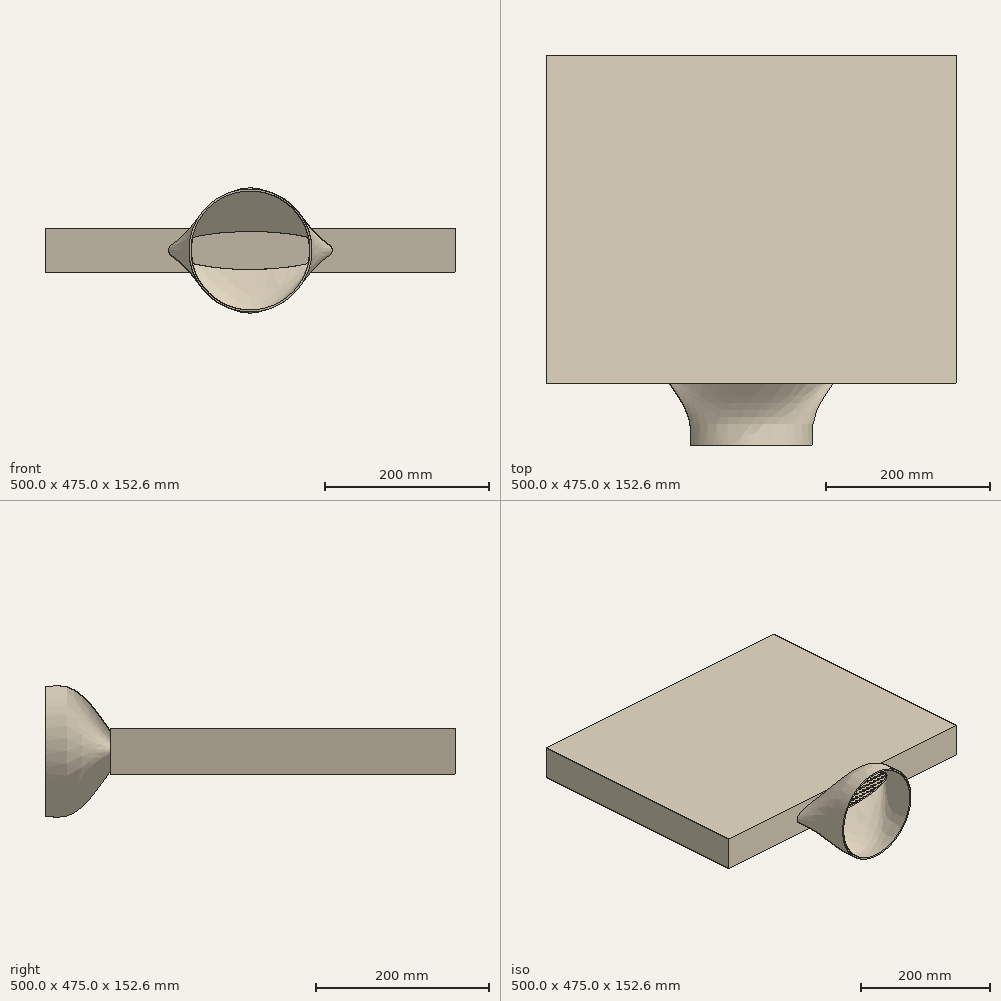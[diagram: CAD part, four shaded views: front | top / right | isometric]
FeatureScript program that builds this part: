
annotation { "Feature Type Name" : "Feature", "Feature Type Description" : "" }
export const myFeature = defineFeature(function(context is Context, id is Id, definition is map)
    precondition{}
    {
        {
            var Q0;
            Q0=qCreatedBy(makeId("Top.planeOp"),FACE);
            var sketch = newSketch(context, id + "F0", { "sketchPlane" : qUnion([Q0])});
            skLineSegment(sketch, "E0.bottom", {"start": v(-250, -200) * mm, "end": v(250, -200) * mm});
            skLineSegment(sketch, "E0.top", {"start": v(-250, 200) * mm, "end": v(250, 200) * mm});
            skLineSegment(sketch, "E0.left", {"start": v(-250, -200) * mm, "end": v(-250, 200) * mm});
            skLineSegment(sketch, "E0.right", {"start": v(250, -200) * mm, "end": v(250, 200) * mm});
            skPoint(sketch, "E0.middle", {"position": v(0, 0) * mm});
            skCircle(sketch, "E1", {"center": v(-243.5, 197) * mm, "radius": 2.5 * mm});
            skCircle(sketch, "E2.0.1.0", {"center": v(-243.5, 189) * mm, "radius": 2.5 * mm});
            skCircle(sketch, "E2.0.2.0", {"center": v(-243.5, 181) * mm, "radius": 2.5 * mm});
            skCircle(sketch, "E2.0.3.0", {"center": v(-243.5, 173) * mm, "radius": 2.5 * mm});
            skCircle(sketch, "E2.0.4.0", {"center": v(-243.5, 165) * mm, "radius": 2.5 * mm});
            skCircle(sketch, "E2.0.5.0", {"center": v(-243.5, 157) * mm, "radius": 2.5 * mm});
            skCircle(sketch, "E2.0.6.0", {"center": v(-243.5, 149) * mm, "radius": 2.5 * mm});
            skCircle(sketch, "E2.0.7.0", {"center": v(-243.5, 141) * mm, "radius": 2.5 * mm});
            skCircle(sketch, "E2.0.8.0", {"center": v(-243.5, 133) * mm, "radius": 2.5 * mm});
            skCircle(sketch, "E2.0.9.0", {"center": v(-243.5, 125) * mm, "radius": 2.5 * mm});
            skCircle(sketch, "E2.0.10.0", {"center": v(-243.5, 117) * mm, "radius": 2.5 * mm});
            skCircle(sketch, "E2.0.11.0", {"center": v(-243.5, 109) * mm, "radius": 2.5 * mm});
            skCircle(sketch, "E2.0.12.0", {"center": v(-243.5, 101) * mm, "radius": 2.5 * mm});
            skCircle(sketch, "E2.0.13.0", {"center": v(-243.5, 93) * mm, "radius": 2.5 * mm});
            skCircle(sketch, "E2.0.14.0", {"center": v(-243.5, 85) * mm, "radius": 2.5 * mm});
            skCircle(sketch, "E2.0.15.0", {"center": v(-243.5, 77) * mm, "radius": 2.5 * mm});
            skCircle(sketch, "E2.0.16.0", {"center": v(-243.5, 69) * mm, "radius": 2.5 * mm});
            skCircle(sketch, "E2.0.17.0", {"center": v(-243.5, 61) * mm, "radius": 2.5 * mm});
            skCircle(sketch, "E2.0.18.0", {"center": v(-243.5, 53) * mm, "radius": 2.5 * mm});
            skCircle(sketch, "E2.0.19.0", {"center": v(-243.5, 45) * mm, "radius": 2.5 * mm});
            skCircle(sketch, "E2.0.20.0", {"center": v(-243.5, 37) * mm, "radius": 2.5 * mm});
            skCircle(sketch, "E2.0.21.0", {"center": v(-243.5, 29) * mm, "radius": 2.5 * mm});
            skCircle(sketch, "E2.0.22.0", {"center": v(-243.5, 21) * mm, "radius": 2.5 * mm});
            skCircle(sketch, "E2.0.23.0", {"center": v(-243.5, 13) * mm, "radius": 2.5 * mm});
            skCircle(sketch, "E2.0.24.0", {"center": v(-243.5, 5) * mm, "radius": 2.5 * mm});
            skCircle(sketch, "E2.0.25.0", {"center": v(-243.5, -3) * mm, "radius": 2.5 * mm});
            skCircle(sketch, "E2.0.26.0", {"center": v(-243.5, -11) * mm, "radius": 2.5 * mm});
            skCircle(sketch, "E2.0.27.0", {"center": v(-243.5, -19) * mm, "radius": 2.5 * mm});
            skCircle(sketch, "E2.0.28.0", {"center": v(-243.5, -27) * mm, "radius": 2.5 * mm});
            skCircle(sketch, "E2.0.29.0", {"center": v(-243.5, -35) * mm, "radius": 2.5 * mm});
            skCircle(sketch, "E2.0.30.0", {"center": v(-243.5, -43) * mm, "radius": 2.5 * mm});
            skCircle(sketch, "E2.0.31.0", {"center": v(-243.5, -51) * mm, "radius": 2.5 * mm});
            skCircle(sketch, "E2.0.32.0", {"center": v(-243.5, -59) * mm, "radius": 2.5 * mm});
            skCircle(sketch, "E2.0.33.0", {"center": v(-243.5, -67) * mm, "radius": 2.5 * mm});
            skCircle(sketch, "E2.0.34.0", {"center": v(-243.5, -75) * mm, "radius": 2.5 * mm});
            skCircle(sketch, "E2.0.35.0", {"center": v(-243.5, -83) * mm, "radius": 2.5 * mm});
            skCircle(sketch, "E2.0.36.0", {"center": v(-243.5, -91) * mm, "radius": 2.5 * mm});
            skCircle(sketch, "E2.0.37.0", {"center": v(-243.5, -99) * mm, "radius": 2.5 * mm});
            skCircle(sketch, "E2.0.38.0", {"center": v(-243.5, -107) * mm, "radius": 2.5 * mm});
            skCircle(sketch, "E2.0.39.0", {"center": v(-243.5, -115) * mm, "radius": 2.5 * mm});
            skCircle(sketch, "E2.0.40.0", {"center": v(-243.5, -123) * mm, "radius": 2.5 * mm});
            skCircle(sketch, "E2.0.41.0", {"center": v(-243.5, -131) * mm, "radius": 2.5 * mm});
            skCircle(sketch, "E2.0.42.0", {"center": v(-243.5, -139) * mm, "radius": 2.5 * mm});
            skCircle(sketch, "E2.0.43.0", {"center": v(-243.5, -147) * mm, "radius": 2.5 * mm});
            skCircle(sketch, "E2.0.44.0", {"center": v(-243.5, -155) * mm, "radius": 2.5 * mm});
            skCircle(sketch, "E2.0.45.0", {"center": v(-243.5, -163) * mm, "radius": 2.5 * mm});
            skCircle(sketch, "E2.0.46.0", {"center": v(-243.5, -171) * mm, "radius": 2.5 * mm});
            skCircle(sketch, "E2.0.47.0", {"center": v(-243.5, -179) * mm, "radius": 2.5 * mm});
            skCircle(sketch, "E2.0.48.0", {"center": v(-243.5, -187) * mm, "radius": 2.5 * mm});
            skCircle(sketch, "E2.0.49.0", {"center": v(-243.5, -195) * mm, "radius": 2.5 * mm});
            skCircle(sketch, "E2.1.0.0", {"center": v(-235.5, 197) * mm, "radius": 2.5 * mm});
            skCircle(sketch, "E2.1.1.0", {"center": v(-235.5, 189) * mm, "radius": 2.5 * mm});
            skCircle(sketch, "E2.1.2.0", {"center": v(-235.5, 181) * mm, "radius": 2.5 * mm});
            skCircle(sketch, "E2.1.3.0", {"center": v(-235.5, 173) * mm, "radius": 2.5 * mm});
            skCircle(sketch, "E2.1.4.0", {"center": v(-235.5, 165) * mm, "radius": 2.5 * mm});
            skCircle(sketch, "E2.1.5.0", {"center": v(-235.5, 157) * mm, "radius": 2.5 * mm});
            skCircle(sketch, "E2.1.6.0", {"center": v(-235.5, 149) * mm, "radius": 2.5 * mm});
            skCircle(sketch, "E2.1.7.0", {"center": v(-235.5, 141) * mm, "radius": 2.5 * mm});
            skCircle(sketch, "E2.1.8.0", {"center": v(-235.5, 133) * mm, "radius": 2.5 * mm});
            skCircle(sketch, "E2.1.9.0", {"center": v(-235.5, 125) * mm, "radius": 2.5 * mm});
            skCircle(sketch, "E2.1.10.0", {"center": v(-235.5, 117) * mm, "radius": 2.5 * mm});
            skCircle(sketch, "E2.1.11.0", {"center": v(-235.5, 109) * mm, "radius": 2.5 * mm});
            skCircle(sketch, "E2.1.12.0", {"center": v(-235.5, 101) * mm, "radius": 2.5 * mm});
            skCircle(sketch, "E2.1.13.0", {"center": v(-235.5, 93) * mm, "radius": 2.5 * mm});
            skCircle(sketch, "E2.1.14.0", {"center": v(-235.5, 85) * mm, "radius": 2.5 * mm});
            skCircle(sketch, "E2.1.15.0", {"center": v(-235.5, 77) * mm, "radius": 2.5 * mm});
            skCircle(sketch, "E2.1.16.0", {"center": v(-235.5, 69) * mm, "radius": 2.5 * mm});
            skCircle(sketch, "E2.1.17.0", {"center": v(-235.5, 61) * mm, "radius": 2.5 * mm});
            skCircle(sketch, "E2.1.18.0", {"center": v(-235.5, 53) * mm, "radius": 2.5 * mm});
            skCircle(sketch, "E2.1.19.0", {"center": v(-235.5, 45) * mm, "radius": 2.5 * mm});
            skCircle(sketch, "E2.1.20.0", {"center": v(-235.5, 37) * mm, "radius": 2.5 * mm});
            skCircle(sketch, "E2.1.21.0", {"center": v(-235.5, 29) * mm, "radius": 2.5 * mm});
            skCircle(sketch, "E2.1.22.0", {"center": v(-235.5, 21) * mm, "radius": 2.5 * mm});
            skCircle(sketch, "E2.1.23.0", {"center": v(-235.5, 13) * mm, "radius": 2.5 * mm});
            skCircle(sketch, "E2.1.24.0", {"center": v(-235.5, 5) * mm, "radius": 2.5 * mm});
            skCircle(sketch, "E2.1.25.0", {"center": v(-235.5, -3) * mm, "radius": 2.5 * mm});
            skCircle(sketch, "E2.1.26.0", {"center": v(-235.5, -11) * mm, "radius": 2.5 * mm});
            skCircle(sketch, "E2.1.27.0", {"center": v(-235.5, -19) * mm, "radius": 2.5 * mm});
            skCircle(sketch, "E2.1.28.0", {"center": v(-235.5, -27) * mm, "radius": 2.5 * mm});
            skCircle(sketch, "E2.1.29.0", {"center": v(-235.5, -35) * mm, "radius": 2.5 * mm});
            skCircle(sketch, "E2.1.30.0", {"center": v(-235.5, -43) * mm, "radius": 2.5 * mm});
            skCircle(sketch, "E2.1.31.0", {"center": v(-235.5, -51) * mm, "radius": 2.5 * mm});
            skCircle(sketch, "E2.1.32.0", {"center": v(-235.5, -59) * mm, "radius": 2.5 * mm});
            skCircle(sketch, "E2.1.33.0", {"center": v(-235.5, -67) * mm, "radius": 2.5 * mm});
            skCircle(sketch, "E2.1.34.0", {"center": v(-235.5, -75) * mm, "radius": 2.5 * mm});
            skCircle(sketch, "E2.1.35.0", {"center": v(-235.5, -83) * mm, "radius": 2.5 * mm});
            skCircle(sketch, "E2.1.36.0", {"center": v(-235.5, -91) * mm, "radius": 2.5 * mm});
            skCircle(sketch, "E2.1.37.0", {"center": v(-235.5, -99) * mm, "radius": 2.5 * mm});
            skCircle(sketch, "E2.1.38.0", {"center": v(-235.5, -107) * mm, "radius": 2.5 * mm});
            skCircle(sketch, "E2.1.39.0", {"center": v(-235.5, -115) * mm, "radius": 2.5 * mm});
            skCircle(sketch, "E2.1.40.0", {"center": v(-235.5, -123) * mm, "radius": 2.5 * mm});
            skCircle(sketch, "E2.1.41.0", {"center": v(-235.5, -131) * mm, "radius": 2.5 * mm});
            skCircle(sketch, "E2.1.42.0", {"center": v(-235.5, -139) * mm, "radius": 2.5 * mm});
            skCircle(sketch, "E2.1.43.0", {"center": v(-235.5, -147) * mm, "radius": 2.5 * mm});
            skCircle(sketch, "E2.1.44.0", {"center": v(-235.5, -155) * mm, "radius": 2.5 * mm});
            skCircle(sketch, "E2.1.45.0", {"center": v(-235.5, -163) * mm, "radius": 2.5 * mm});
            skCircle(sketch, "E2.1.46.0", {"center": v(-235.5, -171) * mm, "radius": 2.5 * mm});
            skCircle(sketch, "E2.1.47.0", {"center": v(-235.5, -179) * mm, "radius": 2.5 * mm});
            skCircle(sketch, "E2.1.48.0", {"center": v(-235.5, -187) * mm, "radius": 2.5 * mm});
            skCircle(sketch, "E2.1.49.0", {"center": v(-235.5, -195) * mm, "radius": 2.5 * mm});
            skCircle(sketch, "E2.2.0.0", {"center": v(-227.5, 197) * mm, "radius": 2.5 * mm});
            skCircle(sketch, "E2.2.1.0", {"center": v(-227.5, 189) * mm, "radius": 2.5 * mm});
            skCircle(sketch, "E2.2.2.0", {"center": v(-227.5, 181) * mm, "radius": 2.5 * mm});
            skCircle(sketch, "E2.2.3.0", {"center": v(-227.5, 173) * mm, "radius": 2.5 * mm});
            skCircle(sketch, "E2.2.4.0", {"center": v(-227.5, 165) * mm, "radius": 2.5 * mm});
            skCircle(sketch, "E2.2.5.0", {"center": v(-227.5, 157) * mm, "radius": 2.5 * mm});
            skCircle(sketch, "E2.2.6.0", {"center": v(-227.5, 149) * mm, "radius": 2.5 * mm});
            skCircle(sketch, "E2.2.7.0", {"center": v(-227.5, 141) * mm, "radius": 2.5 * mm});
            skCircle(sketch, "E2.2.8.0", {"center": v(-227.5, 133) * mm, "radius": 2.5 * mm});
            skCircle(sketch, "E2.2.9.0", {"center": v(-227.5, 125) * mm, "radius": 2.5 * mm});
            skCircle(sketch, "E2.2.10.0", {"center": v(-227.5, 117) * mm, "radius": 2.5 * mm});
            skCircle(sketch, "E2.2.11.0", {"center": v(-227.5, 109) * mm, "radius": 2.5 * mm});
            skCircle(sketch, "E2.2.12.0", {"center": v(-227.5, 101) * mm, "radius": 2.5 * mm});
            skCircle(sketch, "E2.2.13.0", {"center": v(-227.5, 93) * mm, "radius": 2.5 * mm});
            skCircle(sketch, "E2.2.14.0", {"center": v(-227.5, 85) * mm, "radius": 2.5 * mm});
            skCircle(sketch, "E2.2.15.0", {"center": v(-227.5, 77) * mm, "radius": 2.5 * mm});
            skCircle(sketch, "E2.2.16.0", {"center": v(-227.5, 69) * mm, "radius": 2.5 * mm});
            skCircle(sketch, "E2.2.17.0", {"center": v(-227.5, 61) * mm, "radius": 2.5 * mm});
            skCircle(sketch, "E2.2.18.0", {"center": v(-227.5, 53) * mm, "radius": 2.5 * mm});
            skCircle(sketch, "E2.2.19.0", {"center": v(-227.5, 45) * mm, "radius": 2.5 * mm});
            skCircle(sketch, "E2.2.20.0", {"center": v(-227.5, 37) * mm, "radius": 2.5 * mm});
            skCircle(sketch, "E2.2.21.0", {"center": v(-227.5, 29) * mm, "radius": 2.5 * mm});
            skCircle(sketch, "E2.2.22.0", {"center": v(-227.5, 21) * mm, "radius": 2.5 * mm});
            skCircle(sketch, "E2.2.23.0", {"center": v(-227.5, 13) * mm, "radius": 2.5 * mm});
            skCircle(sketch, "E2.2.24.0", {"center": v(-227.5, 5) * mm, "radius": 2.5 * mm});
            skCircle(sketch, "E2.2.25.0", {"center": v(-227.5, -3) * mm, "radius": 2.5 * mm});
            skCircle(sketch, "E2.2.26.0", {"center": v(-227.5, -11) * mm, "radius": 2.5 * mm});
            skCircle(sketch, "E2.2.27.0", {"center": v(-227.5, -19) * mm, "radius": 2.5 * mm});
            skCircle(sketch, "E2.2.28.0", {"center": v(-227.5, -27) * mm, "radius": 2.5 * mm});
            skCircle(sketch, "E2.2.29.0", {"center": v(-227.5, -35) * mm, "radius": 2.5 * mm});
            skCircle(sketch, "E2.2.30.0", {"center": v(-227.5, -43) * mm, "radius": 2.5 * mm});
            skCircle(sketch, "E2.2.31.0", {"center": v(-227.5, -51) * mm, "radius": 2.5 * mm});
            skCircle(sketch, "E2.2.32.0", {"center": v(-227.5, -59) * mm, "radius": 2.5 * mm});
            skCircle(sketch, "E2.2.33.0", {"center": v(-227.5, -67) * mm, "radius": 2.5 * mm});
            skCircle(sketch, "E2.2.34.0", {"center": v(-227.5, -75) * mm, "radius": 2.5 * mm});
            skCircle(sketch, "E2.2.35.0", {"center": v(-227.5, -83) * mm, "radius": 2.5 * mm});
            skCircle(sketch, "E2.2.36.0", {"center": v(-227.5, -91) * mm, "radius": 2.5 * mm});
            skCircle(sketch, "E2.2.37.0", {"center": v(-227.5, -99) * mm, "radius": 2.5 * mm});
            skCircle(sketch, "E2.2.38.0", {"center": v(-227.5, -107) * mm, "radius": 2.5 * mm});
            skCircle(sketch, "E2.2.39.0", {"center": v(-227.5, -115) * mm, "radius": 2.5 * mm});
            skCircle(sketch, "E2.2.40.0", {"center": v(-227.5, -123) * mm, "radius": 2.5 * mm});
            skCircle(sketch, "E2.2.41.0", {"center": v(-227.5, -131) * mm, "radius": 2.5 * mm});
            skCircle(sketch, "E2.2.42.0", {"center": v(-227.5, -139) * mm, "radius": 2.5 * mm});
            skCircle(sketch, "E2.2.43.0", {"center": v(-227.5, -147) * mm, "radius": 2.5 * mm});
            skCircle(sketch, "E2.2.44.0", {"center": v(-227.5, -155) * mm, "radius": 2.5 * mm});
            skCircle(sketch, "E2.2.45.0", {"center": v(-227.5, -163) * mm, "radius": 2.5 * mm});
            skCircle(sketch, "E2.2.46.0", {"center": v(-227.5, -171) * mm, "radius": 2.5 * mm});
            skCircle(sketch, "E2.2.47.0", {"center": v(-227.5, -179) * mm, "radius": 2.5 * mm});
            skCircle(sketch, "E2.2.48.0", {"center": v(-227.5, -187) * mm, "radius": 2.5 * mm});
            skCircle(sketch, "E2.2.49.0", {"center": v(-227.5, -195) * mm, "radius": 2.5 * mm});
            skCircle(sketch, "E2.3.0.0", {"center": v(-219.5, 197) * mm, "radius": 2.5 * mm});
            skCircle(sketch, "E2.3.1.0", {"center": v(-219.5, 189) * mm, "radius": 2.5 * mm});
            skCircle(sketch, "E2.3.2.0", {"center": v(-219.5, 181) * mm, "radius": 2.5 * mm});
            skCircle(sketch, "E2.3.3.0", {"center": v(-219.5, 173) * mm, "radius": 2.5 * mm});
            skCircle(sketch, "E2.3.4.0", {"center": v(-219.5, 165) * mm, "radius": 2.5 * mm});
            skCircle(sketch, "E2.3.5.0", {"center": v(-219.5, 157) * mm, "radius": 2.5 * mm});
            skCircle(sketch, "E2.3.6.0", {"center": v(-219.5, 149) * mm, "radius": 2.5 * mm});
            skCircle(sketch, "E2.3.7.0", {"center": v(-219.5, 141) * mm, "radius": 2.5 * mm});
            skCircle(sketch, "E2.3.8.0", {"center": v(-219.5, 133) * mm, "radius": 2.5 * mm});
            skCircle(sketch, "E2.3.9.0", {"center": v(-219.5, 125) * mm, "radius": 2.5 * mm});
            skCircle(sketch, "E2.3.10.0", {"center": v(-219.5, 117) * mm, "radius": 2.5 * mm});
            skCircle(sketch, "E2.3.11.0", {"center": v(-219.5, 109) * mm, "radius": 2.5 * mm});
            skCircle(sketch, "E2.3.12.0", {"center": v(-219.5, 101) * mm, "radius": 2.5 * mm});
            skCircle(sketch, "E2.3.13.0", {"center": v(-219.5, 93) * mm, "radius": 2.5 * mm});
            skCircle(sketch, "E2.3.14.0", {"center": v(-219.5, 85) * mm, "radius": 2.5 * mm});
            skCircle(sketch, "E2.3.15.0", {"center": v(-219.5, 77) * mm, "radius": 2.5 * mm});
            skCircle(sketch, "E2.3.16.0", {"center": v(-219.5, 69) * mm, "radius": 2.5 * mm});
            skCircle(sketch, "E2.3.17.0", {"center": v(-219.5, 61) * mm, "radius": 2.5 * mm});
            skCircle(sketch, "E2.3.18.0", {"center": v(-219.5, 53) * mm, "radius": 2.5 * mm});
            skCircle(sketch, "E2.3.19.0", {"center": v(-219.5, 45) * mm, "radius": 2.5 * mm});
            skCircle(sketch, "E2.3.20.0", {"center": v(-219.5, 37) * mm, "radius": 2.5 * mm});
            skCircle(sketch, "E2.3.21.0", {"center": v(-219.5, 29) * mm, "radius": 2.5 * mm});
            skCircle(sketch, "E2.3.22.0", {"center": v(-219.5, 21) * mm, "radius": 2.5 * mm});
            skCircle(sketch, "E2.3.23.0", {"center": v(-219.5, 13) * mm, "radius": 2.5 * mm});
            skCircle(sketch, "E2.3.24.0", {"center": v(-219.5, 5) * mm, "radius": 2.5 * mm});
            skCircle(sketch, "E2.3.25.0", {"center": v(-219.5, -3) * mm, "radius": 2.5 * mm});
            skCircle(sketch, "E2.3.26.0", {"center": v(-219.5, -11) * mm, "radius": 2.5 * mm});
            skCircle(sketch, "E2.3.27.0", {"center": v(-219.5, -19) * mm, "radius": 2.5 * mm});
            skCircle(sketch, "E2.3.28.0", {"center": v(-219.5, -27) * mm, "radius": 2.5 * mm});
            skCircle(sketch, "E2.3.29.0", {"center": v(-219.5, -35) * mm, "radius": 2.5 * mm});
            skCircle(sketch, "E2.3.30.0", {"center": v(-219.5, -43) * mm, "radius": 2.5 * mm});
            skCircle(sketch, "E2.3.31.0", {"center": v(-219.5, -51) * mm, "radius": 2.5 * mm});
            skCircle(sketch, "E2.3.32.0", {"center": v(-219.5, -59) * mm, "radius": 2.5 * mm});
            skCircle(sketch, "E2.3.33.0", {"center": v(-219.5, -67) * mm, "radius": 2.5 * mm});
            skCircle(sketch, "E2.3.34.0", {"center": v(-219.5, -75) * mm, "radius": 2.5 * mm});
            skCircle(sketch, "E2.3.35.0", {"center": v(-219.5, -83) * mm, "radius": 2.5 * mm});
            skCircle(sketch, "E2.3.36.0", {"center": v(-219.5, -91) * mm, "radius": 2.5 * mm});
            skCircle(sketch, "E2.3.37.0", {"center": v(-219.5, -99) * mm, "radius": 2.5 * mm});
            skCircle(sketch, "E2.3.38.0", {"center": v(-219.5, -107) * mm, "radius": 2.5 * mm});
            skCircle(sketch, "E2.3.39.0", {"center": v(-219.5, -115) * mm, "radius": 2.5 * mm});
            skCircle(sketch, "E2.3.40.0", {"center": v(-219.5, -123) * mm, "radius": 2.5 * mm});
            skCircle(sketch, "E2.3.41.0", {"center": v(-219.5, -131) * mm, "radius": 2.5 * mm});
            skCircle(sketch, "E2.3.42.0", {"center": v(-219.5, -139) * mm, "radius": 2.5 * mm});
            skCircle(sketch, "E2.3.43.0", {"center": v(-219.5, -147) * mm, "radius": 2.5 * mm});
            skCircle(sketch, "E2.3.44.0", {"center": v(-219.5, -155) * mm, "radius": 2.5 * mm});
            skCircle(sketch, "E2.3.45.0", {"center": v(-219.5, -163) * mm, "radius": 2.5 * mm});
            skCircle(sketch, "E2.3.46.0", {"center": v(-219.5, -171) * mm, "radius": 2.5 * mm});
            skCircle(sketch, "E2.3.47.0", {"center": v(-219.5, -179) * mm, "radius": 2.5 * mm});
            skCircle(sketch, "E2.3.48.0", {"center": v(-219.5, -187) * mm, "radius": 2.5 * mm});
            skCircle(sketch, "E2.3.49.0", {"center": v(-219.5, -195) * mm, "radius": 2.5 * mm});
            skCircle(sketch, "E2.4.0.0", {"center": v(-211.5, 197) * mm, "radius": 2.5 * mm});
            skCircle(sketch, "E2.4.1.0", {"center": v(-211.5, 189) * mm, "radius": 2.5 * mm});
            skCircle(sketch, "E2.4.2.0", {"center": v(-211.5, 181) * mm, "radius": 2.5 * mm});
            skCircle(sketch, "E2.4.3.0", {"center": v(-211.5, 173) * mm, "radius": 2.5 * mm});
            skCircle(sketch, "E2.4.4.0", {"center": v(-211.5, 165) * mm, "radius": 2.5 * mm});
            skCircle(sketch, "E2.4.5.0", {"center": v(-211.5, 157) * mm, "radius": 2.5 * mm});
            skCircle(sketch, "E2.4.6.0", {"center": v(-211.5, 149) * mm, "radius": 2.5 * mm});
            skCircle(sketch, "E2.4.7.0", {"center": v(-211.5, 141) * mm, "radius": 2.5 * mm});
            skCircle(sketch, "E2.4.8.0", {"center": v(-211.5, 133) * mm, "radius": 2.5 * mm});
            skCircle(sketch, "E2.4.9.0", {"center": v(-211.5, 125) * mm, "radius": 2.5 * mm});
            skCircle(sketch, "E2.4.10.0", {"center": v(-211.5, 117) * mm, "radius": 2.5 * mm});
            skCircle(sketch, "E2.4.11.0", {"center": v(-211.5, 109) * mm, "radius": 2.5 * mm});
            skCircle(sketch, "E2.4.12.0", {"center": v(-211.5, 101) * mm, "radius": 2.5 * mm});
            skCircle(sketch, "E2.4.13.0", {"center": v(-211.5, 93) * mm, "radius": 2.5 * mm});
            skCircle(sketch, "E2.4.14.0", {"center": v(-211.5, 85) * mm, "radius": 2.5 * mm});
            skCircle(sketch, "E2.4.15.0", {"center": v(-211.5, 77) * mm, "radius": 2.5 * mm});
            skCircle(sketch, "E2.4.16.0", {"center": v(-211.5, 69) * mm, "radius": 2.5 * mm});
            skCircle(sketch, "E2.4.17.0", {"center": v(-211.5, 61) * mm, "radius": 2.5 * mm});
            skCircle(sketch, "E2.4.18.0", {"center": v(-211.5, 53) * mm, "radius": 2.5 * mm});
            skCircle(sketch, "E2.4.19.0", {"center": v(-211.5, 45) * mm, "radius": 2.5 * mm});
            skCircle(sketch, "E2.4.20.0", {"center": v(-211.5, 37) * mm, "radius": 2.5 * mm});
            skCircle(sketch, "E2.4.21.0", {"center": v(-211.5, 29) * mm, "radius": 2.5 * mm});
            skCircle(sketch, "E2.4.22.0", {"center": v(-211.5, 21) * mm, "radius": 2.5 * mm});
            skCircle(sketch, "E2.4.23.0", {"center": v(-211.5, 13) * mm, "radius": 2.5 * mm});
            skCircle(sketch, "E2.4.24.0", {"center": v(-211.5, 5) * mm, "radius": 2.5 * mm});
            skCircle(sketch, "E2.4.25.0", {"center": v(-211.5, -3) * mm, "radius": 2.5 * mm});
            skCircle(sketch, "E2.4.26.0", {"center": v(-211.5, -11) * mm, "radius": 2.5 * mm});
            skCircle(sketch, "E2.4.27.0", {"center": v(-211.5, -19) * mm, "radius": 2.5 * mm});
            skCircle(sketch, "E2.4.28.0", {"center": v(-211.5, -27) * mm, "radius": 2.5 * mm});
            skCircle(sketch, "E2.4.29.0", {"center": v(-211.5, -35) * mm, "radius": 2.5 * mm});
            skCircle(sketch, "E2.4.30.0", {"center": v(-211.5, -43) * mm, "radius": 2.5 * mm});
            skCircle(sketch, "E2.4.31.0", {"center": v(-211.5, -51) * mm, "radius": 2.5 * mm});
            skCircle(sketch, "E2.4.32.0", {"center": v(-211.5, -59) * mm, "radius": 2.5 * mm});
            skCircle(sketch, "E2.4.33.0", {"center": v(-211.5, -67) * mm, "radius": 2.5 * mm});
            skCircle(sketch, "E2.4.34.0", {"center": v(-211.5, -75) * mm, "radius": 2.5 * mm});
            skCircle(sketch, "E2.4.35.0", {"center": v(-211.5, -83) * mm, "radius": 2.5 * mm});
            skCircle(sketch, "E2.4.36.0", {"center": v(-211.5, -91) * mm, "radius": 2.5 * mm});
            skCircle(sketch, "E2.4.37.0", {"center": v(-211.5, -99) * mm, "radius": 2.5 * mm});
            skCircle(sketch, "E2.4.38.0", {"center": v(-211.5, -107) * mm, "radius": 2.5 * mm});
            skCircle(sketch, "E2.4.39.0", {"center": v(-211.5, -115) * mm, "radius": 2.5 * mm});
            skCircle(sketch, "E2.4.40.0", {"center": v(-211.5, -123) * mm, "radius": 2.5 * mm});
            skCircle(sketch, "E2.4.41.0", {"center": v(-211.5, -131) * mm, "radius": 2.5 * mm});
            skCircle(sketch, "E2.4.42.0", {"center": v(-211.5, -139) * mm, "radius": 2.5 * mm});
            skCircle(sketch, "E2.4.43.0", {"center": v(-211.5, -147) * mm, "radius": 2.5 * mm});
            skCircle(sketch, "E2.4.44.0", {"center": v(-211.5, -155) * mm, "radius": 2.5 * mm});
            skCircle(sketch, "E2.4.45.0", {"center": v(-211.5, -163) * mm, "radius": 2.5 * mm});
            skCircle(sketch, "E2.4.46.0", {"center": v(-211.5, -171) * mm, "radius": 2.5 * mm});
            skCircle(sketch, "E2.4.47.0", {"center": v(-211.5, -179) * mm, "radius": 2.5 * mm});
            skCircle(sketch, "E2.4.48.0", {"center": v(-211.5, -187) * mm, "radius": 2.5 * mm});
            skCircle(sketch, "E2.4.49.0", {"center": v(-211.5, -195) * mm, "radius": 2.5 * mm});
            skCircle(sketch, "E2.5.0.0", {"center": v(-203.5, 197) * mm, "radius": 2.5 * mm});
            skCircle(sketch, "E2.5.1.0", {"center": v(-203.5, 189) * mm, "radius": 2.5 * mm});
            skCircle(sketch, "E2.5.2.0", {"center": v(-203.5, 181) * mm, "radius": 2.5 * mm});
            skCircle(sketch, "E2.5.3.0", {"center": v(-203.5, 173) * mm, "radius": 2.5 * mm});
            skCircle(sketch, "E2.5.4.0", {"center": v(-203.5, 165) * mm, "radius": 2.5 * mm});
            skCircle(sketch, "E2.5.5.0", {"center": v(-203.5, 157) * mm, "radius": 2.5 * mm});
            skCircle(sketch, "E2.5.6.0", {"center": v(-203.5, 149) * mm, "radius": 2.5 * mm});
            skCircle(sketch, "E2.5.7.0", {"center": v(-203.5, 141) * mm, "radius": 2.5 * mm});
            skCircle(sketch, "E2.5.8.0", {"center": v(-203.5, 133) * mm, "radius": 2.5 * mm});
            skCircle(sketch, "E2.5.9.0", {"center": v(-203.5, 125) * mm, "radius": 2.5 * mm});
            skCircle(sketch, "E2.5.10.0", {"center": v(-203.5, 117) * mm, "radius": 2.5 * mm});
            skCircle(sketch, "E2.5.11.0", {"center": v(-203.5, 109) * mm, "radius": 2.5 * mm});
            skCircle(sketch, "E2.5.12.0", {"center": v(-203.5, 101) * mm, "radius": 2.5 * mm});
            skCircle(sketch, "E2.5.13.0", {"center": v(-203.5, 93) * mm, "radius": 2.5 * mm});
            skCircle(sketch, "E2.5.14.0", {"center": v(-203.5, 85) * mm, "radius": 2.5 * mm});
            skCircle(sketch, "E2.5.15.0", {"center": v(-203.5, 77) * mm, "radius": 2.5 * mm});
            skCircle(sketch, "E2.5.16.0", {"center": v(-203.5, 69) * mm, "radius": 2.5 * mm});
            skCircle(sketch, "E2.5.17.0", {"center": v(-203.5, 61) * mm, "radius": 2.5 * mm});
            skCircle(sketch, "E2.5.18.0", {"center": v(-203.5, 53) * mm, "radius": 2.5 * mm});
            skCircle(sketch, "E2.5.19.0", {"center": v(-203.5, 45) * mm, "radius": 2.5 * mm});
            skCircle(sketch, "E2.5.20.0", {"center": v(-203.5, 37) * mm, "radius": 2.5 * mm});
            skCircle(sketch, "E2.5.21.0", {"center": v(-203.5, 29) * mm, "radius": 2.5 * mm});
            skCircle(sketch, "E2.5.22.0", {"center": v(-203.5, 21) * mm, "radius": 2.5 * mm});
            skCircle(sketch, "E2.5.23.0", {"center": v(-203.5, 13) * mm, "radius": 2.5 * mm});
            skCircle(sketch, "E2.5.24.0", {"center": v(-203.5, 5) * mm, "radius": 2.5 * mm});
            skCircle(sketch, "E2.5.25.0", {"center": v(-203.5, -3) * mm, "radius": 2.5 * mm});
            skCircle(sketch, "E2.5.26.0", {"center": v(-203.5, -11) * mm, "radius": 2.5 * mm});
            skCircle(sketch, "E2.5.27.0", {"center": v(-203.5, -19) * mm, "radius": 2.5 * mm});
            skCircle(sketch, "E2.5.28.0", {"center": v(-203.5, -27) * mm, "radius": 2.5 * mm});
            skCircle(sketch, "E2.5.29.0", {"center": v(-203.5, -35) * mm, "radius": 2.5 * mm});
            skCircle(sketch, "E2.5.30.0", {"center": v(-203.5, -43) * mm, "radius": 2.5 * mm});
            skCircle(sketch, "E2.5.31.0", {"center": v(-203.5, -51) * mm, "radius": 2.5 * mm});
            skCircle(sketch, "E2.5.32.0", {"center": v(-203.5, -59) * mm, "radius": 2.5 * mm});
            skCircle(sketch, "E2.5.33.0", {"center": v(-203.5, -67) * mm, "radius": 2.5 * mm});
            skCircle(sketch, "E2.5.34.0", {"center": v(-203.5, -75) * mm, "radius": 2.5 * mm});
            skCircle(sketch, "E2.5.35.0", {"center": v(-203.5, -83) * mm, "radius": 2.5 * mm});
            skCircle(sketch, "E2.5.36.0", {"center": v(-203.5, -91) * mm, "radius": 2.5 * mm});
            skCircle(sketch, "E2.5.37.0", {"center": v(-203.5, -99) * mm, "radius": 2.5 * mm});
            skCircle(sketch, "E2.5.38.0", {"center": v(-203.5, -107) * mm, "radius": 2.5 * mm});
            skCircle(sketch, "E2.5.39.0", {"center": v(-203.5, -115) * mm, "radius": 2.5 * mm});
            skCircle(sketch, "E2.5.40.0", {"center": v(-203.5, -123) * mm, "radius": 2.5 * mm});
            skCircle(sketch, "E2.5.41.0", {"center": v(-203.5, -131) * mm, "radius": 2.5 * mm});
            skCircle(sketch, "E2.5.42.0", {"center": v(-203.5, -139) * mm, "radius": 2.5 * mm});
            skCircle(sketch, "E2.5.43.0", {"center": v(-203.5, -147) * mm, "radius": 2.5 * mm});
            skCircle(sketch, "E2.5.44.0", {"center": v(-203.5, -155) * mm, "radius": 2.5 * mm});
            skCircle(sketch, "E2.5.45.0", {"center": v(-203.5, -163) * mm, "radius": 2.5 * mm});
            skCircle(sketch, "E2.5.46.0", {"center": v(-203.5, -171) * mm, "radius": 2.5 * mm});
            skCircle(sketch, "E2.5.47.0", {"center": v(-203.5, -179) * mm, "radius": 2.5 * mm});
            skCircle(sketch, "E2.5.48.0", {"center": v(-203.5, -187) * mm, "radius": 2.5 * mm});
            skCircle(sketch, "E2.5.49.0", {"center": v(-203.5, -195) * mm, "radius": 2.5 * mm});
            skCircle(sketch, "E2.6.0.0", {"center": v(-195.5, 197) * mm, "radius": 2.5 * mm});
            skCircle(sketch, "E2.6.1.0", {"center": v(-195.5, 189) * mm, "radius": 2.5 * mm});
            skCircle(sketch, "E2.6.2.0", {"center": v(-195.5, 181) * mm, "radius": 2.5 * mm});
            skCircle(sketch, "E2.6.3.0", {"center": v(-195.5, 173) * mm, "radius": 2.5 * mm});
            skCircle(sketch, "E2.6.4.0", {"center": v(-195.5, 165) * mm, "radius": 2.5 * mm});
            skCircle(sketch, "E2.6.5.0", {"center": v(-195.5, 157) * mm, "radius": 2.5 * mm});
            skCircle(sketch, "E2.6.6.0", {"center": v(-195.5, 149) * mm, "radius": 2.5 * mm});
            skCircle(sketch, "E2.6.7.0", {"center": v(-195.5, 141) * mm, "radius": 2.5 * mm});
            skCircle(sketch, "E2.6.8.0", {"center": v(-195.5, 133) * mm, "radius": 2.5 * mm});
            skCircle(sketch, "E2.6.9.0", {"center": v(-195.5, 125) * mm, "radius": 2.5 * mm});
            skCircle(sketch, "E2.6.10.0", {"center": v(-195.5, 117) * mm, "radius": 2.5 * mm});
            skCircle(sketch, "E2.6.11.0", {"center": v(-195.5, 109) * mm, "radius": 2.5 * mm});
            skCircle(sketch, "E2.6.12.0", {"center": v(-195.5, 101) * mm, "radius": 2.5 * mm});
            skCircle(sketch, "E2.6.13.0", {"center": v(-195.5, 93) * mm, "radius": 2.5 * mm});
            skCircle(sketch, "E2.6.14.0", {"center": v(-195.5, 85) * mm, "radius": 2.5 * mm});
            skCircle(sketch, "E2.6.15.0", {"center": v(-195.5, 77) * mm, "radius": 2.5 * mm});
            skCircle(sketch, "E2.6.16.0", {"center": v(-195.5, 69) * mm, "radius": 2.5 * mm});
            skCircle(sketch, "E2.6.17.0", {"center": v(-195.5, 61) * mm, "radius": 2.5 * mm});
            skCircle(sketch, "E2.6.18.0", {"center": v(-195.5, 53) * mm, "radius": 2.5 * mm});
            skCircle(sketch, "E2.6.19.0", {"center": v(-195.5, 45) * mm, "radius": 2.5 * mm});
            skCircle(sketch, "E2.6.20.0", {"center": v(-195.5, 37) * mm, "radius": 2.5 * mm});
            skCircle(sketch, "E2.6.21.0", {"center": v(-195.5, 29) * mm, "radius": 2.5 * mm});
            skCircle(sketch, "E2.6.22.0", {"center": v(-195.5, 21) * mm, "radius": 2.5 * mm});
            skCircle(sketch, "E2.6.23.0", {"center": v(-195.5, 13) * mm, "radius": 2.5 * mm});
            skCircle(sketch, "E2.6.24.0", {"center": v(-195.5, 5) * mm, "radius": 2.5 * mm});
            skCircle(sketch, "E2.6.25.0", {"center": v(-195.5, -3) * mm, "radius": 2.5 * mm});
            skCircle(sketch, "E2.6.26.0", {"center": v(-195.5, -11) * mm, "radius": 2.5 * mm});
            skCircle(sketch, "E2.6.27.0", {"center": v(-195.5, -19) * mm, "radius": 2.5 * mm});
            skCircle(sketch, "E2.6.28.0", {"center": v(-195.5, -27) * mm, "radius": 2.5 * mm});
            skCircle(sketch, "E2.6.29.0", {"center": v(-195.5, -35) * mm, "radius": 2.5 * mm});
            skCircle(sketch, "E2.6.30.0", {"center": v(-195.5, -43) * mm, "radius": 2.5 * mm});
            skCircle(sketch, "E2.6.31.0", {"center": v(-195.5, -51) * mm, "radius": 2.5 * mm});
            skCircle(sketch, "E2.6.32.0", {"center": v(-195.5, -59) * mm, "radius": 2.5 * mm});
            skCircle(sketch, "E2.6.33.0", {"center": v(-195.5, -67) * mm, "radius": 2.5 * mm});
            skCircle(sketch, "E2.6.34.0", {"center": v(-195.5, -75) * mm, "radius": 2.5 * mm});
            skCircle(sketch, "E2.6.35.0", {"center": v(-195.5, -83) * mm, "radius": 2.5 * mm});
            skCircle(sketch, "E2.6.36.0", {"center": v(-195.5, -91) * mm, "radius": 2.5 * mm});
            skCircle(sketch, "E2.6.37.0", {"center": v(-195.5, -99) * mm, "radius": 2.5 * mm});
            skCircle(sketch, "E2.6.38.0", {"center": v(-195.5, -107) * mm, "radius": 2.5 * mm});
            skCircle(sketch, "E2.6.39.0", {"center": v(-195.5, -115) * mm, "radius": 2.5 * mm});
            skCircle(sketch, "E2.6.40.0", {"center": v(-195.5, -123) * mm, "radius": 2.5 * mm});
            skCircle(sketch, "E2.6.41.0", {"center": v(-195.5, -131) * mm, "radius": 2.5 * mm});
            skCircle(sketch, "E2.6.42.0", {"center": v(-195.5, -139) * mm, "radius": 2.5 * mm});
            skCircle(sketch, "E2.6.43.0", {"center": v(-195.5, -147) * mm, "radius": 2.5 * mm});
            skCircle(sketch, "E2.6.44.0", {"center": v(-195.5, -155) * mm, "radius": 2.5 * mm});
            skCircle(sketch, "E2.6.45.0", {"center": v(-195.5, -163) * mm, "radius": 2.5 * mm});
            skCircle(sketch, "E2.6.46.0", {"center": v(-195.5, -171) * mm, "radius": 2.5 * mm});
            skCircle(sketch, "E2.6.47.0", {"center": v(-195.5, -179) * mm, "radius": 2.5 * mm});
            skCircle(sketch, "E2.6.48.0", {"center": v(-195.5, -187) * mm, "radius": 2.5 * mm});
            skCircle(sketch, "E2.6.49.0", {"center": v(-195.5, -195) * mm, "radius": 2.5 * mm});
            skCircle(sketch, "E2.7.0.0", {"center": v(-187.5, 197) * mm, "radius": 2.5 * mm});
            skCircle(sketch, "E2.7.1.0", {"center": v(-187.5, 189) * mm, "radius": 2.5 * mm});
            skCircle(sketch, "E2.7.2.0", {"center": v(-187.5, 181) * mm, "radius": 2.5 * mm});
            skCircle(sketch, "E2.7.3.0", {"center": v(-187.5, 173) * mm, "radius": 2.5 * mm});
            skCircle(sketch, "E2.7.4.0", {"center": v(-187.5, 165) * mm, "radius": 2.5 * mm});
            skCircle(sketch, "E2.7.5.0", {"center": v(-187.5, 157) * mm, "radius": 2.5 * mm});
            skCircle(sketch, "E2.7.6.0", {"center": v(-187.5, 149) * mm, "radius": 2.5 * mm});
            skCircle(sketch, "E2.7.7.0", {"center": v(-187.5, 141) * mm, "radius": 2.5 * mm});
            skCircle(sketch, "E2.7.8.0", {"center": v(-187.5, 133) * mm, "radius": 2.5 * mm});
            skCircle(sketch, "E2.7.9.0", {"center": v(-187.5, 125) * mm, "radius": 2.5 * mm});
            skCircle(sketch, "E2.7.10.0", {"center": v(-187.5, 117) * mm, "radius": 2.5 * mm});
            skCircle(sketch, "E2.7.11.0", {"center": v(-187.5, 109) * mm, "radius": 2.5 * mm});
            skCircle(sketch, "E2.7.12.0", {"center": v(-187.5, 101) * mm, "radius": 2.5 * mm});
            skCircle(sketch, "E2.7.13.0", {"center": v(-187.5, 93) * mm, "radius": 2.5 * mm});
            skCircle(sketch, "E2.7.14.0", {"center": v(-187.5, 85) * mm, "radius": 2.5 * mm});
            skCircle(sketch, "E2.7.15.0", {"center": v(-187.5, 77) * mm, "radius": 2.5 * mm});
            skCircle(sketch, "E2.7.16.0", {"center": v(-187.5, 69) * mm, "radius": 2.5 * mm});
            skCircle(sketch, "E2.7.17.0", {"center": v(-187.5, 61) * mm, "radius": 2.5 * mm});
            skCircle(sketch, "E2.7.18.0", {"center": v(-187.5, 53) * mm, "radius": 2.5 * mm});
            skCircle(sketch, "E2.7.19.0", {"center": v(-187.5, 45) * mm, "radius": 2.5 * mm});
            skCircle(sketch, "E2.7.20.0", {"center": v(-187.5, 37) * mm, "radius": 2.5 * mm});
            skCircle(sketch, "E2.7.21.0", {"center": v(-187.5, 29) * mm, "radius": 2.5 * mm});
            skCircle(sketch, "E2.7.22.0", {"center": v(-187.5, 21) * mm, "radius": 2.5 * mm});
            skCircle(sketch, "E2.7.23.0", {"center": v(-187.5, 13) * mm, "radius": 2.5 * mm});
            skCircle(sketch, "E2.7.24.0", {"center": v(-187.5, 5) * mm, "radius": 2.5 * mm});
            skCircle(sketch, "E2.7.25.0", {"center": v(-187.5, -3) * mm, "radius": 2.5 * mm});
            skCircle(sketch, "E2.7.26.0", {"center": v(-187.5, -11) * mm, "radius": 2.5 * mm});
            skCircle(sketch, "E2.7.27.0", {"center": v(-187.5, -19) * mm, "radius": 2.5 * mm});
            skCircle(sketch, "E2.7.28.0", {"center": v(-187.5, -27) * mm, "radius": 2.5 * mm});
            skCircle(sketch, "E2.7.29.0", {"center": v(-187.5, -35) * mm, "radius": 2.5 * mm});
            skCircle(sketch, "E2.7.30.0", {"center": v(-187.5, -43) * mm, "radius": 2.5 * mm});
            skCircle(sketch, "E2.7.31.0", {"center": v(-187.5, -51) * mm, "radius": 2.5 * mm});
            skCircle(sketch, "E2.7.32.0", {"center": v(-187.5, -59) * mm, "radius": 2.5 * mm});
            skCircle(sketch, "E2.7.33.0", {"center": v(-187.5, -67) * mm, "radius": 2.5 * mm});
            skCircle(sketch, "E2.7.34.0", {"center": v(-187.5, -75) * mm, "radius": 2.5 * mm});
            skCircle(sketch, "E2.7.35.0", {"center": v(-187.5, -83) * mm, "radius": 2.5 * mm});
            skCircle(sketch, "E2.7.36.0", {"center": v(-187.5, -91) * mm, "radius": 2.5 * mm});
            skCircle(sketch, "E2.7.37.0", {"center": v(-187.5, -99) * mm, "radius": 2.5 * mm});
            skCircle(sketch, "E2.7.38.0", {"center": v(-187.5, -107) * mm, "radius": 2.5 * mm});
            skCircle(sketch, "E2.7.39.0", {"center": v(-187.5, -115) * mm, "radius": 2.5 * mm});
            skCircle(sketch, "E2.7.40.0", {"center": v(-187.5, -123) * mm, "radius": 2.5 * mm});
            skCircle(sketch, "E2.7.41.0", {"center": v(-187.5, -131) * mm, "radius": 2.5 * mm});
            skCircle(sketch, "E2.7.42.0", {"center": v(-187.5, -139) * mm, "radius": 2.5 * mm});
            skCircle(sketch, "E2.7.43.0", {"center": v(-187.5, -147) * mm, "radius": 2.5 * mm});
            skCircle(sketch, "E2.7.44.0", {"center": v(-187.5, -155) * mm, "radius": 2.5 * mm});
            skCircle(sketch, "E2.7.45.0", {"center": v(-187.5, -163) * mm, "radius": 2.5 * mm});
            skCircle(sketch, "E2.7.46.0", {"center": v(-187.5, -171) * mm, "radius": 2.5 * mm});
            skCircle(sketch, "E2.7.47.0", {"center": v(-187.5, -179) * mm, "radius": 2.5 * mm});
            skCircle(sketch, "E2.7.48.0", {"center": v(-187.5, -187) * mm, "radius": 2.5 * mm});
            skCircle(sketch, "E2.7.49.0", {"center": v(-187.5, -195) * mm, "radius": 2.5 * mm});
            skCircle(sketch, "E2.8.0.0", {"center": v(-179.5, 197) * mm, "radius": 2.5 * mm});
            skCircle(sketch, "E2.8.1.0", {"center": v(-179.5, 189) * mm, "radius": 2.5 * mm});
            skCircle(sketch, "E2.8.2.0", {"center": v(-179.5, 181) * mm, "radius": 2.5 * mm});
            skCircle(sketch, "E2.8.3.0", {"center": v(-179.5, 173) * mm, "radius": 2.5 * mm});
            skCircle(sketch, "E2.8.4.0", {"center": v(-179.5, 165) * mm, "radius": 2.5 * mm});
            skCircle(sketch, "E2.8.5.0", {"center": v(-179.5, 157) * mm, "radius": 2.5 * mm});
            skCircle(sketch, "E2.8.6.0", {"center": v(-179.5, 149) * mm, "radius": 2.5 * mm});
            skCircle(sketch, "E2.8.7.0", {"center": v(-179.5, 141) * mm, "radius": 2.5 * mm});
            skCircle(sketch, "E2.8.8.0", {"center": v(-179.5, 133) * mm, "radius": 2.5 * mm});
            skCircle(sketch, "E2.8.9.0", {"center": v(-179.5, 125) * mm, "radius": 2.5 * mm});
            skCircle(sketch, "E2.8.10.0", {"center": v(-179.5, 117) * mm, "radius": 2.5 * mm});
            skCircle(sketch, "E2.8.11.0", {"center": v(-179.5, 109) * mm, "radius": 2.5 * mm});
            skCircle(sketch, "E2.8.12.0", {"center": v(-179.5, 101) * mm, "radius": 2.5 * mm});
            skCircle(sketch, "E2.8.13.0", {"center": v(-179.5, 93) * mm, "radius": 2.5 * mm});
            skCircle(sketch, "E2.8.14.0", {"center": v(-179.5, 85) * mm, "radius": 2.5 * mm});
            skCircle(sketch, "E2.8.15.0", {"center": v(-179.5, 77) * mm, "radius": 2.5 * mm});
            skCircle(sketch, "E2.8.16.0", {"center": v(-179.5, 69) * mm, "radius": 2.5 * mm});
            skCircle(sketch, "E2.8.17.0", {"center": v(-179.5, 61) * mm, "radius": 2.5 * mm});
            skCircle(sketch, "E2.8.18.0", {"center": v(-179.5, 53) * mm, "radius": 2.5 * mm});
            skCircle(sketch, "E2.8.19.0", {"center": v(-179.5, 45) * mm, "radius": 2.5 * mm});
            skCircle(sketch, "E2.8.20.0", {"center": v(-179.5, 37) * mm, "radius": 2.5 * mm});
            skCircle(sketch, "E2.8.21.0", {"center": v(-179.5, 29) * mm, "radius": 2.5 * mm});
            skCircle(sketch, "E2.8.22.0", {"center": v(-179.5, 21) * mm, "radius": 2.5 * mm});
            skCircle(sketch, "E2.8.23.0", {"center": v(-179.5, 13) * mm, "radius": 2.5 * mm});
            skCircle(sketch, "E2.8.24.0", {"center": v(-179.5, 5) * mm, "radius": 2.5 * mm});
            skCircle(sketch, "E2.8.25.0", {"center": v(-179.5, -3) * mm, "radius": 2.5 * mm});
            skCircle(sketch, "E2.8.26.0", {"center": v(-179.5, -11) * mm, "radius": 2.5 * mm});
            skCircle(sketch, "E2.8.27.0", {"center": v(-179.5, -19) * mm, "radius": 2.5 * mm});
            skCircle(sketch, "E2.8.28.0", {"center": v(-179.5, -27) * mm, "radius": 2.5 * mm});
            skCircle(sketch, "E2.8.29.0", {"center": v(-179.5, -35) * mm, "radius": 2.5 * mm});
            skCircle(sketch, "E2.8.30.0", {"center": v(-179.5, -43) * mm, "radius": 2.5 * mm});
            skCircle(sketch, "E2.8.31.0", {"center": v(-179.5, -51) * mm, "radius": 2.5 * mm});
            skCircle(sketch, "E2.8.32.0", {"center": v(-179.5, -59) * mm, "radius": 2.5 * mm});
            skCircle(sketch, "E2.8.33.0", {"center": v(-179.5, -67) * mm, "radius": 2.5 * mm});
            skCircle(sketch, "E2.8.34.0", {"center": v(-179.5, -75) * mm, "radius": 2.5 * mm});
            skCircle(sketch, "E2.8.35.0", {"center": v(-179.5, -83) * mm, "radius": 2.5 * mm});
            skCircle(sketch, "E2.8.36.0", {"center": v(-179.5, -91) * mm, "radius": 2.5 * mm});
            skCircle(sketch, "E2.8.37.0", {"center": v(-179.5, -99) * mm, "radius": 2.5 * mm});
            skCircle(sketch, "E2.8.38.0", {"center": v(-179.5, -107) * mm, "radius": 2.5 * mm});
            skCircle(sketch, "E2.8.39.0", {"center": v(-179.5, -115) * mm, "radius": 2.5 * mm});
            skCircle(sketch, "E2.8.40.0", {"center": v(-179.5, -123) * mm, "radius": 2.5 * mm});
            skCircle(sketch, "E2.8.41.0", {"center": v(-179.5, -131) * mm, "radius": 2.5 * mm});
            skCircle(sketch, "E2.8.42.0", {"center": v(-179.5, -139) * mm, "radius": 2.5 * mm});
            skCircle(sketch, "E2.8.43.0", {"center": v(-179.5, -147) * mm, "radius": 2.5 * mm});
            skCircle(sketch, "E2.8.44.0", {"center": v(-179.5, -155) * mm, "radius": 2.5 * mm});
            skCircle(sketch, "E2.8.45.0", {"center": v(-179.5, -163) * mm, "radius": 2.5 * mm});
            skCircle(sketch, "E2.8.46.0", {"center": v(-179.5, -171) * mm, "radius": 2.5 * mm});
            skCircle(sketch, "E2.8.47.0", {"center": v(-179.5, -179) * mm, "radius": 2.5 * mm});
            skCircle(sketch, "E2.8.48.0", {"center": v(-179.5, -187) * mm, "radius": 2.5 * mm});
            skCircle(sketch, "E2.8.49.0", {"center": v(-179.5, -195) * mm, "radius": 2.5 * mm});
            skCircle(sketch, "E2.9.0.0", {"center": v(-171.5, 197) * mm, "radius": 2.5 * mm});
            skCircle(sketch, "E2.9.1.0", {"center": v(-171.5, 189) * mm, "radius": 2.5 * mm});
            skCircle(sketch, "E2.9.2.0", {"center": v(-171.5, 181) * mm, "radius": 2.5 * mm});
            skCircle(sketch, "E2.9.3.0", {"center": v(-171.5, 173) * mm, "radius": 2.5 * mm});
            skCircle(sketch, "E2.9.4.0", {"center": v(-171.5, 165) * mm, "radius": 2.5 * mm});
            skCircle(sketch, "E2.9.5.0", {"center": v(-171.5, 157) * mm, "radius": 2.5 * mm});
            skCircle(sketch, "E2.9.6.0", {"center": v(-171.5, 149) * mm, "radius": 2.5 * mm});
            skCircle(sketch, "E2.9.7.0", {"center": v(-171.5, 141) * mm, "radius": 2.5 * mm});
            skCircle(sketch, "E2.9.8.0", {"center": v(-171.5, 133) * mm, "radius": 2.5 * mm});
            skCircle(sketch, "E2.9.9.0", {"center": v(-171.5, 125) * mm, "radius": 2.5 * mm});
            skCircle(sketch, "E2.9.10.0", {"center": v(-171.5, 117) * mm, "radius": 2.5 * mm});
            skCircle(sketch, "E2.9.11.0", {"center": v(-171.5, 109) * mm, "radius": 2.5 * mm});
            skCircle(sketch, "E2.9.12.0", {"center": v(-171.5, 101) * mm, "radius": 2.5 * mm});
            skCircle(sketch, "E2.9.13.0", {"center": v(-171.5, 93) * mm, "radius": 2.5 * mm});
            skCircle(sketch, "E2.9.14.0", {"center": v(-171.5, 85) * mm, "radius": 2.5 * mm});
            skCircle(sketch, "E2.9.15.0", {"center": v(-171.5, 77) * mm, "radius": 2.5 * mm});
            skCircle(sketch, "E2.9.16.0", {"center": v(-171.5, 69) * mm, "radius": 2.5 * mm});
            skCircle(sketch, "E2.9.17.0", {"center": v(-171.5, 61) * mm, "radius": 2.5 * mm});
            skCircle(sketch, "E2.9.18.0", {"center": v(-171.5, 53) * mm, "radius": 2.5 * mm});
            skCircle(sketch, "E2.9.19.0", {"center": v(-171.5, 45) * mm, "radius": 2.5 * mm});
            skCircle(sketch, "E2.9.20.0", {"center": v(-171.5, 37) * mm, "radius": 2.5 * mm});
            skCircle(sketch, "E2.9.21.0", {"center": v(-171.5, 29) * mm, "radius": 2.5 * mm});
            skCircle(sketch, "E2.9.22.0", {"center": v(-171.5, 21) * mm, "radius": 2.5 * mm});
            skCircle(sketch, "E2.9.23.0", {"center": v(-171.5, 13) * mm, "radius": 2.5 * mm});
            skCircle(sketch, "E2.9.24.0", {"center": v(-171.5, 5) * mm, "radius": 2.5 * mm});
            skCircle(sketch, "E2.9.25.0", {"center": v(-171.5, -3) * mm, "radius": 2.5 * mm});
            skCircle(sketch, "E2.9.26.0", {"center": v(-171.5, -11) * mm, "radius": 2.5 * mm});
            skCircle(sketch, "E2.9.27.0", {"center": v(-171.5, -19) * mm, "radius": 2.5 * mm});
            skCircle(sketch, "E2.9.28.0", {"center": v(-171.5, -27) * mm, "radius": 2.5 * mm});
            skCircle(sketch, "E2.9.29.0", {"center": v(-171.5, -35) * mm, "radius": 2.5 * mm});
            skCircle(sketch, "E2.9.30.0", {"center": v(-171.5, -43) * mm, "radius": 2.5 * mm});
            skCircle(sketch, "E2.9.31.0", {"center": v(-171.5, -51) * mm, "radius": 2.5 * mm});
            skCircle(sketch, "E2.9.32.0", {"center": v(-171.5, -59) * mm, "radius": 2.5 * mm});
            skCircle(sketch, "E2.9.33.0", {"center": v(-171.5, -67) * mm, "radius": 2.5 * mm});
            skCircle(sketch, "E2.9.34.0", {"center": v(-171.5, -75) * mm, "radius": 2.5 * mm});
            skCircle(sketch, "E2.9.35.0", {"center": v(-171.5, -83) * mm, "radius": 2.5 * mm});
            skCircle(sketch, "E2.9.36.0", {"center": v(-171.5, -91) * mm, "radius": 2.5 * mm});
            skCircle(sketch, "E2.9.37.0", {"center": v(-171.5, -99) * mm, "radius": 2.5 * mm});
            skCircle(sketch, "E2.9.38.0", {"center": v(-171.5, -107) * mm, "radius": 2.5 * mm});
            skCircle(sketch, "E2.9.39.0", {"center": v(-171.5, -115) * mm, "radius": 2.5 * mm});
            skCircle(sketch, "E2.9.40.0", {"center": v(-171.5, -123) * mm, "radius": 2.5 * mm});
            skCircle(sketch, "E2.9.41.0", {"center": v(-171.5, -131) * mm, "radius": 2.5 * mm});
            skCircle(sketch, "E2.9.42.0", {"center": v(-171.5, -139) * mm, "radius": 2.5 * mm});
            skCircle(sketch, "E2.9.43.0", {"center": v(-171.5, -147) * mm, "radius": 2.5 * mm});
            skCircle(sketch, "E2.9.44.0", {"center": v(-171.5, -155) * mm, "radius": 2.5 * mm});
            skCircle(sketch, "E2.9.45.0", {"center": v(-171.5, -163) * mm, "radius": 2.5 * mm});
            skCircle(sketch, "E2.9.46.0", {"center": v(-171.5, -171) * mm, "radius": 2.5 * mm});
            skCircle(sketch, "E2.9.47.0", {"center": v(-171.5, -179) * mm, "radius": 2.5 * mm});
            skCircle(sketch, "E2.9.48.0", {"center": v(-171.5, -187) * mm, "radius": 2.5 * mm});
            skCircle(sketch, "E2.9.49.0", {"center": v(-171.5, -195) * mm, "radius": 2.5 * mm});
            skCircle(sketch, "E2.10.0.0", {"center": v(-163.5, 197) * mm, "radius": 2.5 * mm});
            skCircle(sketch, "E2.10.1.0", {"center": v(-163.5, 189) * mm, "radius": 2.5 * mm});
            skCircle(sketch, "E2.10.2.0", {"center": v(-163.5, 181) * mm, "radius": 2.5 * mm});
            skCircle(sketch, "E2.10.3.0", {"center": v(-163.5, 173) * mm, "radius": 2.5 * mm});
            skCircle(sketch, "E2.10.4.0", {"center": v(-163.5, 165) * mm, "radius": 2.5 * mm});
            skCircle(sketch, "E2.10.5.0", {"center": v(-163.5, 157) * mm, "radius": 2.5 * mm});
            skCircle(sketch, "E2.10.6.0", {"center": v(-163.5, 149) * mm, "radius": 2.5 * mm});
            skCircle(sketch, "E2.10.7.0", {"center": v(-163.5, 141) * mm, "radius": 2.5 * mm});
            skCircle(sketch, "E2.10.8.0", {"center": v(-163.5, 133) * mm, "radius": 2.5 * mm});
            skCircle(sketch, "E2.10.9.0", {"center": v(-163.5, 125) * mm, "radius": 2.5 * mm});
            skCircle(sketch, "E2.10.10.0", {"center": v(-163.5, 117) * mm, "radius": 2.5 * mm});
            skCircle(sketch, "E2.10.11.0", {"center": v(-163.5, 109) * mm, "radius": 2.5 * mm});
            skCircle(sketch, "E2.10.12.0", {"center": v(-163.5, 101) * mm, "radius": 2.5 * mm});
            skCircle(sketch, "E2.10.13.0", {"center": v(-163.5, 93) * mm, "radius": 2.5 * mm});
            skCircle(sketch, "E2.10.14.0", {"center": v(-163.5, 85) * mm, "radius": 2.5 * mm});
            skCircle(sketch, "E2.10.15.0", {"center": v(-163.5, 77) * mm, "radius": 2.5 * mm});
            skCircle(sketch, "E2.10.16.0", {"center": v(-163.5, 69) * mm, "radius": 2.5 * mm});
            skCircle(sketch, "E2.10.17.0", {"center": v(-163.5, 61) * mm, "radius": 2.5 * mm});
            skCircle(sketch, "E2.10.18.0", {"center": v(-163.5, 53) * mm, "radius": 2.5 * mm});
            skCircle(sketch, "E2.10.19.0", {"center": v(-163.5, 45) * mm, "radius": 2.5 * mm});
            skCircle(sketch, "E2.10.20.0", {"center": v(-163.5, 37) * mm, "radius": 2.5 * mm});
            skCircle(sketch, "E2.10.21.0", {"center": v(-163.5, 29) * mm, "radius": 2.5 * mm});
            skCircle(sketch, "E2.10.22.0", {"center": v(-163.5, 21) * mm, "radius": 2.5 * mm});
            skCircle(sketch, "E2.10.23.0", {"center": v(-163.5, 13) * mm, "radius": 2.5 * mm});
            skCircle(sketch, "E2.10.24.0", {"center": v(-163.5, 5) * mm, "radius": 2.5 * mm});
            skCircle(sketch, "E2.10.25.0", {"center": v(-163.5, -3) * mm, "radius": 2.5 * mm});
            skCircle(sketch, "E2.10.26.0", {"center": v(-163.5, -11) * mm, "radius": 2.5 * mm});
            skCircle(sketch, "E2.10.27.0", {"center": v(-163.5, -19) * mm, "radius": 2.5 * mm});
            skCircle(sketch, "E2.10.28.0", {"center": v(-163.5, -27) * mm, "radius": 2.5 * mm});
            skCircle(sketch, "E2.10.29.0", {"center": v(-163.5, -35) * mm, "radius": 2.5 * mm});
            skCircle(sketch, "E2.10.30.0", {"center": v(-163.5, -43) * mm, "radius": 2.5 * mm});
            skCircle(sketch, "E2.10.31.0", {"center": v(-163.5, -51) * mm, "radius": 2.5 * mm});
            skCircle(sketch, "E2.10.32.0", {"center": v(-163.5, -59) * mm, "radius": 2.5 * mm});
            skCircle(sketch, "E2.10.33.0", {"center": v(-163.5, -67) * mm, "radius": 2.5 * mm});
            skCircle(sketch, "E2.10.34.0", {"center": v(-163.5, -75) * mm, "radius": 2.5 * mm});
            skCircle(sketch, "E2.10.35.0", {"center": v(-163.5, -83) * mm, "radius": 2.5 * mm});
            skCircle(sketch, "E2.10.36.0", {"center": v(-163.5, -91) * mm, "radius": 2.5 * mm});
            skCircle(sketch, "E2.10.37.0", {"center": v(-163.5, -99) * mm, "radius": 2.5 * mm});
            skCircle(sketch, "E2.10.38.0", {"center": v(-163.5, -107) * mm, "radius": 2.5 * mm});
            skCircle(sketch, "E2.10.39.0", {"center": v(-163.5, -115) * mm, "radius": 2.5 * mm});
            skCircle(sketch, "E2.10.40.0", {"center": v(-163.5, -123) * mm, "radius": 2.5 * mm});
            skCircle(sketch, "E2.10.41.0", {"center": v(-163.5, -131) * mm, "radius": 2.5 * mm});
            skCircle(sketch, "E2.10.42.0", {"center": v(-163.5, -139) * mm, "radius": 2.5 * mm});
            skCircle(sketch, "E2.10.43.0", {"center": v(-163.5, -147) * mm, "radius": 2.5 * mm});
            skCircle(sketch, "E2.10.44.0", {"center": v(-163.5, -155) * mm, "radius": 2.5 * mm});
            skCircle(sketch, "E2.10.45.0", {"center": v(-163.5, -163) * mm, "radius": 2.5 * mm});
            skCircle(sketch, "E2.10.46.0", {"center": v(-163.5, -171) * mm, "radius": 2.5 * mm});
            skCircle(sketch, "E2.10.47.0", {"center": v(-163.5, -179) * mm, "radius": 2.5 * mm});
            skCircle(sketch, "E2.10.48.0", {"center": v(-163.5, -187) * mm, "radius": 2.5 * mm});
            skCircle(sketch, "E2.10.49.0", {"center": v(-163.5, -195) * mm, "radius": 2.5 * mm});
            skCircle(sketch, "E2.11.0.0", {"center": v(-155.5, 197) * mm, "radius": 2.5 * mm});
            skCircle(sketch, "E2.11.1.0", {"center": v(-155.5, 189) * mm, "radius": 2.5 * mm});
            skCircle(sketch, "E2.11.2.0", {"center": v(-155.5, 181) * mm, "radius": 2.5 * mm});
            skCircle(sketch, "E2.11.3.0", {"center": v(-155.5, 173) * mm, "radius": 2.5 * mm});
            skCircle(sketch, "E2.11.4.0", {"center": v(-155.5, 165) * mm, "radius": 2.5 * mm});
            skCircle(sketch, "E2.11.5.0", {"center": v(-155.5, 157) * mm, "radius": 2.5 * mm});
            skCircle(sketch, "E2.11.6.0", {"center": v(-155.5, 149) * mm, "radius": 2.5 * mm});
            skCircle(sketch, "E2.11.7.0", {"center": v(-155.5, 141) * mm, "radius": 2.5 * mm});
            skCircle(sketch, "E2.11.8.0", {"center": v(-155.5, 133) * mm, "radius": 2.5 * mm});
            skCircle(sketch, "E2.11.9.0", {"center": v(-155.5, 125) * mm, "radius": 2.5 * mm});
            skCircle(sketch, "E2.11.10.0", {"center": v(-155.5, 117) * mm, "radius": 2.5 * mm});
            skCircle(sketch, "E2.11.11.0", {"center": v(-155.5, 109) * mm, "radius": 2.5 * mm});
            skCircle(sketch, "E2.11.12.0", {"center": v(-155.5, 101) * mm, "radius": 2.5 * mm});
            skCircle(sketch, "E2.11.13.0", {"center": v(-155.5, 93) * mm, "radius": 2.5 * mm});
            skCircle(sketch, "E2.11.14.0", {"center": v(-155.5, 85) * mm, "radius": 2.5 * mm});
            skCircle(sketch, "E2.11.15.0", {"center": v(-155.5, 77) * mm, "radius": 2.5 * mm});
            skCircle(sketch, "E2.11.16.0", {"center": v(-155.5, 69) * mm, "radius": 2.5 * mm});
            skCircle(sketch, "E2.11.17.0", {"center": v(-155.5, 61) * mm, "radius": 2.5 * mm});
            skCircle(sketch, "E2.11.18.0", {"center": v(-155.5, 53) * mm, "radius": 2.5 * mm});
            skCircle(sketch, "E2.11.19.0", {"center": v(-155.5, 45) * mm, "radius": 2.5 * mm});
            skCircle(sketch, "E2.11.20.0", {"center": v(-155.5, 37) * mm, "radius": 2.5 * mm});
            skCircle(sketch, "E2.11.21.0", {"center": v(-155.5, 29) * mm, "radius": 2.5 * mm});
            skCircle(sketch, "E2.11.22.0", {"center": v(-155.5, 21) * mm, "radius": 2.5 * mm});
            skCircle(sketch, "E2.11.23.0", {"center": v(-155.5, 13) * mm, "radius": 2.5 * mm});
            skCircle(sketch, "E2.11.24.0", {"center": v(-155.5, 5) * mm, "radius": 2.5 * mm});
            skCircle(sketch, "E2.11.25.0", {"center": v(-155.5, -3) * mm, "radius": 2.5 * mm});
            skCircle(sketch, "E2.11.26.0", {"center": v(-155.5, -11) * mm, "radius": 2.5 * mm});
            skCircle(sketch, "E2.11.27.0", {"center": v(-155.5, -19) * mm, "radius": 2.5 * mm});
            skCircle(sketch, "E2.11.28.0", {"center": v(-155.5, -27) * mm, "radius": 2.5 * mm});
            skCircle(sketch, "E2.11.29.0", {"center": v(-155.5, -35) * mm, "radius": 2.5 * mm});
            skCircle(sketch, "E2.11.30.0", {"center": v(-155.5, -43) * mm, "radius": 2.5 * mm});
            skCircle(sketch, "E2.11.31.0", {"center": v(-155.5, -51) * mm, "radius": 2.5 * mm});
            skCircle(sketch, "E2.11.32.0", {"center": v(-155.5, -59) * mm, "radius": 2.5 * mm});
            skCircle(sketch, "E2.11.33.0", {"center": v(-155.5, -67) * mm, "radius": 2.5 * mm});
            skCircle(sketch, "E2.11.34.0", {"center": v(-155.5, -75) * mm, "radius": 2.5 * mm});
            skCircle(sketch, "E2.11.35.0", {"center": v(-155.5, -83) * mm, "radius": 2.5 * mm});
            skCircle(sketch, "E2.11.36.0", {"center": v(-155.5, -91) * mm, "radius": 2.5 * mm});
            skCircle(sketch, "E2.11.37.0", {"center": v(-155.5, -99) * mm, "radius": 2.5 * mm});
            skCircle(sketch, "E2.11.38.0", {"center": v(-155.5, -107) * mm, "radius": 2.5 * mm});
            skCircle(sketch, "E2.11.39.0", {"center": v(-155.5, -115) * mm, "radius": 2.5 * mm});
            skCircle(sketch, "E2.11.40.0", {"center": v(-155.5, -123) * mm, "radius": 2.5 * mm});
            skCircle(sketch, "E2.11.41.0", {"center": v(-155.5, -131) * mm, "radius": 2.5 * mm});
            skCircle(sketch, "E2.11.42.0", {"center": v(-155.5, -139) * mm, "radius": 2.5 * mm});
            skCircle(sketch, "E2.11.43.0", {"center": v(-155.5, -147) * mm, "radius": 2.5 * mm});
            skCircle(sketch, "E2.11.44.0", {"center": v(-155.5, -155) * mm, "radius": 2.5 * mm});
            skCircle(sketch, "E2.11.45.0", {"center": v(-155.5, -163) * mm, "radius": 2.5 * mm});
            skCircle(sketch, "E2.11.46.0", {"center": v(-155.5, -171) * mm, "radius": 2.5 * mm});
            skCircle(sketch, "E2.11.47.0", {"center": v(-155.5, -179) * mm, "radius": 2.5 * mm});
            skCircle(sketch, "E2.11.48.0", {"center": v(-155.5, -187) * mm, "radius": 2.5 * mm});
            skCircle(sketch, "E2.11.49.0", {"center": v(-155.5, -195) * mm, "radius": 2.5 * mm});
            skCircle(sketch, "E2.12.0.0", {"center": v(-147.5, 197) * mm, "radius": 2.5 * mm});
            skCircle(sketch, "E2.12.1.0", {"center": v(-147.5, 189) * mm, "radius": 2.5 * mm});
            skCircle(sketch, "E2.12.2.0", {"center": v(-147.5, 181) * mm, "radius": 2.5 * mm});
            skCircle(sketch, "E2.12.3.0", {"center": v(-147.5, 173) * mm, "radius": 2.5 * mm});
            skCircle(sketch, "E2.12.4.0", {"center": v(-147.5, 165) * mm, "radius": 2.5 * mm});
            skCircle(sketch, "E2.12.5.0", {"center": v(-147.5, 157) * mm, "radius": 2.5 * mm});
            skCircle(sketch, "E2.12.6.0", {"center": v(-147.5, 149) * mm, "radius": 2.5 * mm});
            skCircle(sketch, "E2.12.7.0", {"center": v(-147.5, 141) * mm, "radius": 2.5 * mm});
            skCircle(sketch, "E2.12.8.0", {"center": v(-147.5, 133) * mm, "radius": 2.5 * mm});
            skCircle(sketch, "E2.12.9.0", {"center": v(-147.5, 125) * mm, "radius": 2.5 * mm});
            skCircle(sketch, "E2.12.10.0", {"center": v(-147.5, 117) * mm, "radius": 2.5 * mm});
            skCircle(sketch, "E2.12.11.0", {"center": v(-147.5, 109) * mm, "radius": 2.5 * mm});
            skCircle(sketch, "E2.12.12.0", {"center": v(-147.5, 101) * mm, "radius": 2.5 * mm});
            skCircle(sketch, "E2.12.13.0", {"center": v(-147.5, 93) * mm, "radius": 2.5 * mm});
            skCircle(sketch, "E2.12.14.0", {"center": v(-147.5, 85) * mm, "radius": 2.5 * mm});
            skCircle(sketch, "E2.12.15.0", {"center": v(-147.5, 77) * mm, "radius": 2.5 * mm});
            skCircle(sketch, "E2.12.16.0", {"center": v(-147.5, 69) * mm, "radius": 2.5 * mm});
            skCircle(sketch, "E2.12.17.0", {"center": v(-147.5, 61) * mm, "radius": 2.5 * mm});
            skCircle(sketch, "E2.12.18.0", {"center": v(-147.5, 53) * mm, "radius": 2.5 * mm});
            skCircle(sketch, "E2.12.19.0", {"center": v(-147.5, 45) * mm, "radius": 2.5 * mm});
            skCircle(sketch, "E2.12.20.0", {"center": v(-147.5, 37) * mm, "radius": 2.5 * mm});
            skCircle(sketch, "E2.12.21.0", {"center": v(-147.5, 29) * mm, "radius": 2.5 * mm});
            skCircle(sketch, "E2.12.22.0", {"center": v(-147.5, 21) * mm, "radius": 2.5 * mm});
            skCircle(sketch, "E2.12.23.0", {"center": v(-147.5, 13) * mm, "radius": 2.5 * mm});
            skCircle(sketch, "E2.12.24.0", {"center": v(-147.5, 5) * mm, "radius": 2.5 * mm});
            skCircle(sketch, "E2.12.25.0", {"center": v(-147.5, -3) * mm, "radius": 2.5 * mm});
            skCircle(sketch, "E2.12.26.0", {"center": v(-147.5, -11) * mm, "radius": 2.5 * mm});
            skCircle(sketch, "E2.12.27.0", {"center": v(-147.5, -19) * mm, "radius": 2.5 * mm});
            skCircle(sketch, "E2.12.28.0", {"center": v(-147.5, -27) * mm, "radius": 2.5 * mm});
            skCircle(sketch, "E2.12.29.0", {"center": v(-147.5, -35) * mm, "radius": 2.5 * mm});
            skCircle(sketch, "E2.12.30.0", {"center": v(-147.5, -43) * mm, "radius": 2.5 * mm});
            skCircle(sketch, "E2.12.31.0", {"center": v(-147.5, -51) * mm, "radius": 2.5 * mm});
            skCircle(sketch, "E2.12.32.0", {"center": v(-147.5, -59) * mm, "radius": 2.5 * mm});
            skCircle(sketch, "E2.12.33.0", {"center": v(-147.5, -67) * mm, "radius": 2.5 * mm});
            skCircle(sketch, "E2.12.34.0", {"center": v(-147.5, -75) * mm, "radius": 2.5 * mm});
            skCircle(sketch, "E2.12.35.0", {"center": v(-147.5, -83) * mm, "radius": 2.5 * mm});
            skCircle(sketch, "E2.12.36.0", {"center": v(-147.5, -91) * mm, "radius": 2.5 * mm});
            skCircle(sketch, "E2.12.37.0", {"center": v(-147.5, -99) * mm, "radius": 2.5 * mm});
            skCircle(sketch, "E2.12.38.0", {"center": v(-147.5, -107) * mm, "radius": 2.5 * mm});
            skCircle(sketch, "E2.12.39.0", {"center": v(-147.5, -115) * mm, "radius": 2.5 * mm});
            skCircle(sketch, "E2.12.40.0", {"center": v(-147.5, -123) * mm, "radius": 2.5 * mm});
            skCircle(sketch, "E2.12.41.0", {"center": v(-147.5, -131) * mm, "radius": 2.5 * mm});
            skCircle(sketch, "E2.12.42.0", {"center": v(-147.5, -139) * mm, "radius": 2.5 * mm});
            skCircle(sketch, "E2.12.43.0", {"center": v(-147.5, -147) * mm, "radius": 2.5 * mm});
            skCircle(sketch, "E2.12.44.0", {"center": v(-147.5, -155) * mm, "radius": 2.5 * mm});
            skCircle(sketch, "E2.12.45.0", {"center": v(-147.5, -163) * mm, "radius": 2.5 * mm});
            skCircle(sketch, "E2.12.46.0", {"center": v(-147.5, -171) * mm, "radius": 2.5 * mm});
            skCircle(sketch, "E2.12.47.0", {"center": v(-147.5, -179) * mm, "radius": 2.5 * mm});
            skCircle(sketch, "E2.12.48.0", {"center": v(-147.5, -187) * mm, "radius": 2.5 * mm});
            skCircle(sketch, "E2.12.49.0", {"center": v(-147.5, -195) * mm, "radius": 2.5 * mm});
            skCircle(sketch, "E2.13.0.0", {"center": v(-139.5, 197) * mm, "radius": 2.5 * mm});
            skCircle(sketch, "E2.13.1.0", {"center": v(-139.5, 189) * mm, "radius": 2.5 * mm});
            skCircle(sketch, "E2.13.2.0", {"center": v(-139.5, 181) * mm, "radius": 2.5 * mm});
            skCircle(sketch, "E2.13.3.0", {"center": v(-139.5, 173) * mm, "radius": 2.5 * mm});
            skCircle(sketch, "E2.13.4.0", {"center": v(-139.5, 165) * mm, "radius": 2.5 * mm});
            skCircle(sketch, "E2.13.5.0", {"center": v(-139.5, 157) * mm, "radius": 2.5 * mm});
            skCircle(sketch, "E2.13.6.0", {"center": v(-139.5, 149) * mm, "radius": 2.5 * mm});
            skCircle(sketch, "E2.13.7.0", {"center": v(-139.5, 141) * mm, "radius": 2.5 * mm});
            skCircle(sketch, "E2.13.8.0", {"center": v(-139.5, 133) * mm, "radius": 2.5 * mm});
            skCircle(sketch, "E2.13.9.0", {"center": v(-139.5, 125) * mm, "radius": 2.5 * mm});
            skCircle(sketch, "E2.13.10.0", {"center": v(-139.5, 117) * mm, "radius": 2.5 * mm});
            skCircle(sketch, "E2.13.11.0", {"center": v(-139.5, 109) * mm, "radius": 2.5 * mm});
            skCircle(sketch, "E2.13.12.0", {"center": v(-139.5, 101) * mm, "radius": 2.5 * mm});
            skCircle(sketch, "E2.13.13.0", {"center": v(-139.5, 93) * mm, "radius": 2.5 * mm});
            skCircle(sketch, "E2.13.14.0", {"center": v(-139.5, 85) * mm, "radius": 2.5 * mm});
            skCircle(sketch, "E2.13.15.0", {"center": v(-139.5, 77) * mm, "radius": 2.5 * mm});
            skCircle(sketch, "E2.13.16.0", {"center": v(-139.5, 69) * mm, "radius": 2.5 * mm});
            skCircle(sketch, "E2.13.17.0", {"center": v(-139.5, 61) * mm, "radius": 2.5 * mm});
            skCircle(sketch, "E2.13.18.0", {"center": v(-139.5, 53) * mm, "radius": 2.5 * mm});
            skCircle(sketch, "E2.13.19.0", {"center": v(-139.5, 45) * mm, "radius": 2.5 * mm});
            skCircle(sketch, "E2.13.20.0", {"center": v(-139.5, 37) * mm, "radius": 2.5 * mm});
            skCircle(sketch, "E2.13.21.0", {"center": v(-139.5, 29) * mm, "radius": 2.5 * mm});
            skCircle(sketch, "E2.13.22.0", {"center": v(-139.5, 21) * mm, "radius": 2.5 * mm});
            skCircle(sketch, "E2.13.23.0", {"center": v(-139.5, 13) * mm, "radius": 2.5 * mm});
            skCircle(sketch, "E2.13.24.0", {"center": v(-139.5, 5) * mm, "radius": 2.5 * mm});
            skCircle(sketch, "E2.13.25.0", {"center": v(-139.5, -3) * mm, "radius": 2.5 * mm});
            skCircle(sketch, "E2.13.26.0", {"center": v(-139.5, -11) * mm, "radius": 2.5 * mm});
            skCircle(sketch, "E2.13.27.0", {"center": v(-139.5, -19) * mm, "radius": 2.5 * mm});
            skCircle(sketch, "E2.13.28.0", {"center": v(-139.5, -27) * mm, "radius": 2.5 * mm});
            skCircle(sketch, "E2.13.29.0", {"center": v(-139.5, -35) * mm, "radius": 2.5 * mm});
            skCircle(sketch, "E2.13.30.0", {"center": v(-139.5, -43) * mm, "radius": 2.5 * mm});
            skCircle(sketch, "E2.13.31.0", {"center": v(-139.5, -51) * mm, "radius": 2.5 * mm});
            skCircle(sketch, "E2.13.32.0", {"center": v(-139.5, -59) * mm, "radius": 2.5 * mm});
            skCircle(sketch, "E2.13.33.0", {"center": v(-139.5, -67) * mm, "radius": 2.5 * mm});
            skCircle(sketch, "E2.13.34.0", {"center": v(-139.5, -75) * mm, "radius": 2.5 * mm});
            skCircle(sketch, "E2.13.35.0", {"center": v(-139.5, -83) * mm, "radius": 2.5 * mm});
            skCircle(sketch, "E2.13.36.0", {"center": v(-139.5, -91) * mm, "radius": 2.5 * mm});
            skCircle(sketch, "E2.13.37.0", {"center": v(-139.5, -99) * mm, "radius": 2.5 * mm});
            skCircle(sketch, "E2.13.38.0", {"center": v(-139.5, -107) * mm, "radius": 2.5 * mm});
            skCircle(sketch, "E2.13.39.0", {"center": v(-139.5, -115) * mm, "radius": 2.5 * mm});
            skCircle(sketch, "E2.13.40.0", {"center": v(-139.5, -123) * mm, "radius": 2.5 * mm});
            skCircle(sketch, "E2.13.41.0", {"center": v(-139.5, -131) * mm, "radius": 2.5 * mm});
            skCircle(sketch, "E2.13.42.0", {"center": v(-139.5, -139) * mm, "radius": 2.5 * mm});
            skCircle(sketch, "E2.13.43.0", {"center": v(-139.5, -147) * mm, "radius": 2.5 * mm});
            skCircle(sketch, "E2.13.44.0", {"center": v(-139.5, -155) * mm, "radius": 2.5 * mm});
            skCircle(sketch, "E2.13.45.0", {"center": v(-139.5, -163) * mm, "radius": 2.5 * mm});
            skCircle(sketch, "E2.13.46.0", {"center": v(-139.5, -171) * mm, "radius": 2.5 * mm});
            skCircle(sketch, "E2.13.47.0", {"center": v(-139.5, -179) * mm, "radius": 2.5 * mm});
            skCircle(sketch, "E2.13.48.0", {"center": v(-139.5, -187) * mm, "radius": 2.5 * mm});
            skCircle(sketch, "E2.13.49.0", {"center": v(-139.5, -195) * mm, "radius": 2.5 * mm});
            skCircle(sketch, "E2.14.0.0", {"center": v(-131.5, 197) * mm, "radius": 2.5 * mm});
            skCircle(sketch, "E2.14.1.0", {"center": v(-131.5, 189) * mm, "radius": 2.5 * mm});
            skCircle(sketch, "E2.14.2.0", {"center": v(-131.5, 181) * mm, "radius": 2.5 * mm});
            skCircle(sketch, "E2.14.3.0", {"center": v(-131.5, 173) * mm, "radius": 2.5 * mm});
            skCircle(sketch, "E2.14.4.0", {"center": v(-131.5, 165) * mm, "radius": 2.5 * mm});
            skCircle(sketch, "E2.14.5.0", {"center": v(-131.5, 157) * mm, "radius": 2.5 * mm});
            skCircle(sketch, "E2.14.6.0", {"center": v(-131.5, 149) * mm, "radius": 2.5 * mm});
            skCircle(sketch, "E2.14.7.0", {"center": v(-131.5, 141) * mm, "radius": 2.5 * mm});
            skCircle(sketch, "E2.14.8.0", {"center": v(-131.5, 133) * mm, "radius": 2.5 * mm});
            skCircle(sketch, "E2.14.9.0", {"center": v(-131.5, 125) * mm, "radius": 2.5 * mm});
            skCircle(sketch, "E2.14.10.0", {"center": v(-131.5, 117) * mm, "radius": 2.5 * mm});
            skCircle(sketch, "E2.14.11.0", {"center": v(-131.5, 109) * mm, "radius": 2.5 * mm});
            skCircle(sketch, "E2.14.12.0", {"center": v(-131.5, 101) * mm, "radius": 2.5 * mm});
            skCircle(sketch, "E2.14.13.0", {"center": v(-131.5, 93) * mm, "radius": 2.5 * mm});
            skCircle(sketch, "E2.14.14.0", {"center": v(-131.5, 85) * mm, "radius": 2.5 * mm});
            skCircle(sketch, "E2.14.15.0", {"center": v(-131.5, 77) * mm, "radius": 2.5 * mm});
            skCircle(sketch, "E2.14.16.0", {"center": v(-131.5, 69) * mm, "radius": 2.5 * mm});
            skCircle(sketch, "E2.14.17.0", {"center": v(-131.5, 61) * mm, "radius": 2.5 * mm});
            skCircle(sketch, "E2.14.18.0", {"center": v(-131.5, 53) * mm, "radius": 2.5 * mm});
            skCircle(sketch, "E2.14.19.0", {"center": v(-131.5, 45) * mm, "radius": 2.5 * mm});
            skCircle(sketch, "E2.14.20.0", {"center": v(-131.5, 37) * mm, "radius": 2.5 * mm});
            skCircle(sketch, "E2.14.21.0", {"center": v(-131.5, 29) * mm, "radius": 2.5 * mm});
            skCircle(sketch, "E2.14.22.0", {"center": v(-131.5, 21) * mm, "radius": 2.5 * mm});
            skCircle(sketch, "E2.14.23.0", {"center": v(-131.5, 13) * mm, "radius": 2.5 * mm});
            skCircle(sketch, "E2.14.24.0", {"center": v(-131.5, 5) * mm, "radius": 2.5 * mm});
            skCircle(sketch, "E2.14.25.0", {"center": v(-131.5, -3) * mm, "radius": 2.5 * mm});
            skCircle(sketch, "E2.14.26.0", {"center": v(-131.5, -11) * mm, "radius": 2.5 * mm});
            skCircle(sketch, "E2.14.27.0", {"center": v(-131.5, -19) * mm, "radius": 2.5 * mm});
            skCircle(sketch, "E2.14.28.0", {"center": v(-131.5, -27) * mm, "radius": 2.5 * mm});
            skCircle(sketch, "E2.14.29.0", {"center": v(-131.5, -35) * mm, "radius": 2.5 * mm});
            skCircle(sketch, "E2.14.30.0", {"center": v(-131.5, -43) * mm, "radius": 2.5 * mm});
            skCircle(sketch, "E2.14.31.0", {"center": v(-131.5, -51) * mm, "radius": 2.5 * mm});
            skCircle(sketch, "E2.14.32.0", {"center": v(-131.5, -59) * mm, "radius": 2.5 * mm});
            skCircle(sketch, "E2.14.33.0", {"center": v(-131.5, -67) * mm, "radius": 2.5 * mm});
            skCircle(sketch, "E2.14.34.0", {"center": v(-131.5, -75) * mm, "radius": 2.5 * mm});
            skCircle(sketch, "E2.14.35.0", {"center": v(-131.5, -83) * mm, "radius": 2.5 * mm});
            skCircle(sketch, "E2.14.36.0", {"center": v(-131.5, -91) * mm, "radius": 2.5 * mm});
            skCircle(sketch, "E2.14.37.0", {"center": v(-131.5, -99) * mm, "radius": 2.5 * mm});
            skCircle(sketch, "E2.14.38.0", {"center": v(-131.5, -107) * mm, "radius": 2.5 * mm});
            skCircle(sketch, "E2.14.39.0", {"center": v(-131.5, -115) * mm, "radius": 2.5 * mm});
            skCircle(sketch, "E2.14.40.0", {"center": v(-131.5, -123) * mm, "radius": 2.5 * mm});
            skCircle(sketch, "E2.14.41.0", {"center": v(-131.5, -131) * mm, "radius": 2.5 * mm});
            skCircle(sketch, "E2.14.42.0", {"center": v(-131.5, -139) * mm, "radius": 2.5 * mm});
            skCircle(sketch, "E2.14.43.0", {"center": v(-131.5, -147) * mm, "radius": 2.5 * mm});
            skCircle(sketch, "E2.14.44.0", {"center": v(-131.5, -155) * mm, "radius": 2.5 * mm});
            skCircle(sketch, "E2.14.45.0", {"center": v(-131.5, -163) * mm, "radius": 2.5 * mm});
            skCircle(sketch, "E2.14.46.0", {"center": v(-131.5, -171) * mm, "radius": 2.5 * mm});
            skCircle(sketch, "E2.14.47.0", {"center": v(-131.5, -179) * mm, "radius": 2.5 * mm});
            skCircle(sketch, "E2.14.48.0", {"center": v(-131.5, -187) * mm, "radius": 2.5 * mm});
            skCircle(sketch, "E2.14.49.0", {"center": v(-131.5, -195) * mm, "radius": 2.5 * mm});
            skCircle(sketch, "E2.15.0.0", {"center": v(-123.5, 197) * mm, "radius": 2.5 * mm});
            skCircle(sketch, "E2.15.1.0", {"center": v(-123.5, 189) * mm, "radius": 2.5 * mm});
            skCircle(sketch, "E2.15.2.0", {"center": v(-123.5, 181) * mm, "radius": 2.5 * mm});
            skCircle(sketch, "E2.15.3.0", {"center": v(-123.5, 173) * mm, "radius": 2.5 * mm});
            skCircle(sketch, "E2.15.4.0", {"center": v(-123.5, 165) * mm, "radius": 2.5 * mm});
            skCircle(sketch, "E2.15.5.0", {"center": v(-123.5, 157) * mm, "radius": 2.5 * mm});
            skCircle(sketch, "E2.15.6.0", {"center": v(-123.5, 149) * mm, "radius": 2.5 * mm});
            skCircle(sketch, "E2.15.7.0", {"center": v(-123.5, 141) * mm, "radius": 2.5 * mm});
            skCircle(sketch, "E2.15.8.0", {"center": v(-123.5, 133) * mm, "radius": 2.5 * mm});
            skCircle(sketch, "E2.15.9.0", {"center": v(-123.5, 125) * mm, "radius": 2.5 * mm});
            skCircle(sketch, "E2.15.10.0", {"center": v(-123.5, 117) * mm, "radius": 2.5 * mm});
            skCircle(sketch, "E2.15.11.0", {"center": v(-123.5, 109) * mm, "radius": 2.5 * mm});
            skCircle(sketch, "E2.15.12.0", {"center": v(-123.5, 101) * mm, "radius": 2.5 * mm});
            skCircle(sketch, "E2.15.13.0", {"center": v(-123.5, 93) * mm, "radius": 2.5 * mm});
            skCircle(sketch, "E2.15.14.0", {"center": v(-123.5, 85) * mm, "radius": 2.5 * mm});
            skCircle(sketch, "E2.15.15.0", {"center": v(-123.5, 77) * mm, "radius": 2.5 * mm});
            skCircle(sketch, "E2.15.16.0", {"center": v(-123.5, 69) * mm, "radius": 2.5 * mm});
            skCircle(sketch, "E2.15.17.0", {"center": v(-123.5, 61) * mm, "radius": 2.5 * mm});
            skCircle(sketch, "E2.15.18.0", {"center": v(-123.5, 53) * mm, "radius": 2.5 * mm});
            skCircle(sketch, "E2.15.19.0", {"center": v(-123.5, 45) * mm, "radius": 2.5 * mm});
            skCircle(sketch, "E2.15.20.0", {"center": v(-123.5, 37) * mm, "radius": 2.5 * mm});
            skCircle(sketch, "E2.15.21.0", {"center": v(-123.5, 29) * mm, "radius": 2.5 * mm});
            skCircle(sketch, "E2.15.22.0", {"center": v(-123.5, 21) * mm, "radius": 2.5 * mm});
            skCircle(sketch, "E2.15.23.0", {"center": v(-123.5, 13) * mm, "radius": 2.5 * mm});
            skCircle(sketch, "E2.15.24.0", {"center": v(-123.5, 5) * mm, "radius": 2.5 * mm});
            skCircle(sketch, "E2.15.25.0", {"center": v(-123.5, -3) * mm, "radius": 2.5 * mm});
            skCircle(sketch, "E2.15.26.0", {"center": v(-123.5, -11) * mm, "radius": 2.5 * mm});
            skCircle(sketch, "E2.15.27.0", {"center": v(-123.5, -19) * mm, "radius": 2.5 * mm});
            skCircle(sketch, "E2.15.28.0", {"center": v(-123.5, -27) * mm, "radius": 2.5 * mm});
            skCircle(sketch, "E2.15.29.0", {"center": v(-123.5, -35) * mm, "radius": 2.5 * mm});
            skCircle(sketch, "E2.15.30.0", {"center": v(-123.5, -43) * mm, "radius": 2.5 * mm});
            skCircle(sketch, "E2.15.31.0", {"center": v(-123.5, -51) * mm, "radius": 2.5 * mm});
            skCircle(sketch, "E2.15.32.0", {"center": v(-123.5, -59) * mm, "radius": 2.5 * mm});
            skCircle(sketch, "E2.15.33.0", {"center": v(-123.5, -67) * mm, "radius": 2.5 * mm});
            skCircle(sketch, "E2.15.34.0", {"center": v(-123.5, -75) * mm, "radius": 2.5 * mm});
            skCircle(sketch, "E2.15.35.0", {"center": v(-123.5, -83) * mm, "radius": 2.5 * mm});
            skCircle(sketch, "E2.15.36.0", {"center": v(-123.5, -91) * mm, "radius": 2.5 * mm});
            skCircle(sketch, "E2.15.37.0", {"center": v(-123.5, -99) * mm, "radius": 2.5 * mm});
            skCircle(sketch, "E2.15.38.0", {"center": v(-123.5, -107) * mm, "radius": 2.5 * mm});
            skCircle(sketch, "E2.15.39.0", {"center": v(-123.5, -115) * mm, "radius": 2.5 * mm});
            skCircle(sketch, "E2.15.40.0", {"center": v(-123.5, -123) * mm, "radius": 2.5 * mm});
            skCircle(sketch, "E2.15.41.0", {"center": v(-123.5, -131) * mm, "radius": 2.5 * mm});
            skCircle(sketch, "E2.15.42.0", {"center": v(-123.5, -139) * mm, "radius": 2.5 * mm});
            skCircle(sketch, "E2.15.43.0", {"center": v(-123.5, -147) * mm, "radius": 2.5 * mm});
            skCircle(sketch, "E2.15.44.0", {"center": v(-123.5, -155) * mm, "radius": 2.5 * mm});
            skCircle(sketch, "E2.15.45.0", {"center": v(-123.5, -163) * mm, "radius": 2.5 * mm});
            skCircle(sketch, "E2.15.46.0", {"center": v(-123.5, -171) * mm, "radius": 2.5 * mm});
            skCircle(sketch, "E2.15.47.0", {"center": v(-123.5, -179) * mm, "radius": 2.5 * mm});
            skCircle(sketch, "E2.15.48.0", {"center": v(-123.5, -187) * mm, "radius": 2.5 * mm});
            skCircle(sketch, "E2.15.49.0", {"center": v(-123.5, -195) * mm, "radius": 2.5 * mm});
            skCircle(sketch, "E2.16.0.0", {"center": v(-115.5, 197) * mm, "radius": 2.5 * mm});
            skCircle(sketch, "E2.16.1.0", {"center": v(-115.5, 189) * mm, "radius": 2.5 * mm});
            skCircle(sketch, "E2.16.2.0", {"center": v(-115.5, 181) * mm, "radius": 2.5 * mm});
            skCircle(sketch, "E2.16.3.0", {"center": v(-115.5, 173) * mm, "radius": 2.5 * mm});
            skCircle(sketch, "E2.16.4.0", {"center": v(-115.5, 165) * mm, "radius": 2.5 * mm});
            skCircle(sketch, "E2.16.5.0", {"center": v(-115.5, 157) * mm, "radius": 2.5 * mm});
            skCircle(sketch, "E2.16.6.0", {"center": v(-115.5, 149) * mm, "radius": 2.5 * mm});
            skCircle(sketch, "E2.16.7.0", {"center": v(-115.5, 141) * mm, "radius": 2.5 * mm});
            skCircle(sketch, "E2.16.8.0", {"center": v(-115.5, 133) * mm, "radius": 2.5 * mm});
            skCircle(sketch, "E2.16.9.0", {"center": v(-115.5, 125) * mm, "radius": 2.5 * mm});
            skCircle(sketch, "E2.16.10.0", {"center": v(-115.5, 117) * mm, "radius": 2.5 * mm});
            skCircle(sketch, "E2.16.11.0", {"center": v(-115.5, 109) * mm, "radius": 2.5 * mm});
            skCircle(sketch, "E2.16.12.0", {"center": v(-115.5, 101) * mm, "radius": 2.5 * mm});
            skCircle(sketch, "E2.16.13.0", {"center": v(-115.5, 93) * mm, "radius": 2.5 * mm});
            skCircle(sketch, "E2.16.14.0", {"center": v(-115.5, 85) * mm, "radius": 2.5 * mm});
            skCircle(sketch, "E2.16.15.0", {"center": v(-115.5, 77) * mm, "radius": 2.5 * mm});
            skCircle(sketch, "E2.16.16.0", {"center": v(-115.5, 69) * mm, "radius": 2.5 * mm});
            skCircle(sketch, "E2.16.17.0", {"center": v(-115.5, 61) * mm, "radius": 2.5 * mm});
            skCircle(sketch, "E2.16.18.0", {"center": v(-115.5, 53) * mm, "radius": 2.5 * mm});
            skCircle(sketch, "E2.16.19.0", {"center": v(-115.5, 45) * mm, "radius": 2.5 * mm});
            skCircle(sketch, "E2.16.20.0", {"center": v(-115.5, 37) * mm, "radius": 2.5 * mm});
            skCircle(sketch, "E2.16.21.0", {"center": v(-115.5, 29) * mm, "radius": 2.5 * mm});
            skCircle(sketch, "E2.16.22.0", {"center": v(-115.5, 21) * mm, "radius": 2.5 * mm});
            skCircle(sketch, "E2.16.23.0", {"center": v(-115.5, 13) * mm, "radius": 2.5 * mm});
            skCircle(sketch, "E2.16.24.0", {"center": v(-115.5, 5) * mm, "radius": 2.5 * mm});
            skCircle(sketch, "E2.16.25.0", {"center": v(-115.5, -3) * mm, "radius": 2.5 * mm});
            skCircle(sketch, "E2.16.26.0", {"center": v(-115.5, -11) * mm, "radius": 2.5 * mm});
            skCircle(sketch, "E2.16.27.0", {"center": v(-115.5, -19) * mm, "radius": 2.5 * mm});
            skCircle(sketch, "E2.16.28.0", {"center": v(-115.5, -27) * mm, "radius": 2.5 * mm});
            skCircle(sketch, "E2.16.29.0", {"center": v(-115.5, -35) * mm, "radius": 2.5 * mm});
            skCircle(sketch, "E2.16.30.0", {"center": v(-115.5, -43) * mm, "radius": 2.5 * mm});
            skCircle(sketch, "E2.16.31.0", {"center": v(-115.5, -51) * mm, "radius": 2.5 * mm});
            skCircle(sketch, "E2.16.32.0", {"center": v(-115.5, -59) * mm, "radius": 2.5 * mm});
            skCircle(sketch, "E2.16.33.0", {"center": v(-115.5, -67) * mm, "radius": 2.5 * mm});
            skCircle(sketch, "E2.16.34.0", {"center": v(-115.5, -75) * mm, "radius": 2.5 * mm});
            skCircle(sketch, "E2.16.35.0", {"center": v(-115.5, -83) * mm, "radius": 2.5 * mm});
            skCircle(sketch, "E2.16.36.0", {"center": v(-115.5, -91) * mm, "radius": 2.5 * mm});
            skCircle(sketch, "E2.16.37.0", {"center": v(-115.5, -99) * mm, "radius": 2.5 * mm});
            skCircle(sketch, "E2.16.38.0", {"center": v(-115.5, -107) * mm, "radius": 2.5 * mm});
            skCircle(sketch, "E2.16.39.0", {"center": v(-115.5, -115) * mm, "radius": 2.5 * mm});
            skCircle(sketch, "E2.16.40.0", {"center": v(-115.5, -123) * mm, "radius": 2.5 * mm});
            skCircle(sketch, "E2.16.41.0", {"center": v(-115.5, -131) * mm, "radius": 2.5 * mm});
            skCircle(sketch, "E2.16.42.0", {"center": v(-115.5, -139) * mm, "radius": 2.5 * mm});
            skCircle(sketch, "E2.16.43.0", {"center": v(-115.5, -147) * mm, "radius": 2.5 * mm});
            skCircle(sketch, "E2.16.44.0", {"center": v(-115.5, -155) * mm, "radius": 2.5 * mm});
            skCircle(sketch, "E2.16.45.0", {"center": v(-115.5, -163) * mm, "radius": 2.5 * mm});
            skCircle(sketch, "E2.16.46.0", {"center": v(-115.5, -171) * mm, "radius": 2.5 * mm});
            skCircle(sketch, "E2.16.47.0", {"center": v(-115.5, -179) * mm, "radius": 2.5 * mm});
            skCircle(sketch, "E2.16.48.0", {"center": v(-115.5, -187) * mm, "radius": 2.5 * mm});
            skCircle(sketch, "E2.16.49.0", {"center": v(-115.5, -195) * mm, "radius": 2.5 * mm});
            skCircle(sketch, "E2.17.0.0", {"center": v(-107.5, 197) * mm, "radius": 2.5 * mm});
            skCircle(sketch, "E2.17.1.0", {"center": v(-107.5, 189) * mm, "radius": 2.5 * mm});
            skCircle(sketch, "E2.17.2.0", {"center": v(-107.5, 181) * mm, "radius": 2.5 * mm});
            skCircle(sketch, "E2.17.3.0", {"center": v(-107.5, 173) * mm, "radius": 2.5 * mm});
            skCircle(sketch, "E2.17.4.0", {"center": v(-107.5, 165) * mm, "radius": 2.5 * mm});
            skCircle(sketch, "E2.17.5.0", {"center": v(-107.5, 157) * mm, "radius": 2.5 * mm});
            skCircle(sketch, "E2.17.6.0", {"center": v(-107.5, 149) * mm, "radius": 2.5 * mm});
            skCircle(sketch, "E2.17.7.0", {"center": v(-107.5, 141) * mm, "radius": 2.5 * mm});
            skCircle(sketch, "E2.17.8.0", {"center": v(-107.5, 133) * mm, "radius": 2.5 * mm});
            skCircle(sketch, "E2.17.9.0", {"center": v(-107.5, 125) * mm, "radius": 2.5 * mm});
            skCircle(sketch, "E2.17.10.0", {"center": v(-107.5, 117) * mm, "radius": 2.5 * mm});
            skCircle(sketch, "E2.17.11.0", {"center": v(-107.5, 109) * mm, "radius": 2.5 * mm});
            skCircle(sketch, "E2.17.12.0", {"center": v(-107.5, 101) * mm, "radius": 2.5 * mm});
            skCircle(sketch, "E2.17.13.0", {"center": v(-107.5, 93) * mm, "radius": 2.5 * mm});
            skCircle(sketch, "E2.17.14.0", {"center": v(-107.5, 85) * mm, "radius": 2.5 * mm});
            skCircle(sketch, "E2.17.15.0", {"center": v(-107.5, 77) * mm, "radius": 2.5 * mm});
            skCircle(sketch, "E2.17.16.0", {"center": v(-107.5, 69) * mm, "radius": 2.5 * mm});
            skCircle(sketch, "E2.17.17.0", {"center": v(-107.5, 61) * mm, "radius": 2.5 * mm});
            skCircle(sketch, "E2.17.18.0", {"center": v(-107.5, 53) * mm, "radius": 2.5 * mm});
            skCircle(sketch, "E2.17.19.0", {"center": v(-107.5, 45) * mm, "radius": 2.5 * mm});
            skCircle(sketch, "E2.17.20.0", {"center": v(-107.5, 37) * mm, "radius": 2.5 * mm});
            skCircle(sketch, "E2.17.21.0", {"center": v(-107.5, 29) * mm, "radius": 2.5 * mm});
            skCircle(sketch, "E2.17.22.0", {"center": v(-107.5, 21) * mm, "radius": 2.5 * mm});
            skCircle(sketch, "E2.17.23.0", {"center": v(-107.5, 13) * mm, "radius": 2.5 * mm});
            skCircle(sketch, "E2.17.24.0", {"center": v(-107.5, 5) * mm, "radius": 2.5 * mm});
            skCircle(sketch, "E2.17.25.0", {"center": v(-107.5, -3) * mm, "radius": 2.5 * mm});
            skCircle(sketch, "E2.17.26.0", {"center": v(-107.5, -11) * mm, "radius": 2.5 * mm});
            skCircle(sketch, "E2.17.27.0", {"center": v(-107.5, -19) * mm, "radius": 2.5 * mm});
            skCircle(sketch, "E2.17.28.0", {"center": v(-107.5, -27) * mm, "radius": 2.5 * mm});
            skCircle(sketch, "E2.17.29.0", {"center": v(-107.5, -35) * mm, "radius": 2.5 * mm});
            skCircle(sketch, "E2.17.30.0", {"center": v(-107.5, -43) * mm, "radius": 2.5 * mm});
            skCircle(sketch, "E2.17.31.0", {"center": v(-107.5, -51) * mm, "radius": 2.5 * mm});
            skCircle(sketch, "E2.17.32.0", {"center": v(-107.5, -59) * mm, "radius": 2.5 * mm});
            skCircle(sketch, "E2.17.33.0", {"center": v(-107.5, -67) * mm, "radius": 2.5 * mm});
            skCircle(sketch, "E2.17.34.0", {"center": v(-107.5, -75) * mm, "radius": 2.5 * mm});
            skCircle(sketch, "E2.17.35.0", {"center": v(-107.5, -83) * mm, "radius": 2.5 * mm});
            skCircle(sketch, "E2.17.36.0", {"center": v(-107.5, -91) * mm, "radius": 2.5 * mm});
            skCircle(sketch, "E2.17.37.0", {"center": v(-107.5, -99) * mm, "radius": 2.5 * mm});
            skCircle(sketch, "E2.17.38.0", {"center": v(-107.5, -107) * mm, "radius": 2.5 * mm});
            skCircle(sketch, "E2.17.39.0", {"center": v(-107.5, -115) * mm, "radius": 2.5 * mm});
            skCircle(sketch, "E2.17.40.0", {"center": v(-107.5, -123) * mm, "radius": 2.5 * mm});
            skCircle(sketch, "E2.17.41.0", {"center": v(-107.5, -131) * mm, "radius": 2.5 * mm});
            skCircle(sketch, "E2.17.42.0", {"center": v(-107.5, -139) * mm, "radius": 2.5 * mm});
            skCircle(sketch, "E2.17.43.0", {"center": v(-107.5, -147) * mm, "radius": 2.5 * mm});
            skCircle(sketch, "E2.17.44.0", {"center": v(-107.5, -155) * mm, "radius": 2.5 * mm});
            skCircle(sketch, "E2.17.45.0", {"center": v(-107.5, -163) * mm, "radius": 2.5 * mm});
            skCircle(sketch, "E2.17.46.0", {"center": v(-107.5, -171) * mm, "radius": 2.5 * mm});
            skCircle(sketch, "E2.17.47.0", {"center": v(-107.5, -179) * mm, "radius": 2.5 * mm});
            skCircle(sketch, "E2.17.48.0", {"center": v(-107.5, -187) * mm, "radius": 2.5 * mm});
            skCircle(sketch, "E2.17.49.0", {"center": v(-107.5, -195) * mm, "radius": 2.5 * mm});
            skCircle(sketch, "E2.18.0.0", {"center": v(-99.5, 197) * mm, "radius": 2.5 * mm});
            skCircle(sketch, "E2.18.1.0", {"center": v(-99.5, 189) * mm, "radius": 2.5 * mm});
            skCircle(sketch, "E2.18.2.0", {"center": v(-99.5, 181) * mm, "radius": 2.5 * mm});
            skCircle(sketch, "E2.18.3.0", {"center": v(-99.5, 173) * mm, "radius": 2.5 * mm});
            skCircle(sketch, "E2.18.4.0", {"center": v(-99.5, 165) * mm, "radius": 2.5 * mm});
            skCircle(sketch, "E2.18.5.0", {"center": v(-99.5, 157) * mm, "radius": 2.5 * mm});
            skCircle(sketch, "E2.18.6.0", {"center": v(-99.5, 149) * mm, "radius": 2.5 * mm});
            skCircle(sketch, "E2.18.7.0", {"center": v(-99.5, 141) * mm, "radius": 2.5 * mm});
            skCircle(sketch, "E2.18.8.0", {"center": v(-99.5, 133) * mm, "radius": 2.5 * mm});
            skCircle(sketch, "E2.18.9.0", {"center": v(-99.5, 125) * mm, "radius": 2.5 * mm});
            skCircle(sketch, "E2.18.10.0", {"center": v(-99.5, 117) * mm, "radius": 2.5 * mm});
            skCircle(sketch, "E2.18.11.0", {"center": v(-99.5, 109) * mm, "radius": 2.5 * mm});
            skCircle(sketch, "E2.18.12.0", {"center": v(-99.5, 101) * mm, "radius": 2.5 * mm});
            skCircle(sketch, "E2.18.13.0", {"center": v(-99.5, 93) * mm, "radius": 2.5 * mm});
            skCircle(sketch, "E2.18.14.0", {"center": v(-99.5, 85) * mm, "radius": 2.5 * mm});
            skCircle(sketch, "E2.18.15.0", {"center": v(-99.5, 77) * mm, "radius": 2.5 * mm});
            skCircle(sketch, "E2.18.16.0", {"center": v(-99.5, 69) * mm, "radius": 2.5 * mm});
            skCircle(sketch, "E2.18.17.0", {"center": v(-99.5, 61) * mm, "radius": 2.5 * mm});
            skCircle(sketch, "E2.18.18.0", {"center": v(-99.5, 53) * mm, "radius": 2.5 * mm});
            skCircle(sketch, "E2.18.19.0", {"center": v(-99.5, 45) * mm, "radius": 2.5 * mm});
            skCircle(sketch, "E2.18.20.0", {"center": v(-99.5, 37) * mm, "radius": 2.5 * mm});
            skCircle(sketch, "E2.18.21.0", {"center": v(-99.5, 29) * mm, "radius": 2.5 * mm});
            skCircle(sketch, "E2.18.22.0", {"center": v(-99.5, 21) * mm, "radius": 2.5 * mm});
            skCircle(sketch, "E2.18.23.0", {"center": v(-99.5, 13) * mm, "radius": 2.5 * mm});
            skCircle(sketch, "E2.18.24.0", {"center": v(-99.5, 5) * mm, "radius": 2.5 * mm});
            skCircle(sketch, "E2.18.25.0", {"center": v(-99.5, -3) * mm, "radius": 2.5 * mm});
            skCircle(sketch, "E2.18.26.0", {"center": v(-99.5, -11) * mm, "radius": 2.5 * mm});
            skCircle(sketch, "E2.18.27.0", {"center": v(-99.5, -19) * mm, "radius": 2.5 * mm});
            skCircle(sketch, "E2.18.28.0", {"center": v(-99.5, -27) * mm, "radius": 2.5 * mm});
            skCircle(sketch, "E2.18.29.0", {"center": v(-99.5, -35) * mm, "radius": 2.5 * mm});
            skCircle(sketch, "E2.18.30.0", {"center": v(-99.5, -43) * mm, "radius": 2.5 * mm});
            skCircle(sketch, "E2.18.31.0", {"center": v(-99.5, -51) * mm, "radius": 2.5 * mm});
            skCircle(sketch, "E2.18.32.0", {"center": v(-99.5, -59) * mm, "radius": 2.5 * mm});
            skCircle(sketch, "E2.18.33.0", {"center": v(-99.5, -67) * mm, "radius": 2.5 * mm});
            skCircle(sketch, "E2.18.34.0", {"center": v(-99.5, -75) * mm, "radius": 2.5 * mm});
            skCircle(sketch, "E2.18.35.0", {"center": v(-99.5, -83) * mm, "radius": 2.5 * mm});
            skCircle(sketch, "E2.18.36.0", {"center": v(-99.5, -91) * mm, "radius": 2.5 * mm});
            skCircle(sketch, "E2.18.37.0", {"center": v(-99.5, -99) * mm, "radius": 2.5 * mm});
            skCircle(sketch, "E2.18.38.0", {"center": v(-99.5, -107) * mm, "radius": 2.5 * mm});
            skCircle(sketch, "E2.18.39.0", {"center": v(-99.5, -115) * mm, "radius": 2.5 * mm});
            skCircle(sketch, "E2.18.40.0", {"center": v(-99.5, -123) * mm, "radius": 2.5 * mm});
            skCircle(sketch, "E2.18.41.0", {"center": v(-99.5, -131) * mm, "radius": 2.5 * mm});
            skCircle(sketch, "E2.18.42.0", {"center": v(-99.5, -139) * mm, "radius": 2.5 * mm});
            skCircle(sketch, "E2.18.43.0", {"center": v(-99.5, -147) * mm, "radius": 2.5 * mm});
            skCircle(sketch, "E2.18.44.0", {"center": v(-99.5, -155) * mm, "radius": 2.5 * mm});
            skCircle(sketch, "E2.18.45.0", {"center": v(-99.5, -163) * mm, "radius": 2.5 * mm});
            skCircle(sketch, "E2.18.46.0", {"center": v(-99.5, -171) * mm, "radius": 2.5 * mm});
            skCircle(sketch, "E2.18.47.0", {"center": v(-99.5, -179) * mm, "radius": 2.5 * mm});
            skCircle(sketch, "E2.18.48.0", {"center": v(-99.5, -187) * mm, "radius": 2.5 * mm});
            skCircle(sketch, "E2.18.49.0", {"center": v(-99.5, -195) * mm, "radius": 2.5 * mm});
            skCircle(sketch, "E2.19.0.0", {"center": v(-91.5, 197) * mm, "radius": 2.5 * mm});
            skCircle(sketch, "E2.19.1.0", {"center": v(-91.5, 189) * mm, "radius": 2.5 * mm});
            skCircle(sketch, "E2.19.2.0", {"center": v(-91.5, 181) * mm, "radius": 2.5 * mm});
            skCircle(sketch, "E2.19.3.0", {"center": v(-91.5, 173) * mm, "radius": 2.5 * mm});
            skCircle(sketch, "E2.19.4.0", {"center": v(-91.5, 165) * mm, "radius": 2.5 * mm});
            skCircle(sketch, "E2.19.5.0", {"center": v(-91.5, 157) * mm, "radius": 2.5 * mm});
            skCircle(sketch, "E2.19.6.0", {"center": v(-91.5, 149) * mm, "radius": 2.5 * mm});
            skCircle(sketch, "E2.19.7.0", {"center": v(-91.5, 141) * mm, "radius": 2.5 * mm});
            skCircle(sketch, "E2.19.8.0", {"center": v(-91.5, 133) * mm, "radius": 2.5 * mm});
            skCircle(sketch, "E2.19.9.0", {"center": v(-91.5, 125) * mm, "radius": 2.5 * mm});
            skCircle(sketch, "E2.19.10.0", {"center": v(-91.5, 117) * mm, "radius": 2.5 * mm});
            skCircle(sketch, "E2.19.11.0", {"center": v(-91.5, 109) * mm, "radius": 2.5 * mm});
            skCircle(sketch, "E2.19.12.0", {"center": v(-91.5, 101) * mm, "radius": 2.5 * mm});
            skCircle(sketch, "E2.19.13.0", {"center": v(-91.5, 93) * mm, "radius": 2.5 * mm});
            skCircle(sketch, "E2.19.14.0", {"center": v(-91.5, 85) * mm, "radius": 2.5 * mm});
            skCircle(sketch, "E2.19.15.0", {"center": v(-91.5, 77) * mm, "radius": 2.5 * mm});
            skCircle(sketch, "E2.19.16.0", {"center": v(-91.5, 69) * mm, "radius": 2.5 * mm});
            skCircle(sketch, "E2.19.17.0", {"center": v(-91.5, 61) * mm, "radius": 2.5 * mm});
            skCircle(sketch, "E2.19.18.0", {"center": v(-91.5, 53) * mm, "radius": 2.5 * mm});
            skCircle(sketch, "E2.19.19.0", {"center": v(-91.5, 45) * mm, "radius": 2.5 * mm});
            skCircle(sketch, "E2.19.20.0", {"center": v(-91.5, 37) * mm, "radius": 2.5 * mm});
            skCircle(sketch, "E2.19.21.0", {"center": v(-91.5, 29) * mm, "radius": 2.5 * mm});
            skCircle(sketch, "E2.19.22.0", {"center": v(-91.5, 21) * mm, "radius": 2.5 * mm});
            skCircle(sketch, "E2.19.23.0", {"center": v(-91.5, 13) * mm, "radius": 2.5 * mm});
            skCircle(sketch, "E2.19.24.0", {"center": v(-91.5, 5) * mm, "radius": 2.5 * mm});
            skCircle(sketch, "E2.19.25.0", {"center": v(-91.5, -3) * mm, "radius": 2.5 * mm});
            skCircle(sketch, "E2.19.26.0", {"center": v(-91.5, -11) * mm, "radius": 2.5 * mm});
            skCircle(sketch, "E2.19.27.0", {"center": v(-91.5, -19) * mm, "radius": 2.5 * mm});
            skCircle(sketch, "E2.19.28.0", {"center": v(-91.5, -27) * mm, "radius": 2.5 * mm});
            skCircle(sketch, "E2.19.29.0", {"center": v(-91.5, -35) * mm, "radius": 2.5 * mm});
            skCircle(sketch, "E2.19.30.0", {"center": v(-91.5, -43) * mm, "radius": 2.5 * mm});
            skCircle(sketch, "E2.19.31.0", {"center": v(-91.5, -51) * mm, "radius": 2.5 * mm});
            skCircle(sketch, "E2.19.32.0", {"center": v(-91.5, -59) * mm, "radius": 2.5 * mm});
            skCircle(sketch, "E2.19.33.0", {"center": v(-91.5, -67) * mm, "radius": 2.5 * mm});
            skCircle(sketch, "E2.19.34.0", {"center": v(-91.5, -75) * mm, "radius": 2.5 * mm});
            skCircle(sketch, "E2.19.35.0", {"center": v(-91.5, -83) * mm, "radius": 2.5 * mm});
            skCircle(sketch, "E2.19.36.0", {"center": v(-91.5, -91) * mm, "radius": 2.5 * mm});
            skCircle(sketch, "E2.19.37.0", {"center": v(-91.5, -99) * mm, "radius": 2.5 * mm});
            skCircle(sketch, "E2.19.38.0", {"center": v(-91.5, -107) * mm, "radius": 2.5 * mm});
            skCircle(sketch, "E2.19.39.0", {"center": v(-91.5, -115) * mm, "radius": 2.5 * mm});
            skCircle(sketch, "E2.19.40.0", {"center": v(-91.5, -123) * mm, "radius": 2.5 * mm});
            skCircle(sketch, "E2.19.41.0", {"center": v(-91.5, -131) * mm, "radius": 2.5 * mm});
            skCircle(sketch, "E2.19.42.0", {"center": v(-91.5, -139) * mm, "radius": 2.5 * mm});
            skCircle(sketch, "E2.19.43.0", {"center": v(-91.5, -147) * mm, "radius": 2.5 * mm});
            skCircle(sketch, "E2.19.44.0", {"center": v(-91.5, -155) * mm, "radius": 2.5 * mm});
            skCircle(sketch, "E2.19.45.0", {"center": v(-91.5, -163) * mm, "radius": 2.5 * mm});
            skCircle(sketch, "E2.19.46.0", {"center": v(-91.5, -171) * mm, "radius": 2.5 * mm});
            skCircle(sketch, "E2.19.47.0", {"center": v(-91.5, -179) * mm, "radius": 2.5 * mm});
            skCircle(sketch, "E2.19.48.0", {"center": v(-91.5, -187) * mm, "radius": 2.5 * mm});
            skCircle(sketch, "E2.19.49.0", {"center": v(-91.5, -195) * mm, "radius": 2.5 * mm});
            skCircle(sketch, "E2.20.0.0", {"center": v(-83.5, 197) * mm, "radius": 2.5 * mm});
            skCircle(sketch, "E2.20.1.0", {"center": v(-83.5, 189) * mm, "radius": 2.5 * mm});
            skCircle(sketch, "E2.20.2.0", {"center": v(-83.5, 181) * mm, "radius": 2.5 * mm});
            skCircle(sketch, "E2.20.3.0", {"center": v(-83.5, 173) * mm, "radius": 2.5 * mm});
            skCircle(sketch, "E2.20.4.0", {"center": v(-83.5, 165) * mm, "radius": 2.5 * mm});
            skCircle(sketch, "E2.20.5.0", {"center": v(-83.5, 157) * mm, "radius": 2.5 * mm});
            skCircle(sketch, "E2.20.6.0", {"center": v(-83.5, 149) * mm, "radius": 2.5 * mm});
            skCircle(sketch, "E2.20.7.0", {"center": v(-83.5, 141) * mm, "radius": 2.5 * mm});
            skCircle(sketch, "E2.20.8.0", {"center": v(-83.5, 133) * mm, "radius": 2.5 * mm});
            skCircle(sketch, "E2.20.9.0", {"center": v(-83.5, 125) * mm, "radius": 2.5 * mm});
            skCircle(sketch, "E2.20.10.0", {"center": v(-83.5, 117) * mm, "radius": 2.5 * mm});
            skCircle(sketch, "E2.20.11.0", {"center": v(-83.5, 109) * mm, "radius": 2.5 * mm});
            skCircle(sketch, "E2.20.12.0", {"center": v(-83.5, 101) * mm, "radius": 2.5 * mm});
            skCircle(sketch, "E2.20.13.0", {"center": v(-83.5, 93) * mm, "radius": 2.5 * mm});
            skCircle(sketch, "E2.20.14.0", {"center": v(-83.5, 85) * mm, "radius": 2.5 * mm});
            skCircle(sketch, "E2.20.15.0", {"center": v(-83.5, 77) * mm, "radius": 2.5 * mm});
            skCircle(sketch, "E2.20.16.0", {"center": v(-83.5, 69) * mm, "radius": 2.5 * mm});
            skCircle(sketch, "E2.20.17.0", {"center": v(-83.5, 61) * mm, "radius": 2.5 * mm});
            skCircle(sketch, "E2.20.18.0", {"center": v(-83.5, 53) * mm, "radius": 2.5 * mm});
            skCircle(sketch, "E2.20.19.0", {"center": v(-83.5, 45) * mm, "radius": 2.5 * mm});
            skCircle(sketch, "E2.20.20.0", {"center": v(-83.5, 37) * mm, "radius": 2.5 * mm});
            skCircle(sketch, "E2.20.21.0", {"center": v(-83.5, 29) * mm, "radius": 2.5 * mm});
            skCircle(sketch, "E2.20.22.0", {"center": v(-83.5, 21) * mm, "radius": 2.5 * mm});
            skCircle(sketch, "E2.20.23.0", {"center": v(-83.5, 13) * mm, "radius": 2.5 * mm});
            skCircle(sketch, "E2.20.24.0", {"center": v(-83.5, 5) * mm, "radius": 2.5 * mm});
            skCircle(sketch, "E2.20.25.0", {"center": v(-83.5, -3) * mm, "radius": 2.5 * mm});
            skCircle(sketch, "E2.20.26.0", {"center": v(-83.5, -11) * mm, "radius": 2.5 * mm});
            skCircle(sketch, "E2.20.27.0", {"center": v(-83.5, -19) * mm, "radius": 2.5 * mm});
            skCircle(sketch, "E2.20.28.0", {"center": v(-83.5, -27) * mm, "radius": 2.5 * mm});
            skCircle(sketch, "E2.20.29.0", {"center": v(-83.5, -35) * mm, "radius": 2.5 * mm});
            skCircle(sketch, "E2.20.30.0", {"center": v(-83.5, -43) * mm, "radius": 2.5 * mm});
            skCircle(sketch, "E2.20.31.0", {"center": v(-83.5, -51) * mm, "radius": 2.5 * mm});
            skCircle(sketch, "E2.20.32.0", {"center": v(-83.5, -59) * mm, "radius": 2.5 * mm});
            skCircle(sketch, "E2.20.33.0", {"center": v(-83.5, -67) * mm, "radius": 2.5 * mm});
            skCircle(sketch, "E2.20.34.0", {"center": v(-83.5, -75) * mm, "radius": 2.5 * mm});
            skCircle(sketch, "E2.20.35.0", {"center": v(-83.5, -83) * mm, "radius": 2.5 * mm});
            skCircle(sketch, "E2.20.36.0", {"center": v(-83.5, -91) * mm, "radius": 2.5 * mm});
            skCircle(sketch, "E2.20.37.0", {"center": v(-83.5, -99) * mm, "radius": 2.5 * mm});
            skCircle(sketch, "E2.20.38.0", {"center": v(-83.5, -107) * mm, "radius": 2.5 * mm});
            skCircle(sketch, "E2.20.39.0", {"center": v(-83.5, -115) * mm, "radius": 2.5 * mm});
            skCircle(sketch, "E2.20.40.0", {"center": v(-83.5, -123) * mm, "radius": 2.5 * mm});
            skCircle(sketch, "E2.20.41.0", {"center": v(-83.5, -131) * mm, "radius": 2.5 * mm});
            skCircle(sketch, "E2.20.42.0", {"center": v(-83.5, -139) * mm, "radius": 2.5 * mm});
            skCircle(sketch, "E2.20.43.0", {"center": v(-83.5, -147) * mm, "radius": 2.5 * mm});
            skCircle(sketch, "E2.20.44.0", {"center": v(-83.5, -155) * mm, "radius": 2.5 * mm});
            skCircle(sketch, "E2.20.45.0", {"center": v(-83.5, -163) * mm, "radius": 2.5 * mm});
            skCircle(sketch, "E2.20.46.0", {"center": v(-83.5, -171) * mm, "radius": 2.5 * mm});
            skCircle(sketch, "E2.20.47.0", {"center": v(-83.5, -179) * mm, "radius": 2.5 * mm});
            skCircle(sketch, "E2.20.48.0", {"center": v(-83.5, -187) * mm, "radius": 2.5 * mm});
            skCircle(sketch, "E2.20.49.0", {"center": v(-83.5, -195) * mm, "radius": 2.5 * mm});
            skCircle(sketch, "E2.21.0.0", {"center": v(-75.5, 197) * mm, "radius": 2.5 * mm});
            skCircle(sketch, "E2.21.1.0", {"center": v(-75.5, 189) * mm, "radius": 2.5 * mm});
            skCircle(sketch, "E2.21.2.0", {"center": v(-75.5, 181) * mm, "radius": 2.5 * mm});
            skCircle(sketch, "E2.21.3.0", {"center": v(-75.5, 173) * mm, "radius": 2.5 * mm});
            skCircle(sketch, "E2.21.4.0", {"center": v(-75.5, 165) * mm, "radius": 2.5 * mm});
            skCircle(sketch, "E2.21.5.0", {"center": v(-75.5, 157) * mm, "radius": 2.5 * mm});
            skCircle(sketch, "E2.21.6.0", {"center": v(-75.5, 149) * mm, "radius": 2.5 * mm});
            skCircle(sketch, "E2.21.7.0", {"center": v(-75.5, 141) * mm, "radius": 2.5 * mm});
            skCircle(sketch, "E2.21.8.0", {"center": v(-75.5, 133) * mm, "radius": 2.5 * mm});
            skCircle(sketch, "E2.21.9.0", {"center": v(-75.5, 125) * mm, "radius": 2.5 * mm});
            skCircle(sketch, "E2.21.10.0", {"center": v(-75.5, 117) * mm, "radius": 2.5 * mm});
            skCircle(sketch, "E2.21.11.0", {"center": v(-75.5, 109) * mm, "radius": 2.5 * mm});
            skCircle(sketch, "E2.21.12.0", {"center": v(-75.5, 101) * mm, "radius": 2.5 * mm});
            skCircle(sketch, "E2.21.13.0", {"center": v(-75.5, 93) * mm, "radius": 2.5 * mm});
            skCircle(sketch, "E2.21.14.0", {"center": v(-75.5, 85) * mm, "radius": 2.5 * mm});
            skCircle(sketch, "E2.21.15.0", {"center": v(-75.5, 77) * mm, "radius": 2.5 * mm});
            skCircle(sketch, "E2.21.16.0", {"center": v(-75.5, 69) * mm, "radius": 2.5 * mm});
            skCircle(sketch, "E2.21.17.0", {"center": v(-75.5, 61) * mm, "radius": 2.5 * mm});
            skCircle(sketch, "E2.21.18.0", {"center": v(-75.5, 53) * mm, "radius": 2.5 * mm});
            skCircle(sketch, "E2.21.19.0", {"center": v(-75.5, 45) * mm, "radius": 2.5 * mm});
            skCircle(sketch, "E2.21.20.0", {"center": v(-75.5, 37) * mm, "radius": 2.5 * mm});
            skCircle(sketch, "E2.21.21.0", {"center": v(-75.5, 29) * mm, "radius": 2.5 * mm});
            skCircle(sketch, "E2.21.22.0", {"center": v(-75.5, 21) * mm, "radius": 2.5 * mm});
            skCircle(sketch, "E2.21.23.0", {"center": v(-75.5, 13) * mm, "radius": 2.5 * mm});
            skCircle(sketch, "E2.21.24.0", {"center": v(-75.5, 5) * mm, "radius": 2.5 * mm});
            skCircle(sketch, "E2.21.25.0", {"center": v(-75.5, -3) * mm, "radius": 2.5 * mm});
            skCircle(sketch, "E2.21.26.0", {"center": v(-75.5, -11) * mm, "radius": 2.5 * mm});
            skCircle(sketch, "E2.21.27.0", {"center": v(-75.5, -19) * mm, "radius": 2.5 * mm});
            skCircle(sketch, "E2.21.28.0", {"center": v(-75.5, -27) * mm, "radius": 2.5 * mm});
            skCircle(sketch, "E2.21.29.0", {"center": v(-75.5, -35) * mm, "radius": 2.5 * mm});
            skCircle(sketch, "E2.21.30.0", {"center": v(-75.5, -43) * mm, "radius": 2.5 * mm});
            skCircle(sketch, "E2.21.31.0", {"center": v(-75.5, -51) * mm, "radius": 2.5 * mm});
            skCircle(sketch, "E2.21.32.0", {"center": v(-75.5, -59) * mm, "radius": 2.5 * mm});
            skCircle(sketch, "E2.21.33.0", {"center": v(-75.5, -67) * mm, "radius": 2.5 * mm});
            skCircle(sketch, "E2.21.34.0", {"center": v(-75.5, -75) * mm, "radius": 2.5 * mm});
            skCircle(sketch, "E2.21.35.0", {"center": v(-75.5, -83) * mm, "radius": 2.5 * mm});
            skCircle(sketch, "E2.21.36.0", {"center": v(-75.5, -91) * mm, "radius": 2.5 * mm});
            skCircle(sketch, "E2.21.37.0", {"center": v(-75.5, -99) * mm, "radius": 2.5 * mm});
            skCircle(sketch, "E2.21.38.0", {"center": v(-75.5, -107) * mm, "radius": 2.5 * mm});
            skCircle(sketch, "E2.21.39.0", {"center": v(-75.5, -115) * mm, "radius": 2.5 * mm});
            skCircle(sketch, "E2.21.40.0", {"center": v(-75.5, -123) * mm, "radius": 2.5 * mm});
            skCircle(sketch, "E2.21.41.0", {"center": v(-75.5, -131) * mm, "radius": 2.5 * mm});
            skCircle(sketch, "E2.21.42.0", {"center": v(-75.5, -139) * mm, "radius": 2.5 * mm});
            skCircle(sketch, "E2.21.43.0", {"center": v(-75.5, -147) * mm, "radius": 2.5 * mm});
            skCircle(sketch, "E2.21.44.0", {"center": v(-75.5, -155) * mm, "radius": 2.5 * mm});
            skCircle(sketch, "E2.21.45.0", {"center": v(-75.5, -163) * mm, "radius": 2.5 * mm});
            skCircle(sketch, "E2.21.46.0", {"center": v(-75.5, -171) * mm, "radius": 2.5 * mm});
            skCircle(sketch, "E2.21.47.0", {"center": v(-75.5, -179) * mm, "radius": 2.5 * mm});
            skCircle(sketch, "E2.21.48.0", {"center": v(-75.5, -187) * mm, "radius": 2.5 * mm});
            skCircle(sketch, "E2.21.49.0", {"center": v(-75.5, -195) * mm, "radius": 2.5 * mm});
            skCircle(sketch, "E2.22.0.0", {"center": v(-67.5, 197) * mm, "radius": 2.5 * mm});
            skCircle(sketch, "E2.22.1.0", {"center": v(-67.5, 189) * mm, "radius": 2.5 * mm});
            skCircle(sketch, "E2.22.2.0", {"center": v(-67.5, 181) * mm, "radius": 2.5 * mm});
            skCircle(sketch, "E2.22.3.0", {"center": v(-67.5, 173) * mm, "radius": 2.5 * mm});
            skCircle(sketch, "E2.22.4.0", {"center": v(-67.5, 165) * mm, "radius": 2.5 * mm});
            skCircle(sketch, "E2.22.5.0", {"center": v(-67.5, 157) * mm, "radius": 2.5 * mm});
            skCircle(sketch, "E2.22.6.0", {"center": v(-67.5, 149) * mm, "radius": 2.5 * mm});
            skCircle(sketch, "E2.22.7.0", {"center": v(-67.5, 141) * mm, "radius": 2.5 * mm});
            skCircle(sketch, "E2.22.8.0", {"center": v(-67.5, 133) * mm, "radius": 2.5 * mm});
            skCircle(sketch, "E2.22.9.0", {"center": v(-67.5, 125) * mm, "radius": 2.5 * mm});
            skCircle(sketch, "E2.22.10.0", {"center": v(-67.5, 117) * mm, "radius": 2.5 * mm});
            skCircle(sketch, "E2.22.11.0", {"center": v(-67.5, 109) * mm, "radius": 2.5 * mm});
            skCircle(sketch, "E2.22.12.0", {"center": v(-67.5, 101) * mm, "radius": 2.5 * mm});
            skCircle(sketch, "E2.22.13.0", {"center": v(-67.5, 93) * mm, "radius": 2.5 * mm});
            skCircle(sketch, "E2.22.14.0", {"center": v(-67.5, 85) * mm, "radius": 2.5 * mm});
            skCircle(sketch, "E2.22.15.0", {"center": v(-67.5, 77) * mm, "radius": 2.5 * mm});
            skCircle(sketch, "E2.22.16.0", {"center": v(-67.5, 69) * mm, "radius": 2.5 * mm});
            skCircle(sketch, "E2.22.17.0", {"center": v(-67.5, 61) * mm, "radius": 2.5 * mm});
            skCircle(sketch, "E2.22.18.0", {"center": v(-67.5, 53) * mm, "radius": 2.5 * mm});
            skCircle(sketch, "E2.22.19.0", {"center": v(-67.5, 45) * mm, "radius": 2.5 * mm});
            skCircle(sketch, "E2.22.20.0", {"center": v(-67.5, 37) * mm, "radius": 2.5 * mm});
            skCircle(sketch, "E2.22.21.0", {"center": v(-67.5, 29) * mm, "radius": 2.5 * mm});
            skCircle(sketch, "E2.22.22.0", {"center": v(-67.5, 21) * mm, "radius": 2.5 * mm});
            skCircle(sketch, "E2.22.23.0", {"center": v(-67.5, 13) * mm, "radius": 2.5 * mm});
            skCircle(sketch, "E2.22.24.0", {"center": v(-67.5, 5) * mm, "radius": 2.5 * mm});
            skCircle(sketch, "E2.22.25.0", {"center": v(-67.5, -3) * mm, "radius": 2.5 * mm});
            skCircle(sketch, "E2.22.26.0", {"center": v(-67.5, -11) * mm, "radius": 2.5 * mm});
            skCircle(sketch, "E2.22.27.0", {"center": v(-67.5, -19) * mm, "radius": 2.5 * mm});
            skCircle(sketch, "E2.22.28.0", {"center": v(-67.5, -27) * mm, "radius": 2.5 * mm});
            skCircle(sketch, "E2.22.29.0", {"center": v(-67.5, -35) * mm, "radius": 2.5 * mm});
            skCircle(sketch, "E2.22.30.0", {"center": v(-67.5, -43) * mm, "radius": 2.5 * mm});
            skCircle(sketch, "E2.22.31.0", {"center": v(-67.5, -51) * mm, "radius": 2.5 * mm});
            skCircle(sketch, "E2.22.32.0", {"center": v(-67.5, -59) * mm, "radius": 2.5 * mm});
            skCircle(sketch, "E2.22.33.0", {"center": v(-67.5, -67) * mm, "radius": 2.5 * mm});
            skCircle(sketch, "E2.22.34.0", {"center": v(-67.5, -75) * mm, "radius": 2.5 * mm});
            skCircle(sketch, "E2.22.35.0", {"center": v(-67.5, -83) * mm, "radius": 2.5 * mm});
            skCircle(sketch, "E2.22.36.0", {"center": v(-67.5, -91) * mm, "radius": 2.5 * mm});
            skCircle(sketch, "E2.22.37.0", {"center": v(-67.5, -99) * mm, "radius": 2.5 * mm});
            skCircle(sketch, "E2.22.38.0", {"center": v(-67.5, -107) * mm, "radius": 2.5 * mm});
            skCircle(sketch, "E2.22.39.0", {"center": v(-67.5, -115) * mm, "radius": 2.5 * mm});
            skCircle(sketch, "E2.22.40.0", {"center": v(-67.5, -123) * mm, "radius": 2.5 * mm});
            skCircle(sketch, "E2.22.41.0", {"center": v(-67.5, -131) * mm, "radius": 2.5 * mm});
            skCircle(sketch, "E2.22.42.0", {"center": v(-67.5, -139) * mm, "radius": 2.5 * mm});
            skCircle(sketch, "E2.22.43.0", {"center": v(-67.5, -147) * mm, "radius": 2.5 * mm});
            skCircle(sketch, "E2.22.44.0", {"center": v(-67.5, -155) * mm, "radius": 2.5 * mm});
            skCircle(sketch, "E2.22.45.0", {"center": v(-67.5, -163) * mm, "radius": 2.5 * mm});
            skCircle(sketch, "E2.22.46.0", {"center": v(-67.5, -171) * mm, "radius": 2.5 * mm});
            skCircle(sketch, "E2.22.47.0", {"center": v(-67.5, -179) * mm, "radius": 2.5 * mm});
            skCircle(sketch, "E2.22.48.0", {"center": v(-67.5, -187) * mm, "radius": 2.5 * mm});
            skCircle(sketch, "E2.22.49.0", {"center": v(-67.5, -195) * mm, "radius": 2.5 * mm});
            skCircle(sketch, "E2.23.0.0", {"center": v(-59.5, 197) * mm, "radius": 2.5 * mm});
            skCircle(sketch, "E2.23.1.0", {"center": v(-59.5, 189) * mm, "radius": 2.5 * mm});
            skCircle(sketch, "E2.23.2.0", {"center": v(-59.5, 181) * mm, "radius": 2.5 * mm});
            skCircle(sketch, "E2.23.3.0", {"center": v(-59.5, 173) * mm, "radius": 2.5 * mm});
            skCircle(sketch, "E2.23.4.0", {"center": v(-59.5, 165) * mm, "radius": 2.5 * mm});
            skCircle(sketch, "E2.23.5.0", {"center": v(-59.5, 157) * mm, "radius": 2.5 * mm});
            skCircle(sketch, "E2.23.6.0", {"center": v(-59.5, 149) * mm, "radius": 2.5 * mm});
            skCircle(sketch, "E2.23.7.0", {"center": v(-59.5, 141) * mm, "radius": 2.5 * mm});
            skCircle(sketch, "E2.23.8.0", {"center": v(-59.5, 133) * mm, "radius": 2.5 * mm});
            skCircle(sketch, "E2.23.9.0", {"center": v(-59.5, 125) * mm, "radius": 2.5 * mm});
            skCircle(sketch, "E2.23.10.0", {"center": v(-59.5, 117) * mm, "radius": 2.5 * mm});
            skCircle(sketch, "E2.23.11.0", {"center": v(-59.5, 109) * mm, "radius": 2.5 * mm});
            skCircle(sketch, "E2.23.12.0", {"center": v(-59.5, 101) * mm, "radius": 2.5 * mm});
            skCircle(sketch, "E2.23.13.0", {"center": v(-59.5, 93) * mm, "radius": 2.5 * mm});
            skCircle(sketch, "E2.23.14.0", {"center": v(-59.5, 85) * mm, "radius": 2.5 * mm});
            skCircle(sketch, "E2.23.15.0", {"center": v(-59.5, 77) * mm, "radius": 2.5 * mm});
            skCircle(sketch, "E2.23.16.0", {"center": v(-59.5, 69) * mm, "radius": 2.5 * mm});
            skCircle(sketch, "E2.23.17.0", {"center": v(-59.5, 61) * mm, "radius": 2.5 * mm});
            skCircle(sketch, "E2.23.18.0", {"center": v(-59.5, 53) * mm, "radius": 2.5 * mm});
            skCircle(sketch, "E2.23.19.0", {"center": v(-59.5, 45) * mm, "radius": 2.5 * mm});
            skCircle(sketch, "E2.23.20.0", {"center": v(-59.5, 37) * mm, "radius": 2.5 * mm});
            skCircle(sketch, "E2.23.21.0", {"center": v(-59.5, 29) * mm, "radius": 2.5 * mm});
            skCircle(sketch, "E2.23.22.0", {"center": v(-59.5, 21) * mm, "radius": 2.5 * mm});
            skCircle(sketch, "E2.23.23.0", {"center": v(-59.5, 13) * mm, "radius": 2.5 * mm});
            skCircle(sketch, "E2.23.24.0", {"center": v(-59.5, 5) * mm, "radius": 2.5 * mm});
            skCircle(sketch, "E2.23.25.0", {"center": v(-59.5, -3) * mm, "radius": 2.5 * mm});
            skCircle(sketch, "E2.23.26.0", {"center": v(-59.5, -11) * mm, "radius": 2.5 * mm});
            skCircle(sketch, "E2.23.27.0", {"center": v(-59.5, -19) * mm, "radius": 2.5 * mm});
            skCircle(sketch, "E2.23.28.0", {"center": v(-59.5, -27) * mm, "radius": 2.5 * mm});
            skCircle(sketch, "E2.23.29.0", {"center": v(-59.5, -35) * mm, "radius": 2.5 * mm});
            skCircle(sketch, "E2.23.30.0", {"center": v(-59.5, -43) * mm, "radius": 2.5 * mm});
            skCircle(sketch, "E2.23.31.0", {"center": v(-59.5, -51) * mm, "radius": 2.5 * mm});
            skCircle(sketch, "E2.23.32.0", {"center": v(-59.5, -59) * mm, "radius": 2.5 * mm});
            skCircle(sketch, "E2.23.33.0", {"center": v(-59.5, -67) * mm, "radius": 2.5 * mm});
            skCircle(sketch, "E2.23.34.0", {"center": v(-59.5, -75) * mm, "radius": 2.5 * mm});
            skCircle(sketch, "E2.23.35.0", {"center": v(-59.5, -83) * mm, "radius": 2.5 * mm});
            skCircle(sketch, "E2.23.36.0", {"center": v(-59.5, -91) * mm, "radius": 2.5 * mm});
            skCircle(sketch, "E2.23.37.0", {"center": v(-59.5, -99) * mm, "radius": 2.5 * mm});
            skCircle(sketch, "E2.23.38.0", {"center": v(-59.5, -107) * mm, "radius": 2.5 * mm});
            skCircle(sketch, "E2.23.39.0", {"center": v(-59.5, -115) * mm, "radius": 2.5 * mm});
            skCircle(sketch, "E2.23.40.0", {"center": v(-59.5, -123) * mm, "radius": 2.5 * mm});
            skCircle(sketch, "E2.23.41.0", {"center": v(-59.5, -131) * mm, "radius": 2.5 * mm});
            skCircle(sketch, "E2.23.42.0", {"center": v(-59.5, -139) * mm, "radius": 2.5 * mm});
            skCircle(sketch, "E2.23.43.0", {"center": v(-59.5, -147) * mm, "radius": 2.5 * mm});
            skCircle(sketch, "E2.23.44.0", {"center": v(-59.5, -155) * mm, "radius": 2.5 * mm});
            skCircle(sketch, "E2.23.45.0", {"center": v(-59.5, -163) * mm, "radius": 2.5 * mm});
            skCircle(sketch, "E2.23.46.0", {"center": v(-59.5, -171) * mm, "radius": 2.5 * mm});
            skCircle(sketch, "E2.23.47.0", {"center": v(-59.5, -179) * mm, "radius": 2.5 * mm});
            skCircle(sketch, "E2.23.48.0", {"center": v(-59.5, -187) * mm, "radius": 2.5 * mm});
            skCircle(sketch, "E2.23.49.0", {"center": v(-59.5, -195) * mm, "radius": 2.5 * mm});
            skCircle(sketch, "E2.24.0.0", {"center": v(-51.5, 197) * mm, "radius": 2.5 * mm});
            skCircle(sketch, "E2.24.1.0", {"center": v(-51.5, 189) * mm, "radius": 2.5 * mm});
            skCircle(sketch, "E2.24.2.0", {"center": v(-51.5, 181) * mm, "radius": 2.5 * mm});
            skCircle(sketch, "E2.24.3.0", {"center": v(-51.5, 173) * mm, "radius": 2.5 * mm});
            skCircle(sketch, "E2.24.4.0", {"center": v(-51.5, 165) * mm, "radius": 2.5 * mm});
            skCircle(sketch, "E2.24.5.0", {"center": v(-51.5, 157) * mm, "radius": 2.5 * mm});
            skCircle(sketch, "E2.24.6.0", {"center": v(-51.5, 149) * mm, "radius": 2.5 * mm});
            skCircle(sketch, "E2.24.7.0", {"center": v(-51.5, 141) * mm, "radius": 2.5 * mm});
            skCircle(sketch, "E2.24.8.0", {"center": v(-51.5, 133) * mm, "radius": 2.5 * mm});
            skCircle(sketch, "E2.24.9.0", {"center": v(-51.5, 125) * mm, "radius": 2.5 * mm});
            skCircle(sketch, "E2.24.10.0", {"center": v(-51.5, 117) * mm, "radius": 2.5 * mm});
            skCircle(sketch, "E2.24.11.0", {"center": v(-51.5, 109) * mm, "radius": 2.5 * mm});
            skCircle(sketch, "E2.24.12.0", {"center": v(-51.5, 101) * mm, "radius": 2.5 * mm});
            skCircle(sketch, "E2.24.13.0", {"center": v(-51.5, 93) * mm, "radius": 2.5 * mm});
            skCircle(sketch, "E2.24.14.0", {"center": v(-51.5, 85) * mm, "radius": 2.5 * mm});
            skCircle(sketch, "E2.24.15.0", {"center": v(-51.5, 77) * mm, "radius": 2.5 * mm});
            skCircle(sketch, "E2.24.16.0", {"center": v(-51.5, 69) * mm, "radius": 2.5 * mm});
            skCircle(sketch, "E2.24.17.0", {"center": v(-51.5, 61) * mm, "radius": 2.5 * mm});
            skCircle(sketch, "E2.24.18.0", {"center": v(-51.5, 53) * mm, "radius": 2.5 * mm});
            skCircle(sketch, "E2.24.19.0", {"center": v(-51.5, 45) * mm, "radius": 2.5 * mm});
            skCircle(sketch, "E2.24.20.0", {"center": v(-51.5, 37) * mm, "radius": 2.5 * mm});
            skCircle(sketch, "E2.24.21.0", {"center": v(-51.5, 29) * mm, "radius": 2.5 * mm});
            skCircle(sketch, "E2.24.22.0", {"center": v(-51.5, 21) * mm, "radius": 2.5 * mm});
            skCircle(sketch, "E2.24.23.0", {"center": v(-51.5, 13) * mm, "radius": 2.5 * mm});
            skCircle(sketch, "E2.24.24.0", {"center": v(-51.5, 5) * mm, "radius": 2.5 * mm});
            skCircle(sketch, "E2.24.25.0", {"center": v(-51.5, -3) * mm, "radius": 2.5 * mm});
            skCircle(sketch, "E2.24.26.0", {"center": v(-51.5, -11) * mm, "radius": 2.5 * mm});
            skCircle(sketch, "E2.24.27.0", {"center": v(-51.5, -19) * mm, "radius": 2.5 * mm});
            skCircle(sketch, "E2.24.28.0", {"center": v(-51.5, -27) * mm, "radius": 2.5 * mm});
            skCircle(sketch, "E2.24.29.0", {"center": v(-51.5, -35) * mm, "radius": 2.5 * mm});
            skCircle(sketch, "E2.24.30.0", {"center": v(-51.5, -43) * mm, "radius": 2.5 * mm});
            skCircle(sketch, "E2.24.31.0", {"center": v(-51.5, -51) * mm, "radius": 2.5 * mm});
            skCircle(sketch, "E2.24.32.0", {"center": v(-51.5, -59) * mm, "radius": 2.5 * mm});
            skCircle(sketch, "E2.24.33.0", {"center": v(-51.5, -67) * mm, "radius": 2.5 * mm});
            skCircle(sketch, "E2.24.34.0", {"center": v(-51.5, -75) * mm, "radius": 2.5 * mm});
            skCircle(sketch, "E2.24.35.0", {"center": v(-51.5, -83) * mm, "radius": 2.5 * mm});
            skCircle(sketch, "E2.24.36.0", {"center": v(-51.5, -91) * mm, "radius": 2.5 * mm});
            skCircle(sketch, "E2.24.37.0", {"center": v(-51.5, -99) * mm, "radius": 2.5 * mm});
            skCircle(sketch, "E2.24.38.0", {"center": v(-51.5, -107) * mm, "radius": 2.5 * mm});
            skCircle(sketch, "E2.24.39.0", {"center": v(-51.5, -115) * mm, "radius": 2.5 * mm});
            skCircle(sketch, "E2.24.40.0", {"center": v(-51.5, -123) * mm, "radius": 2.5 * mm});
            skCircle(sketch, "E2.24.41.0", {"center": v(-51.5, -131) * mm, "radius": 2.5 * mm});
            skCircle(sketch, "E2.24.42.0", {"center": v(-51.5, -139) * mm, "radius": 2.5 * mm});
            skCircle(sketch, "E2.24.43.0", {"center": v(-51.5, -147) * mm, "radius": 2.5 * mm});
            skCircle(sketch, "E2.24.44.0", {"center": v(-51.5, -155) * mm, "radius": 2.5 * mm});
            skCircle(sketch, "E2.24.45.0", {"center": v(-51.5, -163) * mm, "radius": 2.5 * mm});
            skCircle(sketch, "E2.24.46.0", {"center": v(-51.5, -171) * mm, "radius": 2.5 * mm});
            skCircle(sketch, "E2.24.47.0", {"center": v(-51.5, -179) * mm, "radius": 2.5 * mm});
            skCircle(sketch, "E2.24.48.0", {"center": v(-51.5, -187) * mm, "radius": 2.5 * mm});
            skCircle(sketch, "E2.24.49.0", {"center": v(-51.5, -195) * mm, "radius": 2.5 * mm});
            skCircle(sketch, "E2.25.0.0", {"center": v(-43.5, 197) * mm, "radius": 2.5 * mm});
            skCircle(sketch, "E2.25.1.0", {"center": v(-43.5, 189) * mm, "radius": 2.5 * mm});
            skCircle(sketch, "E2.25.2.0", {"center": v(-43.5, 181) * mm, "radius": 2.5 * mm});
            skCircle(sketch, "E2.25.3.0", {"center": v(-43.5, 173) * mm, "radius": 2.5 * mm});
            skCircle(sketch, "E2.25.4.0", {"center": v(-43.5, 165) * mm, "radius": 2.5 * mm});
            skCircle(sketch, "E2.25.5.0", {"center": v(-43.5, 157) * mm, "radius": 2.5 * mm});
            skCircle(sketch, "E2.25.6.0", {"center": v(-43.5, 149) * mm, "radius": 2.5 * mm});
            skCircle(sketch, "E2.25.7.0", {"center": v(-43.5, 141) * mm, "radius": 2.5 * mm});
            skCircle(sketch, "E2.25.8.0", {"center": v(-43.5, 133) * mm, "radius": 2.5 * mm});
            skCircle(sketch, "E2.25.9.0", {"center": v(-43.5, 125) * mm, "radius": 2.5 * mm});
            skCircle(sketch, "E2.25.10.0", {"center": v(-43.5, 117) * mm, "radius": 2.5 * mm});
            skCircle(sketch, "E2.25.11.0", {"center": v(-43.5, 109) * mm, "radius": 2.5 * mm});
            skCircle(sketch, "E2.25.12.0", {"center": v(-43.5, 101) * mm, "radius": 2.5 * mm});
            skCircle(sketch, "E2.25.13.0", {"center": v(-43.5, 93) * mm, "radius": 2.5 * mm});
            skCircle(sketch, "E2.25.14.0", {"center": v(-43.5, 85) * mm, "radius": 2.5 * mm});
            skCircle(sketch, "E2.25.15.0", {"center": v(-43.5, 77) * mm, "radius": 2.5 * mm});
            skCircle(sketch, "E2.25.16.0", {"center": v(-43.5, 69) * mm, "radius": 2.5 * mm});
            skCircle(sketch, "E2.25.17.0", {"center": v(-43.5, 61) * mm, "radius": 2.5 * mm});
            skCircle(sketch, "E2.25.18.0", {"center": v(-43.5, 53) * mm, "radius": 2.5 * mm});
            skCircle(sketch, "E2.25.19.0", {"center": v(-43.5, 45) * mm, "radius": 2.5 * mm});
            skCircle(sketch, "E2.25.20.0", {"center": v(-43.5, 37) * mm, "radius": 2.5 * mm});
            skCircle(sketch, "E2.25.21.0", {"center": v(-43.5, 29) * mm, "radius": 2.5 * mm});
            skCircle(sketch, "E2.25.22.0", {"center": v(-43.5, 21) * mm, "radius": 2.5 * mm});
            skCircle(sketch, "E2.25.23.0", {"center": v(-43.5, 13) * mm, "radius": 2.5 * mm});
            skCircle(sketch, "E2.25.24.0", {"center": v(-43.5, 5) * mm, "radius": 2.5 * mm});
            skCircle(sketch, "E2.25.25.0", {"center": v(-43.5, -3) * mm, "radius": 2.5 * mm});
            skCircle(sketch, "E2.25.26.0", {"center": v(-43.5, -11) * mm, "radius": 2.5 * mm});
            skCircle(sketch, "E2.25.27.0", {"center": v(-43.5, -19) * mm, "radius": 2.5 * mm});
            skCircle(sketch, "E2.25.28.0", {"center": v(-43.5, -27) * mm, "radius": 2.5 * mm});
            skCircle(sketch, "E2.25.29.0", {"center": v(-43.5, -35) * mm, "radius": 2.5 * mm});
            skCircle(sketch, "E2.25.30.0", {"center": v(-43.5, -43) * mm, "radius": 2.5 * mm});
            skCircle(sketch, "E2.25.31.0", {"center": v(-43.5, -51) * mm, "radius": 2.5 * mm});
            skCircle(sketch, "E2.25.32.0", {"center": v(-43.5, -59) * mm, "radius": 2.5 * mm});
            skCircle(sketch, "E2.25.33.0", {"center": v(-43.5, -67) * mm, "radius": 2.5 * mm});
            skCircle(sketch, "E2.25.34.0", {"center": v(-43.5, -75) * mm, "radius": 2.5 * mm});
            skCircle(sketch, "E2.25.35.0", {"center": v(-43.5, -83) * mm, "radius": 2.5 * mm});
            skCircle(sketch, "E2.25.36.0", {"center": v(-43.5, -91) * mm, "radius": 2.5 * mm});
            skCircle(sketch, "E2.25.37.0", {"center": v(-43.5, -99) * mm, "radius": 2.5 * mm});
            skCircle(sketch, "E2.25.38.0", {"center": v(-43.5, -107) * mm, "radius": 2.5 * mm});
            skCircle(sketch, "E2.25.39.0", {"center": v(-43.5, -115) * mm, "radius": 2.5 * mm});
            skCircle(sketch, "E2.25.40.0", {"center": v(-43.5, -123) * mm, "radius": 2.5 * mm});
            skCircle(sketch, "E2.25.41.0", {"center": v(-43.5, -131) * mm, "radius": 2.5 * mm});
            skCircle(sketch, "E2.25.42.0", {"center": v(-43.5, -139) * mm, "radius": 2.5 * mm});
            skCircle(sketch, "E2.25.43.0", {"center": v(-43.5, -147) * mm, "radius": 2.5 * mm});
            skCircle(sketch, "E2.25.44.0", {"center": v(-43.5, -155) * mm, "radius": 2.5 * mm});
            skCircle(sketch, "E2.25.45.0", {"center": v(-43.5, -163) * mm, "radius": 2.5 * mm});
            skCircle(sketch, "E2.25.46.0", {"center": v(-43.5, -171) * mm, "radius": 2.5 * mm});
            skCircle(sketch, "E2.25.47.0", {"center": v(-43.5, -179) * mm, "radius": 2.5 * mm});
            skCircle(sketch, "E2.25.48.0", {"center": v(-43.5, -187) * mm, "radius": 2.5 * mm});
            skCircle(sketch, "E2.25.49.0", {"center": v(-43.5, -195) * mm, "radius": 2.5 * mm});
            skCircle(sketch, "E2.26.0.0", {"center": v(-35.5, 197) * mm, "radius": 2.5 * mm});
            skCircle(sketch, "E2.26.1.0", {"center": v(-35.5, 189) * mm, "radius": 2.5 * mm});
            skCircle(sketch, "E2.26.2.0", {"center": v(-35.5, 181) * mm, "radius": 2.5 * mm});
            skCircle(sketch, "E2.26.3.0", {"center": v(-35.5, 173) * mm, "radius": 2.5 * mm});
            skCircle(sketch, "E2.26.4.0", {"center": v(-35.5, 165) * mm, "radius": 2.5 * mm});
            skCircle(sketch, "E2.26.5.0", {"center": v(-35.5, 157) * mm, "radius": 2.5 * mm});
            skCircle(sketch, "E2.26.6.0", {"center": v(-35.5, 149) * mm, "radius": 2.5 * mm});
            skCircle(sketch, "E2.26.7.0", {"center": v(-35.5, 141) * mm, "radius": 2.5 * mm});
            skCircle(sketch, "E2.26.8.0", {"center": v(-35.5, 133) * mm, "radius": 2.5 * mm});
            skCircle(sketch, "E2.26.9.0", {"center": v(-35.5, 125) * mm, "radius": 2.5 * mm});
            skCircle(sketch, "E2.26.10.0", {"center": v(-35.5, 117) * mm, "radius": 2.5 * mm});
            skCircle(sketch, "E2.26.11.0", {"center": v(-35.5, 109) * mm, "radius": 2.5 * mm});
            skCircle(sketch, "E2.26.12.0", {"center": v(-35.5, 101) * mm, "radius": 2.5 * mm});
            skCircle(sketch, "E2.26.13.0", {"center": v(-35.5, 93) * mm, "radius": 2.5 * mm});
            skCircle(sketch, "E2.26.14.0", {"center": v(-35.5, 85) * mm, "radius": 2.5 * mm});
            skCircle(sketch, "E2.26.15.0", {"center": v(-35.5, 77) * mm, "radius": 2.5 * mm});
            skCircle(sketch, "E2.26.16.0", {"center": v(-35.5, 69) * mm, "radius": 2.5 * mm});
            skCircle(sketch, "E2.26.17.0", {"center": v(-35.5, 61) * mm, "radius": 2.5 * mm});
            skCircle(sketch, "E2.26.18.0", {"center": v(-35.5, 53) * mm, "radius": 2.5 * mm});
            skCircle(sketch, "E2.26.19.0", {"center": v(-35.5, 45) * mm, "radius": 2.5 * mm});
            skCircle(sketch, "E2.26.20.0", {"center": v(-35.5, 37) * mm, "radius": 2.5 * mm});
            skCircle(sketch, "E2.26.21.0", {"center": v(-35.5, 29) * mm, "radius": 2.5 * mm});
            skCircle(sketch, "E2.26.22.0", {"center": v(-35.5, 21) * mm, "radius": 2.5 * mm});
            skCircle(sketch, "E2.26.23.0", {"center": v(-35.5, 13) * mm, "radius": 2.5 * mm});
            skCircle(sketch, "E2.26.24.0", {"center": v(-35.5, 5) * mm, "radius": 2.5 * mm});
            skCircle(sketch, "E2.26.25.0", {"center": v(-35.5, -3) * mm, "radius": 2.5 * mm});
            skCircle(sketch, "E2.26.26.0", {"center": v(-35.5, -11) * mm, "radius": 2.5 * mm});
            skCircle(sketch, "E2.26.27.0", {"center": v(-35.5, -19) * mm, "radius": 2.5 * mm});
            skCircle(sketch, "E2.26.28.0", {"center": v(-35.5, -27) * mm, "radius": 2.5 * mm});
            skCircle(sketch, "E2.26.29.0", {"center": v(-35.5, -35) * mm, "radius": 2.5 * mm});
            skCircle(sketch, "E2.26.30.0", {"center": v(-35.5, -43) * mm, "radius": 2.5 * mm});
            skCircle(sketch, "E2.26.31.0", {"center": v(-35.5, -51) * mm, "radius": 2.5 * mm});
            skCircle(sketch, "E2.26.32.0", {"center": v(-35.5, -59) * mm, "radius": 2.5 * mm});
            skCircle(sketch, "E2.26.33.0", {"center": v(-35.5, -67) * mm, "radius": 2.5 * mm});
            skCircle(sketch, "E2.26.34.0", {"center": v(-35.5, -75) * mm, "radius": 2.5 * mm});
            skCircle(sketch, "E2.26.35.0", {"center": v(-35.5, -83) * mm, "radius": 2.5 * mm});
            skCircle(sketch, "E2.26.36.0", {"center": v(-35.5, -91) * mm, "radius": 2.5 * mm});
            skCircle(sketch, "E2.26.37.0", {"center": v(-35.5, -99) * mm, "radius": 2.5 * mm});
            skCircle(sketch, "E2.26.38.0", {"center": v(-35.5, -107) * mm, "radius": 2.5 * mm});
            skCircle(sketch, "E2.26.39.0", {"center": v(-35.5, -115) * mm, "radius": 2.5 * mm});
            skCircle(sketch, "E2.26.40.0", {"center": v(-35.5, -123) * mm, "radius": 2.5 * mm});
            skCircle(sketch, "E2.26.41.0", {"center": v(-35.5, -131) * mm, "radius": 2.5 * mm});
            skCircle(sketch, "E2.26.42.0", {"center": v(-35.5, -139) * mm, "radius": 2.5 * mm});
            skCircle(sketch, "E2.26.43.0", {"center": v(-35.5, -147) * mm, "radius": 2.5 * mm});
            skCircle(sketch, "E2.26.44.0", {"center": v(-35.5, -155) * mm, "radius": 2.5 * mm});
            skCircle(sketch, "E2.26.45.0", {"center": v(-35.5, -163) * mm, "radius": 2.5 * mm});
            skCircle(sketch, "E2.26.46.0", {"center": v(-35.5, -171) * mm, "radius": 2.5 * mm});
            skCircle(sketch, "E2.26.47.0", {"center": v(-35.5, -179) * mm, "radius": 2.5 * mm});
            skCircle(sketch, "E2.26.48.0", {"center": v(-35.5, -187) * mm, "radius": 2.5 * mm});
            skCircle(sketch, "E2.26.49.0", {"center": v(-35.5, -195) * mm, "radius": 2.5 * mm});
            skCircle(sketch, "E2.27.0.0", {"center": v(-27.5, 197) * mm, "radius": 2.5 * mm});
            skCircle(sketch, "E2.27.1.0", {"center": v(-27.5, 189) * mm, "radius": 2.5 * mm});
            skCircle(sketch, "E2.27.2.0", {"center": v(-27.5, 181) * mm, "radius": 2.5 * mm});
            skCircle(sketch, "E2.27.3.0", {"center": v(-27.5, 173) * mm, "radius": 2.5 * mm});
            skCircle(sketch, "E2.27.4.0", {"center": v(-27.5, 165) * mm, "radius": 2.5 * mm});
            skCircle(sketch, "E2.27.5.0", {"center": v(-27.5, 157) * mm, "radius": 2.5 * mm});
            skCircle(sketch, "E2.27.6.0", {"center": v(-27.5, 149) * mm, "radius": 2.5 * mm});
            skCircle(sketch, "E2.27.7.0", {"center": v(-27.5, 141) * mm, "radius": 2.5 * mm});
            skCircle(sketch, "E2.27.8.0", {"center": v(-27.5, 133) * mm, "radius": 2.5 * mm});
            skCircle(sketch, "E2.27.9.0", {"center": v(-27.5, 125) * mm, "radius": 2.5 * mm});
            skCircle(sketch, "E2.27.10.0", {"center": v(-27.5, 117) * mm, "radius": 2.5 * mm});
            skCircle(sketch, "E2.27.11.0", {"center": v(-27.5, 109) * mm, "radius": 2.5 * mm});
            skCircle(sketch, "E2.27.12.0", {"center": v(-27.5, 101) * mm, "radius": 2.5 * mm});
            skCircle(sketch, "E2.27.13.0", {"center": v(-27.5, 93) * mm, "radius": 2.5 * mm});
            skCircle(sketch, "E2.27.14.0", {"center": v(-27.5, 85) * mm, "radius": 2.5 * mm});
            skCircle(sketch, "E2.27.15.0", {"center": v(-27.5, 77) * mm, "radius": 2.5 * mm});
            skCircle(sketch, "E2.27.16.0", {"center": v(-27.5, 69) * mm, "radius": 2.5 * mm});
            skCircle(sketch, "E2.27.17.0", {"center": v(-27.5, 61) * mm, "radius": 2.5 * mm});
            skCircle(sketch, "E2.27.18.0", {"center": v(-27.5, 53) * mm, "radius": 2.5 * mm});
            skCircle(sketch, "E2.27.19.0", {"center": v(-27.5, 45) * mm, "radius": 2.5 * mm});
            skCircle(sketch, "E2.27.20.0", {"center": v(-27.5, 37) * mm, "radius": 2.5 * mm});
            skCircle(sketch, "E2.27.21.0", {"center": v(-27.5, 29) * mm, "radius": 2.5 * mm});
            skCircle(sketch, "E2.27.22.0", {"center": v(-27.5, 21) * mm, "radius": 2.5 * mm});
            skCircle(sketch, "E2.27.23.0", {"center": v(-27.5, 13) * mm, "radius": 2.5 * mm});
            skCircle(sketch, "E2.27.24.0", {"center": v(-27.5, 5) * mm, "radius": 2.5 * mm});
            skCircle(sketch, "E2.27.25.0", {"center": v(-27.5, -3) * mm, "radius": 2.5 * mm});
            skCircle(sketch, "E2.27.26.0", {"center": v(-27.5, -11) * mm, "radius": 2.5 * mm});
            skCircle(sketch, "E2.27.27.0", {"center": v(-27.5, -19) * mm, "radius": 2.5 * mm});
            skCircle(sketch, "E2.27.28.0", {"center": v(-27.5, -27) * mm, "radius": 2.5 * mm});
            skCircle(sketch, "E2.27.29.0", {"center": v(-27.5, -35) * mm, "radius": 2.5 * mm});
            skCircle(sketch, "E2.27.30.0", {"center": v(-27.5, -43) * mm, "radius": 2.5 * mm});
            skCircle(sketch, "E2.27.31.0", {"center": v(-27.5, -51) * mm, "radius": 2.5 * mm});
            skCircle(sketch, "E2.27.32.0", {"center": v(-27.5, -59) * mm, "radius": 2.5 * mm});
            skCircle(sketch, "E2.27.33.0", {"center": v(-27.5, -67) * mm, "radius": 2.5 * mm});
            skCircle(sketch, "E2.27.34.0", {"center": v(-27.5, -75) * mm, "radius": 2.5 * mm});
            skCircle(sketch, "E2.27.35.0", {"center": v(-27.5, -83) * mm, "radius": 2.5 * mm});
            skCircle(sketch, "E2.27.36.0", {"center": v(-27.5, -91) * mm, "radius": 2.5 * mm});
            skCircle(sketch, "E2.27.37.0", {"center": v(-27.5, -99) * mm, "radius": 2.5 * mm});
            skCircle(sketch, "E2.27.38.0", {"center": v(-27.5, -107) * mm, "radius": 2.5 * mm});
            skCircle(sketch, "E2.27.39.0", {"center": v(-27.5, -115) * mm, "radius": 2.5 * mm});
            skCircle(sketch, "E2.27.40.0", {"center": v(-27.5, -123) * mm, "radius": 2.5 * mm});
            skCircle(sketch, "E2.27.41.0", {"center": v(-27.5, -131) * mm, "radius": 2.5 * mm});
            skCircle(sketch, "E2.27.42.0", {"center": v(-27.5, -139) * mm, "radius": 2.5 * mm});
            skCircle(sketch, "E2.27.43.0", {"center": v(-27.5, -147) * mm, "radius": 2.5 * mm});
            skCircle(sketch, "E2.27.44.0", {"center": v(-27.5, -155) * mm, "radius": 2.5 * mm});
            skCircle(sketch, "E2.27.45.0", {"center": v(-27.5, -163) * mm, "radius": 2.5 * mm});
            skCircle(sketch, "E2.27.46.0", {"center": v(-27.5, -171) * mm, "radius": 2.5 * mm});
            skCircle(sketch, "E2.27.47.0", {"center": v(-27.5, -179) * mm, "radius": 2.5 * mm});
            skCircle(sketch, "E2.27.48.0", {"center": v(-27.5, -187) * mm, "radius": 2.5 * mm});
            skCircle(sketch, "E2.27.49.0", {"center": v(-27.5, -195) * mm, "radius": 2.5 * mm});
            skCircle(sketch, "E2.28.0.0", {"center": v(-19.5, 197) * mm, "radius": 2.5 * mm});
            skCircle(sketch, "E2.28.1.0", {"center": v(-19.5, 189) * mm, "radius": 2.5 * mm});
            skCircle(sketch, "E2.28.2.0", {"center": v(-19.5, 181) * mm, "radius": 2.5 * mm});
            skCircle(sketch, "E2.28.3.0", {"center": v(-19.5, 173) * mm, "radius": 2.5 * mm});
            skCircle(sketch, "E2.28.4.0", {"center": v(-19.5, 165) * mm, "radius": 2.5 * mm});
            skCircle(sketch, "E2.28.5.0", {"center": v(-19.5, 157) * mm, "radius": 2.5 * mm});
            skCircle(sketch, "E2.28.6.0", {"center": v(-19.5, 149) * mm, "radius": 2.5 * mm});
            skCircle(sketch, "E2.28.7.0", {"center": v(-19.5, 141) * mm, "radius": 2.5 * mm});
            skCircle(sketch, "E2.28.8.0", {"center": v(-19.5, 133) * mm, "radius": 2.5 * mm});
            skCircle(sketch, "E2.28.9.0", {"center": v(-19.5, 125) * mm, "radius": 2.5 * mm});
            skCircle(sketch, "E2.28.10.0", {"center": v(-19.5, 117) * mm, "radius": 2.5 * mm});
            skCircle(sketch, "E2.28.11.0", {"center": v(-19.5, 109) * mm, "radius": 2.5 * mm});
            skCircle(sketch, "E2.28.12.0", {"center": v(-19.5, 101) * mm, "radius": 2.5 * mm});
            skCircle(sketch, "E2.28.13.0", {"center": v(-19.5, 93) * mm, "radius": 2.5 * mm});
            skCircle(sketch, "E2.28.14.0", {"center": v(-19.5, 85) * mm, "radius": 2.5 * mm});
            skCircle(sketch, "E2.28.15.0", {"center": v(-19.5, 77) * mm, "radius": 2.5 * mm});
            skCircle(sketch, "E2.28.16.0", {"center": v(-19.5, 69) * mm, "radius": 2.5 * mm});
            skCircle(sketch, "E2.28.17.0", {"center": v(-19.5, 61) * mm, "radius": 2.5 * mm});
            skCircle(sketch, "E2.28.18.0", {"center": v(-19.5, 53) * mm, "radius": 2.5 * mm});
            skCircle(sketch, "E2.28.19.0", {"center": v(-19.5, 45) * mm, "radius": 2.5 * mm});
            skCircle(sketch, "E2.28.20.0", {"center": v(-19.5, 37) * mm, "radius": 2.5 * mm});
            skCircle(sketch, "E2.28.21.0", {"center": v(-19.5, 29) * mm, "radius": 2.5 * mm});
            skCircle(sketch, "E2.28.22.0", {"center": v(-19.5, 21) * mm, "radius": 2.5 * mm});
            skCircle(sketch, "E2.28.23.0", {"center": v(-19.5, 13) * mm, "radius": 2.5 * mm});
            skCircle(sketch, "E2.28.24.0", {"center": v(-19.5, 5) * mm, "radius": 2.5 * mm});
            skCircle(sketch, "E2.28.25.0", {"center": v(-19.5, -3) * mm, "radius": 2.5 * mm});
            skCircle(sketch, "E2.28.26.0", {"center": v(-19.5, -11) * mm, "radius": 2.5 * mm});
            skCircle(sketch, "E2.28.27.0", {"center": v(-19.5, -19) * mm, "radius": 2.5 * mm});
            skCircle(sketch, "E2.28.28.0", {"center": v(-19.5, -27) * mm, "radius": 2.5 * mm});
            skCircle(sketch, "E2.28.29.0", {"center": v(-19.5, -35) * mm, "radius": 2.5 * mm});
            skCircle(sketch, "E2.28.30.0", {"center": v(-19.5, -43) * mm, "radius": 2.5 * mm});
            skCircle(sketch, "E2.28.31.0", {"center": v(-19.5, -51) * mm, "radius": 2.5 * mm});
            skCircle(sketch, "E2.28.32.0", {"center": v(-19.5, -59) * mm, "radius": 2.5 * mm});
            skCircle(sketch, "E2.28.33.0", {"center": v(-19.5, -67) * mm, "radius": 2.5 * mm});
            skCircle(sketch, "E2.28.34.0", {"center": v(-19.5, -75) * mm, "radius": 2.5 * mm});
            skCircle(sketch, "E2.28.35.0", {"center": v(-19.5, -83) * mm, "radius": 2.5 * mm});
            skCircle(sketch, "E2.28.36.0", {"center": v(-19.5, -91) * mm, "radius": 2.5 * mm});
            skCircle(sketch, "E2.28.37.0", {"center": v(-19.5, -99) * mm, "radius": 2.5 * mm});
            skCircle(sketch, "E2.28.38.0", {"center": v(-19.5, -107) * mm, "radius": 2.5 * mm});
            skCircle(sketch, "E2.28.39.0", {"center": v(-19.5, -115) * mm, "radius": 2.5 * mm});
            skCircle(sketch, "E2.28.40.0", {"center": v(-19.5, -123) * mm, "radius": 2.5 * mm});
            skCircle(sketch, "E2.28.41.0", {"center": v(-19.5, -131) * mm, "radius": 2.5 * mm});
            skCircle(sketch, "E2.28.42.0", {"center": v(-19.5, -139) * mm, "radius": 2.5 * mm});
            skCircle(sketch, "E2.28.43.0", {"center": v(-19.5, -147) * mm, "radius": 2.5 * mm});
            skCircle(sketch, "E2.28.44.0", {"center": v(-19.5, -155) * mm, "radius": 2.5 * mm});
            skCircle(sketch, "E2.28.45.0", {"center": v(-19.5, -163) * mm, "radius": 2.5 * mm});
            skCircle(sketch, "E2.28.46.0", {"center": v(-19.5, -171) * mm, "radius": 2.5 * mm});
            skCircle(sketch, "E2.28.47.0", {"center": v(-19.5, -179) * mm, "radius": 2.5 * mm});
            skCircle(sketch, "E2.28.48.0", {"center": v(-19.5, -187) * mm, "radius": 2.5 * mm});
            skCircle(sketch, "E2.28.49.0", {"center": v(-19.5, -195) * mm, "radius": 2.5 * mm});
            skCircle(sketch, "E2.29.0.0", {"center": v(-11.5, 197) * mm, "radius": 2.5 * mm});
            skCircle(sketch, "E2.29.1.0", {"center": v(-11.5, 189) * mm, "radius": 2.5 * mm});
            skCircle(sketch, "E2.29.2.0", {"center": v(-11.5, 181) * mm, "radius": 2.5 * mm});
            skCircle(sketch, "E2.29.3.0", {"center": v(-11.5, 173) * mm, "radius": 2.5 * mm});
            skCircle(sketch, "E2.29.4.0", {"center": v(-11.5, 165) * mm, "radius": 2.5 * mm});
            skCircle(sketch, "E2.29.5.0", {"center": v(-11.5, 157) * mm, "radius": 2.5 * mm});
            skCircle(sketch, "E2.29.6.0", {"center": v(-11.5, 149) * mm, "radius": 2.5 * mm});
            skCircle(sketch, "E2.29.7.0", {"center": v(-11.5, 141) * mm, "radius": 2.5 * mm});
            skCircle(sketch, "E2.29.8.0", {"center": v(-11.5, 133) * mm, "radius": 2.5 * mm});
            skCircle(sketch, "E2.29.9.0", {"center": v(-11.5, 125) * mm, "radius": 2.5 * mm});
            skCircle(sketch, "E2.29.10.0", {"center": v(-11.5, 117) * mm, "radius": 2.5 * mm});
            skCircle(sketch, "E2.29.11.0", {"center": v(-11.5, 109) * mm, "radius": 2.5 * mm});
            skCircle(sketch, "E2.29.12.0", {"center": v(-11.5, 101) * mm, "radius": 2.5 * mm});
            skCircle(sketch, "E2.29.13.0", {"center": v(-11.5, 93) * mm, "radius": 2.5 * mm});
            skCircle(sketch, "E2.29.14.0", {"center": v(-11.5, 85) * mm, "radius": 2.5 * mm});
            skCircle(sketch, "E2.29.15.0", {"center": v(-11.5, 77) * mm, "radius": 2.5 * mm});
            skCircle(sketch, "E2.29.16.0", {"center": v(-11.5, 69) * mm, "radius": 2.5 * mm});
            skCircle(sketch, "E2.29.17.0", {"center": v(-11.5, 61) * mm, "radius": 2.5 * mm});
            skCircle(sketch, "E2.29.18.0", {"center": v(-11.5, 53) * mm, "radius": 2.5 * mm});
            skCircle(sketch, "E2.29.19.0", {"center": v(-11.5, 45) * mm, "radius": 2.5 * mm});
            skCircle(sketch, "E2.29.20.0", {"center": v(-11.5, 37) * mm, "radius": 2.5 * mm});
            skCircle(sketch, "E2.29.21.0", {"center": v(-11.5, 29) * mm, "radius": 2.5 * mm});
            skCircle(sketch, "E2.29.22.0", {"center": v(-11.5, 21) * mm, "radius": 2.5 * mm});
            skCircle(sketch, "E2.29.23.0", {"center": v(-11.5, 13) * mm, "radius": 2.5 * mm});
            skCircle(sketch, "E2.29.24.0", {"center": v(-11.5, 5) * mm, "radius": 2.5 * mm});
            skCircle(sketch, "E2.29.25.0", {"center": v(-11.5, -3) * mm, "radius": 2.5 * mm});
            skCircle(sketch, "E2.29.26.0", {"center": v(-11.5, -11) * mm, "radius": 2.5 * mm});
            skCircle(sketch, "E2.29.27.0", {"center": v(-11.5, -19) * mm, "radius": 2.5 * mm});
            skCircle(sketch, "E2.29.28.0", {"center": v(-11.5, -27) * mm, "radius": 2.5 * mm});
            skCircle(sketch, "E2.29.29.0", {"center": v(-11.5, -35) * mm, "radius": 2.5 * mm});
            skCircle(sketch, "E2.29.30.0", {"center": v(-11.5, -43) * mm, "radius": 2.5 * mm});
            skCircle(sketch, "E2.29.31.0", {"center": v(-11.5, -51) * mm, "radius": 2.5 * mm});
            skCircle(sketch, "E2.29.32.0", {"center": v(-11.5, -59) * mm, "radius": 2.5 * mm});
            skCircle(sketch, "E2.29.33.0", {"center": v(-11.5, -67) * mm, "radius": 2.5 * mm});
            skCircle(sketch, "E2.29.34.0", {"center": v(-11.5, -75) * mm, "radius": 2.5 * mm});
            skCircle(sketch, "E2.29.35.0", {"center": v(-11.5, -83) * mm, "radius": 2.5 * mm});
            skCircle(sketch, "E2.29.36.0", {"center": v(-11.5, -91) * mm, "radius": 2.5 * mm});
            skCircle(sketch, "E2.29.37.0", {"center": v(-11.5, -99) * mm, "radius": 2.5 * mm});
            skCircle(sketch, "E2.29.38.0", {"center": v(-11.5, -107) * mm, "radius": 2.5 * mm});
            skCircle(sketch, "E2.29.39.0", {"center": v(-11.5, -115) * mm, "radius": 2.5 * mm});
            skCircle(sketch, "E2.29.40.0", {"center": v(-11.5, -123) * mm, "radius": 2.5 * mm});
            skCircle(sketch, "E2.29.41.0", {"center": v(-11.5, -131) * mm, "radius": 2.5 * mm});
            skCircle(sketch, "E2.29.42.0", {"center": v(-11.5, -139) * mm, "radius": 2.5 * mm});
            skCircle(sketch, "E2.29.43.0", {"center": v(-11.5, -147) * mm, "radius": 2.5 * mm});
            skCircle(sketch, "E2.29.44.0", {"center": v(-11.5, -155) * mm, "radius": 2.5 * mm});
            skCircle(sketch, "E2.29.45.0", {"center": v(-11.5, -163) * mm, "radius": 2.5 * mm});
            skCircle(sketch, "E2.29.46.0", {"center": v(-11.5, -171) * mm, "radius": 2.5 * mm});
            skCircle(sketch, "E2.29.47.0", {"center": v(-11.5, -179) * mm, "radius": 2.5 * mm});
            skCircle(sketch, "E2.29.48.0", {"center": v(-11.5, -187) * mm, "radius": 2.5 * mm});
            skCircle(sketch, "E2.29.49.0", {"center": v(-11.5, -195) * mm, "radius": 2.5 * mm});
            skCircle(sketch, "E2.30.0.0", {"center": v(-3.5, 197) * mm, "radius": 2.5 * mm});
            skCircle(sketch, "E2.30.1.0", {"center": v(-3.5, 189) * mm, "radius": 2.5 * mm});
            skCircle(sketch, "E2.30.2.0", {"center": v(-3.5, 181) * mm, "radius": 2.5 * mm});
            skCircle(sketch, "E2.30.3.0", {"center": v(-3.5, 173) * mm, "radius": 2.5 * mm});
            skCircle(sketch, "E2.30.4.0", {"center": v(-3.5, 165) * mm, "radius": 2.5 * mm});
            skCircle(sketch, "E2.30.5.0", {"center": v(-3.5, 157) * mm, "radius": 2.5 * mm});
            skCircle(sketch, "E2.30.6.0", {"center": v(-3.5, 149) * mm, "radius": 2.5 * mm});
            skCircle(sketch, "E2.30.7.0", {"center": v(-3.5, 141) * mm, "radius": 2.5 * mm});
            skCircle(sketch, "E2.30.8.0", {"center": v(-3.5, 133) * mm, "radius": 2.5 * mm});
            skCircle(sketch, "E2.30.9.0", {"center": v(-3.5, 125) * mm, "radius": 2.5 * mm});
            skCircle(sketch, "E2.30.10.0", {"center": v(-3.5, 117) * mm, "radius": 2.5 * mm});
            skCircle(sketch, "E2.30.11.0", {"center": v(-3.5, 109) * mm, "radius": 2.5 * mm});
            skCircle(sketch, "E2.30.12.0", {"center": v(-3.5, 101) * mm, "radius": 2.5 * mm});
            skCircle(sketch, "E2.30.13.0", {"center": v(-3.5, 93) * mm, "radius": 2.5 * mm});
            skCircle(sketch, "E2.30.14.0", {"center": v(-3.5, 85) * mm, "radius": 2.5 * mm});
            skCircle(sketch, "E2.30.15.0", {"center": v(-3.5, 77) * mm, "radius": 2.5 * mm});
            skCircle(sketch, "E2.30.16.0", {"center": v(-3.5, 69) * mm, "radius": 2.5 * mm});
            skCircle(sketch, "E2.30.17.0", {"center": v(-3.5, 61) * mm, "radius": 2.5 * mm});
            skCircle(sketch, "E2.30.18.0", {"center": v(-3.5, 53) * mm, "radius": 2.5 * mm});
            skCircle(sketch, "E2.30.19.0", {"center": v(-3.5, 45) * mm, "radius": 2.5 * mm});
            skCircle(sketch, "E2.30.20.0", {"center": v(-3.5, 37) * mm, "radius": 2.5 * mm});
            skCircle(sketch, "E2.30.21.0", {"center": v(-3.5, 29) * mm, "radius": 2.5 * mm});
            skCircle(sketch, "E2.30.22.0", {"center": v(-3.5, 21) * mm, "radius": 2.5 * mm});
            skCircle(sketch, "E2.30.23.0", {"center": v(-3.5, 13) * mm, "radius": 2.5 * mm});
            skCircle(sketch, "E2.30.24.0", {"center": v(-3.5, 5) * mm, "radius": 2.5 * mm});
            skCircle(sketch, "E2.30.25.0", {"center": v(-3.5, -3) * mm, "radius": 2.5 * mm});
            skCircle(sketch, "E2.30.26.0", {"center": v(-3.5, -11) * mm, "radius": 2.5 * mm});
            skCircle(sketch, "E2.30.27.0", {"center": v(-3.5, -19) * mm, "radius": 2.5 * mm});
            skCircle(sketch, "E2.30.28.0", {"center": v(-3.5, -27) * mm, "radius": 2.5 * mm});
            skCircle(sketch, "E2.30.29.0", {"center": v(-3.5, -35) * mm, "radius": 2.5 * mm});
            skCircle(sketch, "E2.30.30.0", {"center": v(-3.5, -43) * mm, "radius": 2.5 * mm});
            skCircle(sketch, "E2.30.31.0", {"center": v(-3.5, -51) * mm, "radius": 2.5 * mm});
            skCircle(sketch, "E2.30.32.0", {"center": v(-3.5, -59) * mm, "radius": 2.5 * mm});
            skCircle(sketch, "E2.30.33.0", {"center": v(-3.5, -67) * mm, "radius": 2.5 * mm});
            skCircle(sketch, "E2.30.34.0", {"center": v(-3.5, -75) * mm, "radius": 2.5 * mm});
            skCircle(sketch, "E2.30.35.0", {"center": v(-3.5, -83) * mm, "radius": 2.5 * mm});
            skCircle(sketch, "E2.30.36.0", {"center": v(-3.5, -91) * mm, "radius": 2.5 * mm});
            skCircle(sketch, "E2.30.37.0", {"center": v(-3.5, -99) * mm, "radius": 2.5 * mm});
            skCircle(sketch, "E2.30.38.0", {"center": v(-3.5, -107) * mm, "radius": 2.5 * mm});
            skCircle(sketch, "E2.30.39.0", {"center": v(-3.5, -115) * mm, "radius": 2.5 * mm});
            skCircle(sketch, "E2.30.40.0", {"center": v(-3.5, -123) * mm, "radius": 2.5 * mm});
            skCircle(sketch, "E2.30.41.0", {"center": v(-3.5, -131) * mm, "radius": 2.5 * mm});
            skCircle(sketch, "E2.30.42.0", {"center": v(-3.5, -139) * mm, "radius": 2.5 * mm});
            skCircle(sketch, "E2.30.43.0", {"center": v(-3.5, -147) * mm, "radius": 2.5 * mm});
            skCircle(sketch, "E2.30.44.0", {"center": v(-3.5, -155) * mm, "radius": 2.5 * mm});
            skCircle(sketch, "E2.30.45.0", {"center": v(-3.5, -163) * mm, "radius": 2.5 * mm});
            skCircle(sketch, "E2.30.46.0", {"center": v(-3.5, -171) * mm, "radius": 2.5 * mm});
            skCircle(sketch, "E2.30.47.0", {"center": v(-3.5, -179) * mm, "radius": 2.5 * mm});
            skCircle(sketch, "E2.30.48.0", {"center": v(-3.5, -187) * mm, "radius": 2.5 * mm});
            skCircle(sketch, "E2.30.49.0", {"center": v(-3.5, -195) * mm, "radius": 2.5 * mm});
            skCircle(sketch, "E2.31.0.0", {"center": v(4.5, 197) * mm, "radius": 2.5 * mm});
            skCircle(sketch, "E2.31.1.0", {"center": v(4.5, 189) * mm, "radius": 2.5 * mm});
            skCircle(sketch, "E2.31.2.0", {"center": v(4.5, 181) * mm, "radius": 2.5 * mm});
            skCircle(sketch, "E2.31.3.0", {"center": v(4.5, 173) * mm, "radius": 2.5 * mm});
            skCircle(sketch, "E2.31.4.0", {"center": v(4.5, 165) * mm, "radius": 2.5 * mm});
            skCircle(sketch, "E2.31.5.0", {"center": v(4.5, 157) * mm, "radius": 2.5 * mm});
            skCircle(sketch, "E2.31.6.0", {"center": v(4.5, 149) * mm, "radius": 2.5 * mm});
            skCircle(sketch, "E2.31.7.0", {"center": v(4.5, 141) * mm, "radius": 2.5 * mm});
            skCircle(sketch, "E2.31.8.0", {"center": v(4.5, 133) * mm, "radius": 2.5 * mm});
            skCircle(sketch, "E2.31.9.0", {"center": v(4.5, 125) * mm, "radius": 2.5 * mm});
            skCircle(sketch, "E2.31.10.0", {"center": v(4.5, 117) * mm, "radius": 2.5 * mm});
            skCircle(sketch, "E2.31.11.0", {"center": v(4.5, 109) * mm, "radius": 2.5 * mm});
            skCircle(sketch, "E2.31.12.0", {"center": v(4.5, 101) * mm, "radius": 2.5 * mm});
            skCircle(sketch, "E2.31.13.0", {"center": v(4.5, 93) * mm, "radius": 2.5 * mm});
            skCircle(sketch, "E2.31.14.0", {"center": v(4.5, 85) * mm, "radius": 2.5 * mm});
            skCircle(sketch, "E2.31.15.0", {"center": v(4.5, 77) * mm, "radius": 2.5 * mm});
            skCircle(sketch, "E2.31.16.0", {"center": v(4.5, 69) * mm, "radius": 2.5 * mm});
            skCircle(sketch, "E2.31.17.0", {"center": v(4.5, 61) * mm, "radius": 2.5 * mm});
            skCircle(sketch, "E2.31.18.0", {"center": v(4.5, 53) * mm, "radius": 2.5 * mm});
            skCircle(sketch, "E2.31.19.0", {"center": v(4.5, 45) * mm, "radius": 2.5 * mm});
            skCircle(sketch, "E2.31.20.0", {"center": v(4.5, 37) * mm, "radius": 2.5 * mm});
            skCircle(sketch, "E2.31.21.0", {"center": v(4.5, 29) * mm, "radius": 2.5 * mm});
            skCircle(sketch, "E2.31.22.0", {"center": v(4.5, 21) * mm, "radius": 2.5 * mm});
            skCircle(sketch, "E2.31.23.0", {"center": v(4.5, 13) * mm, "radius": 2.5 * mm});
            skCircle(sketch, "E2.31.24.0", {"center": v(4.5, 5) * mm, "radius": 2.5 * mm});
            skCircle(sketch, "E2.31.25.0", {"center": v(4.5, -3) * mm, "radius": 2.5 * mm});
            skCircle(sketch, "E2.31.26.0", {"center": v(4.5, -11) * mm, "radius": 2.5 * mm});
            skCircle(sketch, "E2.31.27.0", {"center": v(4.5, -19) * mm, "radius": 2.5 * mm});
            skCircle(sketch, "E2.31.28.0", {"center": v(4.5, -27) * mm, "radius": 2.5 * mm});
            skCircle(sketch, "E2.31.29.0", {"center": v(4.5, -35) * mm, "radius": 2.5 * mm});
            skCircle(sketch, "E2.31.30.0", {"center": v(4.5, -43) * mm, "radius": 2.5 * mm});
            skCircle(sketch, "E2.31.31.0", {"center": v(4.5, -51) * mm, "radius": 2.5 * mm});
            skCircle(sketch, "E2.31.32.0", {"center": v(4.5, -59) * mm, "radius": 2.5 * mm});
            skCircle(sketch, "E2.31.33.0", {"center": v(4.5, -67) * mm, "radius": 2.5 * mm});
            skCircle(sketch, "E2.31.34.0", {"center": v(4.5, -75) * mm, "radius": 2.5 * mm});
            skCircle(sketch, "E2.31.35.0", {"center": v(4.5, -83) * mm, "radius": 2.5 * mm});
            skCircle(sketch, "E2.31.36.0", {"center": v(4.5, -91) * mm, "radius": 2.5 * mm});
            skCircle(sketch, "E2.31.37.0", {"center": v(4.5, -99) * mm, "radius": 2.5 * mm});
            skCircle(sketch, "E2.31.38.0", {"center": v(4.5, -107) * mm, "radius": 2.5 * mm});
            skCircle(sketch, "E2.31.39.0", {"center": v(4.5, -115) * mm, "radius": 2.5 * mm});
            skCircle(sketch, "E2.31.40.0", {"center": v(4.5, -123) * mm, "radius": 2.5 * mm});
            skCircle(sketch, "E2.31.41.0", {"center": v(4.5, -131) * mm, "radius": 2.5 * mm});
            skCircle(sketch, "E2.31.42.0", {"center": v(4.5, -139) * mm, "radius": 2.5 * mm});
            skCircle(sketch, "E2.31.43.0", {"center": v(4.5, -147) * mm, "radius": 2.5 * mm});
            skCircle(sketch, "E2.31.44.0", {"center": v(4.5, -155) * mm, "radius": 2.5 * mm});
            skCircle(sketch, "E2.31.45.0", {"center": v(4.5, -163) * mm, "radius": 2.5 * mm});
            skCircle(sketch, "E2.31.46.0", {"center": v(4.5, -171) * mm, "radius": 2.5 * mm});
            skCircle(sketch, "E2.31.47.0", {"center": v(4.5, -179) * mm, "radius": 2.5 * mm});
            skCircle(sketch, "E2.31.48.0", {"center": v(4.5, -187) * mm, "radius": 2.5 * mm});
            skCircle(sketch, "E2.31.49.0", {"center": v(4.5, -195) * mm, "radius": 2.5 * mm});
            skCircle(sketch, "E2.32.0.0", {"center": v(12.5, 197) * mm, "radius": 2.5 * mm});
            skCircle(sketch, "E2.32.1.0", {"center": v(12.5, 189) * mm, "radius": 2.5 * mm});
            skCircle(sketch, "E2.32.2.0", {"center": v(12.5, 181) * mm, "radius": 2.5 * mm});
            skCircle(sketch, "E2.32.3.0", {"center": v(12.5, 173) * mm, "radius": 2.5 * mm});
            skCircle(sketch, "E2.32.4.0", {"center": v(12.5, 165) * mm, "radius": 2.5 * mm});
            skCircle(sketch, "E2.32.5.0", {"center": v(12.5, 157) * mm, "radius": 2.5 * mm});
            skCircle(sketch, "E2.32.6.0", {"center": v(12.5, 149) * mm, "radius": 2.5 * mm});
            skCircle(sketch, "E2.32.7.0", {"center": v(12.5, 141) * mm, "radius": 2.5 * mm});
            skCircle(sketch, "E2.32.8.0", {"center": v(12.5, 133) * mm, "radius": 2.5 * mm});
            skCircle(sketch, "E2.32.9.0", {"center": v(12.5, 125) * mm, "radius": 2.5 * mm});
            skCircle(sketch, "E2.32.10.0", {"center": v(12.5, 117) * mm, "radius": 2.5 * mm});
            skCircle(sketch, "E2.32.11.0", {"center": v(12.5, 109) * mm, "radius": 2.5 * mm});
            skCircle(sketch, "E2.32.12.0", {"center": v(12.5, 101) * mm, "radius": 2.5 * mm});
            skCircle(sketch, "E2.32.13.0", {"center": v(12.5, 93) * mm, "radius": 2.5 * mm});
            skCircle(sketch, "E2.32.14.0", {"center": v(12.5, 85) * mm, "radius": 2.5 * mm});
            skCircle(sketch, "E2.32.15.0", {"center": v(12.5, 77) * mm, "radius": 2.5 * mm});
            skCircle(sketch, "E2.32.16.0", {"center": v(12.5, 69) * mm, "radius": 2.5 * mm});
            skCircle(sketch, "E2.32.17.0", {"center": v(12.5, 61) * mm, "radius": 2.5 * mm});
            skCircle(sketch, "E2.32.18.0", {"center": v(12.5, 53) * mm, "radius": 2.5 * mm});
            skCircle(sketch, "E2.32.19.0", {"center": v(12.5, 45) * mm, "radius": 2.5 * mm});
            skCircle(sketch, "E2.32.20.0", {"center": v(12.5, 37) * mm, "radius": 2.5 * mm});
            skCircle(sketch, "E2.32.21.0", {"center": v(12.5, 29) * mm, "radius": 2.5 * mm});
            skCircle(sketch, "E2.32.22.0", {"center": v(12.5, 21) * mm, "radius": 2.5 * mm});
            skCircle(sketch, "E2.32.23.0", {"center": v(12.5, 13) * mm, "radius": 2.5 * mm});
            skCircle(sketch, "E2.32.24.0", {"center": v(12.5, 5) * mm, "radius": 2.5 * mm});
            skCircle(sketch, "E2.32.25.0", {"center": v(12.5, -3) * mm, "radius": 2.5 * mm});
            skCircle(sketch, "E2.32.26.0", {"center": v(12.5, -11) * mm, "radius": 2.5 * mm});
            skCircle(sketch, "E2.32.27.0", {"center": v(12.5, -19) * mm, "radius": 2.5 * mm});
            skCircle(sketch, "E2.32.28.0", {"center": v(12.5, -27) * mm, "radius": 2.5 * mm});
            skCircle(sketch, "E2.32.29.0", {"center": v(12.5, -35) * mm, "radius": 2.5 * mm});
            skCircle(sketch, "E2.32.30.0", {"center": v(12.5, -43) * mm, "radius": 2.5 * mm});
            skCircle(sketch, "E2.32.31.0", {"center": v(12.5, -51) * mm, "radius": 2.5 * mm});
            skCircle(sketch, "E2.32.32.0", {"center": v(12.5, -59) * mm, "radius": 2.5 * mm});
            skCircle(sketch, "E2.32.33.0", {"center": v(12.5, -67) * mm, "radius": 2.5 * mm});
            skCircle(sketch, "E2.32.34.0", {"center": v(12.5, -75) * mm, "radius": 2.5 * mm});
            skCircle(sketch, "E2.32.35.0", {"center": v(12.5, -83) * mm, "radius": 2.5 * mm});
            skCircle(sketch, "E2.32.36.0", {"center": v(12.5, -91) * mm, "radius": 2.5 * mm});
            skCircle(sketch, "E2.32.37.0", {"center": v(12.5, -99) * mm, "radius": 2.5 * mm});
            skCircle(sketch, "E2.32.38.0", {"center": v(12.5, -107) * mm, "radius": 2.5 * mm});
            skCircle(sketch, "E2.32.39.0", {"center": v(12.5, -115) * mm, "radius": 2.5 * mm});
            skCircle(sketch, "E2.32.40.0", {"center": v(12.5, -123) * mm, "radius": 2.5 * mm});
            skCircle(sketch, "E2.32.41.0", {"center": v(12.5, -131) * mm, "radius": 2.5 * mm});
            skCircle(sketch, "E2.32.42.0", {"center": v(12.5, -139) * mm, "radius": 2.5 * mm});
            skCircle(sketch, "E2.32.43.0", {"center": v(12.5, -147) * mm, "radius": 2.5 * mm});
            skCircle(sketch, "E2.32.44.0", {"center": v(12.5, -155) * mm, "radius": 2.5 * mm});
            skCircle(sketch, "E2.32.45.0", {"center": v(12.5, -163) * mm, "radius": 2.5 * mm});
            skCircle(sketch, "E2.32.46.0", {"center": v(12.5, -171) * mm, "radius": 2.5 * mm});
            skCircle(sketch, "E2.32.47.0", {"center": v(12.5, -179) * mm, "radius": 2.5 * mm});
            skCircle(sketch, "E2.32.48.0", {"center": v(12.5, -187) * mm, "radius": 2.5 * mm});
            skCircle(sketch, "E2.32.49.0", {"center": v(12.5, -195) * mm, "radius": 2.5 * mm});
            skCircle(sketch, "E2.33.0.0", {"center": v(20.5, 197) * mm, "radius": 2.5 * mm});
            skCircle(sketch, "E2.33.1.0", {"center": v(20.5, 189) * mm, "radius": 2.5 * mm});
            skCircle(sketch, "E2.33.2.0", {"center": v(20.5, 181) * mm, "radius": 2.5 * mm});
            skCircle(sketch, "E2.33.3.0", {"center": v(20.5, 173) * mm, "radius": 2.5 * mm});
            skCircle(sketch, "E2.33.4.0", {"center": v(20.5, 165) * mm, "radius": 2.5 * mm});
            skCircle(sketch, "E2.33.5.0", {"center": v(20.5, 157) * mm, "radius": 2.5 * mm});
            skCircle(sketch, "E2.33.6.0", {"center": v(20.5, 149) * mm, "radius": 2.5 * mm});
            skCircle(sketch, "E2.33.7.0", {"center": v(20.5, 141) * mm, "radius": 2.5 * mm});
            skCircle(sketch, "E2.33.8.0", {"center": v(20.5, 133) * mm, "radius": 2.5 * mm});
            skCircle(sketch, "E2.33.9.0", {"center": v(20.5, 125) * mm, "radius": 2.5 * mm});
            skCircle(sketch, "E2.33.10.0", {"center": v(20.5, 117) * mm, "radius": 2.5 * mm});
            skCircle(sketch, "E2.33.11.0", {"center": v(20.5, 109) * mm, "radius": 2.5 * mm});
            skCircle(sketch, "E2.33.12.0", {"center": v(20.5, 101) * mm, "radius": 2.5 * mm});
            skCircle(sketch, "E2.33.13.0", {"center": v(20.5, 93) * mm, "radius": 2.5 * mm});
            skCircle(sketch, "E2.33.14.0", {"center": v(20.5, 85) * mm, "radius": 2.5 * mm});
            skCircle(sketch, "E2.33.15.0", {"center": v(20.5, 77) * mm, "radius": 2.5 * mm});
            skCircle(sketch, "E2.33.16.0", {"center": v(20.5, 69) * mm, "radius": 2.5 * mm});
            skCircle(sketch, "E2.33.17.0", {"center": v(20.5, 61) * mm, "radius": 2.5 * mm});
            skCircle(sketch, "E2.33.18.0", {"center": v(20.5, 53) * mm, "radius": 2.5 * mm});
            skCircle(sketch, "E2.33.19.0", {"center": v(20.5, 45) * mm, "radius": 2.5 * mm});
            skCircle(sketch, "E2.33.20.0", {"center": v(20.5, 37) * mm, "radius": 2.5 * mm});
            skCircle(sketch, "E2.33.21.0", {"center": v(20.5, 29) * mm, "radius": 2.5 * mm});
            skCircle(sketch, "E2.33.22.0", {"center": v(20.5, 21) * mm, "radius": 2.5 * mm});
            skCircle(sketch, "E2.33.23.0", {"center": v(20.5, 13) * mm, "radius": 2.5 * mm});
            skCircle(sketch, "E2.33.24.0", {"center": v(20.5, 5) * mm, "radius": 2.5 * mm});
            skCircle(sketch, "E2.33.25.0", {"center": v(20.5, -3) * mm, "radius": 2.5 * mm});
            skCircle(sketch, "E2.33.26.0", {"center": v(20.5, -11) * mm, "radius": 2.5 * mm});
            skCircle(sketch, "E2.33.27.0", {"center": v(20.5, -19) * mm, "radius": 2.5 * mm});
            skCircle(sketch, "E2.33.28.0", {"center": v(20.5, -27) * mm, "radius": 2.5 * mm});
            skCircle(sketch, "E2.33.29.0", {"center": v(20.5, -35) * mm, "radius": 2.5 * mm});
            skCircle(sketch, "E2.33.30.0", {"center": v(20.5, -43) * mm, "radius": 2.5 * mm});
            skCircle(sketch, "E2.33.31.0", {"center": v(20.5, -51) * mm, "radius": 2.5 * mm});
            skCircle(sketch, "E2.33.32.0", {"center": v(20.5, -59) * mm, "radius": 2.5 * mm});
            skCircle(sketch, "E2.33.33.0", {"center": v(20.5, -67) * mm, "radius": 2.5 * mm});
            skCircle(sketch, "E2.33.34.0", {"center": v(20.5, -75) * mm, "radius": 2.5 * mm});
            skCircle(sketch, "E2.33.35.0", {"center": v(20.5, -83) * mm, "radius": 2.5 * mm});
            skCircle(sketch, "E2.33.36.0", {"center": v(20.5, -91) * mm, "radius": 2.5 * mm});
            skCircle(sketch, "E2.33.37.0", {"center": v(20.5, -99) * mm, "radius": 2.5 * mm});
            skCircle(sketch, "E2.33.38.0", {"center": v(20.5, -107) * mm, "radius": 2.5 * mm});
            skCircle(sketch, "E2.33.39.0", {"center": v(20.5, -115) * mm, "radius": 2.5 * mm});
            skCircle(sketch, "E2.33.40.0", {"center": v(20.5, -123) * mm, "radius": 2.5 * mm});
            skCircle(sketch, "E2.33.41.0", {"center": v(20.5, -131) * mm, "radius": 2.5 * mm});
            skCircle(sketch, "E2.33.42.0", {"center": v(20.5, -139) * mm, "radius": 2.5 * mm});
            skCircle(sketch, "E2.33.43.0", {"center": v(20.5, -147) * mm, "radius": 2.5 * mm});
            skCircle(sketch, "E2.33.44.0", {"center": v(20.5, -155) * mm, "radius": 2.5 * mm});
            skCircle(sketch, "E2.33.45.0", {"center": v(20.5, -163) * mm, "radius": 2.5 * mm});
            skCircle(sketch, "E2.33.46.0", {"center": v(20.5, -171) * mm, "radius": 2.5 * mm});
            skCircle(sketch, "E2.33.47.0", {"center": v(20.5, -179) * mm, "radius": 2.5 * mm});
            skCircle(sketch, "E2.33.48.0", {"center": v(20.5, -187) * mm, "radius": 2.5 * mm});
            skCircle(sketch, "E2.33.49.0", {"center": v(20.5, -195) * mm, "radius": 2.5 * mm});
            skCircle(sketch, "E2.34.0.0", {"center": v(28.5, 197) * mm, "radius": 2.5 * mm});
            skCircle(sketch, "E2.34.1.0", {"center": v(28.5, 189) * mm, "radius": 2.5 * mm});
            skCircle(sketch, "E2.34.2.0", {"center": v(28.5, 181) * mm, "radius": 2.5 * mm});
            skCircle(sketch, "E2.34.3.0", {"center": v(28.5, 173) * mm, "radius": 2.5 * mm});
            skCircle(sketch, "E2.34.4.0", {"center": v(28.5, 165) * mm, "radius": 2.5 * mm});
            skCircle(sketch, "E2.34.5.0", {"center": v(28.5, 157) * mm, "radius": 2.5 * mm});
            skCircle(sketch, "E2.34.6.0", {"center": v(28.5, 149) * mm, "radius": 2.5 * mm});
            skCircle(sketch, "E2.34.7.0", {"center": v(28.5, 141) * mm, "radius": 2.5 * mm});
            skCircle(sketch, "E2.34.8.0", {"center": v(28.5, 133) * mm, "radius": 2.5 * mm});
            skCircle(sketch, "E2.34.9.0", {"center": v(28.5, 125) * mm, "radius": 2.5 * mm});
            skCircle(sketch, "E2.34.10.0", {"center": v(28.5, 117) * mm, "radius": 2.5 * mm});
            skCircle(sketch, "E2.34.11.0", {"center": v(28.5, 109) * mm, "radius": 2.5 * mm});
            skCircle(sketch, "E2.34.12.0", {"center": v(28.5, 101) * mm, "radius": 2.5 * mm});
            skCircle(sketch, "E2.34.13.0", {"center": v(28.5, 93) * mm, "radius": 2.5 * mm});
            skCircle(sketch, "E2.34.14.0", {"center": v(28.5, 85) * mm, "radius": 2.5 * mm});
            skCircle(sketch, "E2.34.15.0", {"center": v(28.5, 77) * mm, "radius": 2.5 * mm});
            skCircle(sketch, "E2.34.16.0", {"center": v(28.5, 69) * mm, "radius": 2.5 * mm});
            skCircle(sketch, "E2.34.17.0", {"center": v(28.5, 61) * mm, "radius": 2.5 * mm});
            skCircle(sketch, "E2.34.18.0", {"center": v(28.5, 53) * mm, "radius": 2.5 * mm});
            skCircle(sketch, "E2.34.19.0", {"center": v(28.5, 45) * mm, "radius": 2.5 * mm});
            skCircle(sketch, "E2.34.20.0", {"center": v(28.5, 37) * mm, "radius": 2.5 * mm});
            skCircle(sketch, "E2.34.21.0", {"center": v(28.5, 29) * mm, "radius": 2.5 * mm});
            skCircle(sketch, "E2.34.22.0", {"center": v(28.5, 21) * mm, "radius": 2.5 * mm});
            skCircle(sketch, "E2.34.23.0", {"center": v(28.5, 13) * mm, "radius": 2.5 * mm});
            skCircle(sketch, "E2.34.24.0", {"center": v(28.5, 5) * mm, "radius": 2.5 * mm});
            skCircle(sketch, "E2.34.25.0", {"center": v(28.5, -3) * mm, "radius": 2.5 * mm});
            skCircle(sketch, "E2.34.26.0", {"center": v(28.5, -11) * mm, "radius": 2.5 * mm});
            skCircle(sketch, "E2.34.27.0", {"center": v(28.5, -19) * mm, "radius": 2.5 * mm});
            skCircle(sketch, "E2.34.28.0", {"center": v(28.5, -27) * mm, "radius": 2.5 * mm});
            skCircle(sketch, "E2.34.29.0", {"center": v(28.5, -35) * mm, "radius": 2.5 * mm});
            skCircle(sketch, "E2.34.30.0", {"center": v(28.5, -43) * mm, "radius": 2.5 * mm});
            skCircle(sketch, "E2.34.31.0", {"center": v(28.5, -51) * mm, "radius": 2.5 * mm});
            skCircle(sketch, "E2.34.32.0", {"center": v(28.5, -59) * mm, "radius": 2.5 * mm});
            skCircle(sketch, "E2.34.33.0", {"center": v(28.5, -67) * mm, "radius": 2.5 * mm});
            skCircle(sketch, "E2.34.34.0", {"center": v(28.5, -75) * mm, "radius": 2.5 * mm});
            skCircle(sketch, "E2.34.35.0", {"center": v(28.5, -83) * mm, "radius": 2.5 * mm});
            skCircle(sketch, "E2.34.36.0", {"center": v(28.5, -91) * mm, "radius": 2.5 * mm});
            skCircle(sketch, "E2.34.37.0", {"center": v(28.5, -99) * mm, "radius": 2.5 * mm});
            skCircle(sketch, "E2.34.38.0", {"center": v(28.5, -107) * mm, "radius": 2.5 * mm});
            skCircle(sketch, "E2.34.39.0", {"center": v(28.5, -115) * mm, "radius": 2.5 * mm});
            skCircle(sketch, "E2.34.40.0", {"center": v(28.5, -123) * mm, "radius": 2.5 * mm});
            skCircle(sketch, "E2.34.41.0", {"center": v(28.5, -131) * mm, "radius": 2.5 * mm});
            skCircle(sketch, "E2.34.42.0", {"center": v(28.5, -139) * mm, "radius": 2.5 * mm});
            skCircle(sketch, "E2.34.43.0", {"center": v(28.5, -147) * mm, "radius": 2.5 * mm});
            skCircle(sketch, "E2.34.44.0", {"center": v(28.5, -155) * mm, "radius": 2.5 * mm});
            skCircle(sketch, "E2.34.45.0", {"center": v(28.5, -163) * mm, "radius": 2.5 * mm});
            skCircle(sketch, "E2.34.46.0", {"center": v(28.5, -171) * mm, "radius": 2.5 * mm});
            skCircle(sketch, "E2.34.47.0", {"center": v(28.5, -179) * mm, "radius": 2.5 * mm});
            skCircle(sketch, "E2.34.48.0", {"center": v(28.5, -187) * mm, "radius": 2.5 * mm});
            skCircle(sketch, "E2.34.49.0", {"center": v(28.5, -195) * mm, "radius": 2.5 * mm});
            skCircle(sketch, "E2.35.0.0", {"center": v(36.5, 197) * mm, "radius": 2.5 * mm});
            skCircle(sketch, "E2.35.1.0", {"center": v(36.5, 189) * mm, "radius": 2.5 * mm});
            skCircle(sketch, "E2.35.2.0", {"center": v(36.5, 181) * mm, "radius": 2.5 * mm});
            skCircle(sketch, "E2.35.3.0", {"center": v(36.5, 173) * mm, "radius": 2.5 * mm});
            skCircle(sketch, "E2.35.4.0", {"center": v(36.5, 165) * mm, "radius": 2.5 * mm});
            skCircle(sketch, "E2.35.5.0", {"center": v(36.5, 157) * mm, "radius": 2.5 * mm});
            skCircle(sketch, "E2.35.6.0", {"center": v(36.5, 149) * mm, "radius": 2.5 * mm});
            skCircle(sketch, "E2.35.7.0", {"center": v(36.5, 141) * mm, "radius": 2.5 * mm});
            skCircle(sketch, "E2.35.8.0", {"center": v(36.5, 133) * mm, "radius": 2.5 * mm});
            skCircle(sketch, "E2.35.9.0", {"center": v(36.5, 125) * mm, "radius": 2.5 * mm});
            skCircle(sketch, "E2.35.10.0", {"center": v(36.5, 117) * mm, "radius": 2.5 * mm});
            skCircle(sketch, "E2.35.11.0", {"center": v(36.5, 109) * mm, "radius": 2.5 * mm});
            skCircle(sketch, "E2.35.12.0", {"center": v(36.5, 101) * mm, "radius": 2.5 * mm});
            skCircle(sketch, "E2.35.13.0", {"center": v(36.5, 93) * mm, "radius": 2.5 * mm});
            skCircle(sketch, "E2.35.14.0", {"center": v(36.5, 85) * mm, "radius": 2.5 * mm});
            skCircle(sketch, "E2.35.15.0", {"center": v(36.5, 77) * mm, "radius": 2.5 * mm});
            skCircle(sketch, "E2.35.16.0", {"center": v(36.5, 69) * mm, "radius": 2.5 * mm});
            skCircle(sketch, "E2.35.17.0", {"center": v(36.5, 61) * mm, "radius": 2.5 * mm});
            skCircle(sketch, "E2.35.18.0", {"center": v(36.5, 53) * mm, "radius": 2.5 * mm});
            skCircle(sketch, "E2.35.19.0", {"center": v(36.5, 45) * mm, "radius": 2.5 * mm});
            skCircle(sketch, "E2.35.20.0", {"center": v(36.5, 37) * mm, "radius": 2.5 * mm});
            skCircle(sketch, "E2.35.21.0", {"center": v(36.5, 29) * mm, "radius": 2.5 * mm});
            skCircle(sketch, "E2.35.22.0", {"center": v(36.5, 21) * mm, "radius": 2.5 * mm});
            skCircle(sketch, "E2.35.23.0", {"center": v(36.5, 13) * mm, "radius": 2.5 * mm});
            skCircle(sketch, "E2.35.24.0", {"center": v(36.5, 5) * mm, "radius": 2.5 * mm});
            skCircle(sketch, "E2.35.25.0", {"center": v(36.5, -3) * mm, "radius": 2.5 * mm});
            skCircle(sketch, "E2.35.26.0", {"center": v(36.5, -11) * mm, "radius": 2.5 * mm});
            skCircle(sketch, "E2.35.27.0", {"center": v(36.5, -19) * mm, "radius": 2.5 * mm});
            skCircle(sketch, "E2.35.28.0", {"center": v(36.5, -27) * mm, "radius": 2.5 * mm});
            skCircle(sketch, "E2.35.29.0", {"center": v(36.5, -35) * mm, "radius": 2.5 * mm});
            skCircle(sketch, "E2.35.30.0", {"center": v(36.5, -43) * mm, "radius": 2.5 * mm});
            skCircle(sketch, "E2.35.31.0", {"center": v(36.5, -51) * mm, "radius": 2.5 * mm});
            skCircle(sketch, "E2.35.32.0", {"center": v(36.5, -59) * mm, "radius": 2.5 * mm});
            skCircle(sketch, "E2.35.33.0", {"center": v(36.5, -67) * mm, "radius": 2.5 * mm});
            skCircle(sketch, "E2.35.34.0", {"center": v(36.5, -75) * mm, "radius": 2.5 * mm});
            skCircle(sketch, "E2.35.35.0", {"center": v(36.5, -83) * mm, "radius": 2.5 * mm});
            skCircle(sketch, "E2.35.36.0", {"center": v(36.5, -91) * mm, "radius": 2.5 * mm});
            skCircle(sketch, "E2.35.37.0", {"center": v(36.5, -99) * mm, "radius": 2.5 * mm});
            skCircle(sketch, "E2.35.38.0", {"center": v(36.5, -107) * mm, "radius": 2.5 * mm});
            skCircle(sketch, "E2.35.39.0", {"center": v(36.5, -115) * mm, "radius": 2.5 * mm});
            skCircle(sketch, "E2.35.40.0", {"center": v(36.5, -123) * mm, "radius": 2.5 * mm});
            skCircle(sketch, "E2.35.41.0", {"center": v(36.5, -131) * mm, "radius": 2.5 * mm});
            skCircle(sketch, "E2.35.42.0", {"center": v(36.5, -139) * mm, "radius": 2.5 * mm});
            skCircle(sketch, "E2.35.43.0", {"center": v(36.5, -147) * mm, "radius": 2.5 * mm});
            skCircle(sketch, "E2.35.44.0", {"center": v(36.5, -155) * mm, "radius": 2.5 * mm});
            skCircle(sketch, "E2.35.45.0", {"center": v(36.5, -163) * mm, "radius": 2.5 * mm});
            skCircle(sketch, "E2.35.46.0", {"center": v(36.5, -171) * mm, "radius": 2.5 * mm});
            skCircle(sketch, "E2.35.47.0", {"center": v(36.5, -179) * mm, "radius": 2.5 * mm});
            skCircle(sketch, "E2.35.48.0", {"center": v(36.5, -187) * mm, "radius": 2.5 * mm});
            skCircle(sketch, "E2.35.49.0", {"center": v(36.5, -195) * mm, "radius": 2.5 * mm});
            skCircle(sketch, "E2.36.0.0", {"center": v(44.5, 197) * mm, "radius": 2.5 * mm});
            skCircle(sketch, "E2.36.1.0", {"center": v(44.5, 189) * mm, "radius": 2.5 * mm});
            skCircle(sketch, "E2.36.2.0", {"center": v(44.5, 181) * mm, "radius": 2.5 * mm});
            skCircle(sketch, "E2.36.3.0", {"center": v(44.5, 173) * mm, "radius": 2.5 * mm});
            skCircle(sketch, "E2.36.4.0", {"center": v(44.5, 165) * mm, "radius": 2.5 * mm});
            skCircle(sketch, "E2.36.5.0", {"center": v(44.5, 157) * mm, "radius": 2.5 * mm});
            skCircle(sketch, "E2.36.6.0", {"center": v(44.5, 149) * mm, "radius": 2.5 * mm});
            skCircle(sketch, "E2.36.7.0", {"center": v(44.5, 141) * mm, "radius": 2.5 * mm});
            skCircle(sketch, "E2.36.8.0", {"center": v(44.5, 133) * mm, "radius": 2.5 * mm});
            skCircle(sketch, "E2.36.9.0", {"center": v(44.5, 125) * mm, "radius": 2.5 * mm});
            skCircle(sketch, "E2.36.10.0", {"center": v(44.5, 117) * mm, "radius": 2.5 * mm});
            skCircle(sketch, "E2.36.11.0", {"center": v(44.5, 109) * mm, "radius": 2.5 * mm});
            skCircle(sketch, "E2.36.12.0", {"center": v(44.5, 101) * mm, "radius": 2.5 * mm});
            skCircle(sketch, "E2.36.13.0", {"center": v(44.5, 93) * mm, "radius": 2.5 * mm});
            skCircle(sketch, "E2.36.14.0", {"center": v(44.5, 85) * mm, "radius": 2.5 * mm});
            skCircle(sketch, "E2.36.15.0", {"center": v(44.5, 77) * mm, "radius": 2.5 * mm});
            skCircle(sketch, "E2.36.16.0", {"center": v(44.5, 69) * mm, "radius": 2.5 * mm});
            skCircle(sketch, "E2.36.17.0", {"center": v(44.5, 61) * mm, "radius": 2.5 * mm});
            skCircle(sketch, "E2.36.18.0", {"center": v(44.5, 53) * mm, "radius": 2.5 * mm});
            skCircle(sketch, "E2.36.19.0", {"center": v(44.5, 45) * mm, "radius": 2.5 * mm});
            skCircle(sketch, "E2.36.20.0", {"center": v(44.5, 37) * mm, "radius": 2.5 * mm});
            skCircle(sketch, "E2.36.21.0", {"center": v(44.5, 29) * mm, "radius": 2.5 * mm});
            skCircle(sketch, "E2.36.22.0", {"center": v(44.5, 21) * mm, "radius": 2.5 * mm});
            skCircle(sketch, "E2.36.23.0", {"center": v(44.5, 13) * mm, "radius": 2.5 * mm});
            skCircle(sketch, "E2.36.24.0", {"center": v(44.5, 5) * mm, "radius": 2.5 * mm});
            skCircle(sketch, "E2.36.25.0", {"center": v(44.5, -3) * mm, "radius": 2.5 * mm});
            skCircle(sketch, "E2.36.26.0", {"center": v(44.5, -11) * mm, "radius": 2.5 * mm});
            skCircle(sketch, "E2.36.27.0", {"center": v(44.5, -19) * mm, "radius": 2.5 * mm});
            skCircle(sketch, "E2.36.28.0", {"center": v(44.5, -27) * mm, "radius": 2.5 * mm});
            skCircle(sketch, "E2.36.29.0", {"center": v(44.5, -35) * mm, "radius": 2.5 * mm});
            skCircle(sketch, "E2.36.30.0", {"center": v(44.5, -43) * mm, "radius": 2.5 * mm});
            skCircle(sketch, "E2.36.31.0", {"center": v(44.5, -51) * mm, "radius": 2.5 * mm});
            skCircle(sketch, "E2.36.32.0", {"center": v(44.5, -59) * mm, "radius": 2.5 * mm});
            skCircle(sketch, "E2.36.33.0", {"center": v(44.5, -67) * mm, "radius": 2.5 * mm});
            skCircle(sketch, "E2.36.34.0", {"center": v(44.5, -75) * mm, "radius": 2.5 * mm});
            skCircle(sketch, "E2.36.35.0", {"center": v(44.5, -83) * mm, "radius": 2.5 * mm});
            skCircle(sketch, "E2.36.36.0", {"center": v(44.5, -91) * mm, "radius": 2.5 * mm});
            skCircle(sketch, "E2.36.37.0", {"center": v(44.5, -99) * mm, "radius": 2.5 * mm});
            skCircle(sketch, "E2.36.38.0", {"center": v(44.5, -107) * mm, "radius": 2.5 * mm});
            skCircle(sketch, "E2.36.39.0", {"center": v(44.5, -115) * mm, "radius": 2.5 * mm});
            skCircle(sketch, "E2.36.40.0", {"center": v(44.5, -123) * mm, "radius": 2.5 * mm});
            skCircle(sketch, "E2.36.41.0", {"center": v(44.5, -131) * mm, "radius": 2.5 * mm});
            skCircle(sketch, "E2.36.42.0", {"center": v(44.5, -139) * mm, "radius": 2.5 * mm});
            skCircle(sketch, "E2.36.43.0", {"center": v(44.5, -147) * mm, "radius": 2.5 * mm});
            skCircle(sketch, "E2.36.44.0", {"center": v(44.5, -155) * mm, "radius": 2.5 * mm});
            skCircle(sketch, "E2.36.45.0", {"center": v(44.5, -163) * mm, "radius": 2.5 * mm});
            skCircle(sketch, "E2.36.46.0", {"center": v(44.5, -171) * mm, "radius": 2.5 * mm});
            skCircle(sketch, "E2.36.47.0", {"center": v(44.5, -179) * mm, "radius": 2.5 * mm});
            skCircle(sketch, "E2.36.48.0", {"center": v(44.5, -187) * mm, "radius": 2.5 * mm});
            skCircle(sketch, "E2.36.49.0", {"center": v(44.5, -195) * mm, "radius": 2.5 * mm});
            skCircle(sketch, "E2.37.0.0", {"center": v(52.5, 197) * mm, "radius": 2.5 * mm});
            skCircle(sketch, "E2.37.1.0", {"center": v(52.5, 189) * mm, "radius": 2.5 * mm});
            skCircle(sketch, "E2.37.2.0", {"center": v(52.5, 181) * mm, "radius": 2.5 * mm});
            skCircle(sketch, "E2.37.3.0", {"center": v(52.5, 173) * mm, "radius": 2.5 * mm});
            skCircle(sketch, "E2.37.4.0", {"center": v(52.5, 165) * mm, "radius": 2.5 * mm});
            skCircle(sketch, "E2.37.5.0", {"center": v(52.5, 157) * mm, "radius": 2.5 * mm});
            skCircle(sketch, "E2.37.6.0", {"center": v(52.5, 149) * mm, "radius": 2.5 * mm});
            skCircle(sketch, "E2.37.7.0", {"center": v(52.5, 141) * mm, "radius": 2.5 * mm});
            skCircle(sketch, "E2.37.8.0", {"center": v(52.5, 133) * mm, "radius": 2.5 * mm});
            skCircle(sketch, "E2.37.9.0", {"center": v(52.5, 125) * mm, "radius": 2.5 * mm});
            skCircle(sketch, "E2.37.10.0", {"center": v(52.5, 117) * mm, "radius": 2.5 * mm});
            skCircle(sketch, "E2.37.11.0", {"center": v(52.5, 109) * mm, "radius": 2.5 * mm});
            skCircle(sketch, "E2.37.12.0", {"center": v(52.5, 101) * mm, "radius": 2.5 * mm});
            skCircle(sketch, "E2.37.13.0", {"center": v(52.5, 93) * mm, "radius": 2.5 * mm});
            skCircle(sketch, "E2.37.14.0", {"center": v(52.5, 85) * mm, "radius": 2.5 * mm});
            skCircle(sketch, "E2.37.15.0", {"center": v(52.5, 77) * mm, "radius": 2.5 * mm});
            skCircle(sketch, "E2.37.16.0", {"center": v(52.5, 69) * mm, "radius": 2.5 * mm});
            skCircle(sketch, "E2.37.17.0", {"center": v(52.5, 61) * mm, "radius": 2.5 * mm});
            skCircle(sketch, "E2.37.18.0", {"center": v(52.5, 53) * mm, "radius": 2.5 * mm});
            skCircle(sketch, "E2.37.19.0", {"center": v(52.5, 45) * mm, "radius": 2.5 * mm});
            skCircle(sketch, "E2.37.20.0", {"center": v(52.5, 37) * mm, "radius": 2.5 * mm});
            skCircle(sketch, "E2.37.21.0", {"center": v(52.5, 29) * mm, "radius": 2.5 * mm});
            skCircle(sketch, "E2.37.22.0", {"center": v(52.5, 21) * mm, "radius": 2.5 * mm});
            skCircle(sketch, "E2.37.23.0", {"center": v(52.5, 13) * mm, "radius": 2.5 * mm});
            skCircle(sketch, "E2.37.24.0", {"center": v(52.5, 5) * mm, "radius": 2.5 * mm});
            skCircle(sketch, "E2.37.25.0", {"center": v(52.5, -3) * mm, "radius": 2.5 * mm});
            skCircle(sketch, "E2.37.26.0", {"center": v(52.5, -11) * mm, "radius": 2.5 * mm});
            skCircle(sketch, "E2.37.27.0", {"center": v(52.5, -19) * mm, "radius": 2.5 * mm});
            skCircle(sketch, "E2.37.28.0", {"center": v(52.5, -27) * mm, "radius": 2.5 * mm});
            skCircle(sketch, "E2.37.29.0", {"center": v(52.5, -35) * mm, "radius": 2.5 * mm});
            skCircle(sketch, "E2.37.30.0", {"center": v(52.5, -43) * mm, "radius": 2.5 * mm});
            skCircle(sketch, "E2.37.31.0", {"center": v(52.5, -51) * mm, "radius": 2.5 * mm});
            skCircle(sketch, "E2.37.32.0", {"center": v(52.5, -59) * mm, "radius": 2.5 * mm});
            skCircle(sketch, "E2.37.33.0", {"center": v(52.5, -67) * mm, "radius": 2.5 * mm});
            skCircle(sketch, "E2.37.34.0", {"center": v(52.5, -75) * mm, "radius": 2.5 * mm});
            skCircle(sketch, "E2.37.35.0", {"center": v(52.5, -83) * mm, "radius": 2.5 * mm});
            skCircle(sketch, "E2.37.36.0", {"center": v(52.5, -91) * mm, "radius": 2.5 * mm});
            skCircle(sketch, "E2.37.37.0", {"center": v(52.5, -99) * mm, "radius": 2.5 * mm});
            skCircle(sketch, "E2.37.38.0", {"center": v(52.5, -107) * mm, "radius": 2.5 * mm});
            skCircle(sketch, "E2.37.39.0", {"center": v(52.5, -115) * mm, "radius": 2.5 * mm});
            skCircle(sketch, "E2.37.40.0", {"center": v(52.5, -123) * mm, "radius": 2.5 * mm});
            skCircle(sketch, "E2.37.41.0", {"center": v(52.5, -131) * mm, "radius": 2.5 * mm});
            skCircle(sketch, "E2.37.42.0", {"center": v(52.5, -139) * mm, "radius": 2.5 * mm});
            skCircle(sketch, "E2.37.43.0", {"center": v(52.5, -147) * mm, "radius": 2.5 * mm});
            skCircle(sketch, "E2.37.44.0", {"center": v(52.5, -155) * mm, "radius": 2.5 * mm});
            skCircle(sketch, "E2.37.45.0", {"center": v(52.5, -163) * mm, "radius": 2.5 * mm});
            skCircle(sketch, "E2.37.46.0", {"center": v(52.5, -171) * mm, "radius": 2.5 * mm});
            skCircle(sketch, "E2.37.47.0", {"center": v(52.5, -179) * mm, "radius": 2.5 * mm});
            skCircle(sketch, "E2.37.48.0", {"center": v(52.5, -187) * mm, "radius": 2.5 * mm});
            skCircle(sketch, "E2.37.49.0", {"center": v(52.5, -195) * mm, "radius": 2.5 * mm});
            skCircle(sketch, "E2.38.0.0", {"center": v(60.5, 197) * mm, "radius": 2.5 * mm});
            skCircle(sketch, "E2.38.1.0", {"center": v(60.5, 189) * mm, "radius": 2.5 * mm});
            skCircle(sketch, "E2.38.2.0", {"center": v(60.5, 181) * mm, "radius": 2.5 * mm});
            skCircle(sketch, "E2.38.3.0", {"center": v(60.5, 173) * mm, "radius": 2.5 * mm});
            skCircle(sketch, "E2.38.4.0", {"center": v(60.5, 165) * mm, "radius": 2.5 * mm});
            skCircle(sketch, "E2.38.5.0", {"center": v(60.5, 157) * mm, "radius": 2.5 * mm});
            skCircle(sketch, "E2.38.6.0", {"center": v(60.5, 149) * mm, "radius": 2.5 * mm});
            skCircle(sketch, "E2.38.7.0", {"center": v(60.5, 141) * mm, "radius": 2.5 * mm});
            skCircle(sketch, "E2.38.8.0", {"center": v(60.5, 133) * mm, "radius": 2.5 * mm});
            skCircle(sketch, "E2.38.9.0", {"center": v(60.5, 125) * mm, "radius": 2.5 * mm});
            skCircle(sketch, "E2.38.10.0", {"center": v(60.5, 117) * mm, "radius": 2.5 * mm});
            skCircle(sketch, "E2.38.11.0", {"center": v(60.5, 109) * mm, "radius": 2.5 * mm});
            skCircle(sketch, "E2.38.12.0", {"center": v(60.5, 101) * mm, "radius": 2.5 * mm});
            skCircle(sketch, "E2.38.13.0", {"center": v(60.5, 93) * mm, "radius": 2.5 * mm});
            skCircle(sketch, "E2.38.14.0", {"center": v(60.5, 85) * mm, "radius": 2.5 * mm});
            skCircle(sketch, "E2.38.15.0", {"center": v(60.5, 77) * mm, "radius": 2.5 * mm});
            skCircle(sketch, "E2.38.16.0", {"center": v(60.5, 69) * mm, "radius": 2.5 * mm});
            skCircle(sketch, "E2.38.17.0", {"center": v(60.5, 61) * mm, "radius": 2.5 * mm});
            skCircle(sketch, "E2.38.18.0", {"center": v(60.5, 53) * mm, "radius": 2.5 * mm});
            skCircle(sketch, "E2.38.19.0", {"center": v(60.5, 45) * mm, "radius": 2.5 * mm});
            skCircle(sketch, "E2.38.20.0", {"center": v(60.5, 37) * mm, "radius": 2.5 * mm});
            skCircle(sketch, "E2.38.21.0", {"center": v(60.5, 29) * mm, "radius": 2.5 * mm});
            skCircle(sketch, "E2.38.22.0", {"center": v(60.5, 21) * mm, "radius": 2.5 * mm});
            skCircle(sketch, "E2.38.23.0", {"center": v(60.5, 13) * mm, "radius": 2.5 * mm});
            skCircle(sketch, "E2.38.24.0", {"center": v(60.5, 5) * mm, "radius": 2.5 * mm});
            skCircle(sketch, "E2.38.25.0", {"center": v(60.5, -3) * mm, "radius": 2.5 * mm});
            skCircle(sketch, "E2.38.26.0", {"center": v(60.5, -11) * mm, "radius": 2.5 * mm});
            skCircle(sketch, "E2.38.27.0", {"center": v(60.5, -19) * mm, "radius": 2.5 * mm});
            skCircle(sketch, "E2.38.28.0", {"center": v(60.5, -27) * mm, "radius": 2.5 * mm});
            skCircle(sketch, "E2.38.29.0", {"center": v(60.5, -35) * mm, "radius": 2.5 * mm});
            skCircle(sketch, "E2.38.30.0", {"center": v(60.5, -43) * mm, "radius": 2.5 * mm});
            skCircle(sketch, "E2.38.31.0", {"center": v(60.5, -51) * mm, "radius": 2.5 * mm});
            skCircle(sketch, "E2.38.32.0", {"center": v(60.5, -59) * mm, "radius": 2.5 * mm});
            skCircle(sketch, "E2.38.33.0", {"center": v(60.5, -67) * mm, "radius": 2.5 * mm});
            skCircle(sketch, "E2.38.34.0", {"center": v(60.5, -75) * mm, "radius": 2.5 * mm});
            skCircle(sketch, "E2.38.35.0", {"center": v(60.5, -83) * mm, "radius": 2.5 * mm});
            skCircle(sketch, "E2.38.36.0", {"center": v(60.5, -91) * mm, "radius": 2.5 * mm});
            skCircle(sketch, "E2.38.37.0", {"center": v(60.5, -99) * mm, "radius": 2.5 * mm});
            skCircle(sketch, "E2.38.38.0", {"center": v(60.5, -107) * mm, "radius": 2.5 * mm});
            skCircle(sketch, "E2.38.39.0", {"center": v(60.5, -115) * mm, "radius": 2.5 * mm});
            skCircle(sketch, "E2.38.40.0", {"center": v(60.5, -123) * mm, "radius": 2.5 * mm});
            skCircle(sketch, "E2.38.41.0", {"center": v(60.5, -131) * mm, "radius": 2.5 * mm});
            skCircle(sketch, "E2.38.42.0", {"center": v(60.5, -139) * mm, "radius": 2.5 * mm});
            skCircle(sketch, "E2.38.43.0", {"center": v(60.5, -147) * mm, "radius": 2.5 * mm});
            skCircle(sketch, "E2.38.44.0", {"center": v(60.5, -155) * mm, "radius": 2.5 * mm});
            skCircle(sketch, "E2.38.45.0", {"center": v(60.5, -163) * mm, "radius": 2.5 * mm});
            skCircle(sketch, "E2.38.46.0", {"center": v(60.5, -171) * mm, "radius": 2.5 * mm});
            skCircle(sketch, "E2.38.47.0", {"center": v(60.5, -179) * mm, "radius": 2.5 * mm});
            skCircle(sketch, "E2.38.48.0", {"center": v(60.5, -187) * mm, "radius": 2.5 * mm});
            skCircle(sketch, "E2.38.49.0", {"center": v(60.5, -195) * mm, "radius": 2.5 * mm});
            skCircle(sketch, "E2.39.0.0", {"center": v(68.5, 197) * mm, "radius": 2.5 * mm});
            skCircle(sketch, "E2.39.1.0", {"center": v(68.5, 189) * mm, "radius": 2.5 * mm});
            skCircle(sketch, "E2.39.2.0", {"center": v(68.5, 181) * mm, "radius": 2.5 * mm});
            skCircle(sketch, "E2.39.3.0", {"center": v(68.5, 173) * mm, "radius": 2.5 * mm});
            skCircle(sketch, "E2.39.4.0", {"center": v(68.5, 165) * mm, "radius": 2.5 * mm});
            skCircle(sketch, "E2.39.5.0", {"center": v(68.5, 157) * mm, "radius": 2.5 * mm});
            skCircle(sketch, "E2.39.6.0", {"center": v(68.5, 149) * mm, "radius": 2.5 * mm});
            skCircle(sketch, "E2.39.7.0", {"center": v(68.5, 141) * mm, "radius": 2.5 * mm});
            skCircle(sketch, "E2.39.8.0", {"center": v(68.5, 133) * mm, "radius": 2.5 * mm});
            skCircle(sketch, "E2.39.9.0", {"center": v(68.5, 125) * mm, "radius": 2.5 * mm});
            skCircle(sketch, "E2.39.10.0", {"center": v(68.5, 117) * mm, "radius": 2.5 * mm});
            skCircle(sketch, "E2.39.11.0", {"center": v(68.5, 109) * mm, "radius": 2.5 * mm});
            skCircle(sketch, "E2.39.12.0", {"center": v(68.5, 101) * mm, "radius": 2.5 * mm});
            skCircle(sketch, "E2.39.13.0", {"center": v(68.5, 93) * mm, "radius": 2.5 * mm});
            skCircle(sketch, "E2.39.14.0", {"center": v(68.5, 85) * mm, "radius": 2.5 * mm});
            skCircle(sketch, "E2.39.15.0", {"center": v(68.5, 77) * mm, "radius": 2.5 * mm});
            skCircle(sketch, "E2.39.16.0", {"center": v(68.5, 69) * mm, "radius": 2.5 * mm});
            skCircle(sketch, "E2.39.17.0", {"center": v(68.5, 61) * mm, "radius": 2.5 * mm});
            skCircle(sketch, "E2.39.18.0", {"center": v(68.5, 53) * mm, "radius": 2.5 * mm});
            skCircle(sketch, "E2.39.19.0", {"center": v(68.5, 45) * mm, "radius": 2.5 * mm});
            skCircle(sketch, "E2.39.20.0", {"center": v(68.5, 37) * mm, "radius": 2.5 * mm});
            skCircle(sketch, "E2.39.21.0", {"center": v(68.5, 29) * mm, "radius": 2.5 * mm});
            skCircle(sketch, "E2.39.22.0", {"center": v(68.5, 21) * mm, "radius": 2.5 * mm});
            skCircle(sketch, "E2.39.23.0", {"center": v(68.5, 13) * mm, "radius": 2.5 * mm});
            skCircle(sketch, "E2.39.24.0", {"center": v(68.5, 5) * mm, "radius": 2.5 * mm});
            skCircle(sketch, "E2.39.25.0", {"center": v(68.5, -3) * mm, "radius": 2.5 * mm});
            skCircle(sketch, "E2.39.26.0", {"center": v(68.5, -11) * mm, "radius": 2.5 * mm});
            skCircle(sketch, "E2.39.27.0", {"center": v(68.5, -19) * mm, "radius": 2.5 * mm});
            skCircle(sketch, "E2.39.28.0", {"center": v(68.5, -27) * mm, "radius": 2.5 * mm});
            skCircle(sketch, "E2.39.29.0", {"center": v(68.5, -35) * mm, "radius": 2.5 * mm});
            skCircle(sketch, "E2.39.30.0", {"center": v(68.5, -43) * mm, "radius": 2.5 * mm});
            skCircle(sketch, "E2.39.31.0", {"center": v(68.5, -51) * mm, "radius": 2.5 * mm});
            skCircle(sketch, "E2.39.32.0", {"center": v(68.5, -59) * mm, "radius": 2.5 * mm});
            skCircle(sketch, "E2.39.33.0", {"center": v(68.5, -67) * mm, "radius": 2.5 * mm});
            skCircle(sketch, "E2.39.34.0", {"center": v(68.5, -75) * mm, "radius": 2.5 * mm});
            skCircle(sketch, "E2.39.35.0", {"center": v(68.5, -83) * mm, "radius": 2.5 * mm});
            skCircle(sketch, "E2.39.36.0", {"center": v(68.5, -91) * mm, "radius": 2.5 * mm});
            skCircle(sketch, "E2.39.37.0", {"center": v(68.5, -99) * mm, "radius": 2.5 * mm});
            skCircle(sketch, "E2.39.38.0", {"center": v(68.5, -107) * mm, "radius": 2.5 * mm});
            skCircle(sketch, "E2.39.39.0", {"center": v(68.5, -115) * mm, "radius": 2.5 * mm});
            skCircle(sketch, "E2.39.40.0", {"center": v(68.5, -123) * mm, "radius": 2.5 * mm});
            skCircle(sketch, "E2.39.41.0", {"center": v(68.5, -131) * mm, "radius": 2.5 * mm});
            skCircle(sketch, "E2.39.42.0", {"center": v(68.5, -139) * mm, "radius": 2.5 * mm});
            skCircle(sketch, "E2.39.43.0", {"center": v(68.5, -147) * mm, "radius": 2.5 * mm});
            skCircle(sketch, "E2.39.44.0", {"center": v(68.5, -155) * mm, "radius": 2.5 * mm});
            skCircle(sketch, "E2.39.45.0", {"center": v(68.5, -163) * mm, "radius": 2.5 * mm});
            skCircle(sketch, "E2.39.46.0", {"center": v(68.5, -171) * mm, "radius": 2.5 * mm});
            skCircle(sketch, "E2.39.47.0", {"center": v(68.5, -179) * mm, "radius": 2.5 * mm});
            skCircle(sketch, "E2.39.48.0", {"center": v(68.5, -187) * mm, "radius": 2.5 * mm});
            skCircle(sketch, "E2.39.49.0", {"center": v(68.5, -195) * mm, "radius": 2.5 * mm});
            skCircle(sketch, "E2.40.0.0", {"center": v(76.5, 197) * mm, "radius": 2.5 * mm});
            skCircle(sketch, "E2.40.1.0", {"center": v(76.5, 189) * mm, "radius": 2.5 * mm});
            skCircle(sketch, "E2.40.2.0", {"center": v(76.5, 181) * mm, "radius": 2.5 * mm});
            skCircle(sketch, "E2.40.3.0", {"center": v(76.5, 173) * mm, "radius": 2.5 * mm});
            skCircle(sketch, "E2.40.4.0", {"center": v(76.5, 165) * mm, "radius": 2.5 * mm});
            skCircle(sketch, "E2.40.5.0", {"center": v(76.5, 157) * mm, "radius": 2.5 * mm});
            skCircle(sketch, "E2.40.6.0", {"center": v(76.5, 149) * mm, "radius": 2.5 * mm});
            skCircle(sketch, "E2.40.7.0", {"center": v(76.5, 141) * mm, "radius": 2.5 * mm});
            skCircle(sketch, "E2.40.8.0", {"center": v(76.5, 133) * mm, "radius": 2.5 * mm});
            skCircle(sketch, "E2.40.9.0", {"center": v(76.5, 125) * mm, "radius": 2.5 * mm});
            skCircle(sketch, "E2.40.10.0", {"center": v(76.5, 117) * mm, "radius": 2.5 * mm});
            skCircle(sketch, "E2.40.11.0", {"center": v(76.5, 109) * mm, "radius": 2.5 * mm});
            skCircle(sketch, "E2.40.12.0", {"center": v(76.5, 101) * mm, "radius": 2.5 * mm});
            skCircle(sketch, "E2.40.13.0", {"center": v(76.5, 93) * mm, "radius": 2.5 * mm});
            skCircle(sketch, "E2.40.14.0", {"center": v(76.5, 85) * mm, "radius": 2.5 * mm});
            skCircle(sketch, "E2.40.15.0", {"center": v(76.5, 77) * mm, "radius": 2.5 * mm});
            skCircle(sketch, "E2.40.16.0", {"center": v(76.5, 69) * mm, "radius": 2.5 * mm});
            skCircle(sketch, "E2.40.17.0", {"center": v(76.5, 61) * mm, "radius": 2.5 * mm});
            skCircle(sketch, "E2.40.18.0", {"center": v(76.5, 53) * mm, "radius": 2.5 * mm});
            skCircle(sketch, "E2.40.19.0", {"center": v(76.5, 45) * mm, "radius": 2.5 * mm});
            skCircle(sketch, "E2.40.20.0", {"center": v(76.5, 37) * mm, "radius": 2.5 * mm});
            skCircle(sketch, "E2.40.21.0", {"center": v(76.5, 29) * mm, "radius": 2.5 * mm});
            skCircle(sketch, "E2.40.22.0", {"center": v(76.5, 21) * mm, "radius": 2.5 * mm});
            skCircle(sketch, "E2.40.23.0", {"center": v(76.5, 13) * mm, "radius": 2.5 * mm});
            skCircle(sketch, "E2.40.24.0", {"center": v(76.5, 5) * mm, "radius": 2.5 * mm});
            skCircle(sketch, "E2.40.25.0", {"center": v(76.5, -3) * mm, "radius": 2.5 * mm});
            skCircle(sketch, "E2.40.26.0", {"center": v(76.5, -11) * mm, "radius": 2.5 * mm});
            skCircle(sketch, "E2.40.27.0", {"center": v(76.5, -19) * mm, "radius": 2.5 * mm});
            skCircle(sketch, "E2.40.28.0", {"center": v(76.5, -27) * mm, "radius": 2.5 * mm});
            skCircle(sketch, "E2.40.29.0", {"center": v(76.5, -35) * mm, "radius": 2.5 * mm});
            skCircle(sketch, "E2.40.30.0", {"center": v(76.5, -43) * mm, "radius": 2.5 * mm});
            skCircle(sketch, "E2.40.31.0", {"center": v(76.5, -51) * mm, "radius": 2.5 * mm});
            skCircle(sketch, "E2.40.32.0", {"center": v(76.5, -59) * mm, "radius": 2.5 * mm});
            skCircle(sketch, "E2.40.33.0", {"center": v(76.5, -67) * mm, "radius": 2.5 * mm});
            skCircle(sketch, "E2.40.34.0", {"center": v(76.5, -75) * mm, "radius": 2.5 * mm});
            skCircle(sketch, "E2.40.35.0", {"center": v(76.5, -83) * mm, "radius": 2.5 * mm});
            skCircle(sketch, "E2.40.36.0", {"center": v(76.5, -91) * mm, "radius": 2.5 * mm});
            skCircle(sketch, "E2.40.37.0", {"center": v(76.5, -99) * mm, "radius": 2.5 * mm});
            skCircle(sketch, "E2.40.38.0", {"center": v(76.5, -107) * mm, "radius": 2.5 * mm});
            skCircle(sketch, "E2.40.39.0", {"center": v(76.5, -115) * mm, "radius": 2.5 * mm});
            skCircle(sketch, "E2.40.40.0", {"center": v(76.5, -123) * mm, "radius": 2.5 * mm});
            skCircle(sketch, "E2.40.41.0", {"center": v(76.5, -131) * mm, "radius": 2.5 * mm});
            skCircle(sketch, "E2.40.42.0", {"center": v(76.5, -139) * mm, "radius": 2.5 * mm});
            skCircle(sketch, "E2.40.43.0", {"center": v(76.5, -147) * mm, "radius": 2.5 * mm});
            skCircle(sketch, "E2.40.44.0", {"center": v(76.5, -155) * mm, "radius": 2.5 * mm});
            skCircle(sketch, "E2.40.45.0", {"center": v(76.5, -163) * mm, "radius": 2.5 * mm});
            skCircle(sketch, "E2.40.46.0", {"center": v(76.5, -171) * mm, "radius": 2.5 * mm});
            skCircle(sketch, "E2.40.47.0", {"center": v(76.5, -179) * mm, "radius": 2.5 * mm});
            skCircle(sketch, "E2.40.48.0", {"center": v(76.5, -187) * mm, "radius": 2.5 * mm});
            skCircle(sketch, "E2.40.49.0", {"center": v(76.5, -195) * mm, "radius": 2.5 * mm});
            skCircle(sketch, "E2.41.0.0", {"center": v(84.5, 197) * mm, "radius": 2.5 * mm});
            skCircle(sketch, "E2.41.1.0", {"center": v(84.5, 189) * mm, "radius": 2.5 * mm});
            skCircle(sketch, "E2.41.2.0", {"center": v(84.5, 181) * mm, "radius": 2.5 * mm});
            skCircle(sketch, "E2.41.3.0", {"center": v(84.5, 173) * mm, "radius": 2.5 * mm});
            skCircle(sketch, "E2.41.4.0", {"center": v(84.5, 165) * mm, "radius": 2.5 * mm});
            skCircle(sketch, "E2.41.5.0", {"center": v(84.5, 157) * mm, "radius": 2.5 * mm});
            skCircle(sketch, "E2.41.6.0", {"center": v(84.5, 149) * mm, "radius": 2.5 * mm});
            skCircle(sketch, "E2.41.7.0", {"center": v(84.5, 141) * mm, "radius": 2.5 * mm});
            skCircle(sketch, "E2.41.8.0", {"center": v(84.5, 133) * mm, "radius": 2.5 * mm});
            skCircle(sketch, "E2.41.9.0", {"center": v(84.5, 125) * mm, "radius": 2.5 * mm});
            skCircle(sketch, "E2.41.10.0", {"center": v(84.5, 117) * mm, "radius": 2.5 * mm});
            skCircle(sketch, "E2.41.11.0", {"center": v(84.5, 109) * mm, "radius": 2.5 * mm});
            skCircle(sketch, "E2.41.12.0", {"center": v(84.5, 101) * mm, "radius": 2.5 * mm});
            skCircle(sketch, "E2.41.13.0", {"center": v(84.5, 93) * mm, "radius": 2.5 * mm});
            skCircle(sketch, "E2.41.14.0", {"center": v(84.5, 85) * mm, "radius": 2.5 * mm});
            skCircle(sketch, "E2.41.15.0", {"center": v(84.5, 77) * mm, "radius": 2.5 * mm});
            skCircle(sketch, "E2.41.16.0", {"center": v(84.5, 69) * mm, "radius": 2.5 * mm});
            skCircle(sketch, "E2.41.17.0", {"center": v(84.5, 61) * mm, "radius": 2.5 * mm});
            skCircle(sketch, "E2.41.18.0", {"center": v(84.5, 53) * mm, "radius": 2.5 * mm});
            skCircle(sketch, "E2.41.19.0", {"center": v(84.5, 45) * mm, "radius": 2.5 * mm});
            skCircle(sketch, "E2.41.20.0", {"center": v(84.5, 37) * mm, "radius": 2.5 * mm});
            skCircle(sketch, "E2.41.21.0", {"center": v(84.5, 29) * mm, "radius": 2.5 * mm});
            skCircle(sketch, "E2.41.22.0", {"center": v(84.5, 21) * mm, "radius": 2.5 * mm});
            skCircle(sketch, "E2.41.23.0", {"center": v(84.5, 13) * mm, "radius": 2.5 * mm});
            skCircle(sketch, "E2.41.24.0", {"center": v(84.5, 5) * mm, "radius": 2.5 * mm});
            skCircle(sketch, "E2.41.25.0", {"center": v(84.5, -3) * mm, "radius": 2.5 * mm});
            skCircle(sketch, "E2.41.26.0", {"center": v(84.5, -11) * mm, "radius": 2.5 * mm});
            skCircle(sketch, "E2.41.27.0", {"center": v(84.5, -19) * mm, "radius": 2.5 * mm});
            skCircle(sketch, "E2.41.28.0", {"center": v(84.5, -27) * mm, "radius": 2.5 * mm});
            skCircle(sketch, "E2.41.29.0", {"center": v(84.5, -35) * mm, "radius": 2.5 * mm});
            skCircle(sketch, "E2.41.30.0", {"center": v(84.5, -43) * mm, "radius": 2.5 * mm});
            skCircle(sketch, "E2.41.31.0", {"center": v(84.5, -51) * mm, "radius": 2.5 * mm});
            skCircle(sketch, "E2.41.32.0", {"center": v(84.5, -59) * mm, "radius": 2.5 * mm});
            skCircle(sketch, "E2.41.33.0", {"center": v(84.5, -67) * mm, "radius": 2.5 * mm});
            skCircle(sketch, "E2.41.34.0", {"center": v(84.5, -75) * mm, "radius": 2.5 * mm});
            skCircle(sketch, "E2.41.35.0", {"center": v(84.5, -83) * mm, "radius": 2.5 * mm});
            skCircle(sketch, "E2.41.36.0", {"center": v(84.5, -91) * mm, "radius": 2.5 * mm});
            skCircle(sketch, "E2.41.37.0", {"center": v(84.5, -99) * mm, "radius": 2.5 * mm});
            skCircle(sketch, "E2.41.38.0", {"center": v(84.5, -107) * mm, "radius": 2.5 * mm});
            skCircle(sketch, "E2.41.39.0", {"center": v(84.5, -115) * mm, "radius": 2.5 * mm});
            skCircle(sketch, "E2.41.40.0", {"center": v(84.5, -123) * mm, "radius": 2.5 * mm});
            skCircle(sketch, "E2.41.41.0", {"center": v(84.5, -131) * mm, "radius": 2.5 * mm});
            skCircle(sketch, "E2.41.42.0", {"center": v(84.5, -139) * mm, "radius": 2.5 * mm});
            skCircle(sketch, "E2.41.43.0", {"center": v(84.5, -147) * mm, "radius": 2.5 * mm});
            skCircle(sketch, "E2.41.44.0", {"center": v(84.5, -155) * mm, "radius": 2.5 * mm});
            skCircle(sketch, "E2.41.45.0", {"center": v(84.5, -163) * mm, "radius": 2.5 * mm});
            skCircle(sketch, "E2.41.46.0", {"center": v(84.5, -171) * mm, "radius": 2.5 * mm});
            skCircle(sketch, "E2.41.47.0", {"center": v(84.5, -179) * mm, "radius": 2.5 * mm});
            skCircle(sketch, "E2.41.48.0", {"center": v(84.5, -187) * mm, "radius": 2.5 * mm});
            skCircle(sketch, "E2.41.49.0", {"center": v(84.5, -195) * mm, "radius": 2.5 * mm});
            skCircle(sketch, "E2.42.0.0", {"center": v(92.5, 197) * mm, "radius": 2.5 * mm});
            skCircle(sketch, "E2.42.1.0", {"center": v(92.5, 189) * mm, "radius": 2.5 * mm});
            skCircle(sketch, "E2.42.2.0", {"center": v(92.5, 181) * mm, "radius": 2.5 * mm});
            skCircle(sketch, "E2.42.3.0", {"center": v(92.5, 173) * mm, "radius": 2.5 * mm});
            skCircle(sketch, "E2.42.4.0", {"center": v(92.5, 165) * mm, "radius": 2.5 * mm});
            skCircle(sketch, "E2.42.5.0", {"center": v(92.5, 157) * mm, "radius": 2.5 * mm});
            skCircle(sketch, "E2.42.6.0", {"center": v(92.5, 149) * mm, "radius": 2.5 * mm});
            skCircle(sketch, "E2.42.7.0", {"center": v(92.5, 141) * mm, "radius": 2.5 * mm});
            skCircle(sketch, "E2.42.8.0", {"center": v(92.5, 133) * mm, "radius": 2.5 * mm});
            skCircle(sketch, "E2.42.9.0", {"center": v(92.5, 125) * mm, "radius": 2.5 * mm});
            skCircle(sketch, "E2.42.10.0", {"center": v(92.5, 117) * mm, "radius": 2.5 * mm});
            skCircle(sketch, "E2.42.11.0", {"center": v(92.5, 109) * mm, "radius": 2.5 * mm});
            skCircle(sketch, "E2.42.12.0", {"center": v(92.5, 101) * mm, "radius": 2.5 * mm});
            skCircle(sketch, "E2.42.13.0", {"center": v(92.5, 93) * mm, "radius": 2.5 * mm});
            skCircle(sketch, "E2.42.14.0", {"center": v(92.5, 85) * mm, "radius": 2.5 * mm});
            skCircle(sketch, "E2.42.15.0", {"center": v(92.5, 77) * mm, "radius": 2.5 * mm});
            skCircle(sketch, "E2.42.16.0", {"center": v(92.5, 69) * mm, "radius": 2.5 * mm});
            skCircle(sketch, "E2.42.17.0", {"center": v(92.5, 61) * mm, "radius": 2.5 * mm});
            skCircle(sketch, "E2.42.18.0", {"center": v(92.5, 53) * mm, "radius": 2.5 * mm});
            skCircle(sketch, "E2.42.19.0", {"center": v(92.5, 45) * mm, "radius": 2.5 * mm});
            skCircle(sketch, "E2.42.20.0", {"center": v(92.5, 37) * mm, "radius": 2.5 * mm});
            skCircle(sketch, "E2.42.21.0", {"center": v(92.5, 29) * mm, "radius": 2.5 * mm});
            skCircle(sketch, "E2.42.22.0", {"center": v(92.5, 21) * mm, "radius": 2.5 * mm});
            skCircle(sketch, "E2.42.23.0", {"center": v(92.5, 13) * mm, "radius": 2.5 * mm});
            skCircle(sketch, "E2.42.24.0", {"center": v(92.5, 5) * mm, "radius": 2.5 * mm});
            skCircle(sketch, "E2.42.25.0", {"center": v(92.5, -3) * mm, "radius": 2.5 * mm});
            skCircle(sketch, "E2.42.26.0", {"center": v(92.5, -11) * mm, "radius": 2.5 * mm});
            skCircle(sketch, "E2.42.27.0", {"center": v(92.5, -19) * mm, "radius": 2.5 * mm});
            skCircle(sketch, "E2.42.28.0", {"center": v(92.5, -27) * mm, "radius": 2.5 * mm});
            skCircle(sketch, "E2.42.29.0", {"center": v(92.5, -35) * mm, "radius": 2.5 * mm});
            skCircle(sketch, "E2.42.30.0", {"center": v(92.5, -43) * mm, "radius": 2.5 * mm});
            skCircle(sketch, "E2.42.31.0", {"center": v(92.5, -51) * mm, "radius": 2.5 * mm});
            skCircle(sketch, "E2.42.32.0", {"center": v(92.5, -59) * mm, "radius": 2.5 * mm});
            skCircle(sketch, "E2.42.33.0", {"center": v(92.5, -67) * mm, "radius": 2.5 * mm});
            skCircle(sketch, "E2.42.34.0", {"center": v(92.5, -75) * mm, "radius": 2.5 * mm});
            skCircle(sketch, "E2.42.35.0", {"center": v(92.5, -83) * mm, "radius": 2.5 * mm});
            skCircle(sketch, "E2.42.36.0", {"center": v(92.5, -91) * mm, "radius": 2.5 * mm});
            skCircle(sketch, "E2.42.37.0", {"center": v(92.5, -99) * mm, "radius": 2.5 * mm});
            skCircle(sketch, "E2.42.38.0", {"center": v(92.5, -107) * mm, "radius": 2.5 * mm});
            skCircle(sketch, "E2.42.39.0", {"center": v(92.5, -115) * mm, "radius": 2.5 * mm});
            skCircle(sketch, "E2.42.40.0", {"center": v(92.5, -123) * mm, "radius": 2.5 * mm});
            skCircle(sketch, "E2.42.41.0", {"center": v(92.5, -131) * mm, "radius": 2.5 * mm});
            skCircle(sketch, "E2.42.42.0", {"center": v(92.5, -139) * mm, "radius": 2.5 * mm});
            skCircle(sketch, "E2.42.43.0", {"center": v(92.5, -147) * mm, "radius": 2.5 * mm});
            skCircle(sketch, "E2.42.44.0", {"center": v(92.5, -155) * mm, "radius": 2.5 * mm});
            skCircle(sketch, "E2.42.45.0", {"center": v(92.5, -163) * mm, "radius": 2.5 * mm});
            skCircle(sketch, "E2.42.46.0", {"center": v(92.5, -171) * mm, "radius": 2.5 * mm});
            skCircle(sketch, "E2.42.47.0", {"center": v(92.5, -179) * mm, "radius": 2.5 * mm});
            skCircle(sketch, "E2.42.48.0", {"center": v(92.5, -187) * mm, "radius": 2.5 * mm});
            skCircle(sketch, "E2.42.49.0", {"center": v(92.5, -195) * mm, "radius": 2.5 * mm});
            skCircle(sketch, "E2.43.0.0", {"center": v(100.5, 197) * mm, "radius": 2.5 * mm});
            skCircle(sketch, "E2.43.1.0", {"center": v(100.5, 189) * mm, "radius": 2.5 * mm});
            skCircle(sketch, "E2.43.2.0", {"center": v(100.5, 181) * mm, "radius": 2.5 * mm});
            skCircle(sketch, "E2.43.3.0", {"center": v(100.5, 173) * mm, "radius": 2.5 * mm});
            skCircle(sketch, "E2.43.4.0", {"center": v(100.5, 165) * mm, "radius": 2.5 * mm});
            skCircle(sketch, "E2.43.5.0", {"center": v(100.5, 157) * mm, "radius": 2.5 * mm});
            skCircle(sketch, "E2.43.6.0", {"center": v(100.5, 149) * mm, "radius": 2.5 * mm});
            skCircle(sketch, "E2.43.7.0", {"center": v(100.5, 141) * mm, "radius": 2.5 * mm});
            skCircle(sketch, "E2.43.8.0", {"center": v(100.5, 133) * mm, "radius": 2.5 * mm});
            skCircle(sketch, "E2.43.9.0", {"center": v(100.5, 125) * mm, "radius": 2.5 * mm});
            skCircle(sketch, "E2.43.10.0", {"center": v(100.5, 117) * mm, "radius": 2.5 * mm});
            skCircle(sketch, "E2.43.11.0", {"center": v(100.5, 109) * mm, "radius": 2.5 * mm});
            skCircle(sketch, "E2.43.12.0", {"center": v(100.5, 101) * mm, "radius": 2.5 * mm});
            skCircle(sketch, "E2.43.13.0", {"center": v(100.5, 93) * mm, "radius": 2.5 * mm});
            skCircle(sketch, "E2.43.14.0", {"center": v(100.5, 85) * mm, "radius": 2.5 * mm});
            skCircle(sketch, "E2.43.15.0", {"center": v(100.5, 77) * mm, "radius": 2.5 * mm});
            skCircle(sketch, "E2.43.16.0", {"center": v(100.5, 69) * mm, "radius": 2.5 * mm});
            skCircle(sketch, "E2.43.17.0", {"center": v(100.5, 61) * mm, "radius": 2.5 * mm});
            skCircle(sketch, "E2.43.18.0", {"center": v(100.5, 53) * mm, "radius": 2.5 * mm});
            skCircle(sketch, "E2.43.19.0", {"center": v(100.5, 45) * mm, "radius": 2.5 * mm});
            skCircle(sketch, "E2.43.20.0", {"center": v(100.5, 37) * mm, "radius": 2.5 * mm});
            skCircle(sketch, "E2.43.21.0", {"center": v(100.5, 29) * mm, "radius": 2.5 * mm});
            skCircle(sketch, "E2.43.22.0", {"center": v(100.5, 21) * mm, "radius": 2.5 * mm});
            skCircle(sketch, "E2.43.23.0", {"center": v(100.5, 13) * mm, "radius": 2.5 * mm});
            skCircle(sketch, "E2.43.24.0", {"center": v(100.5, 5) * mm, "radius": 2.5 * mm});
            skCircle(sketch, "E2.43.25.0", {"center": v(100.5, -3) * mm, "radius": 2.5 * mm});
            skCircle(sketch, "E2.43.26.0", {"center": v(100.5, -11) * mm, "radius": 2.5 * mm});
            skCircle(sketch, "E2.43.27.0", {"center": v(100.5, -19) * mm, "radius": 2.5 * mm});
            skCircle(sketch, "E2.43.28.0", {"center": v(100.5, -27) * mm, "radius": 2.5 * mm});
            skCircle(sketch, "E2.43.29.0", {"center": v(100.5, -35) * mm, "radius": 2.5 * mm});
            skCircle(sketch, "E2.43.30.0", {"center": v(100.5, -43) * mm, "radius": 2.5 * mm});
            skCircle(sketch, "E2.43.31.0", {"center": v(100.5, -51) * mm, "radius": 2.5 * mm});
            skCircle(sketch, "E2.43.32.0", {"center": v(100.5, -59) * mm, "radius": 2.5 * mm});
            skCircle(sketch, "E2.43.33.0", {"center": v(100.5, -67) * mm, "radius": 2.5 * mm});
            skCircle(sketch, "E2.43.34.0", {"center": v(100.5, -75) * mm, "radius": 2.5 * mm});
            skCircle(sketch, "E2.43.35.0", {"center": v(100.5, -83) * mm, "radius": 2.5 * mm});
            skCircle(sketch, "E2.43.36.0", {"center": v(100.5, -91) * mm, "radius": 2.5 * mm});
            skCircle(sketch, "E2.43.37.0", {"center": v(100.5, -99) * mm, "radius": 2.5 * mm});
            skCircle(sketch, "E2.43.38.0", {"center": v(100.5, -107) * mm, "radius": 2.5 * mm});
            skCircle(sketch, "E2.43.39.0", {"center": v(100.5, -115) * mm, "radius": 2.5 * mm});
            skCircle(sketch, "E2.43.40.0", {"center": v(100.5, -123) * mm, "radius": 2.5 * mm});
            skCircle(sketch, "E2.43.41.0", {"center": v(100.5, -131) * mm, "radius": 2.5 * mm});
            skCircle(sketch, "E2.43.42.0", {"center": v(100.5, -139) * mm, "radius": 2.5 * mm});
            skCircle(sketch, "E2.43.43.0", {"center": v(100.5, -147) * mm, "radius": 2.5 * mm});
            skCircle(sketch, "E2.43.44.0", {"center": v(100.5, -155) * mm, "radius": 2.5 * mm});
            skCircle(sketch, "E2.43.45.0", {"center": v(100.5, -163) * mm, "radius": 2.5 * mm});
            skCircle(sketch, "E2.43.46.0", {"center": v(100.5, -171) * mm, "radius": 2.5 * mm});
            skCircle(sketch, "E2.43.47.0", {"center": v(100.5, -179) * mm, "radius": 2.5 * mm});
            skCircle(sketch, "E2.43.48.0", {"center": v(100.5, -187) * mm, "radius": 2.5 * mm});
            skCircle(sketch, "E2.43.49.0", {"center": v(100.5, -195) * mm, "radius": 2.5 * mm});
            skCircle(sketch, "E2.44.0.0", {"center": v(108.5, 197) * mm, "radius": 2.5 * mm});
            skCircle(sketch, "E2.44.1.0", {"center": v(108.5, 189) * mm, "radius": 2.5 * mm});
            skCircle(sketch, "E2.44.2.0", {"center": v(108.5, 181) * mm, "radius": 2.5 * mm});
            skCircle(sketch, "E2.44.3.0", {"center": v(108.5, 173) * mm, "radius": 2.5 * mm});
            skCircle(sketch, "E2.44.4.0", {"center": v(108.5, 165) * mm, "radius": 2.5 * mm});
            skCircle(sketch, "E2.44.5.0", {"center": v(108.5, 157) * mm, "radius": 2.5 * mm});
            skCircle(sketch, "E2.44.6.0", {"center": v(108.5, 149) * mm, "radius": 2.5 * mm});
            skCircle(sketch, "E2.44.7.0", {"center": v(108.5, 141) * mm, "radius": 2.5 * mm});
            skCircle(sketch, "E2.44.8.0", {"center": v(108.5, 133) * mm, "radius": 2.5 * mm});
            skCircle(sketch, "E2.44.9.0", {"center": v(108.5, 125) * mm, "radius": 2.5 * mm});
            skCircle(sketch, "E2.44.10.0", {"center": v(108.5, 117) * mm, "radius": 2.5 * mm});
            skCircle(sketch, "E2.44.11.0", {"center": v(108.5, 109) * mm, "radius": 2.5 * mm});
            skCircle(sketch, "E2.44.12.0", {"center": v(108.5, 101) * mm, "radius": 2.5 * mm});
            skCircle(sketch, "E2.44.13.0", {"center": v(108.5, 93) * mm, "radius": 2.5 * mm});
            skCircle(sketch, "E2.44.14.0", {"center": v(108.5, 85) * mm, "radius": 2.5 * mm});
            skCircle(sketch, "E2.44.15.0", {"center": v(108.5, 77) * mm, "radius": 2.5 * mm});
            skCircle(sketch, "E2.44.16.0", {"center": v(108.5, 69) * mm, "radius": 2.5 * mm});
            skCircle(sketch, "E2.44.17.0", {"center": v(108.5, 61) * mm, "radius": 2.5 * mm});
            skCircle(sketch, "E2.44.18.0", {"center": v(108.5, 53) * mm, "radius": 2.5 * mm});
            skCircle(sketch, "E2.44.19.0", {"center": v(108.5, 45) * mm, "radius": 2.5 * mm});
            skCircle(sketch, "E2.44.20.0", {"center": v(108.5, 37) * mm, "radius": 2.5 * mm});
            skCircle(sketch, "E2.44.21.0", {"center": v(108.5, 29) * mm, "radius": 2.5 * mm});
            skCircle(sketch, "E2.44.22.0", {"center": v(108.5, 21) * mm, "radius": 2.5 * mm});
            skCircle(sketch, "E2.44.23.0", {"center": v(108.5, 13) * mm, "radius": 2.5 * mm});
            skCircle(sketch, "E2.44.24.0", {"center": v(108.5, 5) * mm, "radius": 2.5 * mm});
            skCircle(sketch, "E2.44.25.0", {"center": v(108.5, -3) * mm, "radius": 2.5 * mm});
            skCircle(sketch, "E2.44.26.0", {"center": v(108.5, -11) * mm, "radius": 2.5 * mm});
            skCircle(sketch, "E2.44.27.0", {"center": v(108.5, -19) * mm, "radius": 2.5 * mm});
            skCircle(sketch, "E2.44.28.0", {"center": v(108.5, -27) * mm, "radius": 2.5 * mm});
            skCircle(sketch, "E2.44.29.0", {"center": v(108.5, -35) * mm, "radius": 2.5 * mm});
            skCircle(sketch, "E2.44.30.0", {"center": v(108.5, -43) * mm, "radius": 2.5 * mm});
            skCircle(sketch, "E2.44.31.0", {"center": v(108.5, -51) * mm, "radius": 2.5 * mm});
            skCircle(sketch, "E2.44.32.0", {"center": v(108.5, -59) * mm, "radius": 2.5 * mm});
            skCircle(sketch, "E2.44.33.0", {"center": v(108.5, -67) * mm, "radius": 2.5 * mm});
            skCircle(sketch, "E2.44.34.0", {"center": v(108.5, -75) * mm, "radius": 2.5 * mm});
            skCircle(sketch, "E2.44.35.0", {"center": v(108.5, -83) * mm, "radius": 2.5 * mm});
            skCircle(sketch, "E2.44.36.0", {"center": v(108.5, -91) * mm, "radius": 2.5 * mm});
            skCircle(sketch, "E2.44.37.0", {"center": v(108.5, -99) * mm, "radius": 2.5 * mm});
            skCircle(sketch, "E2.44.38.0", {"center": v(108.5, -107) * mm, "radius": 2.5 * mm});
            skCircle(sketch, "E2.44.39.0", {"center": v(108.5, -115) * mm, "radius": 2.5 * mm});
            skCircle(sketch, "E2.44.40.0", {"center": v(108.5, -123) * mm, "radius": 2.5 * mm});
            skCircle(sketch, "E2.44.41.0", {"center": v(108.5, -131) * mm, "radius": 2.5 * mm});
            skCircle(sketch, "E2.44.42.0", {"center": v(108.5, -139) * mm, "radius": 2.5 * mm});
            skCircle(sketch, "E2.44.43.0", {"center": v(108.5, -147) * mm, "radius": 2.5 * mm});
            skCircle(sketch, "E2.44.44.0", {"center": v(108.5, -155) * mm, "radius": 2.5 * mm});
            skCircle(sketch, "E2.44.45.0", {"center": v(108.5, -163) * mm, "radius": 2.5 * mm});
            skCircle(sketch, "E2.44.46.0", {"center": v(108.5, -171) * mm, "radius": 2.5 * mm});
            skCircle(sketch, "E2.44.47.0", {"center": v(108.5, -179) * mm, "radius": 2.5 * mm});
            skCircle(sketch, "E2.44.48.0", {"center": v(108.5, -187) * mm, "radius": 2.5 * mm});
            skCircle(sketch, "E2.44.49.0", {"center": v(108.5, -195) * mm, "radius": 2.5 * mm});
            skCircle(sketch, "E2.45.0.0", {"center": v(116.5, 197) * mm, "radius": 2.5 * mm});
            skCircle(sketch, "E2.45.1.0", {"center": v(116.5, 189) * mm, "radius": 2.5 * mm});
            skCircle(sketch, "E2.45.2.0", {"center": v(116.5, 181) * mm, "radius": 2.5 * mm});
            skCircle(sketch, "E2.45.3.0", {"center": v(116.5, 173) * mm, "radius": 2.5 * mm});
            skCircle(sketch, "E2.45.4.0", {"center": v(116.5, 165) * mm, "radius": 2.5 * mm});
            skCircle(sketch, "E2.45.5.0", {"center": v(116.5, 157) * mm, "radius": 2.5 * mm});
            skCircle(sketch, "E2.45.6.0", {"center": v(116.5, 149) * mm, "radius": 2.5 * mm});
            skCircle(sketch, "E2.45.7.0", {"center": v(116.5, 141) * mm, "radius": 2.5 * mm});
            skCircle(sketch, "E2.45.8.0", {"center": v(116.5, 133) * mm, "radius": 2.5 * mm});
            skCircle(sketch, "E2.45.9.0", {"center": v(116.5, 125) * mm, "radius": 2.5 * mm});
            skCircle(sketch, "E2.45.10.0", {"center": v(116.5, 117) * mm, "radius": 2.5 * mm});
            skCircle(sketch, "E2.45.11.0", {"center": v(116.5, 109) * mm, "radius": 2.5 * mm});
            skCircle(sketch, "E2.45.12.0", {"center": v(116.5, 101) * mm, "radius": 2.5 * mm});
            skCircle(sketch, "E2.45.13.0", {"center": v(116.5, 93) * mm, "radius": 2.5 * mm});
            skCircle(sketch, "E2.45.14.0", {"center": v(116.5, 85) * mm, "radius": 2.5 * mm});
            skCircle(sketch, "E2.45.15.0", {"center": v(116.5, 77) * mm, "radius": 2.5 * mm});
            skCircle(sketch, "E2.45.16.0", {"center": v(116.5, 69) * mm, "radius": 2.5 * mm});
            skCircle(sketch, "E2.45.17.0", {"center": v(116.5, 61) * mm, "radius": 2.5 * mm});
            skCircle(sketch, "E2.45.18.0", {"center": v(116.5, 53) * mm, "radius": 2.5 * mm});
            skCircle(sketch, "E2.45.19.0", {"center": v(116.5, 45) * mm, "radius": 2.5 * mm});
            skCircle(sketch, "E2.45.20.0", {"center": v(116.5, 37) * mm, "radius": 2.5 * mm});
            skCircle(sketch, "E2.45.21.0", {"center": v(116.5, 29) * mm, "radius": 2.5 * mm});
            skCircle(sketch, "E2.45.22.0", {"center": v(116.5, 21) * mm, "radius": 2.5 * mm});
            skCircle(sketch, "E2.45.23.0", {"center": v(116.5, 13) * mm, "radius": 2.5 * mm});
            skCircle(sketch, "E2.45.24.0", {"center": v(116.5, 5) * mm, "radius": 2.5 * mm});
            skCircle(sketch, "E2.45.25.0", {"center": v(116.5, -3) * mm, "radius": 2.5 * mm});
            skCircle(sketch, "E2.45.26.0", {"center": v(116.5, -11) * mm, "radius": 2.5 * mm});
            skCircle(sketch, "E2.45.27.0", {"center": v(116.5, -19) * mm, "radius": 2.5 * mm});
            skCircle(sketch, "E2.45.28.0", {"center": v(116.5, -27) * mm, "radius": 2.5 * mm});
            skCircle(sketch, "E2.45.29.0", {"center": v(116.5, -35) * mm, "radius": 2.5 * mm});
            skCircle(sketch, "E2.45.30.0", {"center": v(116.5, -43) * mm, "radius": 2.5 * mm});
            skCircle(sketch, "E2.45.31.0", {"center": v(116.5, -51) * mm, "radius": 2.5 * mm});
            skCircle(sketch, "E2.45.32.0", {"center": v(116.5, -59) * mm, "radius": 2.5 * mm});
            skCircle(sketch, "E2.45.33.0", {"center": v(116.5, -67) * mm, "radius": 2.5 * mm});
            skCircle(sketch, "E2.45.34.0", {"center": v(116.5, -75) * mm, "radius": 2.5 * mm});
            skCircle(sketch, "E2.45.35.0", {"center": v(116.5, -83) * mm, "radius": 2.5 * mm});
            skCircle(sketch, "E2.45.36.0", {"center": v(116.5, -91) * mm, "radius": 2.5 * mm});
            skCircle(sketch, "E2.45.37.0", {"center": v(116.5, -99) * mm, "radius": 2.5 * mm});
            skCircle(sketch, "E2.45.38.0", {"center": v(116.5, -107) * mm, "radius": 2.5 * mm});
            skCircle(sketch, "E2.45.39.0", {"center": v(116.5, -115) * mm, "radius": 2.5 * mm});
            skCircle(sketch, "E2.45.40.0", {"center": v(116.5, -123) * mm, "radius": 2.5 * mm});
            skCircle(sketch, "E2.45.41.0", {"center": v(116.5, -131) * mm, "radius": 2.5 * mm});
            skCircle(sketch, "E2.45.42.0", {"center": v(116.5, -139) * mm, "radius": 2.5 * mm});
            skCircle(sketch, "E2.45.43.0", {"center": v(116.5, -147) * mm, "radius": 2.5 * mm});
            skCircle(sketch, "E2.45.44.0", {"center": v(116.5, -155) * mm, "radius": 2.5 * mm});
            skCircle(sketch, "E2.45.45.0", {"center": v(116.5, -163) * mm, "radius": 2.5 * mm});
            skCircle(sketch, "E2.45.46.0", {"center": v(116.5, -171) * mm, "radius": 2.5 * mm});
            skCircle(sketch, "E2.45.47.0", {"center": v(116.5, -179) * mm, "radius": 2.5 * mm});
            skCircle(sketch, "E2.45.48.0", {"center": v(116.5, -187) * mm, "radius": 2.5 * mm});
            skCircle(sketch, "E2.45.49.0", {"center": v(116.5, -195) * mm, "radius": 2.5 * mm});
            skCircle(sketch, "E2.46.0.0", {"center": v(124.5, 197) * mm, "radius": 2.5 * mm});
            skCircle(sketch, "E2.46.1.0", {"center": v(124.5, 189) * mm, "radius": 2.5 * mm});
            skCircle(sketch, "E2.46.2.0", {"center": v(124.5, 181) * mm, "radius": 2.5 * mm});
            skCircle(sketch, "E2.46.3.0", {"center": v(124.5, 173) * mm, "radius": 2.5 * mm});
            skCircle(sketch, "E2.46.4.0", {"center": v(124.5, 165) * mm, "radius": 2.5 * mm});
            skCircle(sketch, "E2.46.5.0", {"center": v(124.5, 157) * mm, "radius": 2.5 * mm});
            skCircle(sketch, "E2.46.6.0", {"center": v(124.5, 149) * mm, "radius": 2.5 * mm});
            skCircle(sketch, "E2.46.7.0", {"center": v(124.5, 141) * mm, "radius": 2.5 * mm});
            skCircle(sketch, "E2.46.8.0", {"center": v(124.5, 133) * mm, "radius": 2.5 * mm});
            skCircle(sketch, "E2.46.9.0", {"center": v(124.5, 125) * mm, "radius": 2.5 * mm});
            skCircle(sketch, "E2.46.10.0", {"center": v(124.5, 117) * mm, "radius": 2.5 * mm});
            skCircle(sketch, "E2.46.11.0", {"center": v(124.5, 109) * mm, "radius": 2.5 * mm});
            skCircle(sketch, "E2.46.12.0", {"center": v(124.5, 101) * mm, "radius": 2.5 * mm});
            skCircle(sketch, "E2.46.13.0", {"center": v(124.5, 93) * mm, "radius": 2.5 * mm});
            skCircle(sketch, "E2.46.14.0", {"center": v(124.5, 85) * mm, "radius": 2.5 * mm});
            skCircle(sketch, "E2.46.15.0", {"center": v(124.5, 77) * mm, "radius": 2.5 * mm});
            skCircle(sketch, "E2.46.16.0", {"center": v(124.5, 69) * mm, "radius": 2.5 * mm});
            skCircle(sketch, "E2.46.17.0", {"center": v(124.5, 61) * mm, "radius": 2.5 * mm});
            skCircle(sketch, "E2.46.18.0", {"center": v(124.5, 53) * mm, "radius": 2.5 * mm});
            skCircle(sketch, "E2.46.19.0", {"center": v(124.5, 45) * mm, "radius": 2.5 * mm});
            skCircle(sketch, "E2.46.20.0", {"center": v(124.5, 37) * mm, "radius": 2.5 * mm});
            skCircle(sketch, "E2.46.21.0", {"center": v(124.5, 29) * mm, "radius": 2.5 * mm});
            skCircle(sketch, "E2.46.22.0", {"center": v(124.5, 21) * mm, "radius": 2.5 * mm});
            skCircle(sketch, "E2.46.23.0", {"center": v(124.5, 13) * mm, "radius": 2.5 * mm});
            skCircle(sketch, "E2.46.24.0", {"center": v(124.5, 5) * mm, "radius": 2.5 * mm});
            skCircle(sketch, "E2.46.25.0", {"center": v(124.5, -3) * mm, "radius": 2.5 * mm});
            skCircle(sketch, "E2.46.26.0", {"center": v(124.5, -11) * mm, "radius": 2.5 * mm});
            skCircle(sketch, "E2.46.27.0", {"center": v(124.5, -19) * mm, "radius": 2.5 * mm});
            skCircle(sketch, "E2.46.28.0", {"center": v(124.5, -27) * mm, "radius": 2.5 * mm});
            skCircle(sketch, "E2.46.29.0", {"center": v(124.5, -35) * mm, "radius": 2.5 * mm});
            skCircle(sketch, "E2.46.30.0", {"center": v(124.5, -43) * mm, "radius": 2.5 * mm});
            skCircle(sketch, "E2.46.31.0", {"center": v(124.5, -51) * mm, "radius": 2.5 * mm});
            skCircle(sketch, "E2.46.32.0", {"center": v(124.5, -59) * mm, "radius": 2.5 * mm});
            skCircle(sketch, "E2.46.33.0", {"center": v(124.5, -67) * mm, "radius": 2.5 * mm});
            skCircle(sketch, "E2.46.34.0", {"center": v(124.5, -75) * mm, "radius": 2.5 * mm});
            skCircle(sketch, "E2.46.35.0", {"center": v(124.5, -83) * mm, "radius": 2.5 * mm});
            skCircle(sketch, "E2.46.36.0", {"center": v(124.5, -91) * mm, "radius": 2.5 * mm});
            skCircle(sketch, "E2.46.37.0", {"center": v(124.5, -99) * mm, "radius": 2.5 * mm});
            skCircle(sketch, "E2.46.38.0", {"center": v(124.5, -107) * mm, "radius": 2.5 * mm});
            skCircle(sketch, "E2.46.39.0", {"center": v(124.5, -115) * mm, "radius": 2.5 * mm});
            skCircle(sketch, "E2.46.40.0", {"center": v(124.5, -123) * mm, "radius": 2.5 * mm});
            skCircle(sketch, "E2.46.41.0", {"center": v(124.5, -131) * mm, "radius": 2.5 * mm});
            skCircle(sketch, "E2.46.42.0", {"center": v(124.5, -139) * mm, "radius": 2.5 * mm});
            skCircle(sketch, "E2.46.43.0", {"center": v(124.5, -147) * mm, "radius": 2.5 * mm});
            skCircle(sketch, "E2.46.44.0", {"center": v(124.5, -155) * mm, "radius": 2.5 * mm});
            skCircle(sketch, "E2.46.45.0", {"center": v(124.5, -163) * mm, "radius": 2.5 * mm});
            skCircle(sketch, "E2.46.46.0", {"center": v(124.5, -171) * mm, "radius": 2.5 * mm});
            skCircle(sketch, "E2.46.47.0", {"center": v(124.5, -179) * mm, "radius": 2.5 * mm});
            skCircle(sketch, "E2.46.48.0", {"center": v(124.5, -187) * mm, "radius": 2.5 * mm});
            skCircle(sketch, "E2.46.49.0", {"center": v(124.5, -195) * mm, "radius": 2.5 * mm});
            skCircle(sketch, "E2.47.0.0", {"center": v(132.5, 197) * mm, "radius": 2.5 * mm});
            skCircle(sketch, "E2.47.1.0", {"center": v(132.5, 189) * mm, "radius": 2.5 * mm});
            skCircle(sketch, "E2.47.2.0", {"center": v(132.5, 181) * mm, "radius": 2.5 * mm});
            skCircle(sketch, "E2.47.3.0", {"center": v(132.5, 173) * mm, "radius": 2.5 * mm});
            skCircle(sketch, "E2.47.4.0", {"center": v(132.5, 165) * mm, "radius": 2.5 * mm});
            skCircle(sketch, "E2.47.5.0", {"center": v(132.5, 157) * mm, "radius": 2.5 * mm});
            skCircle(sketch, "E2.47.6.0", {"center": v(132.5, 149) * mm, "radius": 2.5 * mm});
            skCircle(sketch, "E2.47.7.0", {"center": v(132.5, 141) * mm, "radius": 2.5 * mm});
            skCircle(sketch, "E2.47.8.0", {"center": v(132.5, 133) * mm, "radius": 2.5 * mm});
            skCircle(sketch, "E2.47.9.0", {"center": v(132.5, 125) * mm, "radius": 2.5 * mm});
            skCircle(sketch, "E2.47.10.0", {"center": v(132.5, 117) * mm, "radius": 2.5 * mm});
            skCircle(sketch, "E2.47.11.0", {"center": v(132.5, 109) * mm, "radius": 2.5 * mm});
            skCircle(sketch, "E2.47.12.0", {"center": v(132.5, 101) * mm, "radius": 2.5 * mm});
            skCircle(sketch, "E2.47.13.0", {"center": v(132.5, 93) * mm, "radius": 2.5 * mm});
            skCircle(sketch, "E2.47.14.0", {"center": v(132.5, 85) * mm, "radius": 2.5 * mm});
            skCircle(sketch, "E2.47.15.0", {"center": v(132.5, 77) * mm, "radius": 2.5 * mm});
            skCircle(sketch, "E2.47.16.0", {"center": v(132.5, 69) * mm, "radius": 2.5 * mm});
            skCircle(sketch, "E2.47.17.0", {"center": v(132.5, 61) * mm, "radius": 2.5 * mm});
            skCircle(sketch, "E2.47.18.0", {"center": v(132.5, 53) * mm, "radius": 2.5 * mm});
            skCircle(sketch, "E2.47.19.0", {"center": v(132.5, 45) * mm, "radius": 2.5 * mm});
            skCircle(sketch, "E2.47.20.0", {"center": v(132.5, 37) * mm, "radius": 2.5 * mm});
            skCircle(sketch, "E2.47.21.0", {"center": v(132.5, 29) * mm, "radius": 2.5 * mm});
            skCircle(sketch, "E2.47.22.0", {"center": v(132.5, 21) * mm, "radius": 2.5 * mm});
            skCircle(sketch, "E2.47.23.0", {"center": v(132.5, 13) * mm, "radius": 2.5 * mm});
            skCircle(sketch, "E2.47.24.0", {"center": v(132.5, 5) * mm, "radius": 2.5 * mm});
            skCircle(sketch, "E2.47.25.0", {"center": v(132.5, -3) * mm, "radius": 2.5 * mm});
            skCircle(sketch, "E2.47.26.0", {"center": v(132.5, -11) * mm, "radius": 2.5 * mm});
            skCircle(sketch, "E2.47.27.0", {"center": v(132.5, -19) * mm, "radius": 2.5 * mm});
            skCircle(sketch, "E2.47.28.0", {"center": v(132.5, -27) * mm, "radius": 2.5 * mm});
            skCircle(sketch, "E2.47.29.0", {"center": v(132.5, -35) * mm, "radius": 2.5 * mm});
            skCircle(sketch, "E2.47.30.0", {"center": v(132.5, -43) * mm, "radius": 2.5 * mm});
            skCircle(sketch, "E2.47.31.0", {"center": v(132.5, -51) * mm, "radius": 2.5 * mm});
            skCircle(sketch, "E2.47.32.0", {"center": v(132.5, -59) * mm, "radius": 2.5 * mm});
            skCircle(sketch, "E2.47.33.0", {"center": v(132.5, -67) * mm, "radius": 2.5 * mm});
            skCircle(sketch, "E2.47.34.0", {"center": v(132.5, -75) * mm, "radius": 2.5 * mm});
            skCircle(sketch, "E2.47.35.0", {"center": v(132.5, -83) * mm, "radius": 2.5 * mm});
            skCircle(sketch, "E2.47.36.0", {"center": v(132.5, -91) * mm, "radius": 2.5 * mm});
            skCircle(sketch, "E2.47.37.0", {"center": v(132.5, -99) * mm, "radius": 2.5 * mm});
            skCircle(sketch, "E2.47.38.0", {"center": v(132.5, -107) * mm, "radius": 2.5 * mm});
            skCircle(sketch, "E2.47.39.0", {"center": v(132.5, -115) * mm, "radius": 2.5 * mm});
            skCircle(sketch, "E2.47.40.0", {"center": v(132.5, -123) * mm, "radius": 2.5 * mm});
            skCircle(sketch, "E2.47.41.0", {"center": v(132.5, -131) * mm, "radius": 2.5 * mm});
            skCircle(sketch, "E2.47.42.0", {"center": v(132.5, -139) * mm, "radius": 2.5 * mm});
            skCircle(sketch, "E2.47.43.0", {"center": v(132.5, -147) * mm, "radius": 2.5 * mm});
            skCircle(sketch, "E2.47.44.0", {"center": v(132.5, -155) * mm, "radius": 2.5 * mm});
            skCircle(sketch, "E2.47.45.0", {"center": v(132.5, -163) * mm, "radius": 2.5 * mm});
            skCircle(sketch, "E2.47.46.0", {"center": v(132.5, -171) * mm, "radius": 2.5 * mm});
            skCircle(sketch, "E2.47.47.0", {"center": v(132.5, -179) * mm, "radius": 2.5 * mm});
            skCircle(sketch, "E2.47.48.0", {"center": v(132.5, -187) * mm, "radius": 2.5 * mm});
            skCircle(sketch, "E2.47.49.0", {"center": v(132.5, -195) * mm, "radius": 2.5 * mm});
            skCircle(sketch, "E2.48.0.0", {"center": v(140.5, 197) * mm, "radius": 2.5 * mm});
            skCircle(sketch, "E2.48.1.0", {"center": v(140.5, 189) * mm, "radius": 2.5 * mm});
            skCircle(sketch, "E2.48.2.0", {"center": v(140.5, 181) * mm, "radius": 2.5 * mm});
            skCircle(sketch, "E2.48.3.0", {"center": v(140.5, 173) * mm, "radius": 2.5 * mm});
            skCircle(sketch, "E2.48.4.0", {"center": v(140.5, 165) * mm, "radius": 2.5 * mm});
            skCircle(sketch, "E2.48.5.0", {"center": v(140.5, 157) * mm, "radius": 2.5 * mm});
            skCircle(sketch, "E2.48.6.0", {"center": v(140.5, 149) * mm, "radius": 2.5 * mm});
            skCircle(sketch, "E2.48.7.0", {"center": v(140.5, 141) * mm, "radius": 2.5 * mm});
            skCircle(sketch, "E2.48.8.0", {"center": v(140.5, 133) * mm, "radius": 2.5 * mm});
            skCircle(sketch, "E2.48.9.0", {"center": v(140.5, 125) * mm, "radius": 2.5 * mm});
            skCircle(sketch, "E2.48.10.0", {"center": v(140.5, 117) * mm, "radius": 2.5 * mm});
            skCircle(sketch, "E2.48.11.0", {"center": v(140.5, 109) * mm, "radius": 2.5 * mm});
            skCircle(sketch, "E2.48.12.0", {"center": v(140.5, 101) * mm, "radius": 2.5 * mm});
            skCircle(sketch, "E2.48.13.0", {"center": v(140.5, 93) * mm, "radius": 2.5 * mm});
            skCircle(sketch, "E2.48.14.0", {"center": v(140.5, 85) * mm, "radius": 2.5 * mm});
            skCircle(sketch, "E2.48.15.0", {"center": v(140.5, 77) * mm, "radius": 2.5 * mm});
            skCircle(sketch, "E2.48.16.0", {"center": v(140.5, 69) * mm, "radius": 2.5 * mm});
            skCircle(sketch, "E2.48.17.0", {"center": v(140.5, 61) * mm, "radius": 2.5 * mm});
            skCircle(sketch, "E2.48.18.0", {"center": v(140.5, 53) * mm, "radius": 2.5 * mm});
            skCircle(sketch, "E2.48.19.0", {"center": v(140.5, 45) * mm, "radius": 2.5 * mm});
            skCircle(sketch, "E2.48.20.0", {"center": v(140.5, 37) * mm, "radius": 2.5 * mm});
            skCircle(sketch, "E2.48.21.0", {"center": v(140.5, 29) * mm, "radius": 2.5 * mm});
            skCircle(sketch, "E2.48.22.0", {"center": v(140.5, 21) * mm, "radius": 2.5 * mm});
            skCircle(sketch, "E2.48.23.0", {"center": v(140.5, 13) * mm, "radius": 2.5 * mm});
            skCircle(sketch, "E2.48.24.0", {"center": v(140.5, 5) * mm, "radius": 2.5 * mm});
            skCircle(sketch, "E2.48.25.0", {"center": v(140.5, -3) * mm, "radius": 2.5 * mm});
            skCircle(sketch, "E2.48.26.0", {"center": v(140.5, -11) * mm, "radius": 2.5 * mm});
            skCircle(sketch, "E2.48.27.0", {"center": v(140.5, -19) * mm, "radius": 2.5 * mm});
            skCircle(sketch, "E2.48.28.0", {"center": v(140.5, -27) * mm, "radius": 2.5 * mm});
            skCircle(sketch, "E2.48.29.0", {"center": v(140.5, -35) * mm, "radius": 2.5 * mm});
            skCircle(sketch, "E2.48.30.0", {"center": v(140.5, -43) * mm, "radius": 2.5 * mm});
            skCircle(sketch, "E2.48.31.0", {"center": v(140.5, -51) * mm, "radius": 2.5 * mm});
            skCircle(sketch, "E2.48.32.0", {"center": v(140.5, -59) * mm, "radius": 2.5 * mm});
            skCircle(sketch, "E2.48.33.0", {"center": v(140.5, -67) * mm, "radius": 2.5 * mm});
            skCircle(sketch, "E2.48.34.0", {"center": v(140.5, -75) * mm, "radius": 2.5 * mm});
            skCircle(sketch, "E2.48.35.0", {"center": v(140.5, -83) * mm, "radius": 2.5 * mm});
            skCircle(sketch, "E2.48.36.0", {"center": v(140.5, -91) * mm, "radius": 2.5 * mm});
            skCircle(sketch, "E2.48.37.0", {"center": v(140.5, -99) * mm, "radius": 2.5 * mm});
            skCircle(sketch, "E2.48.38.0", {"center": v(140.5, -107) * mm, "radius": 2.5 * mm});
            skCircle(sketch, "E2.48.39.0", {"center": v(140.5, -115) * mm, "radius": 2.5 * mm});
            skCircle(sketch, "E2.48.40.0", {"center": v(140.5, -123) * mm, "radius": 2.5 * mm});
            skCircle(sketch, "E2.48.41.0", {"center": v(140.5, -131) * mm, "radius": 2.5 * mm});
            skCircle(sketch, "E2.48.42.0", {"center": v(140.5, -139) * mm, "radius": 2.5 * mm});
            skCircle(sketch, "E2.48.43.0", {"center": v(140.5, -147) * mm, "radius": 2.5 * mm});
            skCircle(sketch, "E2.48.44.0", {"center": v(140.5, -155) * mm, "radius": 2.5 * mm});
            skCircle(sketch, "E2.48.45.0", {"center": v(140.5, -163) * mm, "radius": 2.5 * mm});
            skCircle(sketch, "E2.48.46.0", {"center": v(140.5, -171) * mm, "radius": 2.5 * mm});
            skCircle(sketch, "E2.48.47.0", {"center": v(140.5, -179) * mm, "radius": 2.5 * mm});
            skCircle(sketch, "E2.48.48.0", {"center": v(140.5, -187) * mm, "radius": 2.5 * mm});
            skCircle(sketch, "E2.48.49.0", {"center": v(140.5, -195) * mm, "radius": 2.5 * mm});
            skCircle(sketch, "E2.49.0.0", {"center": v(148.5, 197) * mm, "radius": 2.5 * mm});
            skCircle(sketch, "E2.49.1.0", {"center": v(148.5, 189) * mm, "radius": 2.5 * mm});
            skCircle(sketch, "E2.49.2.0", {"center": v(148.5, 181) * mm, "radius": 2.5 * mm});
            skCircle(sketch, "E2.49.3.0", {"center": v(148.5, 173) * mm, "radius": 2.5 * mm});
            skCircle(sketch, "E2.49.4.0", {"center": v(148.5, 165) * mm, "radius": 2.5 * mm});
            skCircle(sketch, "E2.49.5.0", {"center": v(148.5, 157) * mm, "radius": 2.5 * mm});
            skCircle(sketch, "E2.49.6.0", {"center": v(148.5, 149) * mm, "radius": 2.5 * mm});
            skCircle(sketch, "E2.49.7.0", {"center": v(148.5, 141) * mm, "radius": 2.5 * mm});
            skCircle(sketch, "E2.49.8.0", {"center": v(148.5, 133) * mm, "radius": 2.5 * mm});
            skCircle(sketch, "E2.49.9.0", {"center": v(148.5, 125) * mm, "radius": 2.5 * mm});
            skCircle(sketch, "E2.49.10.0", {"center": v(148.5, 117) * mm, "radius": 2.5 * mm});
            skCircle(sketch, "E2.49.11.0", {"center": v(148.5, 109) * mm, "radius": 2.5 * mm});
            skCircle(sketch, "E2.49.12.0", {"center": v(148.5, 101) * mm, "radius": 2.5 * mm});
            skCircle(sketch, "E2.49.13.0", {"center": v(148.5, 93) * mm, "radius": 2.5 * mm});
            skCircle(sketch, "E2.49.14.0", {"center": v(148.5, 85) * mm, "radius": 2.5 * mm});
            skCircle(sketch, "E2.49.15.0", {"center": v(148.5, 77) * mm, "radius": 2.5 * mm});
            skCircle(sketch, "E2.49.16.0", {"center": v(148.5, 69) * mm, "radius": 2.5 * mm});
            skCircle(sketch, "E2.49.17.0", {"center": v(148.5, 61) * mm, "radius": 2.5 * mm});
            skCircle(sketch, "E2.49.18.0", {"center": v(148.5, 53) * mm, "radius": 2.5 * mm});
            skCircle(sketch, "E2.49.19.0", {"center": v(148.5, 45) * mm, "radius": 2.5 * mm});
            skCircle(sketch, "E2.49.20.0", {"center": v(148.5, 37) * mm, "radius": 2.5 * mm});
            skCircle(sketch, "E2.49.21.0", {"center": v(148.5, 29) * mm, "radius": 2.5 * mm});
            skCircle(sketch, "E2.49.22.0", {"center": v(148.5, 21) * mm, "radius": 2.5 * mm});
            skCircle(sketch, "E2.49.23.0", {"center": v(148.5, 13) * mm, "radius": 2.5 * mm});
            skCircle(sketch, "E2.49.24.0", {"center": v(148.5, 5) * mm, "radius": 2.5 * mm});
            skCircle(sketch, "E2.49.25.0", {"center": v(148.5, -3) * mm, "radius": 2.5 * mm});
            skCircle(sketch, "E2.49.26.0", {"center": v(148.5, -11) * mm, "radius": 2.5 * mm});
            skCircle(sketch, "E2.49.27.0", {"center": v(148.5, -19) * mm, "radius": 2.5 * mm});
            skCircle(sketch, "E2.49.28.0", {"center": v(148.5, -27) * mm, "radius": 2.5 * mm});
            skCircle(sketch, "E2.49.29.0", {"center": v(148.5, -35) * mm, "radius": 2.5 * mm});
            skCircle(sketch, "E2.49.30.0", {"center": v(148.5, -43) * mm, "radius": 2.5 * mm});
            skCircle(sketch, "E2.49.31.0", {"center": v(148.5, -51) * mm, "radius": 2.5 * mm});
            skCircle(sketch, "E2.49.32.0", {"center": v(148.5, -59) * mm, "radius": 2.5 * mm});
            skCircle(sketch, "E2.49.33.0", {"center": v(148.5, -67) * mm, "radius": 2.5 * mm});
            skCircle(sketch, "E2.49.34.0", {"center": v(148.5, -75) * mm, "radius": 2.5 * mm});
            skCircle(sketch, "E2.49.35.0", {"center": v(148.5, -83) * mm, "radius": 2.5 * mm});
            skCircle(sketch, "E2.49.36.0", {"center": v(148.5, -91) * mm, "radius": 2.5 * mm});
            skCircle(sketch, "E2.49.37.0", {"center": v(148.5, -99) * mm, "radius": 2.5 * mm});
            skCircle(sketch, "E2.49.38.0", {"center": v(148.5, -107) * mm, "radius": 2.5 * mm});
            skCircle(sketch, "E2.49.39.0", {"center": v(148.5, -115) * mm, "radius": 2.5 * mm});
            skCircle(sketch, "E2.49.40.0", {"center": v(148.5, -123) * mm, "radius": 2.5 * mm});
            skCircle(sketch, "E2.49.41.0", {"center": v(148.5, -131) * mm, "radius": 2.5 * mm});
            skCircle(sketch, "E2.49.42.0", {"center": v(148.5, -139) * mm, "radius": 2.5 * mm});
            skCircle(sketch, "E2.49.43.0", {"center": v(148.5, -147) * mm, "radius": 2.5 * mm});
            skCircle(sketch, "E2.49.44.0", {"center": v(148.5, -155) * mm, "radius": 2.5 * mm});
            skCircle(sketch, "E2.49.45.0", {"center": v(148.5, -163) * mm, "radius": 2.5 * mm});
            skCircle(sketch, "E2.49.46.0", {"center": v(148.5, -171) * mm, "radius": 2.5 * mm});
            skCircle(sketch, "E2.49.47.0", {"center": v(148.5, -179) * mm, "radius": 2.5 * mm});
            skCircle(sketch, "E2.49.48.0", {"center": v(148.5, -187) * mm, "radius": 2.5 * mm});
            skCircle(sketch, "E2.49.49.0", {"center": v(148.5, -195) * mm, "radius": 2.5 * mm});
            skCircle(sketch, "E2.50.0.0", {"center": v(156.5, 197) * mm, "radius": 2.5 * mm});
            skCircle(sketch, "E2.50.1.0", {"center": v(156.5, 189) * mm, "radius": 2.5 * mm});
            skCircle(sketch, "E2.50.2.0", {"center": v(156.5, 181) * mm, "radius": 2.5 * mm});
            skCircle(sketch, "E2.50.3.0", {"center": v(156.5, 173) * mm, "radius": 2.5 * mm});
            skCircle(sketch, "E2.50.4.0", {"center": v(156.5, 165) * mm, "radius": 2.5 * mm});
            skCircle(sketch, "E2.50.5.0", {"center": v(156.5, 157) * mm, "radius": 2.5 * mm});
            skCircle(sketch, "E2.50.6.0", {"center": v(156.5, 149) * mm, "radius": 2.5 * mm});
            skCircle(sketch, "E2.50.7.0", {"center": v(156.5, 141) * mm, "radius": 2.5 * mm});
            skCircle(sketch, "E2.50.8.0", {"center": v(156.5, 133) * mm, "radius": 2.5 * mm});
            skCircle(sketch, "E2.50.9.0", {"center": v(156.5, 125) * mm, "radius": 2.5 * mm});
            skCircle(sketch, "E2.50.10.0", {"center": v(156.5, 117) * mm, "radius": 2.5 * mm});
            skCircle(sketch, "E2.50.11.0", {"center": v(156.5, 109) * mm, "radius": 2.5 * mm});
            skCircle(sketch, "E2.50.12.0", {"center": v(156.5, 101) * mm, "radius": 2.5 * mm});
            skCircle(sketch, "E2.50.13.0", {"center": v(156.5, 93) * mm, "radius": 2.5 * mm});
            skCircle(sketch, "E2.50.14.0", {"center": v(156.5, 85) * mm, "radius": 2.5 * mm});
            skCircle(sketch, "E2.50.15.0", {"center": v(156.5, 77) * mm, "radius": 2.5 * mm});
            skCircle(sketch, "E2.50.16.0", {"center": v(156.5, 69) * mm, "radius": 2.5 * mm});
            skCircle(sketch, "E2.50.17.0", {"center": v(156.5, 61) * mm, "radius": 2.5 * mm});
            skCircle(sketch, "E2.50.18.0", {"center": v(156.5, 53) * mm, "radius": 2.5 * mm});
            skCircle(sketch, "E2.50.19.0", {"center": v(156.5, 45) * mm, "radius": 2.5 * mm});
            skCircle(sketch, "E2.50.20.0", {"center": v(156.5, 37) * mm, "radius": 2.5 * mm});
            skCircle(sketch, "E2.50.21.0", {"center": v(156.5, 29) * mm, "radius": 2.5 * mm});
            skCircle(sketch, "E2.50.22.0", {"center": v(156.5, 21) * mm, "radius": 2.5 * mm});
            skCircle(sketch, "E2.50.23.0", {"center": v(156.5, 13) * mm, "radius": 2.5 * mm});
            skCircle(sketch, "E2.50.24.0", {"center": v(156.5, 5) * mm, "radius": 2.5 * mm});
            skCircle(sketch, "E2.50.25.0", {"center": v(156.5, -3) * mm, "radius": 2.5 * mm});
            skCircle(sketch, "E2.50.26.0", {"center": v(156.5, -11) * mm, "radius": 2.5 * mm});
            skCircle(sketch, "E2.50.27.0", {"center": v(156.5, -19) * mm, "radius": 2.5 * mm});
            skCircle(sketch, "E2.50.28.0", {"center": v(156.5, -27) * mm, "radius": 2.5 * mm});
            skCircle(sketch, "E2.50.29.0", {"center": v(156.5, -35) * mm, "radius": 2.5 * mm});
            skCircle(sketch, "E2.50.30.0", {"center": v(156.5, -43) * mm, "radius": 2.5 * mm});
            skCircle(sketch, "E2.50.31.0", {"center": v(156.5, -51) * mm, "radius": 2.5 * mm});
            skCircle(sketch, "E2.50.32.0", {"center": v(156.5, -59) * mm, "radius": 2.5 * mm});
            skCircle(sketch, "E2.50.33.0", {"center": v(156.5, -67) * mm, "radius": 2.5 * mm});
            skCircle(sketch, "E2.50.34.0", {"center": v(156.5, -75) * mm, "radius": 2.5 * mm});
            skCircle(sketch, "E2.50.35.0", {"center": v(156.5, -83) * mm, "radius": 2.5 * mm});
            skCircle(sketch, "E2.50.36.0", {"center": v(156.5, -91) * mm, "radius": 2.5 * mm});
            skCircle(sketch, "E2.50.37.0", {"center": v(156.5, -99) * mm, "radius": 2.5 * mm});
            skCircle(sketch, "E2.50.38.0", {"center": v(156.5, -107) * mm, "radius": 2.5 * mm});
            skCircle(sketch, "E2.50.39.0", {"center": v(156.5, -115) * mm, "radius": 2.5 * mm});
            skCircle(sketch, "E2.50.40.0", {"center": v(156.5, -123) * mm, "radius": 2.5 * mm});
            skCircle(sketch, "E2.50.41.0", {"center": v(156.5, -131) * mm, "radius": 2.5 * mm});
            skCircle(sketch, "E2.50.42.0", {"center": v(156.5, -139) * mm, "radius": 2.5 * mm});
            skCircle(sketch, "E2.50.43.0", {"center": v(156.5, -147) * mm, "radius": 2.5 * mm});
            skCircle(sketch, "E2.50.44.0", {"center": v(156.5, -155) * mm, "radius": 2.5 * mm});
            skCircle(sketch, "E2.50.45.0", {"center": v(156.5, -163) * mm, "radius": 2.5 * mm});
            skCircle(sketch, "E2.50.46.0", {"center": v(156.5, -171) * mm, "radius": 2.5 * mm});
            skCircle(sketch, "E2.50.47.0", {"center": v(156.5, -179) * mm, "radius": 2.5 * mm});
            skCircle(sketch, "E2.50.48.0", {"center": v(156.5, -187) * mm, "radius": 2.5 * mm});
            skCircle(sketch, "E2.50.49.0", {"center": v(156.5, -195) * mm, "radius": 2.5 * mm});
            skCircle(sketch, "E2.51.0.0", {"center": v(164.5, 197) * mm, "radius": 2.5 * mm});
            skCircle(sketch, "E2.51.1.0", {"center": v(164.5, 189) * mm, "radius": 2.5 * mm});
            skCircle(sketch, "E2.51.2.0", {"center": v(164.5, 181) * mm, "radius": 2.5 * mm});
            skCircle(sketch, "E2.51.3.0", {"center": v(164.5, 173) * mm, "radius": 2.5 * mm});
            skCircle(sketch, "E2.51.4.0", {"center": v(164.5, 165) * mm, "radius": 2.5 * mm});
            skCircle(sketch, "E2.51.5.0", {"center": v(164.5, 157) * mm, "radius": 2.5 * mm});
            skCircle(sketch, "E2.51.6.0", {"center": v(164.5, 149) * mm, "radius": 2.5 * mm});
            skCircle(sketch, "E2.51.7.0", {"center": v(164.5, 141) * mm, "radius": 2.5 * mm});
            skCircle(sketch, "E2.51.8.0", {"center": v(164.5, 133) * mm, "radius": 2.5 * mm});
            skCircle(sketch, "E2.51.9.0", {"center": v(164.5, 125) * mm, "radius": 2.5 * mm});
            skCircle(sketch, "E2.51.10.0", {"center": v(164.5, 117) * mm, "radius": 2.5 * mm});
            skCircle(sketch, "E2.51.11.0", {"center": v(164.5, 109) * mm, "radius": 2.5 * mm});
            skCircle(sketch, "E2.51.12.0", {"center": v(164.5, 101) * mm, "radius": 2.5 * mm});
            skCircle(sketch, "E2.51.13.0", {"center": v(164.5, 93) * mm, "radius": 2.5 * mm});
            skCircle(sketch, "E2.51.14.0", {"center": v(164.5, 85) * mm, "radius": 2.5 * mm});
            skCircle(sketch, "E2.51.15.0", {"center": v(164.5, 77) * mm, "radius": 2.5 * mm});
            skCircle(sketch, "E2.51.16.0", {"center": v(164.5, 69) * mm, "radius": 2.5 * mm});
            skCircle(sketch, "E2.51.17.0", {"center": v(164.5, 61) * mm, "radius": 2.5 * mm});
            skCircle(sketch, "E2.51.18.0", {"center": v(164.5, 53) * mm, "radius": 2.5 * mm});
            skCircle(sketch, "E2.51.19.0", {"center": v(164.5, 45) * mm, "radius": 2.5 * mm});
            skCircle(sketch, "E2.51.20.0", {"center": v(164.5, 37) * mm, "radius": 2.5 * mm});
            skCircle(sketch, "E2.51.21.0", {"center": v(164.5, 29) * mm, "radius": 2.5 * mm});
            skCircle(sketch, "E2.51.22.0", {"center": v(164.5, 21) * mm, "radius": 2.5 * mm});
            skCircle(sketch, "E2.51.23.0", {"center": v(164.5, 13) * mm, "radius": 2.5 * mm});
            skCircle(sketch, "E2.51.24.0", {"center": v(164.5, 5) * mm, "radius": 2.5 * mm});
            skCircle(sketch, "E2.51.25.0", {"center": v(164.5, -3) * mm, "radius": 2.5 * mm});
            skCircle(sketch, "E2.51.26.0", {"center": v(164.5, -11) * mm, "radius": 2.5 * mm});
            skCircle(sketch, "E2.51.27.0", {"center": v(164.5, -19) * mm, "radius": 2.5 * mm});
            skCircle(sketch, "E2.51.28.0", {"center": v(164.5, -27) * mm, "radius": 2.5 * mm});
            skCircle(sketch, "E2.51.29.0", {"center": v(164.5, -35) * mm, "radius": 2.5 * mm});
            skCircle(sketch, "E2.51.30.0", {"center": v(164.5, -43) * mm, "radius": 2.5 * mm});
            skCircle(sketch, "E2.51.31.0", {"center": v(164.5, -51) * mm, "radius": 2.5 * mm});
            skCircle(sketch, "E2.51.32.0", {"center": v(164.5, -59) * mm, "radius": 2.5 * mm});
            skCircle(sketch, "E2.51.33.0", {"center": v(164.5, -67) * mm, "radius": 2.5 * mm});
            skCircle(sketch, "E2.51.34.0", {"center": v(164.5, -75) * mm, "radius": 2.5 * mm});
            skCircle(sketch, "E2.51.35.0", {"center": v(164.5, -83) * mm, "radius": 2.5 * mm});
            skCircle(sketch, "E2.51.36.0", {"center": v(164.5, -91) * mm, "radius": 2.5 * mm});
            skCircle(sketch, "E2.51.37.0", {"center": v(164.5, -99) * mm, "radius": 2.5 * mm});
            skCircle(sketch, "E2.51.38.0", {"center": v(164.5, -107) * mm, "radius": 2.5 * mm});
            skCircle(sketch, "E2.51.39.0", {"center": v(164.5, -115) * mm, "radius": 2.5 * mm});
            skCircle(sketch, "E2.51.40.0", {"center": v(164.5, -123) * mm, "radius": 2.5 * mm});
            skCircle(sketch, "E2.51.41.0", {"center": v(164.5, -131) * mm, "radius": 2.5 * mm});
            skCircle(sketch, "E2.51.42.0", {"center": v(164.5, -139) * mm, "radius": 2.5 * mm});
            skCircle(sketch, "E2.51.43.0", {"center": v(164.5, -147) * mm, "radius": 2.5 * mm});
            skCircle(sketch, "E2.51.44.0", {"center": v(164.5, -155) * mm, "radius": 2.5 * mm});
            skCircle(sketch, "E2.51.45.0", {"center": v(164.5, -163) * mm, "radius": 2.5 * mm});
            skCircle(sketch, "E2.51.46.0", {"center": v(164.5, -171) * mm, "radius": 2.5 * mm});
            skCircle(sketch, "E2.51.47.0", {"center": v(164.5, -179) * mm, "radius": 2.5 * mm});
            skCircle(sketch, "E2.51.48.0", {"center": v(164.5, -187) * mm, "radius": 2.5 * mm});
            skCircle(sketch, "E2.51.49.0", {"center": v(164.5, -195) * mm, "radius": 2.5 * mm});
            skCircle(sketch, "E2.52.0.0", {"center": v(172.5, 197) * mm, "radius": 2.5 * mm});
            skCircle(sketch, "E2.52.1.0", {"center": v(172.5, 189) * mm, "radius": 2.5 * mm});
            skCircle(sketch, "E2.52.2.0", {"center": v(172.5, 181) * mm, "radius": 2.5 * mm});
            skCircle(sketch, "E2.52.3.0", {"center": v(172.5, 173) * mm, "radius": 2.5 * mm});
            skCircle(sketch, "E2.52.4.0", {"center": v(172.5, 165) * mm, "radius": 2.5 * mm});
            skCircle(sketch, "E2.52.5.0", {"center": v(172.5, 157) * mm, "radius": 2.5 * mm});
            skCircle(sketch, "E2.52.6.0", {"center": v(172.5, 149) * mm, "radius": 2.5 * mm});
            skCircle(sketch, "E2.52.7.0", {"center": v(172.5, 141) * mm, "radius": 2.5 * mm});
            skCircle(sketch, "E2.52.8.0", {"center": v(172.5, 133) * mm, "radius": 2.5 * mm});
            skCircle(sketch, "E2.52.9.0", {"center": v(172.5, 125) * mm, "radius": 2.5 * mm});
            skCircle(sketch, "E2.52.10.0", {"center": v(172.5, 117) * mm, "radius": 2.5 * mm});
            skCircle(sketch, "E2.52.11.0", {"center": v(172.5, 109) * mm, "radius": 2.5 * mm});
            skCircle(sketch, "E2.52.12.0", {"center": v(172.5, 101) * mm, "radius": 2.5 * mm});
            skCircle(sketch, "E2.52.13.0", {"center": v(172.5, 93) * mm, "radius": 2.5 * mm});
            skCircle(sketch, "E2.52.14.0", {"center": v(172.5, 85) * mm, "radius": 2.5 * mm});
            skCircle(sketch, "E2.52.15.0", {"center": v(172.5, 77) * mm, "radius": 2.5 * mm});
            skCircle(sketch, "E2.52.16.0", {"center": v(172.5, 69) * mm, "radius": 2.5 * mm});
            skCircle(sketch, "E2.52.17.0", {"center": v(172.5, 61) * mm, "radius": 2.5 * mm});
            skCircle(sketch, "E2.52.18.0", {"center": v(172.5, 53) * mm, "radius": 2.5 * mm});
            skCircle(sketch, "E2.52.19.0", {"center": v(172.5, 45) * mm, "radius": 2.5 * mm});
            skCircle(sketch, "E2.52.20.0", {"center": v(172.5, 37) * mm, "radius": 2.5 * mm});
            skCircle(sketch, "E2.52.21.0", {"center": v(172.5, 29) * mm, "radius": 2.5 * mm});
            skCircle(sketch, "E2.52.22.0", {"center": v(172.5, 21) * mm, "radius": 2.5 * mm});
            skCircle(sketch, "E2.52.23.0", {"center": v(172.5, 13) * mm, "radius": 2.5 * mm});
            skCircle(sketch, "E2.52.24.0", {"center": v(172.5, 5) * mm, "radius": 2.5 * mm});
            skCircle(sketch, "E2.52.25.0", {"center": v(172.5, -3) * mm, "radius": 2.5 * mm});
            skCircle(sketch, "E2.52.26.0", {"center": v(172.5, -11) * mm, "radius": 2.5 * mm});
            skCircle(sketch, "E2.52.27.0", {"center": v(172.5, -19) * mm, "radius": 2.5 * mm});
            skCircle(sketch, "E2.52.28.0", {"center": v(172.5, -27) * mm, "radius": 2.5 * mm});
            skCircle(sketch, "E2.52.29.0", {"center": v(172.5, -35) * mm, "radius": 2.5 * mm});
            skCircle(sketch, "E2.52.30.0", {"center": v(172.5, -43) * mm, "radius": 2.5 * mm});
            skCircle(sketch, "E2.52.31.0", {"center": v(172.5, -51) * mm, "radius": 2.5 * mm});
            skCircle(sketch, "E2.52.32.0", {"center": v(172.5, -59) * mm, "radius": 2.5 * mm});
            skCircle(sketch, "E2.52.33.0", {"center": v(172.5, -67) * mm, "radius": 2.5 * mm});
            skCircle(sketch, "E2.52.34.0", {"center": v(172.5, -75) * mm, "radius": 2.5 * mm});
            skCircle(sketch, "E2.52.35.0", {"center": v(172.5, -83) * mm, "radius": 2.5 * mm});
            skCircle(sketch, "E2.52.36.0", {"center": v(172.5, -91) * mm, "radius": 2.5 * mm});
            skCircle(sketch, "E2.52.37.0", {"center": v(172.5, -99) * mm, "radius": 2.5 * mm});
            skCircle(sketch, "E2.52.38.0", {"center": v(172.5, -107) * mm, "radius": 2.5 * mm});
            skCircle(sketch, "E2.52.39.0", {"center": v(172.5, -115) * mm, "radius": 2.5 * mm});
            skCircle(sketch, "E2.52.40.0", {"center": v(172.5, -123) * mm, "radius": 2.5 * mm});
            skCircle(sketch, "E2.52.41.0", {"center": v(172.5, -131) * mm, "radius": 2.5 * mm});
            skCircle(sketch, "E2.52.42.0", {"center": v(172.5, -139) * mm, "radius": 2.5 * mm});
            skCircle(sketch, "E2.52.43.0", {"center": v(172.5, -147) * mm, "radius": 2.5 * mm});
            skCircle(sketch, "E2.52.44.0", {"center": v(172.5, -155) * mm, "radius": 2.5 * mm});
            skCircle(sketch, "E2.52.45.0", {"center": v(172.5, -163) * mm, "radius": 2.5 * mm});
            skCircle(sketch, "E2.52.46.0", {"center": v(172.5, -171) * mm, "radius": 2.5 * mm});
            skCircle(sketch, "E2.52.47.0", {"center": v(172.5, -179) * mm, "radius": 2.5 * mm});
            skCircle(sketch, "E2.52.48.0", {"center": v(172.5, -187) * mm, "radius": 2.5 * mm});
            skCircle(sketch, "E2.52.49.0", {"center": v(172.5, -195) * mm, "radius": 2.5 * mm});
            skCircle(sketch, "E2.53.0.0", {"center": v(180.5, 197) * mm, "radius": 2.5 * mm});
            skCircle(sketch, "E2.53.1.0", {"center": v(180.5, 189) * mm, "radius": 2.5 * mm});
            skCircle(sketch, "E2.53.2.0", {"center": v(180.5, 181) * mm, "radius": 2.5 * mm});
            skCircle(sketch, "E2.53.3.0", {"center": v(180.5, 173) * mm, "radius": 2.5 * mm});
            skCircle(sketch, "E2.53.4.0", {"center": v(180.5, 165) * mm, "radius": 2.5 * mm});
            skCircle(sketch, "E2.53.5.0", {"center": v(180.5, 157) * mm, "radius": 2.5 * mm});
            skCircle(sketch, "E2.53.6.0", {"center": v(180.5, 149) * mm, "radius": 2.5 * mm});
            skCircle(sketch, "E2.53.7.0", {"center": v(180.5, 141) * mm, "radius": 2.5 * mm});
            skCircle(sketch, "E2.53.8.0", {"center": v(180.5, 133) * mm, "radius": 2.5 * mm});
            skCircle(sketch, "E2.53.9.0", {"center": v(180.5, 125) * mm, "radius": 2.5 * mm});
            skCircle(sketch, "E2.53.10.0", {"center": v(180.5, 117) * mm, "radius": 2.5 * mm});
            skCircle(sketch, "E2.53.11.0", {"center": v(180.5, 109) * mm, "radius": 2.5 * mm});
            skCircle(sketch, "E2.53.12.0", {"center": v(180.5, 101) * mm, "radius": 2.5 * mm});
            skCircle(sketch, "E2.53.13.0", {"center": v(180.5, 93) * mm, "radius": 2.5 * mm});
            skCircle(sketch, "E2.53.14.0", {"center": v(180.5, 85) * mm, "radius": 2.5 * mm});
            skCircle(sketch, "E2.53.15.0", {"center": v(180.5, 77) * mm, "radius": 2.5 * mm});
            skCircle(sketch, "E2.53.16.0", {"center": v(180.5, 69) * mm, "radius": 2.5 * mm});
            skCircle(sketch, "E2.53.17.0", {"center": v(180.5, 61) * mm, "radius": 2.5 * mm});
            skCircle(sketch, "E2.53.18.0", {"center": v(180.5, 53) * mm, "radius": 2.5 * mm});
            skCircle(sketch, "E2.53.19.0", {"center": v(180.5, 45) * mm, "radius": 2.5 * mm});
            skCircle(sketch, "E2.53.20.0", {"center": v(180.5, 37) * mm, "radius": 2.5 * mm});
            skCircle(sketch, "E2.53.21.0", {"center": v(180.5, 29) * mm, "radius": 2.5 * mm});
            skCircle(sketch, "E2.53.22.0", {"center": v(180.5, 21) * mm, "radius": 2.5 * mm});
            skCircle(sketch, "E2.53.23.0", {"center": v(180.5, 13) * mm, "radius": 2.5 * mm});
            skCircle(sketch, "E2.53.24.0", {"center": v(180.5, 5) * mm, "radius": 2.5 * mm});
            skCircle(sketch, "E2.53.25.0", {"center": v(180.5, -3) * mm, "radius": 2.5 * mm});
            skCircle(sketch, "E2.53.26.0", {"center": v(180.5, -11) * mm, "radius": 2.5 * mm});
            skCircle(sketch, "E2.53.27.0", {"center": v(180.5, -19) * mm, "radius": 2.5 * mm});
            skCircle(sketch, "E2.53.28.0", {"center": v(180.5, -27) * mm, "radius": 2.5 * mm});
            skCircle(sketch, "E2.53.29.0", {"center": v(180.5, -35) * mm, "radius": 2.5 * mm});
            skCircle(sketch, "E2.53.30.0", {"center": v(180.5, -43) * mm, "radius": 2.5 * mm});
            skCircle(sketch, "E2.53.31.0", {"center": v(180.5, -51) * mm, "radius": 2.5 * mm});
            skCircle(sketch, "E2.53.32.0", {"center": v(180.5, -59) * mm, "radius": 2.5 * mm});
            skCircle(sketch, "E2.53.33.0", {"center": v(180.5, -67) * mm, "radius": 2.5 * mm});
            skCircle(sketch, "E2.53.34.0", {"center": v(180.5, -75) * mm, "radius": 2.5 * mm});
            skCircle(sketch, "E2.53.35.0", {"center": v(180.5, -83) * mm, "radius": 2.5 * mm});
            skCircle(sketch, "E2.53.36.0", {"center": v(180.5, -91) * mm, "radius": 2.5 * mm});
            skCircle(sketch, "E2.53.37.0", {"center": v(180.5, -99) * mm, "radius": 2.5 * mm});
            skCircle(sketch, "E2.53.38.0", {"center": v(180.5, -107) * mm, "radius": 2.5 * mm});
            skCircle(sketch, "E2.53.39.0", {"center": v(180.5, -115) * mm, "radius": 2.5 * mm});
            skCircle(sketch, "E2.53.40.0", {"center": v(180.5, -123) * mm, "radius": 2.5 * mm});
            skCircle(sketch, "E2.53.41.0", {"center": v(180.5, -131) * mm, "radius": 2.5 * mm});
            skCircle(sketch, "E2.53.42.0", {"center": v(180.5, -139) * mm, "radius": 2.5 * mm});
            skCircle(sketch, "E2.53.43.0", {"center": v(180.5, -147) * mm, "radius": 2.5 * mm});
            skCircle(sketch, "E2.53.44.0", {"center": v(180.5, -155) * mm, "radius": 2.5 * mm});
            skCircle(sketch, "E2.53.45.0", {"center": v(180.5, -163) * mm, "radius": 2.5 * mm});
            skCircle(sketch, "E2.53.46.0", {"center": v(180.5, -171) * mm, "radius": 2.5 * mm});
            skCircle(sketch, "E2.53.47.0", {"center": v(180.5, -179) * mm, "radius": 2.5 * mm});
            skCircle(sketch, "E2.53.48.0", {"center": v(180.5, -187) * mm, "radius": 2.5 * mm});
            skCircle(sketch, "E2.53.49.0", {"center": v(180.5, -195) * mm, "radius": 2.5 * mm});
            skCircle(sketch, "E2.54.0.0", {"center": v(188.5, 197) * mm, "radius": 2.5 * mm});
            skCircle(sketch, "E2.54.1.0", {"center": v(188.5, 189) * mm, "radius": 2.5 * mm});
            skCircle(sketch, "E2.54.2.0", {"center": v(188.5, 181) * mm, "radius": 2.5 * mm});
            skCircle(sketch, "E2.54.3.0", {"center": v(188.5, 173) * mm, "radius": 2.5 * mm});
            skCircle(sketch, "E2.54.4.0", {"center": v(188.5, 165) * mm, "radius": 2.5 * mm});
            skCircle(sketch, "E2.54.5.0", {"center": v(188.5, 157) * mm, "radius": 2.5 * mm});
            skCircle(sketch, "E2.54.6.0", {"center": v(188.5, 149) * mm, "radius": 2.5 * mm});
            skCircle(sketch, "E2.54.7.0", {"center": v(188.5, 141) * mm, "radius": 2.5 * mm});
            skCircle(sketch, "E2.54.8.0", {"center": v(188.5, 133) * mm, "radius": 2.5 * mm});
            skCircle(sketch, "E2.54.9.0", {"center": v(188.5, 125) * mm, "radius": 2.5 * mm});
            skCircle(sketch, "E2.54.10.0", {"center": v(188.5, 117) * mm, "radius": 2.5 * mm});
            skCircle(sketch, "E2.54.11.0", {"center": v(188.5, 109) * mm, "radius": 2.5 * mm});
            skCircle(sketch, "E2.54.12.0", {"center": v(188.5, 101) * mm, "radius": 2.5 * mm});
            skCircle(sketch, "E2.54.13.0", {"center": v(188.5, 93) * mm, "radius": 2.5 * mm});
            skCircle(sketch, "E2.54.14.0", {"center": v(188.5, 85) * mm, "radius": 2.5 * mm});
            skCircle(sketch, "E2.54.15.0", {"center": v(188.5, 77) * mm, "radius": 2.5 * mm});
            skCircle(sketch, "E2.54.16.0", {"center": v(188.5, 69) * mm, "radius": 2.5 * mm});
            skCircle(sketch, "E2.54.17.0", {"center": v(188.5, 61) * mm, "radius": 2.5 * mm});
            skCircle(sketch, "E2.54.18.0", {"center": v(188.5, 53) * mm, "radius": 2.5 * mm});
            skCircle(sketch, "E2.54.19.0", {"center": v(188.5, 45) * mm, "radius": 2.5 * mm});
            skCircle(sketch, "E2.54.20.0", {"center": v(188.5, 37) * mm, "radius": 2.5 * mm});
            skCircle(sketch, "E2.54.21.0", {"center": v(188.5, 29) * mm, "radius": 2.5 * mm});
            skCircle(sketch, "E2.54.22.0", {"center": v(188.5, 21) * mm, "radius": 2.5 * mm});
            skCircle(sketch, "E2.54.23.0", {"center": v(188.5, 13) * mm, "radius": 2.5 * mm});
            skCircle(sketch, "E2.54.24.0", {"center": v(188.5, 5) * mm, "radius": 2.5 * mm});
            skCircle(sketch, "E2.54.25.0", {"center": v(188.5, -3) * mm, "radius": 2.5 * mm});
            skCircle(sketch, "E2.54.26.0", {"center": v(188.5, -11) * mm, "radius": 2.5 * mm});
            skCircle(sketch, "E2.54.27.0", {"center": v(188.5, -19) * mm, "radius": 2.5 * mm});
            skCircle(sketch, "E2.54.28.0", {"center": v(188.5, -27) * mm, "radius": 2.5 * mm});
            skCircle(sketch, "E2.54.29.0", {"center": v(188.5, -35) * mm, "radius": 2.5 * mm});
            skCircle(sketch, "E2.54.30.0", {"center": v(188.5, -43) * mm, "radius": 2.5 * mm});
            skCircle(sketch, "E2.54.31.0", {"center": v(188.5, -51) * mm, "radius": 2.5 * mm});
            skCircle(sketch, "E2.54.32.0", {"center": v(188.5, -59) * mm, "radius": 2.5 * mm});
            skCircle(sketch, "E2.54.33.0", {"center": v(188.5, -67) * mm, "radius": 2.5 * mm});
            skCircle(sketch, "E2.54.34.0", {"center": v(188.5, -75) * mm, "radius": 2.5 * mm});
            skCircle(sketch, "E2.54.35.0", {"center": v(188.5, -83) * mm, "radius": 2.5 * mm});
            skCircle(sketch, "E2.54.36.0", {"center": v(188.5, -91) * mm, "radius": 2.5 * mm});
            skCircle(sketch, "E2.54.37.0", {"center": v(188.5, -99) * mm, "radius": 2.5 * mm});
            skCircle(sketch, "E2.54.38.0", {"center": v(188.5, -107) * mm, "radius": 2.5 * mm});
            skCircle(sketch, "E2.54.39.0", {"center": v(188.5, -115) * mm, "radius": 2.5 * mm});
            skCircle(sketch, "E2.54.40.0", {"center": v(188.5, -123) * mm, "radius": 2.5 * mm});
            skCircle(sketch, "E2.54.41.0", {"center": v(188.5, -131) * mm, "radius": 2.5 * mm});
            skCircle(sketch, "E2.54.42.0", {"center": v(188.5, -139) * mm, "radius": 2.5 * mm});
            skCircle(sketch, "E2.54.43.0", {"center": v(188.5, -147) * mm, "radius": 2.5 * mm});
            skCircle(sketch, "E2.54.44.0", {"center": v(188.5, -155) * mm, "radius": 2.5 * mm});
            skCircle(sketch, "E2.54.45.0", {"center": v(188.5, -163) * mm, "radius": 2.5 * mm});
            skCircle(sketch, "E2.54.46.0", {"center": v(188.5, -171) * mm, "radius": 2.5 * mm});
            skCircle(sketch, "E2.54.47.0", {"center": v(188.5, -179) * mm, "radius": 2.5 * mm});
            skCircle(sketch, "E2.54.48.0", {"center": v(188.5, -187) * mm, "radius": 2.5 * mm});
            skCircle(sketch, "E2.54.49.0", {"center": v(188.5, -195) * mm, "radius": 2.5 * mm});
            skCircle(sketch, "E2.55.0.0", {"center": v(196.5, 197) * mm, "radius": 2.5 * mm});
            skCircle(sketch, "E2.55.1.0", {"center": v(196.5, 189) * mm, "radius": 2.5 * mm});
            skCircle(sketch, "E2.55.2.0", {"center": v(196.5, 181) * mm, "radius": 2.5 * mm});
            skCircle(sketch, "E2.55.3.0", {"center": v(196.5, 173) * mm, "radius": 2.5 * mm});
            skCircle(sketch, "E2.55.4.0", {"center": v(196.5, 165) * mm, "radius": 2.5 * mm});
            skCircle(sketch, "E2.55.5.0", {"center": v(196.5, 157) * mm, "radius": 2.5 * mm});
            skCircle(sketch, "E2.55.6.0", {"center": v(196.5, 149) * mm, "radius": 2.5 * mm});
            skCircle(sketch, "E2.55.7.0", {"center": v(196.5, 141) * mm, "radius": 2.5 * mm});
            skCircle(sketch, "E2.55.8.0", {"center": v(196.5, 133) * mm, "radius": 2.5 * mm});
            skCircle(sketch, "E2.55.9.0", {"center": v(196.5, 125) * mm, "radius": 2.5 * mm});
            skCircle(sketch, "E2.55.10.0", {"center": v(196.5, 117) * mm, "radius": 2.5 * mm});
            skCircle(sketch, "E2.55.11.0", {"center": v(196.5, 109) * mm, "radius": 2.5 * mm});
            skCircle(sketch, "E2.55.12.0", {"center": v(196.5, 101) * mm, "radius": 2.5 * mm});
            skCircle(sketch, "E2.55.13.0", {"center": v(196.5, 93) * mm, "radius": 2.5 * mm});
            skCircle(sketch, "E2.55.14.0", {"center": v(196.5, 85) * mm, "radius": 2.5 * mm});
            skCircle(sketch, "E2.55.15.0", {"center": v(196.5, 77) * mm, "radius": 2.5 * mm});
            skCircle(sketch, "E2.55.16.0", {"center": v(196.5, 69) * mm, "radius": 2.5 * mm});
            skCircle(sketch, "E2.55.17.0", {"center": v(196.5, 61) * mm, "radius": 2.5 * mm});
            skCircle(sketch, "E2.55.18.0", {"center": v(196.5, 53) * mm, "radius": 2.5 * mm});
            skCircle(sketch, "E2.55.19.0", {"center": v(196.5, 45) * mm, "radius": 2.5 * mm});
            skCircle(sketch, "E2.55.20.0", {"center": v(196.5, 37) * mm, "radius": 2.5 * mm});
            skCircle(sketch, "E2.55.21.0", {"center": v(196.5, 29) * mm, "radius": 2.5 * mm});
            skCircle(sketch, "E2.55.22.0", {"center": v(196.5, 21) * mm, "radius": 2.5 * mm});
            skCircle(sketch, "E2.55.23.0", {"center": v(196.5, 13) * mm, "radius": 2.5 * mm});
            skCircle(sketch, "E2.55.24.0", {"center": v(196.5, 5) * mm, "radius": 2.5 * mm});
            skCircle(sketch, "E2.55.25.0", {"center": v(196.5, -3) * mm, "radius": 2.5 * mm});
            skCircle(sketch, "E2.55.26.0", {"center": v(196.5, -11) * mm, "radius": 2.5 * mm});
            skCircle(sketch, "E2.55.27.0", {"center": v(196.5, -19) * mm, "radius": 2.5 * mm});
            skCircle(sketch, "E2.55.28.0", {"center": v(196.5, -27) * mm, "radius": 2.5 * mm});
            skCircle(sketch, "E2.55.29.0", {"center": v(196.5, -35) * mm, "radius": 2.5 * mm});
            skCircle(sketch, "E2.55.30.0", {"center": v(196.5, -43) * mm, "radius": 2.5 * mm});
            skCircle(sketch, "E2.55.31.0", {"center": v(196.5, -51) * mm, "radius": 2.5 * mm});
            skCircle(sketch, "E2.55.32.0", {"center": v(196.5, -59) * mm, "radius": 2.5 * mm});
            skCircle(sketch, "E2.55.33.0", {"center": v(196.5, -67) * mm, "radius": 2.5 * mm});
            skCircle(sketch, "E2.55.34.0", {"center": v(196.5, -75) * mm, "radius": 2.5 * mm});
            skCircle(sketch, "E2.55.35.0", {"center": v(196.5, -83) * mm, "radius": 2.5 * mm});
            skCircle(sketch, "E2.55.36.0", {"center": v(196.5, -91) * mm, "radius": 2.5 * mm});
            skCircle(sketch, "E2.55.37.0", {"center": v(196.5, -99) * mm, "radius": 2.5 * mm});
            skCircle(sketch, "E2.55.38.0", {"center": v(196.5, -107) * mm, "radius": 2.5 * mm});
            skCircle(sketch, "E2.55.39.0", {"center": v(196.5, -115) * mm, "radius": 2.5 * mm});
            skCircle(sketch, "E2.55.40.0", {"center": v(196.5, -123) * mm, "radius": 2.5 * mm});
            skCircle(sketch, "E2.55.41.0", {"center": v(196.5, -131) * mm, "radius": 2.5 * mm});
            skCircle(sketch, "E2.55.42.0", {"center": v(196.5, -139) * mm, "radius": 2.5 * mm});
            skCircle(sketch, "E2.55.43.0", {"center": v(196.5, -147) * mm, "radius": 2.5 * mm});
            skCircle(sketch, "E2.55.44.0", {"center": v(196.5, -155) * mm, "radius": 2.5 * mm});
            skCircle(sketch, "E2.55.45.0", {"center": v(196.5, -163) * mm, "radius": 2.5 * mm});
            skCircle(sketch, "E2.55.46.0", {"center": v(196.5, -171) * mm, "radius": 2.5 * mm});
            skCircle(sketch, "E2.55.47.0", {"center": v(196.5, -179) * mm, "radius": 2.5 * mm});
            skCircle(sketch, "E2.55.48.0", {"center": v(196.5, -187) * mm, "radius": 2.5 * mm});
            skCircle(sketch, "E2.55.49.0", {"center": v(196.5, -195) * mm, "radius": 2.5 * mm});
            skCircle(sketch, "E2.56.0.0", {"center": v(204.5, 197) * mm, "radius": 2.5 * mm});
            skCircle(sketch, "E2.56.1.0", {"center": v(204.5, 189) * mm, "radius": 2.5 * mm});
            skCircle(sketch, "E2.56.2.0", {"center": v(204.5, 181) * mm, "radius": 2.5 * mm});
            skCircle(sketch, "E2.56.3.0", {"center": v(204.5, 173) * mm, "radius": 2.5 * mm});
            skCircle(sketch, "E2.56.4.0", {"center": v(204.5, 165) * mm, "radius": 2.5 * mm});
            skCircle(sketch, "E2.56.5.0", {"center": v(204.5, 157) * mm, "radius": 2.5 * mm});
            skCircle(sketch, "E2.56.6.0", {"center": v(204.5, 149) * mm, "radius": 2.5 * mm});
            skCircle(sketch, "E2.56.7.0", {"center": v(204.5, 141) * mm, "radius": 2.5 * mm});
            skCircle(sketch, "E2.56.8.0", {"center": v(204.5, 133) * mm, "radius": 2.5 * mm});
            skCircle(sketch, "E2.56.9.0", {"center": v(204.5, 125) * mm, "radius": 2.5 * mm});
            skCircle(sketch, "E2.56.10.0", {"center": v(204.5, 117) * mm, "radius": 2.5 * mm});
            skCircle(sketch, "E2.56.11.0", {"center": v(204.5, 109) * mm, "radius": 2.5 * mm});
            skCircle(sketch, "E2.56.12.0", {"center": v(204.5, 101) * mm, "radius": 2.5 * mm});
            skCircle(sketch, "E2.56.13.0", {"center": v(204.5, 93) * mm, "radius": 2.5 * mm});
            skCircle(sketch, "E2.56.14.0", {"center": v(204.5, 85) * mm, "radius": 2.5 * mm});
            skCircle(sketch, "E2.56.15.0", {"center": v(204.5, 77) * mm, "radius": 2.5 * mm});
            skCircle(sketch, "E2.56.16.0", {"center": v(204.5, 69) * mm, "radius": 2.5 * mm});
            skCircle(sketch, "E2.56.17.0", {"center": v(204.5, 61) * mm, "radius": 2.5 * mm});
            skCircle(sketch, "E2.56.18.0", {"center": v(204.5, 53) * mm, "radius": 2.5 * mm});
            skCircle(sketch, "E2.56.19.0", {"center": v(204.5, 45) * mm, "radius": 2.5 * mm});
            skCircle(sketch, "E2.56.20.0", {"center": v(204.5, 37) * mm, "radius": 2.5 * mm});
            skCircle(sketch, "E2.56.21.0", {"center": v(204.5, 29) * mm, "radius": 2.5 * mm});
            skCircle(sketch, "E2.56.22.0", {"center": v(204.5, 21) * mm, "radius": 2.5 * mm});
            skCircle(sketch, "E2.56.23.0", {"center": v(204.5, 13) * mm, "radius": 2.5 * mm});
            skCircle(sketch, "E2.56.24.0", {"center": v(204.5, 5) * mm, "radius": 2.5 * mm});
            skCircle(sketch, "E2.56.25.0", {"center": v(204.5, -3) * mm, "radius": 2.5 * mm});
            skCircle(sketch, "E2.56.26.0", {"center": v(204.5, -11) * mm, "radius": 2.5 * mm});
            skCircle(sketch, "E2.56.27.0", {"center": v(204.5, -19) * mm, "radius": 2.5 * mm});
            skCircle(sketch, "E2.56.28.0", {"center": v(204.5, -27) * mm, "radius": 2.5 * mm});
            skCircle(sketch, "E2.56.29.0", {"center": v(204.5, -35) * mm, "radius": 2.5 * mm});
            skCircle(sketch, "E2.56.30.0", {"center": v(204.5, -43) * mm, "radius": 2.5 * mm});
            skCircle(sketch, "E2.56.31.0", {"center": v(204.5, -51) * mm, "radius": 2.5 * mm});
            skCircle(sketch, "E2.56.32.0", {"center": v(204.5, -59) * mm, "radius": 2.5 * mm});
            skCircle(sketch, "E2.56.33.0", {"center": v(204.5, -67) * mm, "radius": 2.5 * mm});
            skCircle(sketch, "E2.56.34.0", {"center": v(204.5, -75) * mm, "radius": 2.5 * mm});
            skCircle(sketch, "E2.56.35.0", {"center": v(204.5, -83) * mm, "radius": 2.5 * mm});
            skCircle(sketch, "E2.56.36.0", {"center": v(204.5, -91) * mm, "radius": 2.5 * mm});
            skCircle(sketch, "E2.56.37.0", {"center": v(204.5, -99) * mm, "radius": 2.5 * mm});
            skCircle(sketch, "E2.56.38.0", {"center": v(204.5, -107) * mm, "radius": 2.5 * mm});
            skCircle(sketch, "E2.56.39.0", {"center": v(204.5, -115) * mm, "radius": 2.5 * mm});
            skCircle(sketch, "E2.56.40.0", {"center": v(204.5, -123) * mm, "radius": 2.5 * mm});
            skCircle(sketch, "E2.56.41.0", {"center": v(204.5, -131) * mm, "radius": 2.5 * mm});
            skCircle(sketch, "E2.56.42.0", {"center": v(204.5, -139) * mm, "radius": 2.5 * mm});
            skCircle(sketch, "E2.56.43.0", {"center": v(204.5, -147) * mm, "radius": 2.5 * mm});
            skCircle(sketch, "E2.56.44.0", {"center": v(204.5, -155) * mm, "radius": 2.5 * mm});
            skCircle(sketch, "E2.56.45.0", {"center": v(204.5, -163) * mm, "radius": 2.5 * mm});
            skCircle(sketch, "E2.56.46.0", {"center": v(204.5, -171) * mm, "radius": 2.5 * mm});
            skCircle(sketch, "E2.56.47.0", {"center": v(204.5, -179) * mm, "radius": 2.5 * mm});
            skCircle(sketch, "E2.56.48.0", {"center": v(204.5, -187) * mm, "radius": 2.5 * mm});
            skCircle(sketch, "E2.56.49.0", {"center": v(204.5, -195) * mm, "radius": 2.5 * mm});
            skCircle(sketch, "E2.57.0.0", {"center": v(212.5, 197) * mm, "radius": 2.5 * mm});
            skCircle(sketch, "E2.57.1.0", {"center": v(212.5, 189) * mm, "radius": 2.5 * mm});
            skCircle(sketch, "E2.57.2.0", {"center": v(212.5, 181) * mm, "radius": 2.5 * mm});
            skCircle(sketch, "E2.57.3.0", {"center": v(212.5, 173) * mm, "radius": 2.5 * mm});
            skCircle(sketch, "E2.57.4.0", {"center": v(212.5, 165) * mm, "radius": 2.5 * mm});
            skCircle(sketch, "E2.57.5.0", {"center": v(212.5, 157) * mm, "radius": 2.5 * mm});
            skCircle(sketch, "E2.57.6.0", {"center": v(212.5, 149) * mm, "radius": 2.5 * mm});
            skCircle(sketch, "E2.57.7.0", {"center": v(212.5, 141) * mm, "radius": 2.5 * mm});
            skCircle(sketch, "E2.57.8.0", {"center": v(212.5, 133) * mm, "radius": 2.5 * mm});
            skCircle(sketch, "E2.57.9.0", {"center": v(212.5, 125) * mm, "radius": 2.5 * mm});
            skCircle(sketch, "E2.57.10.0", {"center": v(212.5, 117) * mm, "radius": 2.5 * mm});
            skCircle(sketch, "E2.57.11.0", {"center": v(212.5, 109) * mm, "radius": 2.5 * mm});
            skCircle(sketch, "E2.57.12.0", {"center": v(212.5, 101) * mm, "radius": 2.5 * mm});
            skCircle(sketch, "E2.57.13.0", {"center": v(212.5, 93) * mm, "radius": 2.5 * mm});
            skCircle(sketch, "E2.57.14.0", {"center": v(212.5, 85) * mm, "radius": 2.5 * mm});
            skCircle(sketch, "E2.57.15.0", {"center": v(212.5, 77) * mm, "radius": 2.5 * mm});
            skCircle(sketch, "E2.57.16.0", {"center": v(212.5, 69) * mm, "radius": 2.5 * mm});
            skCircle(sketch, "E2.57.17.0", {"center": v(212.5, 61) * mm, "radius": 2.5 * mm});
            skCircle(sketch, "E2.57.18.0", {"center": v(212.5, 53) * mm, "radius": 2.5 * mm});
            skCircle(sketch, "E2.57.19.0", {"center": v(212.5, 45) * mm, "radius": 2.5 * mm});
            skCircle(sketch, "E2.57.20.0", {"center": v(212.5, 37) * mm, "radius": 2.5 * mm});
            skCircle(sketch, "E2.57.21.0", {"center": v(212.5, 29) * mm, "radius": 2.5 * mm});
            skCircle(sketch, "E2.57.22.0", {"center": v(212.5, 21) * mm, "radius": 2.5 * mm});
            skCircle(sketch, "E2.57.23.0", {"center": v(212.5, 13) * mm, "radius": 2.5 * mm});
            skCircle(sketch, "E2.57.24.0", {"center": v(212.5, 5) * mm, "radius": 2.5 * mm});
            skCircle(sketch, "E2.57.25.0", {"center": v(212.5, -3) * mm, "radius": 2.5 * mm});
            skCircle(sketch, "E2.57.26.0", {"center": v(212.5, -11) * mm, "radius": 2.5 * mm});
            skCircle(sketch, "E2.57.27.0", {"center": v(212.5, -19) * mm, "radius": 2.5 * mm});
            skCircle(sketch, "E2.57.28.0", {"center": v(212.5, -27) * mm, "radius": 2.5 * mm});
            skCircle(sketch, "E2.57.29.0", {"center": v(212.5, -35) * mm, "radius": 2.5 * mm});
            skCircle(sketch, "E2.57.30.0", {"center": v(212.5, -43) * mm, "radius": 2.5 * mm});
            skCircle(sketch, "E2.57.31.0", {"center": v(212.5, -51) * mm, "radius": 2.5 * mm});
            skCircle(sketch, "E2.57.32.0", {"center": v(212.5, -59) * mm, "radius": 2.5 * mm});
            skCircle(sketch, "E2.57.33.0", {"center": v(212.5, -67) * mm, "radius": 2.5 * mm});
            skCircle(sketch, "E2.57.34.0", {"center": v(212.5, -75) * mm, "radius": 2.5 * mm});
            skCircle(sketch, "E2.57.35.0", {"center": v(212.5, -83) * mm, "radius": 2.5 * mm});
            skCircle(sketch, "E2.57.36.0", {"center": v(212.5, -91) * mm, "radius": 2.5 * mm});
            skCircle(sketch, "E2.57.37.0", {"center": v(212.5, -99) * mm, "radius": 2.5 * mm});
            skCircle(sketch, "E2.57.38.0", {"center": v(212.5, -107) * mm, "radius": 2.5 * mm});
            skCircle(sketch, "E2.57.39.0", {"center": v(212.5, -115) * mm, "radius": 2.5 * mm});
            skCircle(sketch, "E2.57.40.0", {"center": v(212.5, -123) * mm, "radius": 2.5 * mm});
            skCircle(sketch, "E2.57.41.0", {"center": v(212.5, -131) * mm, "radius": 2.5 * mm});
            skCircle(sketch, "E2.57.42.0", {"center": v(212.5, -139) * mm, "radius": 2.5 * mm});
            skCircle(sketch, "E2.57.43.0", {"center": v(212.5, -147) * mm, "radius": 2.5 * mm});
            skCircle(sketch, "E2.57.44.0", {"center": v(212.5, -155) * mm, "radius": 2.5 * mm});
            skCircle(sketch, "E2.57.45.0", {"center": v(212.5, -163) * mm, "radius": 2.5 * mm});
            skCircle(sketch, "E2.57.46.0", {"center": v(212.5, -171) * mm, "radius": 2.5 * mm});
            skCircle(sketch, "E2.57.47.0", {"center": v(212.5, -179) * mm, "radius": 2.5 * mm});
            skCircle(sketch, "E2.57.48.0", {"center": v(212.5, -187) * mm, "radius": 2.5 * mm});
            skCircle(sketch, "E2.57.49.0", {"center": v(212.5, -195) * mm, "radius": 2.5 * mm});
            skCircle(sketch, "E2.58.0.0", {"center": v(220.5, 197) * mm, "radius": 2.5 * mm});
            skCircle(sketch, "E2.58.1.0", {"center": v(220.5, 189) * mm, "radius": 2.5 * mm});
            skCircle(sketch, "E2.58.2.0", {"center": v(220.5, 181) * mm, "radius": 2.5 * mm});
            skCircle(sketch, "E2.58.3.0", {"center": v(220.5, 173) * mm, "radius": 2.5 * mm});
            skCircle(sketch, "E2.58.4.0", {"center": v(220.5, 165) * mm, "radius": 2.5 * mm});
            skCircle(sketch, "E2.58.5.0", {"center": v(220.5, 157) * mm, "radius": 2.5 * mm});
            skCircle(sketch, "E2.58.6.0", {"center": v(220.5, 149) * mm, "radius": 2.5 * mm});
            skCircle(sketch, "E2.58.7.0", {"center": v(220.5, 141) * mm, "radius": 2.5 * mm});
            skCircle(sketch, "E2.58.8.0", {"center": v(220.5, 133) * mm, "radius": 2.5 * mm});
            skCircle(sketch, "E2.58.9.0", {"center": v(220.5, 125) * mm, "radius": 2.5 * mm});
            skCircle(sketch, "E2.58.10.0", {"center": v(220.5, 117) * mm, "radius": 2.5 * mm});
            skCircle(sketch, "E2.58.11.0", {"center": v(220.5, 109) * mm, "radius": 2.5 * mm});
            skCircle(sketch, "E2.58.12.0", {"center": v(220.5, 101) * mm, "radius": 2.5 * mm});
            skCircle(sketch, "E2.58.13.0", {"center": v(220.5, 93) * mm, "radius": 2.5 * mm});
            skCircle(sketch, "E2.58.14.0", {"center": v(220.5, 85) * mm, "radius": 2.5 * mm});
            skCircle(sketch, "E2.58.15.0", {"center": v(220.5, 77) * mm, "radius": 2.5 * mm});
            skCircle(sketch, "E2.58.16.0", {"center": v(220.5, 69) * mm, "radius": 2.5 * mm});
            skCircle(sketch, "E2.58.17.0", {"center": v(220.5, 61) * mm, "radius": 2.5 * mm});
            skCircle(sketch, "E2.58.18.0", {"center": v(220.5, 53) * mm, "radius": 2.5 * mm});
            skCircle(sketch, "E2.58.19.0", {"center": v(220.5, 45) * mm, "radius": 2.5 * mm});
            skCircle(sketch, "E2.58.20.0", {"center": v(220.5, 37) * mm, "radius": 2.5 * mm});
            skCircle(sketch, "E2.58.21.0", {"center": v(220.5, 29) * mm, "radius": 2.5 * mm});
            skCircle(sketch, "E2.58.22.0", {"center": v(220.5, 21) * mm, "radius": 2.5 * mm});
            skCircle(sketch, "E2.58.23.0", {"center": v(220.5, 13) * mm, "radius": 2.5 * mm});
            skCircle(sketch, "E2.58.24.0", {"center": v(220.5, 5) * mm, "radius": 2.5 * mm});
            skCircle(sketch, "E2.58.25.0", {"center": v(220.5, -3) * mm, "radius": 2.5 * mm});
            skCircle(sketch, "E2.58.26.0", {"center": v(220.5, -11) * mm, "radius": 2.5 * mm});
            skCircle(sketch, "E2.58.27.0", {"center": v(220.5, -19) * mm, "radius": 2.5 * mm});
            skCircle(sketch, "E2.58.28.0", {"center": v(220.5, -27) * mm, "radius": 2.5 * mm});
            skCircle(sketch, "E2.58.29.0", {"center": v(220.5, -35) * mm, "radius": 2.5 * mm});
            skCircle(sketch, "E2.58.30.0", {"center": v(220.5, -43) * mm, "radius": 2.5 * mm});
            skCircle(sketch, "E2.58.31.0", {"center": v(220.5, -51) * mm, "radius": 2.5 * mm});
            skCircle(sketch, "E2.58.32.0", {"center": v(220.5, -59) * mm, "radius": 2.5 * mm});
            skCircle(sketch, "E2.58.33.0", {"center": v(220.5, -67) * mm, "radius": 2.5 * mm});
            skCircle(sketch, "E2.58.34.0", {"center": v(220.5, -75) * mm, "radius": 2.5 * mm});
            skCircle(sketch, "E2.58.35.0", {"center": v(220.5, -83) * mm, "radius": 2.5 * mm});
            skCircle(sketch, "E2.58.36.0", {"center": v(220.5, -91) * mm, "radius": 2.5 * mm});
            skCircle(sketch, "E2.58.37.0", {"center": v(220.5, -99) * mm, "radius": 2.5 * mm});
            skCircle(sketch, "E2.58.38.0", {"center": v(220.5, -107) * mm, "radius": 2.5 * mm});
            skCircle(sketch, "E2.58.39.0", {"center": v(220.5, -115) * mm, "radius": 2.5 * mm});
            skCircle(sketch, "E2.58.40.0", {"center": v(220.5, -123) * mm, "radius": 2.5 * mm});
            skCircle(sketch, "E2.58.41.0", {"center": v(220.5, -131) * mm, "radius": 2.5 * mm});
            skCircle(sketch, "E2.58.42.0", {"center": v(220.5, -139) * mm, "radius": 2.5 * mm});
            skCircle(sketch, "E2.58.43.0", {"center": v(220.5, -147) * mm, "radius": 2.5 * mm});
            skCircle(sketch, "E2.58.44.0", {"center": v(220.5, -155) * mm, "radius": 2.5 * mm});
            skCircle(sketch, "E2.58.45.0", {"center": v(220.5, -163) * mm, "radius": 2.5 * mm});
            skCircle(sketch, "E2.58.46.0", {"center": v(220.5, -171) * mm, "radius": 2.5 * mm});
            skCircle(sketch, "E2.58.47.0", {"center": v(220.5, -179) * mm, "radius": 2.5 * mm});
            skCircle(sketch, "E2.58.48.0", {"center": v(220.5, -187) * mm, "radius": 2.5 * mm});
            skCircle(sketch, "E2.58.49.0", {"center": v(220.5, -195) * mm, "radius": 2.5 * mm});
            skCircle(sketch, "E2.59.0.0", {"center": v(228.5, 197) * mm, "radius": 2.5 * mm});
            skCircle(sketch, "E2.59.1.0", {"center": v(228.5, 189) * mm, "radius": 2.5 * mm});
            skCircle(sketch, "E2.59.2.0", {"center": v(228.5, 181) * mm, "radius": 2.5 * mm});
            skCircle(sketch, "E2.59.3.0", {"center": v(228.5, 173) * mm, "radius": 2.5 * mm});
            skCircle(sketch, "E2.59.4.0", {"center": v(228.5, 165) * mm, "radius": 2.5 * mm});
            skCircle(sketch, "E2.59.5.0", {"center": v(228.5, 157) * mm, "radius": 2.5 * mm});
            skCircle(sketch, "E2.59.6.0", {"center": v(228.5, 149) * mm, "radius": 2.5 * mm});
            skCircle(sketch, "E2.59.7.0", {"center": v(228.5, 141) * mm, "radius": 2.5 * mm});
            skCircle(sketch, "E2.59.8.0", {"center": v(228.5, 133) * mm, "radius": 2.5 * mm});
            skCircle(sketch, "E2.59.9.0", {"center": v(228.5, 125) * mm, "radius": 2.5 * mm});
            skCircle(sketch, "E2.59.10.0", {"center": v(228.5, 117) * mm, "radius": 2.5 * mm});
            skCircle(sketch, "E2.59.11.0", {"center": v(228.5, 109) * mm, "radius": 2.5 * mm});
            skCircle(sketch, "E2.59.12.0", {"center": v(228.5, 101) * mm, "radius": 2.5 * mm});
            skCircle(sketch, "E2.59.13.0", {"center": v(228.5, 93) * mm, "radius": 2.5 * mm});
            skCircle(sketch, "E2.59.14.0", {"center": v(228.5, 85) * mm, "radius": 2.5 * mm});
            skCircle(sketch, "E2.59.15.0", {"center": v(228.5, 77) * mm, "radius": 2.5 * mm});
            skCircle(sketch, "E2.59.16.0", {"center": v(228.5, 69) * mm, "radius": 2.5 * mm});
            skCircle(sketch, "E2.59.17.0", {"center": v(228.5, 61) * mm, "radius": 2.5 * mm});
            skCircle(sketch, "E2.59.18.0", {"center": v(228.5, 53) * mm, "radius": 2.5 * mm});
            skCircle(sketch, "E2.59.19.0", {"center": v(228.5, 45) * mm, "radius": 2.5 * mm});
            skCircle(sketch, "E2.59.20.0", {"center": v(228.5, 37) * mm, "radius": 2.5 * mm});
            skCircle(sketch, "E2.59.21.0", {"center": v(228.5, 29) * mm, "radius": 2.5 * mm});
            skCircle(sketch, "E2.59.22.0", {"center": v(228.5, 21) * mm, "radius": 2.5 * mm});
            skCircle(sketch, "E2.59.23.0", {"center": v(228.5, 13) * mm, "radius": 2.5 * mm});
            skCircle(sketch, "E2.59.24.0", {"center": v(228.5, 5) * mm, "radius": 2.5 * mm});
            skCircle(sketch, "E2.59.25.0", {"center": v(228.5, -3) * mm, "radius": 2.5 * mm});
            skCircle(sketch, "E2.59.26.0", {"center": v(228.5, -11) * mm, "radius": 2.5 * mm});
            skCircle(sketch, "E2.59.27.0", {"center": v(228.5, -19) * mm, "radius": 2.5 * mm});
            skCircle(sketch, "E2.59.28.0", {"center": v(228.5, -27) * mm, "radius": 2.5 * mm});
            skCircle(sketch, "E2.59.29.0", {"center": v(228.5, -35) * mm, "radius": 2.5 * mm});
            skCircle(sketch, "E2.59.30.0", {"center": v(228.5, -43) * mm, "radius": 2.5 * mm});
            skCircle(sketch, "E2.59.31.0", {"center": v(228.5, -51) * mm, "radius": 2.5 * mm});
            skCircle(sketch, "E2.59.32.0", {"center": v(228.5, -59) * mm, "radius": 2.5 * mm});
            skCircle(sketch, "E2.59.33.0", {"center": v(228.5, -67) * mm, "radius": 2.5 * mm});
            skCircle(sketch, "E2.59.34.0", {"center": v(228.5, -75) * mm, "radius": 2.5 * mm});
            skCircle(sketch, "E2.59.35.0", {"center": v(228.5, -83) * mm, "radius": 2.5 * mm});
            skCircle(sketch, "E2.59.36.0", {"center": v(228.5, -91) * mm, "radius": 2.5 * mm});
            skCircle(sketch, "E2.59.37.0", {"center": v(228.5, -99) * mm, "radius": 2.5 * mm});
            skCircle(sketch, "E2.59.38.0", {"center": v(228.5, -107) * mm, "radius": 2.5 * mm});
            skCircle(sketch, "E2.59.39.0", {"center": v(228.5, -115) * mm, "radius": 2.5 * mm});
            skCircle(sketch, "E2.59.40.0", {"center": v(228.5, -123) * mm, "radius": 2.5 * mm});
            skCircle(sketch, "E2.59.41.0", {"center": v(228.5, -131) * mm, "radius": 2.5 * mm});
            skCircle(sketch, "E2.59.42.0", {"center": v(228.5, -139) * mm, "radius": 2.5 * mm});
            skCircle(sketch, "E2.59.43.0", {"center": v(228.5, -147) * mm, "radius": 2.5 * mm});
            skCircle(sketch, "E2.59.44.0", {"center": v(228.5, -155) * mm, "radius": 2.5 * mm});
            skCircle(sketch, "E2.59.45.0", {"center": v(228.5, -163) * mm, "radius": 2.5 * mm});
            skCircle(sketch, "E2.59.46.0", {"center": v(228.5, -171) * mm, "radius": 2.5 * mm});
            skCircle(sketch, "E2.59.47.0", {"center": v(228.5, -179) * mm, "radius": 2.5 * mm});
            skCircle(sketch, "E2.59.48.0", {"center": v(228.5, -187) * mm, "radius": 2.5 * mm});
            skCircle(sketch, "E2.59.49.0", {"center": v(228.5, -195) * mm, "radius": 2.5 * mm});
            skLineSegment(sketch, "E2.direction1", {"start": v(-243.5, 197) * mm, "end": v(-235.5, 197) * mm, "construction": true});
            skLineSegment(sketch, "E2.direction2", {"start": v(-243.5, 197) * mm, "end": v(-243.5, 189) * mm, "construction": true});
            skCircle(sketch, "E3.0.60.0", {"center": v(236.5, 197) * mm, "radius": 2.5 * mm});
            skCircle(sketch, "E3.0.60.1", {"center": v(236.5, 189) * mm, "radius": 2.5 * mm});
            skCircle(sketch, "E3.0.60.2", {"center": v(236.5, 181) * mm, "radius": 2.5 * mm});
            skCircle(sketch, "E3.0.60.3", {"center": v(236.5, 173) * mm, "radius": 2.5 * mm});
            skCircle(sketch, "E3.0.60.4", {"center": v(236.5, 165) * mm, "radius": 2.5 * mm});
            skCircle(sketch, "E3.0.60.5", {"center": v(236.5, 157) * mm, "radius": 2.5 * mm});
            skCircle(sketch, "E3.0.60.6", {"center": v(236.5, 149) * mm, "radius": 2.5 * mm});
            skCircle(sketch, "E3.0.60.7", {"center": v(236.5, 141) * mm, "radius": 2.5 * mm});
            skCircle(sketch, "E3.0.60.8", {"center": v(236.5, 133) * mm, "radius": 2.5 * mm});
            skCircle(sketch, "E3.0.60.9", {"center": v(236.5, 125) * mm, "radius": 2.5 * mm});
            skCircle(sketch, "E3.0.60.10", {"center": v(236.5, 117) * mm, "radius": 2.5 * mm});
            skCircle(sketch, "E3.0.60.11", {"center": v(236.5, 109) * mm, "radius": 2.5 * mm});
            skCircle(sketch, "E3.0.60.12", {"center": v(236.5, 101) * mm, "radius": 2.5 * mm});
            skCircle(sketch, "E3.0.60.13", {"center": v(236.5, 93) * mm, "radius": 2.5 * mm});
            skCircle(sketch, "E3.0.60.14", {"center": v(236.5, 85) * mm, "radius": 2.5 * mm});
            skCircle(sketch, "E3.0.60.15", {"center": v(236.5, 77) * mm, "radius": 2.5 * mm});
            skCircle(sketch, "E3.0.60.16", {"center": v(236.5, 69) * mm, "radius": 2.5 * mm});
            skCircle(sketch, "E3.0.60.17", {"center": v(236.5, 61) * mm, "radius": 2.5 * mm});
            skCircle(sketch, "E3.0.60.18", {"center": v(236.5, 53) * mm, "radius": 2.5 * mm});
            skCircle(sketch, "E3.0.60.19", {"center": v(236.5, 45) * mm, "radius": 2.5 * mm});
            skCircle(sketch, "E3.0.60.20", {"center": v(236.5, 37) * mm, "radius": 2.5 * mm});
            skCircle(sketch, "E3.0.60.21", {"center": v(236.5, 29) * mm, "radius": 2.5 * mm});
            skCircle(sketch, "E3.0.60.22", {"center": v(236.5, 21) * mm, "radius": 2.5 * mm});
            skCircle(sketch, "E3.0.60.23", {"center": v(236.5, 13) * mm, "radius": 2.5 * mm});
            skCircle(sketch, "E3.0.60.24", {"center": v(236.5, 5) * mm, "radius": 2.5 * mm});
            skCircle(sketch, "E3.0.60.25", {"center": v(236.5, -3) * mm, "radius": 2.5 * mm});
            skCircle(sketch, "E3.0.60.26", {"center": v(236.5, -11) * mm, "radius": 2.5 * mm});
            skCircle(sketch, "E3.0.60.27", {"center": v(236.5, -19) * mm, "radius": 2.5 * mm});
            skCircle(sketch, "E3.0.60.28", {"center": v(236.5, -27) * mm, "radius": 2.5 * mm});
            skCircle(sketch, "E3.0.60.29", {"center": v(236.5, -35) * mm, "radius": 2.5 * mm});
            skCircle(sketch, "E3.0.60.30", {"center": v(236.5, -43) * mm, "radius": 2.5 * mm});
            skCircle(sketch, "E3.0.60.31", {"center": v(236.5, -51) * mm, "radius": 2.5 * mm});
            skCircle(sketch, "E3.0.60.32", {"center": v(236.5, -59) * mm, "radius": 2.5 * mm});
            skCircle(sketch, "E3.0.60.33", {"center": v(236.5, -67) * mm, "radius": 2.5 * mm});
            skCircle(sketch, "E3.0.60.34", {"center": v(236.5, -75) * mm, "radius": 2.5 * mm});
            skCircle(sketch, "E3.0.60.35", {"center": v(236.5, -83) * mm, "radius": 2.5 * mm});
            skCircle(sketch, "E3.0.60.36", {"center": v(236.5, -91) * mm, "radius": 2.5 * mm});
            skCircle(sketch, "E3.0.60.37", {"center": v(236.5, -99) * mm, "radius": 2.5 * mm});
            skCircle(sketch, "E3.0.60.38", {"center": v(236.5, -107) * mm, "radius": 2.5 * mm});
            skCircle(sketch, "E3.0.60.39", {"center": v(236.5, -115) * mm, "radius": 2.5 * mm});
            skCircle(sketch, "E3.0.60.40", {"center": v(236.5, -123) * mm, "radius": 2.5 * mm});
            skCircle(sketch, "E3.0.60.41", {"center": v(236.5, -131) * mm, "radius": 2.5 * mm});
            skCircle(sketch, "E3.0.60.42", {"center": v(236.5, -139) * mm, "radius": 2.5 * mm});
            skCircle(sketch, "E3.0.60.43", {"center": v(236.5, -147) * mm, "radius": 2.5 * mm});
            skCircle(sketch, "E3.0.60.44", {"center": v(236.5, -155) * mm, "radius": 2.5 * mm});
            skCircle(sketch, "E3.0.60.45", {"center": v(236.5, -163) * mm, "radius": 2.5 * mm});
            skCircle(sketch, "E3.0.60.46", {"center": v(236.5, -171) * mm, "radius": 2.5 * mm});
            skCircle(sketch, "E3.0.60.47", {"center": v(236.5, -179) * mm, "radius": 2.5 * mm});
            skCircle(sketch, "E3.0.60.48", {"center": v(236.5, -187) * mm, "radius": 2.5 * mm});
            skCircle(sketch, "E3.0.60.49", {"center": v(236.5, -195) * mm, "radius": 2.5 * mm});
            skCircle(sketch, "E3.0.61.0", {"center": v(244.5, 197) * mm, "radius": 2.5 * mm});
            skCircle(sketch, "E3.0.61.1", {"center": v(244.5, 189) * mm, "radius": 2.5 * mm});
            skCircle(sketch, "E3.0.61.2", {"center": v(244.5, 181) * mm, "radius": 2.5 * mm});
            skCircle(sketch, "E3.0.61.3", {"center": v(244.5, 173) * mm, "radius": 2.5 * mm});
            skCircle(sketch, "E3.0.61.4", {"center": v(244.5, 165) * mm, "radius": 2.5 * mm});
            skCircle(sketch, "E3.0.61.5", {"center": v(244.5, 157) * mm, "radius": 2.5 * mm});
            skCircle(sketch, "E3.0.61.6", {"center": v(244.5, 149) * mm, "radius": 2.5 * mm});
            skCircle(sketch, "E3.0.61.7", {"center": v(244.5, 141) * mm, "radius": 2.5 * mm});
            skCircle(sketch, "E3.0.61.8", {"center": v(244.5, 133) * mm, "radius": 2.5 * mm});
            skCircle(sketch, "E3.0.61.9", {"center": v(244.5, 125) * mm, "radius": 2.5 * mm});
            skCircle(sketch, "E3.0.61.10", {"center": v(244.5, 117) * mm, "radius": 2.5 * mm});
            skCircle(sketch, "E3.0.61.11", {"center": v(244.5, 109) * mm, "radius": 2.5 * mm});
            skCircle(sketch, "E3.0.61.12", {"center": v(244.5, 101) * mm, "radius": 2.5 * mm});
            skCircle(sketch, "E3.0.61.13", {"center": v(244.5, 93) * mm, "radius": 2.5 * mm});
            skCircle(sketch, "E3.0.61.14", {"center": v(244.5, 85) * mm, "radius": 2.5 * mm});
            skCircle(sketch, "E3.0.61.15", {"center": v(244.5, 77) * mm, "radius": 2.5 * mm});
            skCircle(sketch, "E3.0.61.16", {"center": v(244.5, 69) * mm, "radius": 2.5 * mm});
            skCircle(sketch, "E3.0.61.17", {"center": v(244.5, 61) * mm, "radius": 2.5 * mm});
            skCircle(sketch, "E3.0.61.18", {"center": v(244.5, 53) * mm, "radius": 2.5 * mm});
            skCircle(sketch, "E3.0.61.19", {"center": v(244.5, 45) * mm, "radius": 2.5 * mm});
            skCircle(sketch, "E3.0.61.20", {"center": v(244.5, 37) * mm, "radius": 2.5 * mm});
            skCircle(sketch, "E3.0.61.21", {"center": v(244.5, 29) * mm, "radius": 2.5 * mm});
            skCircle(sketch, "E3.0.61.22", {"center": v(244.5, 21) * mm, "radius": 2.5 * mm});
            skCircle(sketch, "E3.0.61.23", {"center": v(244.5, 13) * mm, "radius": 2.5 * mm});
            skCircle(sketch, "E3.0.61.24", {"center": v(244.5, 5) * mm, "radius": 2.5 * mm});
            skCircle(sketch, "E3.0.61.25", {"center": v(244.5, -3) * mm, "radius": 2.5 * mm});
            skCircle(sketch, "E3.0.61.26", {"center": v(244.5, -11) * mm, "radius": 2.5 * mm});
            skCircle(sketch, "E3.0.61.27", {"center": v(244.5, -19) * mm, "radius": 2.5 * mm});
            skCircle(sketch, "E3.0.61.28", {"center": v(244.5, -27) * mm, "radius": 2.5 * mm});
            skCircle(sketch, "E3.0.61.29", {"center": v(244.5, -35) * mm, "radius": 2.5 * mm});
            skCircle(sketch, "E3.0.61.30", {"center": v(244.5, -43) * mm, "radius": 2.5 * mm});
            skCircle(sketch, "E3.0.61.31", {"center": v(244.5, -51) * mm, "radius": 2.5 * mm});
            skCircle(sketch, "E3.0.61.32", {"center": v(244.5, -59) * mm, "radius": 2.5 * mm});
            skCircle(sketch, "E3.0.61.33", {"center": v(244.5, -67) * mm, "radius": 2.5 * mm});
            skCircle(sketch, "E3.0.61.34", {"center": v(244.5, -75) * mm, "radius": 2.5 * mm});
            skCircle(sketch, "E3.0.61.35", {"center": v(244.5, -83) * mm, "radius": 2.5 * mm});
            skCircle(sketch, "E3.0.61.36", {"center": v(244.5, -91) * mm, "radius": 2.5 * mm});
            skCircle(sketch, "E3.0.61.37", {"center": v(244.5, -99) * mm, "radius": 2.5 * mm});
            skCircle(sketch, "E3.0.61.38", {"center": v(244.5, -107) * mm, "radius": 2.5 * mm});
            skCircle(sketch, "E3.0.61.39", {"center": v(244.5, -115) * mm, "radius": 2.5 * mm});
            skCircle(sketch, "E3.0.61.40", {"center": v(244.5, -123) * mm, "radius": 2.5 * mm});
            skCircle(sketch, "E3.0.61.41", {"center": v(244.5, -131) * mm, "radius": 2.5 * mm});
            skCircle(sketch, "E3.0.61.42", {"center": v(244.5, -139) * mm, "radius": 2.5 * mm});
            skCircle(sketch, "E3.0.61.43", {"center": v(244.5, -147) * mm, "radius": 2.5 * mm});
            skCircle(sketch, "E3.0.61.44", {"center": v(244.5, -155) * mm, "radius": 2.5 * mm});
            skCircle(sketch, "E3.0.61.45", {"center": v(244.5, -163) * mm, "radius": 2.5 * mm});
            skCircle(sketch, "E3.0.61.46", {"center": v(244.5, -171) * mm, "radius": 2.5 * mm});
            skCircle(sketch, "E3.0.61.47", {"center": v(244.5, -179) * mm, "radius": 2.5 * mm});
            skCircle(sketch, "E3.0.61.48", {"center": v(244.5, -187) * mm, "radius": 2.5 * mm});
            skCircle(sketch, "E3.0.61.49", {"center": v(244.5, -195) * mm, "radius": 2.5 * mm});
            skSolve(sketch);
        }
        {
            var Q0;
            Q0=makeQuery(id+"F0.imprint","IMPRINT",FACE,{"disambiguationData":[TD([[makeQuery(id+"F0.imprint","IMPRINT",EDGE,{"derivedFrom":sQuery(id+"F0.wireOp",EDGE,"E0.bottom")}),1.0]])]});
            extrude(context, id + "F1", {"entities" : qUnion([Q0]), "depth" : 2 * mm, "offsetDistance" : 25 * mm});
        }
        {
            var Q0;
            Q0=makeQuery(id+"F1.opExtrude","CAP_FACE",FACE,{"disambiguationData":[OSD([sQuery(id+"F0.wireOp",EDGE,"E0.bottom"),sQuery(id+"F0.wireOp",EDGE,"E0.top"),sQuery(id+"F0.wireOp",EDGE,"E0.left"),sQuery(id+"F0.wireOp",EDGE,"E0.right"),sQuery(id+"F0.wireOp",EDGE,"E1"),sQuery(id+"F0.wireOp",EDGE,"E2.0.1.0"),sQuery(id+"F0.wireOp",EDGE,"E2.0.2.0"),sQuery(id+"F0.wireOp",EDGE,"E2.0.3.0"),sQuery(id+"F0.wireOp",EDGE,"E2.0.4.0"),sQuery(id+"F0.wireOp",EDGE,"E2.0.5.0"),sQuery(id+"F0.wireOp",EDGE,"E2.0.6.0"),sQuery(id+"F0.wireOp",EDGE,"E2.0.7.0"),sQuery(id+"F0.wireOp",EDGE,"E2.0.8.0"),sQuery(id+"F0.wireOp",EDGE,"E2.0.9.0"),sQuery(id+"F0.wireOp",EDGE,"E2.0.10.0"),sQuery(id+"F0.wireOp",EDGE,"E2.0.11.0"),sQuery(id+"F0.wireOp",EDGE,"E2.0.12.0"),sQuery(id+"F0.wireOp",EDGE,"E2.0.13.0"),sQuery(id+"F0.wireOp",EDGE,"E2.0.14.0"),sQuery(id+"F0.wireOp",EDGE,"E2.0.15.0"),sQuery(id+"F0.wireOp",EDGE,"E2.0.16.0"),sQuery(id+"F0.wireOp",EDGE,"E2.0.17.0"),sQuery(id+"F0.wireOp",EDGE,"E2.0.18.0"),sQuery(id+"F0.wireOp",EDGE,"E2.0.19.0"),sQuery(id+"F0.wireOp",EDGE,"E2.0.20.0"),sQuery(id+"F0.wireOp",EDGE,"E2.0.21.0"),sQuery(id+"F0.wireOp",EDGE,"E2.0.22.0"),sQuery(id+"F0.wireOp",EDGE,"E2.0.23.0"),sQuery(id+"F0.wireOp",EDGE,"E2.0.24.0"),sQuery(id+"F0.wireOp",EDGE,"E2.0.25.0"),sQuery(id+"F0.wireOp",EDGE,"E2.0.26.0"),sQuery(id+"F0.wireOp",EDGE,"E2.0.27.0"),sQuery(id+"F0.wireOp",EDGE,"E2.0.28.0"),sQuery(id+"F0.wireOp",EDGE,"E2.0.29.0"),sQuery(id+"F0.wireOp",EDGE,"E2.0.30.0"),sQuery(id+"F0.wireOp",EDGE,"E2.0.31.0"),sQuery(id+"F0.wireOp",EDGE,"E2.0.32.0"),sQuery(id+"F0.wireOp",EDGE,"E2.0.33.0"),sQuery(id+"F0.wireOp",EDGE,"E2.0.34.0"),sQuery(id+"F0.wireOp",EDGE,"E2.0.35.0"),sQuery(id+"F0.wireOp",EDGE,"E2.0.36.0"),sQuery(id+"F0.wireOp",EDGE,"E2.0.37.0"),sQuery(id+"F0.wireOp",EDGE,"E2.0.38.0"),sQuery(id+"F0.wireOp",EDGE,"E2.0.39.0"),sQuery(id+"F0.wireOp",EDGE,"E2.0.40.0"),sQuery(id+"F0.wireOp",EDGE,"E2.0.41.0"),sQuery(id+"F0.wireOp",EDGE,"E2.0.42.0"),sQuery(id+"F0.wireOp",EDGE,"E2.0.43.0"),sQuery(id+"F0.wireOp",EDGE,"E2.0.44.0"),sQuery(id+"F0.wireOp",EDGE,"E2.0.45.0"),sQuery(id+"F0.wireOp",EDGE,"E2.0.46.0"),sQuery(id+"F0.wireOp",EDGE,"E2.0.47.0"),sQuery(id+"F0.wireOp",EDGE,"E2.0.48.0"),sQuery(id+"F0.wireOp",EDGE,"E2.0.49.0"),sQuery(id+"F0.wireOp",EDGE,"E2.1.0.0"),sQuery(id+"F0.wireOp",EDGE,"E2.1.1.0"),sQuery(id+"F0.wireOp",EDGE,"E2.1.2.0"),sQuery(id+"F0.wireOp",EDGE,"E2.1.3.0"),sQuery(id+"F0.wireOp",EDGE,"E2.1.4.0"),sQuery(id+"F0.wireOp",EDGE,"E2.1.5.0"),sQuery(id+"F0.wireOp",EDGE,"E2.1.6.0"),sQuery(id+"F0.wireOp",EDGE,"E2.1.7.0"),sQuery(id+"F0.wireOp",EDGE,"E2.1.8.0"),sQuery(id+"F0.wireOp",EDGE,"E2.1.9.0"),sQuery(id+"F0.wireOp",EDGE,"E2.1.10.0"),sQuery(id+"F0.wireOp",EDGE,"E2.1.11.0"),sQuery(id+"F0.wireOp",EDGE,"E2.1.12.0"),sQuery(id+"F0.wireOp",EDGE,"E2.1.13.0"),sQuery(id+"F0.wireOp",EDGE,"E2.1.14.0"),sQuery(id+"F0.wireOp",EDGE,"E2.1.15.0"),sQuery(id+"F0.wireOp",EDGE,"E2.1.16.0"),sQuery(id+"F0.wireOp",EDGE,"E2.1.17.0"),sQuery(id+"F0.wireOp",EDGE,"E2.1.18.0"),sQuery(id+"F0.wireOp",EDGE,"E2.1.19.0"),sQuery(id+"F0.wireOp",EDGE,"E2.1.20.0"),sQuery(id+"F0.wireOp",EDGE,"E2.1.21.0"),sQuery(id+"F0.wireOp",EDGE,"E2.1.22.0"),sQuery(id+"F0.wireOp",EDGE,"E2.1.23.0"),sQuery(id+"F0.wireOp",EDGE,"E2.1.24.0"),sQuery(id+"F0.wireOp",EDGE,"E2.1.25.0"),sQuery(id+"F0.wireOp",EDGE,"E2.1.26.0"),sQuery(id+"F0.wireOp",EDGE,"E2.1.27.0"),sQuery(id+"F0.wireOp",EDGE,"E2.1.28.0"),sQuery(id+"F0.wireOp",EDGE,"E2.1.29.0"),sQuery(id+"F0.wireOp",EDGE,"E2.1.30.0"),sQuery(id+"F0.wireOp",EDGE,"E2.1.31.0"),sQuery(id+"F0.wireOp",EDGE,"E2.1.32.0"),sQuery(id+"F0.wireOp",EDGE,"E2.1.33.0"),sQuery(id+"F0.wireOp",EDGE,"E2.1.34.0"),sQuery(id+"F0.wireOp",EDGE,"E2.1.35.0"),sQuery(id+"F0.wireOp",EDGE,"E2.1.36.0"),sQuery(id+"F0.wireOp",EDGE,"E2.1.37.0"),sQuery(id+"F0.wireOp",EDGE,"E2.1.38.0"),sQuery(id+"F0.wireOp",EDGE,"E2.1.39.0"),sQuery(id+"F0.wireOp",EDGE,"E2.1.40.0"),sQuery(id+"F0.wireOp",EDGE,"E2.1.41.0"),sQuery(id+"F0.wireOp",EDGE,"E2.1.42.0"),sQuery(id+"F0.wireOp",EDGE,"E2.1.43.0"),sQuery(id+"F0.wireOp",EDGE,"E2.1.44.0"),sQuery(id+"F0.wireOp",EDGE,"E2.1.45.0"),sQuery(id+"F0.wireOp",EDGE,"E2.1.46.0"),sQuery(id+"F0.wireOp",EDGE,"E2.1.47.0"),sQuery(id+"F0.wireOp",EDGE,"E2.1.48.0"),sQuery(id+"F0.wireOp",EDGE,"E2.1.49.0"),sQuery(id+"F0.wireOp",EDGE,"E2.2.0.0"),sQuery(id+"F0.wireOp",EDGE,"E2.2.1.0"),sQuery(id+"F0.wireOp",EDGE,"E2.2.2.0"),sQuery(id+"F0.wireOp",EDGE,"E2.2.3.0"),sQuery(id+"F0.wireOp",EDGE,"E2.2.4.0"),sQuery(id+"F0.wireOp",EDGE,"E2.2.5.0"),sQuery(id+"F0.wireOp",EDGE,"E2.2.6.0"),sQuery(id+"F0.wireOp",EDGE,"E2.2.7.0"),sQuery(id+"F0.wireOp",EDGE,"E2.2.8.0"),sQuery(id+"F0.wireOp",EDGE,"E2.2.9.0"),sQuery(id+"F0.wireOp",EDGE,"E2.2.10.0"),sQuery(id+"F0.wireOp",EDGE,"E2.2.11.0"),sQuery(id+"F0.wireOp",EDGE,"E2.2.12.0"),sQuery(id+"F0.wireOp",EDGE,"E2.2.13.0"),sQuery(id+"F0.wireOp",EDGE,"E2.2.14.0"),sQuery(id+"F0.wireOp",EDGE,"E2.2.15.0"),sQuery(id+"F0.wireOp",EDGE,"E2.2.16.0"),sQuery(id+"F0.wireOp",EDGE,"E2.2.17.0"),sQuery(id+"F0.wireOp",EDGE,"E2.2.18.0"),sQuery(id+"F0.wireOp",EDGE,"E2.2.19.0"),sQuery(id+"F0.wireOp",EDGE,"E2.2.20.0"),sQuery(id+"F0.wireOp",EDGE,"E2.2.21.0"),sQuery(id+"F0.wireOp",EDGE,"E2.2.22.0"),sQuery(id+"F0.wireOp",EDGE,"E2.2.23.0"),sQuery(id+"F0.wireOp",EDGE,"E2.2.24.0"),sQuery(id+"F0.wireOp",EDGE,"E2.2.25.0"),sQuery(id+"F0.wireOp",EDGE,"E2.2.26.0"),sQuery(id+"F0.wireOp",EDGE,"E2.2.27.0"),sQuery(id+"F0.wireOp",EDGE,"E2.2.28.0"),sQuery(id+"F0.wireOp",EDGE,"E2.2.29.0"),sQuery(id+"F0.wireOp",EDGE,"E2.2.30.0"),sQuery(id+"F0.wireOp",EDGE,"E2.2.31.0"),sQuery(id+"F0.wireOp",EDGE,"E2.2.32.0"),sQuery(id+"F0.wireOp",EDGE,"E2.2.33.0"),sQuery(id+"F0.wireOp",EDGE,"E2.2.34.0"),sQuery(id+"F0.wireOp",EDGE,"E2.2.35.0"),sQuery(id+"F0.wireOp",EDGE,"E2.2.36.0"),sQuery(id+"F0.wireOp",EDGE,"E2.2.37.0"),sQuery(id+"F0.wireOp",EDGE,"E2.2.38.0"),sQuery(id+"F0.wireOp",EDGE,"E2.2.39.0"),sQuery(id+"F0.wireOp",EDGE,"E2.2.40.0"),sQuery(id+"F0.wireOp",EDGE,"E2.2.41.0"),sQuery(id+"F0.wireOp",EDGE,"E2.2.42.0"),sQuery(id+"F0.wireOp",EDGE,"E2.2.43.0"),sQuery(id+"F0.wireOp",EDGE,"E2.2.44.0"),sQuery(id+"F0.wireOp",EDGE,"E2.2.45.0"),sQuery(id+"F0.wireOp",EDGE,"E2.2.46.0"),sQuery(id+"F0.wireOp",EDGE,"E2.2.47.0"),sQuery(id+"F0.wireOp",EDGE,"E2.2.48.0"),sQuery(id+"F0.wireOp",EDGE,"E2.2.49.0"),sQuery(id+"F0.wireOp",EDGE,"E2.3.0.0"),sQuery(id+"F0.wireOp",EDGE,"E2.3.1.0"),sQuery(id+"F0.wireOp",EDGE,"E2.3.2.0"),sQuery(id+"F0.wireOp",EDGE,"E2.3.3.0"),sQuery(id+"F0.wireOp",EDGE,"E2.3.4.0"),sQuery(id+"F0.wireOp",EDGE,"E2.3.5.0"),sQuery(id+"F0.wireOp",EDGE,"E2.3.6.0"),sQuery(id+"F0.wireOp",EDGE,"E2.3.7.0"),sQuery(id+"F0.wireOp",EDGE,"E2.3.8.0"),sQuery(id+"F0.wireOp",EDGE,"E2.3.9.0"),sQuery(id+"F0.wireOp",EDGE,"E2.3.10.0"),sQuery(id+"F0.wireOp",EDGE,"E2.3.11.0"),sQuery(id+"F0.wireOp",EDGE,"E2.3.12.0"),sQuery(id+"F0.wireOp",EDGE,"E2.3.13.0"),sQuery(id+"F0.wireOp",EDGE,"E2.3.14.0"),sQuery(id+"F0.wireOp",EDGE,"E2.3.15.0"),sQuery(id+"F0.wireOp",EDGE,"E2.3.16.0"),sQuery(id+"F0.wireOp",EDGE,"E2.3.17.0"),sQuery(id+"F0.wireOp",EDGE,"E2.3.18.0"),sQuery(id+"F0.wireOp",EDGE,"E2.3.19.0"),sQuery(id+"F0.wireOp",EDGE,"E2.3.20.0"),sQuery(id+"F0.wireOp",EDGE,"E2.3.21.0"),sQuery(id+"F0.wireOp",EDGE,"E2.3.22.0"),sQuery(id+"F0.wireOp",EDGE,"E2.3.23.0"),sQuery(id+"F0.wireOp",EDGE,"E2.3.24.0"),sQuery(id+"F0.wireOp",EDGE,"E2.3.25.0"),sQuery(id+"F0.wireOp",EDGE,"E2.3.26.0"),sQuery(id+"F0.wireOp",EDGE,"E2.3.27.0"),sQuery(id+"F0.wireOp",EDGE,"E2.3.28.0"),sQuery(id+"F0.wireOp",EDGE,"E2.3.29.0"),sQuery(id+"F0.wireOp",EDGE,"E2.3.30.0"),sQuery(id+"F0.wireOp",EDGE,"E2.3.31.0"),sQuery(id+"F0.wireOp",EDGE,"E2.3.32.0"),sQuery(id+"F0.wireOp",EDGE,"E2.3.33.0"),sQuery(id+"F0.wireOp",EDGE,"E2.3.34.0"),sQuery(id+"F0.wireOp",EDGE,"E2.3.35.0"),sQuery(id+"F0.wireOp",EDGE,"E2.3.36.0"),sQuery(id+"F0.wireOp",EDGE,"E2.3.37.0"),sQuery(id+"F0.wireOp",EDGE,"E2.3.38.0"),sQuery(id+"F0.wireOp",EDGE,"E2.3.39.0"),sQuery(id+"F0.wireOp",EDGE,"E2.3.40.0"),sQuery(id+"F0.wireOp",EDGE,"E2.3.41.0"),sQuery(id+"F0.wireOp",EDGE,"E2.3.42.0"),sQuery(id+"F0.wireOp",EDGE,"E2.3.43.0"),sQuery(id+"F0.wireOp",EDGE,"E2.3.44.0"),sQuery(id+"F0.wireOp",EDGE,"E2.3.45.0"),sQuery(id+"F0.wireOp",EDGE,"E2.3.46.0"),sQuery(id+"F0.wireOp",EDGE,"E2.3.47.0"),sQuery(id+"F0.wireOp",EDGE,"E2.3.48.0"),sQuery(id+"F0.wireOp",EDGE,"E2.3.49.0"),sQuery(id+"F0.wireOp",EDGE,"E2.4.0.0"),sQuery(id+"F0.wireOp",EDGE,"E2.4.1.0"),sQuery(id+"F0.wireOp",EDGE,"E2.4.2.0"),sQuery(id+"F0.wireOp",EDGE,"E2.4.3.0"),sQuery(id+"F0.wireOp",EDGE,"E2.4.4.0"),sQuery(id+"F0.wireOp",EDGE,"E2.4.5.0"),sQuery(id+"F0.wireOp",EDGE,"E2.4.6.0"),sQuery(id+"F0.wireOp",EDGE,"E2.4.7.0"),sQuery(id+"F0.wireOp",EDGE,"E2.4.8.0"),sQuery(id+"F0.wireOp",EDGE,"E2.4.9.0"),sQuery(id+"F0.wireOp",EDGE,"E2.4.10.0"),sQuery(id+"F0.wireOp",EDGE,"E2.4.11.0"),sQuery(id+"F0.wireOp",EDGE,"E2.4.12.0"),sQuery(id+"F0.wireOp",EDGE,"E2.4.13.0"),sQuery(id+"F0.wireOp",EDGE,"E2.4.14.0"),sQuery(id+"F0.wireOp",EDGE,"E2.4.15.0"),sQuery(id+"F0.wireOp",EDGE,"E2.4.16.0"),sQuery(id+"F0.wireOp",EDGE,"E2.4.17.0"),sQuery(id+"F0.wireOp",EDGE,"E2.4.18.0"),sQuery(id+"F0.wireOp",EDGE,"E2.4.19.0"),sQuery(id+"F0.wireOp",EDGE,"E2.4.20.0"),sQuery(id+"F0.wireOp",EDGE,"E2.4.21.0"),sQuery(id+"F0.wireOp",EDGE,"E2.4.22.0"),sQuery(id+"F0.wireOp",EDGE,"E2.4.23.0"),sQuery(id+"F0.wireOp",EDGE,"E2.4.24.0"),sQuery(id+"F0.wireOp",EDGE,"E2.4.25.0"),sQuery(id+"F0.wireOp",EDGE,"E2.4.26.0"),sQuery(id+"F0.wireOp",EDGE,"E2.4.27.0"),sQuery(id+"F0.wireOp",EDGE,"E2.4.28.0"),sQuery(id+"F0.wireOp",EDGE,"E2.4.29.0"),sQuery(id+"F0.wireOp",EDGE,"E2.4.30.0"),sQuery(id+"F0.wireOp",EDGE,"E2.4.31.0"),sQuery(id+"F0.wireOp",EDGE,"E2.4.32.0"),sQuery(id+"F0.wireOp",EDGE,"E2.4.33.0"),sQuery(id+"F0.wireOp",EDGE,"E2.4.34.0"),sQuery(id+"F0.wireOp",EDGE,"E2.4.35.0"),sQuery(id+"F0.wireOp",EDGE,"E2.4.36.0"),sQuery(id+"F0.wireOp",EDGE,"E2.4.37.0"),sQuery(id+"F0.wireOp",EDGE,"E2.4.38.0"),sQuery(id+"F0.wireOp",EDGE,"E2.4.39.0"),sQuery(id+"F0.wireOp",EDGE,"E2.4.40.0"),sQuery(id+"F0.wireOp",EDGE,"E2.4.41.0"),sQuery(id+"F0.wireOp",EDGE,"E2.4.42.0"),sQuery(id+"F0.wireOp",EDGE,"E2.4.43.0"),sQuery(id+"F0.wireOp",EDGE,"E2.4.44.0"),sQuery(id+"F0.wireOp",EDGE,"E2.4.45.0"),sQuery(id+"F0.wireOp",EDGE,"E2.4.46.0"),sQuery(id+"F0.wireOp",EDGE,"E2.4.47.0"),sQuery(id+"F0.wireOp",EDGE,"E2.4.48.0"),sQuery(id+"F0.wireOp",EDGE,"E2.4.49.0"),sQuery(id+"F0.wireOp",EDGE,"E2.5.0.0"),sQuery(id+"F0.wireOp",EDGE,"E2.5.1.0"),sQuery(id+"F0.wireOp",EDGE,"E2.5.2.0"),sQuery(id+"F0.wireOp",EDGE,"E2.5.3.0"),sQuery(id+"F0.wireOp",EDGE,"E2.5.4.0"),sQuery(id+"F0.wireOp",EDGE,"E2.5.5.0"),sQuery(id+"F0.wireOp",EDGE,"E2.5.6.0"),sQuery(id+"F0.wireOp",EDGE,"E2.5.7.0"),sQuery(id+"F0.wireOp",EDGE,"E2.5.8.0"),sQuery(id+"F0.wireOp",EDGE,"E2.5.9.0"),sQuery(id+"F0.wireOp",EDGE,"E2.5.10.0"),sQuery(id+"F0.wireOp",EDGE,"E2.5.11.0"),sQuery(id+"F0.wireOp",EDGE,"E2.5.12.0"),sQuery(id+"F0.wireOp",EDGE,"E2.5.13.0"),sQuery(id+"F0.wireOp",EDGE,"E2.5.14.0"),sQuery(id+"F0.wireOp",EDGE,"E2.5.15.0"),sQuery(id+"F0.wireOp",EDGE,"E2.5.16.0"),sQuery(id+"F0.wireOp",EDGE,"E2.5.17.0"),sQuery(id+"F0.wireOp",EDGE,"E2.5.18.0"),sQuery(id+"F0.wireOp",EDGE,"E2.5.19.0"),sQuery(id+"F0.wireOp",EDGE,"E2.5.20.0"),sQuery(id+"F0.wireOp",EDGE,"E2.5.21.0"),sQuery(id+"F0.wireOp",EDGE,"E2.5.22.0"),sQuery(id+"F0.wireOp",EDGE,"E2.5.23.0"),sQuery(id+"F0.wireOp",EDGE,"E2.5.24.0"),sQuery(id+"F0.wireOp",EDGE,"E2.5.25.0"),sQuery(id+"F0.wireOp",EDGE,"E2.5.26.0"),sQuery(id+"F0.wireOp",EDGE,"E2.5.27.0"),sQuery(id+"F0.wireOp",EDGE,"E2.5.28.0"),sQuery(id+"F0.wireOp",EDGE,"E2.5.29.0"),sQuery(id+"F0.wireOp",EDGE,"E2.5.30.0"),sQuery(id+"F0.wireOp",EDGE,"E2.5.31.0"),sQuery(id+"F0.wireOp",EDGE,"E2.5.32.0"),sQuery(id+"F0.wireOp",EDGE,"E2.5.33.0"),sQuery(id+"F0.wireOp",EDGE,"E2.5.34.0"),sQuery(id+"F0.wireOp",EDGE,"E2.5.35.0"),sQuery(id+"F0.wireOp",EDGE,"E2.5.36.0"),sQuery(id+"F0.wireOp",EDGE,"E2.5.37.0"),sQuery(id+"F0.wireOp",EDGE,"E2.5.38.0"),sQuery(id+"F0.wireOp",EDGE,"E2.5.39.0"),sQuery(id+"F0.wireOp",EDGE,"E2.5.40.0"),sQuery(id+"F0.wireOp",EDGE,"E2.5.41.0"),sQuery(id+"F0.wireOp",EDGE,"E2.5.42.0"),sQuery(id+"F0.wireOp",EDGE,"E2.5.43.0"),sQuery(id+"F0.wireOp",EDGE,"E2.5.44.0"),sQuery(id+"F0.wireOp",EDGE,"E2.5.45.0"),sQuery(id+"F0.wireOp",EDGE,"E2.5.46.0"),sQuery(id+"F0.wireOp",EDGE,"E2.5.47.0"),sQuery(id+"F0.wireOp",EDGE,"E2.5.48.0"),sQuery(id+"F0.wireOp",EDGE,"E2.5.49.0"),sQuery(id+"F0.wireOp",EDGE,"E2.6.0.0"),sQuery(id+"F0.wireOp",EDGE,"E2.6.1.0"),sQuery(id+"F0.wireOp",EDGE,"E2.6.2.0"),sQuery(id+"F0.wireOp",EDGE,"E2.6.3.0"),sQuery(id+"F0.wireOp",EDGE,"E2.6.4.0"),sQuery(id+"F0.wireOp",EDGE,"E2.6.5.0"),sQuery(id+"F0.wireOp",EDGE,"E2.6.6.0"),sQuery(id+"F0.wireOp",EDGE,"E2.6.7.0"),sQuery(id+"F0.wireOp",EDGE,"E2.6.8.0"),sQuery(id+"F0.wireOp",EDGE,"E2.6.9.0"),sQuery(id+"F0.wireOp",EDGE,"E2.6.10.0"),sQuery(id+"F0.wireOp",EDGE,"E2.6.11.0"),sQuery(id+"F0.wireOp",EDGE,"E2.6.12.0"),sQuery(id+"F0.wireOp",EDGE,"E2.6.13.0"),sQuery(id+"F0.wireOp",EDGE,"E2.6.14.0"),sQuery(id+"F0.wireOp",EDGE,"E2.6.15.0"),sQuery(id+"F0.wireOp",EDGE,"E2.6.16.0"),sQuery(id+"F0.wireOp",EDGE,"E2.6.17.0"),sQuery(id+"F0.wireOp",EDGE,"E2.6.18.0"),sQuery(id+"F0.wireOp",EDGE,"E2.6.19.0"),sQuery(id+"F0.wireOp",EDGE,"E2.6.20.0"),sQuery(id+"F0.wireOp",EDGE,"E2.6.21.0"),sQuery(id+"F0.wireOp",EDGE,"E2.6.22.0"),sQuery(id+"F0.wireOp",EDGE,"E2.6.23.0"),sQuery(id+"F0.wireOp",EDGE,"E2.6.24.0"),sQuery(id+"F0.wireOp",EDGE,"E2.6.25.0"),sQuery(id+"F0.wireOp",EDGE,"E2.6.26.0"),sQuery(id+"F0.wireOp",EDGE,"E2.6.27.0"),sQuery(id+"F0.wireOp",EDGE,"E2.6.28.0"),sQuery(id+"F0.wireOp",EDGE,"E2.6.29.0"),sQuery(id+"F0.wireOp",EDGE,"E2.6.30.0"),sQuery(id+"F0.wireOp",EDGE,"E2.6.31.0"),sQuery(id+"F0.wireOp",EDGE,"E2.6.32.0"),sQuery(id+"F0.wireOp",EDGE,"E2.6.33.0"),sQuery(id+"F0.wireOp",EDGE,"E2.6.34.0"),sQuery(id+"F0.wireOp",EDGE,"E2.6.35.0"),sQuery(id+"F0.wireOp",EDGE,"E2.6.36.0"),sQuery(id+"F0.wireOp",EDGE,"E2.6.37.0"),sQuery(id+"F0.wireOp",EDGE,"E2.6.38.0"),sQuery(id+"F0.wireOp",EDGE,"E2.6.39.0"),sQuery(id+"F0.wireOp",EDGE,"E2.6.40.0"),sQuery(id+"F0.wireOp",EDGE,"E2.6.41.0"),sQuery(id+"F0.wireOp",EDGE,"E2.6.42.0"),sQuery(id+"F0.wireOp",EDGE,"E2.6.43.0"),sQuery(id+"F0.wireOp",EDGE,"E2.6.44.0"),sQuery(id+"F0.wireOp",EDGE,"E2.6.45.0"),sQuery(id+"F0.wireOp",EDGE,"E2.6.46.0"),sQuery(id+"F0.wireOp",EDGE,"E2.6.47.0"),sQuery(id+"F0.wireOp",EDGE,"E2.6.48.0"),sQuery(id+"F0.wireOp",EDGE,"E2.6.49.0"),sQuery(id+"F0.wireOp",EDGE,"E2.7.0.0"),sQuery(id+"F0.wireOp",EDGE,"E2.7.1.0"),sQuery(id+"F0.wireOp",EDGE,"E2.7.2.0"),sQuery(id+"F0.wireOp",EDGE,"E2.7.3.0"),sQuery(id+"F0.wireOp",EDGE,"E2.7.4.0"),sQuery(id+"F0.wireOp",EDGE,"E2.7.5.0"),sQuery(id+"F0.wireOp",EDGE,"E2.7.6.0"),sQuery(id+"F0.wireOp",EDGE,"E2.7.7.0"),sQuery(id+"F0.wireOp",EDGE,"E2.7.8.0"),sQuery(id+"F0.wireOp",EDGE,"E2.7.9.0"),sQuery(id+"F0.wireOp",EDGE,"E2.7.10.0"),sQuery(id+"F0.wireOp",EDGE,"E2.7.11.0"),sQuery(id+"F0.wireOp",EDGE,"E2.7.12.0"),sQuery(id+"F0.wireOp",EDGE,"E2.7.13.0"),sQuery(id+"F0.wireOp",EDGE,"E2.7.14.0"),sQuery(id+"F0.wireOp",EDGE,"E2.7.15.0"),sQuery(id+"F0.wireOp",EDGE,"E2.7.16.0"),sQuery(id+"F0.wireOp",EDGE,"E2.7.17.0"),sQuery(id+"F0.wireOp",EDGE,"E2.7.18.0"),sQuery(id+"F0.wireOp",EDGE,"E2.7.19.0"),sQuery(id+"F0.wireOp",EDGE,"E2.7.20.0"),sQuery(id+"F0.wireOp",EDGE,"E2.7.21.0"),sQuery(id+"F0.wireOp",EDGE,"E2.7.22.0"),sQuery(id+"F0.wireOp",EDGE,"E2.7.23.0"),sQuery(id+"F0.wireOp",EDGE,"E2.7.24.0"),sQuery(id+"F0.wireOp",EDGE,"E2.7.25.0"),sQuery(id+"F0.wireOp",EDGE,"E2.7.26.0"),sQuery(id+"F0.wireOp",EDGE,"E2.7.27.0"),sQuery(id+"F0.wireOp",EDGE,"E2.7.28.0"),sQuery(id+"F0.wireOp",EDGE,"E2.7.29.0"),sQuery(id+"F0.wireOp",EDGE,"E2.7.30.0"),sQuery(id+"F0.wireOp",EDGE,"E2.7.31.0"),sQuery(id+"F0.wireOp",EDGE,"E2.7.32.0"),sQuery(id+"F0.wireOp",EDGE,"E2.7.33.0"),sQuery(id+"F0.wireOp",EDGE,"E2.7.34.0"),sQuery(id+"F0.wireOp",EDGE,"E2.7.35.0"),sQuery(id+"F0.wireOp",EDGE,"E2.7.36.0"),sQuery(id+"F0.wireOp",EDGE,"E2.7.37.0"),sQuery(id+"F0.wireOp",EDGE,"E2.7.38.0"),sQuery(id+"F0.wireOp",EDGE,"E2.7.39.0"),sQuery(id+"F0.wireOp",EDGE,"E2.7.40.0"),sQuery(id+"F0.wireOp",EDGE,"E2.7.41.0"),sQuery(id+"F0.wireOp",EDGE,"E2.7.42.0"),sQuery(id+"F0.wireOp",EDGE,"E2.7.43.0"),sQuery(id+"F0.wireOp",EDGE,"E2.7.44.0"),sQuery(id+"F0.wireOp",EDGE,"E2.7.45.0"),sQuery(id+"F0.wireOp",EDGE,"E2.7.46.0"),sQuery(id+"F0.wireOp",EDGE,"E2.7.47.0"),sQuery(id+"F0.wireOp",EDGE,"E2.7.48.0"),sQuery(id+"F0.wireOp",EDGE,"E2.7.49.0"),sQuery(id+"F0.wireOp",EDGE,"E2.8.0.0"),sQuery(id+"F0.wireOp",EDGE,"E2.8.1.0"),sQuery(id+"F0.wireOp",EDGE,"E2.8.2.0"),sQuery(id+"F0.wireOp",EDGE,"E2.8.3.0"),sQuery(id+"F0.wireOp",EDGE,"E2.8.4.0"),sQuery(id+"F0.wireOp",EDGE,"E2.8.5.0"),sQuery(id+"F0.wireOp",EDGE,"E2.8.6.0"),sQuery(id+"F0.wireOp",EDGE,"E2.8.7.0"),sQuery(id+"F0.wireOp",EDGE,"E2.8.8.0"),sQuery(id+"F0.wireOp",EDGE,"E2.8.9.0"),sQuery(id+"F0.wireOp",EDGE,"E2.8.10.0"),sQuery(id+"F0.wireOp",EDGE,"E2.8.11.0"),sQuery(id+"F0.wireOp",EDGE,"E2.8.12.0"),sQuery(id+"F0.wireOp",EDGE,"E2.8.13.0"),sQuery(id+"F0.wireOp",EDGE,"E2.8.14.0"),sQuery(id+"F0.wireOp",EDGE,"E2.8.15.0"),sQuery(id+"F0.wireOp",EDGE,"E2.8.16.0"),sQuery(id+"F0.wireOp",EDGE,"E2.8.17.0"),sQuery(id+"F0.wireOp",EDGE,"E2.8.18.0"),sQuery(id+"F0.wireOp",EDGE,"E2.8.19.0"),sQuery(id+"F0.wireOp",EDGE,"E2.8.20.0"),sQuery(id+"F0.wireOp",EDGE,"E2.8.21.0"),sQuery(id+"F0.wireOp",EDGE,"E2.8.22.0"),sQuery(id+"F0.wireOp",EDGE,"E2.8.23.0"),sQuery(id+"F0.wireOp",EDGE,"E2.8.24.0"),sQuery(id+"F0.wireOp",EDGE,"E2.8.25.0"),sQuery(id+"F0.wireOp",EDGE,"E2.8.26.0"),sQuery(id+"F0.wireOp",EDGE,"E2.8.27.0"),sQuery(id+"F0.wireOp",EDGE,"E2.8.28.0"),sQuery(id+"F0.wireOp",EDGE,"E2.8.29.0"),sQuery(id+"F0.wireOp",EDGE,"E2.8.30.0"),sQuery(id+"F0.wireOp",EDGE,"E2.8.31.0"),sQuery(id+"F0.wireOp",EDGE,"E2.8.32.0"),sQuery(id+"F0.wireOp",EDGE,"E2.8.33.0"),sQuery(id+"F0.wireOp",EDGE,"E2.8.34.0"),sQuery(id+"F0.wireOp",EDGE,"E2.8.35.0"),sQuery(id+"F0.wireOp",EDGE,"E2.8.36.0"),sQuery(id+"F0.wireOp",EDGE,"E2.8.37.0"),sQuery(id+"F0.wireOp",EDGE,"E2.8.38.0"),sQuery(id+"F0.wireOp",EDGE,"E2.8.39.0"),sQuery(id+"F0.wireOp",EDGE,"E2.8.40.0"),sQuery(id+"F0.wireOp",EDGE,"E2.8.41.0"),sQuery(id+"F0.wireOp",EDGE,"E2.8.42.0"),sQuery(id+"F0.wireOp",EDGE,"E2.8.43.0"),sQuery(id+"F0.wireOp",EDGE,"E2.8.44.0"),sQuery(id+"F0.wireOp",EDGE,"E2.8.45.0"),sQuery(id+"F0.wireOp",EDGE,"E2.8.46.0"),sQuery(id+"F0.wireOp",EDGE,"E2.8.47.0"),sQuery(id+"F0.wireOp",EDGE,"E2.8.48.0"),sQuery(id+"F0.wireOp",EDGE,"E2.8.49.0"),sQuery(id+"F0.wireOp",EDGE,"E2.9.0.0"),sQuery(id+"F0.wireOp",EDGE,"E2.9.1.0"),sQuery(id+"F0.wireOp",EDGE,"E2.9.2.0"),sQuery(id+"F0.wireOp",EDGE,"E2.9.3.0"),sQuery(id+"F0.wireOp",EDGE,"E2.9.4.0"),sQuery(id+"F0.wireOp",EDGE,"E2.9.5.0"),sQuery(id+"F0.wireOp",EDGE,"E2.9.6.0"),sQuery(id+"F0.wireOp",EDGE,"E2.9.7.0"),sQuery(id+"F0.wireOp",EDGE,"E2.9.8.0"),sQuery(id+"F0.wireOp",EDGE,"E2.9.9.0"),sQuery(id+"F0.wireOp",EDGE,"E2.9.10.0"),sQuery(id+"F0.wireOp",EDGE,"E2.9.11.0"),sQuery(id+"F0.wireOp",EDGE,"E2.9.12.0"),sQuery(id+"F0.wireOp",EDGE,"E2.9.13.0"),sQuery(id+"F0.wireOp",EDGE,"E2.9.14.0"),sQuery(id+"F0.wireOp",EDGE,"E2.9.15.0"),sQuery(id+"F0.wireOp",EDGE,"E2.9.16.0"),sQuery(id+"F0.wireOp",EDGE,"E2.9.17.0"),sQuery(id+"F0.wireOp",EDGE,"E2.9.18.0"),sQuery(id+"F0.wireOp",EDGE,"E2.9.19.0"),sQuery(id+"F0.wireOp",EDGE,"E2.9.20.0"),sQuery(id+"F0.wireOp",EDGE,"E2.9.21.0"),sQuery(id+"F0.wireOp",EDGE,"E2.9.22.0"),sQuery(id+"F0.wireOp",EDGE,"E2.9.23.0"),sQuery(id+"F0.wireOp",EDGE,"E2.9.24.0"),sQuery(id+"F0.wireOp",EDGE,"E2.9.25.0"),sQuery(id+"F0.wireOp",EDGE,"E2.9.26.0"),sQuery(id+"F0.wireOp",EDGE,"E2.9.27.0"),sQuery(id+"F0.wireOp",EDGE,"E2.9.28.0"),sQuery(id+"F0.wireOp",EDGE,"E2.9.29.0"),sQuery(id+"F0.wireOp",EDGE,"E2.9.30.0"),sQuery(id+"F0.wireOp",EDGE,"E2.9.31.0"),sQuery(id+"F0.wireOp",EDGE,"E2.9.32.0"),sQuery(id+"F0.wireOp",EDGE,"E2.9.33.0"),sQuery(id+"F0.wireOp",EDGE,"E2.9.34.0"),sQuery(id+"F0.wireOp",EDGE,"E2.9.35.0"),sQuery(id+"F0.wireOp",EDGE,"E2.9.36.0"),sQuery(id+"F0.wireOp",EDGE,"E2.9.37.0"),sQuery(id+"F0.wireOp",EDGE,"E2.9.38.0"),sQuery(id+"F0.wireOp",EDGE,"E2.9.39.0"),sQuery(id+"F0.wireOp",EDGE,"E2.9.40.0"),sQuery(id+"F0.wireOp",EDGE,"E2.9.41.0"),sQuery(id+"F0.wireOp",EDGE,"E2.9.42.0"),sQuery(id+"F0.wireOp",EDGE,"E2.9.43.0"),sQuery(id+"F0.wireOp",EDGE,"E2.9.44.0"),sQuery(id+"F0.wireOp",EDGE,"E2.9.45.0"),sQuery(id+"F0.wireOp",EDGE,"E2.9.46.0"),sQuery(id+"F0.wireOp",EDGE,"E2.9.47.0"),sQuery(id+"F0.wireOp",EDGE,"E2.9.48.0"),sQuery(id+"F0.wireOp",EDGE,"E2.9.49.0"),sQuery(id+"F0.wireOp",EDGE,"E2.10.0.0"),sQuery(id+"F0.wireOp",EDGE,"E2.10.1.0"),sQuery(id+"F0.wireOp",EDGE,"E2.10.2.0"),sQuery(id+"F0.wireOp",EDGE,"E2.10.3.0"),sQuery(id+"F0.wireOp",EDGE,"E2.10.4.0"),sQuery(id+"F0.wireOp",EDGE,"E2.10.5.0"),sQuery(id+"F0.wireOp",EDGE,"E2.10.6.0"),sQuery(id+"F0.wireOp",EDGE,"E2.10.7.0"),sQuery(id+"F0.wireOp",EDGE,"E2.10.8.0"),sQuery(id+"F0.wireOp",EDGE,"E2.10.9.0"),sQuery(id+"F0.wireOp",EDGE,"E2.10.10.0"),sQuery(id+"F0.wireOp",EDGE,"E2.10.11.0"),sQuery(id+"F0.wireOp",EDGE,"E2.10.12.0"),sQuery(id+"F0.wireOp",EDGE,"E2.10.13.0"),sQuery(id+"F0.wireOp",EDGE,"E2.10.14.0"),sQuery(id+"F0.wireOp",EDGE,"E2.10.15.0"),sQuery(id+"F0.wireOp",EDGE,"E2.10.16.0"),sQuery(id+"F0.wireOp",EDGE,"E2.10.17.0"),sQuery(id+"F0.wireOp",EDGE,"E2.10.18.0"),sQuery(id+"F0.wireOp",EDGE,"E2.10.19.0"),sQuery(id+"F0.wireOp",EDGE,"E2.10.20.0"),sQuery(id+"F0.wireOp",EDGE,"E2.10.21.0"),sQuery(id+"F0.wireOp",EDGE,"E2.10.22.0"),sQuery(id+"F0.wireOp",EDGE,"E2.10.23.0"),sQuery(id+"F0.wireOp",EDGE,"E2.10.24.0"),sQuery(id+"F0.wireOp",EDGE,"E2.10.25.0"),sQuery(id+"F0.wireOp",EDGE,"E2.10.26.0"),sQuery(id+"F0.wireOp",EDGE,"E2.10.27.0"),sQuery(id+"F0.wireOp",EDGE,"E2.10.28.0"),sQuery(id+"F0.wireOp",EDGE,"E2.10.29.0"),sQuery(id+"F0.wireOp",EDGE,"E2.10.30.0"),sQuery(id+"F0.wireOp",EDGE,"E2.10.31.0"),sQuery(id+"F0.wireOp",EDGE,"E2.10.32.0"),sQuery(id+"F0.wireOp",EDGE,"E2.10.33.0"),sQuery(id+"F0.wireOp",EDGE,"E2.10.34.0"),sQuery(id+"F0.wireOp",EDGE,"E2.10.35.0"),sQuery(id+"F0.wireOp",EDGE,"E2.10.36.0"),sQuery(id+"F0.wireOp",EDGE,"E2.10.37.0"),sQuery(id+"F0.wireOp",EDGE,"E2.10.38.0"),sQuery(id+"F0.wireOp",EDGE,"E2.10.39.0"),sQuery(id+"F0.wireOp",EDGE,"E2.10.40.0"),sQuery(id+"F0.wireOp",EDGE,"E2.10.41.0"),sQuery(id+"F0.wireOp",EDGE,"E2.10.42.0"),sQuery(id+"F0.wireOp",EDGE,"E2.10.43.0"),sQuery(id+"F0.wireOp",EDGE,"E2.10.44.0"),sQuery(id+"F0.wireOp",EDGE,"E2.10.45.0"),sQuery(id+"F0.wireOp",EDGE,"E2.10.46.0"),sQuery(id+"F0.wireOp",EDGE,"E2.10.47.0"),sQuery(id+"F0.wireOp",EDGE,"E2.10.48.0"),sQuery(id+"F0.wireOp",EDGE,"E2.10.49.0"),sQuery(id+"F0.wireOp",EDGE,"E2.11.0.0"),sQuery(id+"F0.wireOp",EDGE,"E2.11.1.0"),sQuery(id+"F0.wireOp",EDGE,"E2.11.2.0"),sQuery(id+"F0.wireOp",EDGE,"E2.11.3.0"),sQuery(id+"F0.wireOp",EDGE,"E2.11.4.0"),sQuery(id+"F0.wireOp",EDGE,"E2.11.5.0"),sQuery(id+"F0.wireOp",EDGE,"E2.11.6.0"),sQuery(id+"F0.wireOp",EDGE,"E2.11.7.0"),sQuery(id+"F0.wireOp",EDGE,"E2.11.8.0"),sQuery(id+"F0.wireOp",EDGE,"E2.11.9.0"),sQuery(id+"F0.wireOp",EDGE,"E2.11.10.0"),sQuery(id+"F0.wireOp",EDGE,"E2.11.11.0"),sQuery(id+"F0.wireOp",EDGE,"E2.11.12.0"),sQuery(id+"F0.wireOp",EDGE,"E2.11.13.0"),sQuery(id+"F0.wireOp",EDGE,"E2.11.14.0"),sQuery(id+"F0.wireOp",EDGE,"E2.11.15.0"),sQuery(id+"F0.wireOp",EDGE,"E2.11.16.0"),sQuery(id+"F0.wireOp",EDGE,"E2.11.17.0"),sQuery(id+"F0.wireOp",EDGE,"E2.11.18.0"),sQuery(id+"F0.wireOp",EDGE,"E2.11.19.0"),sQuery(id+"F0.wireOp",EDGE,"E2.11.20.0"),sQuery(id+"F0.wireOp",EDGE,"E2.11.21.0"),sQuery(id+"F0.wireOp",EDGE,"E2.11.22.0"),sQuery(id+"F0.wireOp",EDGE,"E2.11.23.0"),sQuery(id+"F0.wireOp",EDGE,"E2.11.24.0"),sQuery(id+"F0.wireOp",EDGE,"E2.11.25.0"),sQuery(id+"F0.wireOp",EDGE,"E2.11.26.0"),sQuery(id+"F0.wireOp",EDGE,"E2.11.27.0"),sQuery(id+"F0.wireOp",EDGE,"E2.11.28.0"),sQuery(id+"F0.wireOp",EDGE,"E2.11.29.0"),sQuery(id+"F0.wireOp",EDGE,"E2.11.30.0"),sQuery(id+"F0.wireOp",EDGE,"E2.11.31.0"),sQuery(id+"F0.wireOp",EDGE,"E2.11.32.0"),sQuery(id+"F0.wireOp",EDGE,"E2.11.33.0"),sQuery(id+"F0.wireOp",EDGE,"E2.11.34.0"),sQuery(id+"F0.wireOp",EDGE,"E2.11.35.0"),sQuery(id+"F0.wireOp",EDGE,"E2.11.36.0"),sQuery(id+"F0.wireOp",EDGE,"E2.11.37.0"),sQuery(id+"F0.wireOp",EDGE,"E2.11.38.0"),sQuery(id+"F0.wireOp",EDGE,"E2.11.39.0"),sQuery(id+"F0.wireOp",EDGE,"E2.11.40.0"),sQuery(id+"F0.wireOp",EDGE,"E2.11.41.0"),sQuery(id+"F0.wireOp",EDGE,"E2.11.42.0"),sQuery(id+"F0.wireOp",EDGE,"E2.11.43.0"),sQuery(id+"F0.wireOp",EDGE,"E2.11.44.0"),sQuery(id+"F0.wireOp",EDGE,"E2.11.45.0"),sQuery(id+"F0.wireOp",EDGE,"E2.11.46.0"),sQuery(id+"F0.wireOp",EDGE,"E2.11.47.0"),sQuery(id+"F0.wireOp",EDGE,"E2.11.48.0"),sQuery(id+"F0.wireOp",EDGE,"E2.11.49.0"),sQuery(id+"F0.wireOp",EDGE,"E2.12.0.0"),sQuery(id+"F0.wireOp",EDGE,"E2.12.1.0"),sQuery(id+"F0.wireOp",EDGE,"E2.12.2.0"),sQuery(id+"F0.wireOp",EDGE,"E2.12.3.0"),sQuery(id+"F0.wireOp",EDGE,"E2.12.4.0"),sQuery(id+"F0.wireOp",EDGE,"E2.12.5.0"),sQuery(id+"F0.wireOp",EDGE,"E2.12.6.0"),sQuery(id+"F0.wireOp",EDGE,"E2.12.7.0"),sQuery(id+"F0.wireOp",EDGE,"E2.12.8.0"),sQuery(id+"F0.wireOp",EDGE,"E2.12.9.0"),sQuery(id+"F0.wireOp",EDGE,"E2.12.10.0"),sQuery(id+"F0.wireOp",EDGE,"E2.12.11.0"),sQuery(id+"F0.wireOp",EDGE,"E2.12.12.0"),sQuery(id+"F0.wireOp",EDGE,"E2.12.13.0"),sQuery(id+"F0.wireOp",EDGE,"E2.12.14.0"),sQuery(id+"F0.wireOp",EDGE,"E2.12.15.0"),sQuery(id+"F0.wireOp",EDGE,"E2.12.16.0"),sQuery(id+"F0.wireOp",EDGE,"E2.12.17.0"),sQuery(id+"F0.wireOp",EDGE,"E2.12.18.0"),sQuery(id+"F0.wireOp",EDGE,"E2.12.19.0"),sQuery(id+"F0.wireOp",EDGE,"E2.12.20.0"),sQuery(id+"F0.wireOp",EDGE,"E2.12.21.0"),sQuery(id+"F0.wireOp",EDGE,"E2.12.22.0"),sQuery(id+"F0.wireOp",EDGE,"E2.12.23.0"),sQuery(id+"F0.wireOp",EDGE,"E2.12.24.0"),sQuery(id+"F0.wireOp",EDGE,"E2.12.25.0"),sQuery(id+"F0.wireOp",EDGE,"E2.12.26.0"),sQuery(id+"F0.wireOp",EDGE,"E2.12.27.0"),sQuery(id+"F0.wireOp",EDGE,"E2.12.28.0"),sQuery(id+"F0.wireOp",EDGE,"E2.12.29.0"),sQuery(id+"F0.wireOp",EDGE,"E2.12.30.0"),sQuery(id+"F0.wireOp",EDGE,"E2.12.31.0"),sQuery(id+"F0.wireOp",EDGE,"E2.12.32.0"),sQuery(id+"F0.wireOp",EDGE,"E2.12.33.0"),sQuery(id+"F0.wireOp",EDGE,"E2.12.34.0"),sQuery(id+"F0.wireOp",EDGE,"E2.12.35.0"),sQuery(id+"F0.wireOp",EDGE,"E2.12.36.0"),sQuery(id+"F0.wireOp",EDGE,"E2.12.37.0"),sQuery(id+"F0.wireOp",EDGE,"E2.12.38.0"),sQuery(id+"F0.wireOp",EDGE,"E2.12.39.0"),sQuery(id+"F0.wireOp",EDGE,"E2.12.40.0"),sQuery(id+"F0.wireOp",EDGE,"E2.12.41.0"),sQuery(id+"F0.wireOp",EDGE,"E2.12.42.0"),sQuery(id+"F0.wireOp",EDGE,"E2.12.43.0"),sQuery(id+"F0.wireOp",EDGE,"E2.12.44.0"),sQuery(id+"F0.wireOp",EDGE,"E2.12.45.0"),sQuery(id+"F0.wireOp",EDGE,"E2.12.46.0"),sQuery(id+"F0.wireOp",EDGE,"E2.12.47.0"),sQuery(id+"F0.wireOp",EDGE,"E2.12.48.0"),sQuery(id+"F0.wireOp",EDGE,"E2.12.49.0"),sQuery(id+"F0.wireOp",EDGE,"E2.13.0.0"),sQuery(id+"F0.wireOp",EDGE,"E2.13.1.0"),sQuery(id+"F0.wireOp",EDGE,"E2.13.2.0"),sQuery(id+"F0.wireOp",EDGE,"E2.13.3.0"),sQuery(id+"F0.wireOp",EDGE,"E2.13.4.0"),sQuery(id+"F0.wireOp",EDGE,"E2.13.5.0"),sQuery(id+"F0.wireOp",EDGE,"E2.13.6.0"),sQuery(id+"F0.wireOp",EDGE,"E2.13.7.0"),sQuery(id+"F0.wireOp",EDGE,"E2.13.8.0"),sQuery(id+"F0.wireOp",EDGE,"E2.13.9.0"),sQuery(id+"F0.wireOp",EDGE,"E2.13.10.0"),sQuery(id+"F0.wireOp",EDGE,"E2.13.11.0"),sQuery(id+"F0.wireOp",EDGE,"E2.13.12.0"),sQuery(id+"F0.wireOp",EDGE,"E2.13.13.0"),sQuery(id+"F0.wireOp",EDGE,"E2.13.14.0"),sQuery(id+"F0.wireOp",EDGE,"E2.13.15.0"),sQuery(id+"F0.wireOp",EDGE,"E2.13.16.0"),sQuery(id+"F0.wireOp",EDGE,"E2.13.17.0"),sQuery(id+"F0.wireOp",EDGE,"E2.13.18.0"),sQuery(id+"F0.wireOp",EDGE,"E2.13.19.0"),sQuery(id+"F0.wireOp",EDGE,"E2.13.20.0"),sQuery(id+"F0.wireOp",EDGE,"E2.13.21.0"),sQuery(id+"F0.wireOp",EDGE,"E2.13.22.0"),sQuery(id+"F0.wireOp",EDGE,"E2.13.23.0"),sQuery(id+"F0.wireOp",EDGE,"E2.13.24.0"),sQuery(id+"F0.wireOp",EDGE,"E2.13.25.0"),sQuery(id+"F0.wireOp",EDGE,"E2.13.26.0"),sQuery(id+"F0.wireOp",EDGE,"E2.13.27.0"),sQuery(id+"F0.wireOp",EDGE,"E2.13.28.0"),sQuery(id+"F0.wireOp",EDGE,"E2.13.29.0"),sQuery(id+"F0.wireOp",EDGE,"E2.13.30.0"),sQuery(id+"F0.wireOp",EDGE,"E2.13.31.0"),sQuery(id+"F0.wireOp",EDGE,"E2.13.32.0"),sQuery(id+"F0.wireOp",EDGE,"E2.13.33.0"),sQuery(id+"F0.wireOp",EDGE,"E2.13.34.0"),sQuery(id+"F0.wireOp",EDGE,"E2.13.35.0"),sQuery(id+"F0.wireOp",EDGE,"E2.13.36.0"),sQuery(id+"F0.wireOp",EDGE,"E2.13.37.0"),sQuery(id+"F0.wireOp",EDGE,"E2.13.38.0"),sQuery(id+"F0.wireOp",EDGE,"E2.13.39.0"),sQuery(id+"F0.wireOp",EDGE,"E2.13.40.0"),sQuery(id+"F0.wireOp",EDGE,"E2.13.41.0"),sQuery(id+"F0.wireOp",EDGE,"E2.13.42.0"),sQuery(id+"F0.wireOp",EDGE,"E2.13.43.0"),sQuery(id+"F0.wireOp",EDGE,"E2.13.44.0"),sQuery(id+"F0.wireOp",EDGE,"E2.13.45.0"),sQuery(id+"F0.wireOp",EDGE,"E2.13.46.0"),sQuery(id+"F0.wireOp",EDGE,"E2.13.47.0"),sQuery(id+"F0.wireOp",EDGE,"E2.13.48.0"),sQuery(id+"F0.wireOp",EDGE,"E2.13.49.0"),sQuery(id+"F0.wireOp",EDGE,"E2.14.0.0"),sQuery(id+"F0.wireOp",EDGE,"E2.14.1.0"),sQuery(id+"F0.wireOp",EDGE,"E2.14.2.0"),sQuery(id+"F0.wireOp",EDGE,"E2.14.3.0"),sQuery(id+"F0.wireOp",EDGE,"E2.14.4.0"),sQuery(id+"F0.wireOp",EDGE,"E2.14.5.0"),sQuery(id+"F0.wireOp",EDGE,"E2.14.6.0"),sQuery(id+"F0.wireOp",EDGE,"E2.14.7.0"),sQuery(id+"F0.wireOp",EDGE,"E2.14.8.0"),sQuery(id+"F0.wireOp",EDGE,"E2.14.9.0"),sQuery(id+"F0.wireOp",EDGE,"E2.14.10.0"),sQuery(id+"F0.wireOp",EDGE,"E2.14.11.0"),sQuery(id+"F0.wireOp",EDGE,"E2.14.12.0"),sQuery(id+"F0.wireOp",EDGE,"E2.14.13.0"),sQuery(id+"F0.wireOp",EDGE,"E2.14.14.0"),sQuery(id+"F0.wireOp",EDGE,"E2.14.15.0"),sQuery(id+"F0.wireOp",EDGE,"E2.14.16.0"),sQuery(id+"F0.wireOp",EDGE,"E2.14.17.0"),sQuery(id+"F0.wireOp",EDGE,"E2.14.18.0"),sQuery(id+"F0.wireOp",EDGE,"E2.14.19.0"),sQuery(id+"F0.wireOp",EDGE,"E2.14.20.0"),sQuery(id+"F0.wireOp",EDGE,"E2.14.21.0"),sQuery(id+"F0.wireOp",EDGE,"E2.14.22.0"),sQuery(id+"F0.wireOp",EDGE,"E2.14.23.0"),sQuery(id+"F0.wireOp",EDGE,"E2.14.24.0"),sQuery(id+"F0.wireOp",EDGE,"E2.14.25.0"),sQuery(id+"F0.wireOp",EDGE,"E2.14.26.0"),sQuery(id+"F0.wireOp",EDGE,"E2.14.27.0"),sQuery(id+"F0.wireOp",EDGE,"E2.14.28.0"),sQuery(id+"F0.wireOp",EDGE,"E2.14.29.0"),sQuery(id+"F0.wireOp",EDGE,"E2.14.30.0"),sQuery(id+"F0.wireOp",EDGE,"E2.14.31.0"),sQuery(id+"F0.wireOp",EDGE,"E2.14.32.0"),sQuery(id+"F0.wireOp",EDGE,"E2.14.33.0"),sQuery(id+"F0.wireOp",EDGE,"E2.14.34.0"),sQuery(id+"F0.wireOp",EDGE,"E2.14.35.0"),sQuery(id+"F0.wireOp",EDGE,"E2.14.36.0"),sQuery(id+"F0.wireOp",EDGE,"E2.14.37.0"),sQuery(id+"F0.wireOp",EDGE,"E2.14.38.0"),sQuery(id+"F0.wireOp",EDGE,"E2.14.39.0"),sQuery(id+"F0.wireOp",EDGE,"E2.14.40.0"),sQuery(id+"F0.wireOp",EDGE,"E2.14.41.0"),sQuery(id+"F0.wireOp",EDGE,"E2.14.42.0"),sQuery(id+"F0.wireOp",EDGE,"E2.14.43.0"),sQuery(id+"F0.wireOp",EDGE,"E2.14.44.0"),sQuery(id+"F0.wireOp",EDGE,"E2.14.45.0"),sQuery(id+"F0.wireOp",EDGE,"E2.14.46.0"),sQuery(id+"F0.wireOp",EDGE,"E2.14.47.0"),sQuery(id+"F0.wireOp",EDGE,"E2.14.48.0"),sQuery(id+"F0.wireOp",EDGE,"E2.14.49.0"),sQuery(id+"F0.wireOp",EDGE,"E2.15.0.0"),sQuery(id+"F0.wireOp",EDGE,"E2.15.1.0"),sQuery(id+"F0.wireOp",EDGE,"E2.15.2.0"),sQuery(id+"F0.wireOp",EDGE,"E2.15.3.0"),sQuery(id+"F0.wireOp",EDGE,"E2.15.4.0"),sQuery(id+"F0.wireOp",EDGE,"E2.15.5.0"),sQuery(id+"F0.wireOp",EDGE,"E2.15.6.0"),sQuery(id+"F0.wireOp",EDGE,"E2.15.7.0"),sQuery(id+"F0.wireOp",EDGE,"E2.15.8.0"),sQuery(id+"F0.wireOp",EDGE,"E2.15.9.0"),sQuery(id+"F0.wireOp",EDGE,"E2.15.10.0"),sQuery(id+"F0.wireOp",EDGE,"E2.15.11.0"),sQuery(id+"F0.wireOp",EDGE,"E2.15.12.0"),sQuery(id+"F0.wireOp",EDGE,"E2.15.13.0"),sQuery(id+"F0.wireOp",EDGE,"E2.15.14.0"),sQuery(id+"F0.wireOp",EDGE,"E2.15.15.0"),sQuery(id+"F0.wireOp",EDGE,"E2.15.16.0"),sQuery(id+"F0.wireOp",EDGE,"E2.15.17.0"),sQuery(id+"F0.wireOp",EDGE,"E2.15.18.0"),sQuery(id+"F0.wireOp",EDGE,"E2.15.19.0"),sQuery(id+"F0.wireOp",EDGE,"E2.15.20.0"),sQuery(id+"F0.wireOp",EDGE,"E2.15.21.0"),sQuery(id+"F0.wireOp",EDGE,"E2.15.22.0"),sQuery(id+"F0.wireOp",EDGE,"E2.15.23.0"),sQuery(id+"F0.wireOp",EDGE,"E2.15.24.0"),sQuery(id+"F0.wireOp",EDGE,"E2.15.25.0"),sQuery(id+"F0.wireOp",EDGE,"E2.15.26.0"),sQuery(id+"F0.wireOp",EDGE,"E2.15.27.0"),sQuery(id+"F0.wireOp",EDGE,"E2.15.28.0"),sQuery(id+"F0.wireOp",EDGE,"E2.15.29.0"),sQuery(id+"F0.wireOp",EDGE,"E2.15.30.0"),sQuery(id+"F0.wireOp",EDGE,"E2.15.31.0"),sQuery(id+"F0.wireOp",EDGE,"E2.15.32.0"),sQuery(id+"F0.wireOp",EDGE,"E2.15.33.0"),sQuery(id+"F0.wireOp",EDGE,"E2.15.34.0"),sQuery(id+"F0.wireOp",EDGE,"E2.15.35.0"),sQuery(id+"F0.wireOp",EDGE,"E2.15.36.0"),sQuery(id+"F0.wireOp",EDGE,"E2.15.37.0"),sQuery(id+"F0.wireOp",EDGE,"E2.15.38.0"),sQuery(id+"F0.wireOp",EDGE,"E2.15.39.0"),sQuery(id+"F0.wireOp",EDGE,"E2.15.40.0"),sQuery(id+"F0.wireOp",EDGE,"E2.15.41.0"),sQuery(id+"F0.wireOp",EDGE,"E2.15.42.0"),sQuery(id+"F0.wireOp",EDGE,"E2.15.43.0"),sQuery(id+"F0.wireOp",EDGE,"E2.15.44.0"),sQuery(id+"F0.wireOp",EDGE,"E2.15.45.0"),sQuery(id+"F0.wireOp",EDGE,"E2.15.46.0"),sQuery(id+"F0.wireOp",EDGE,"E2.15.47.0"),sQuery(id+"F0.wireOp",EDGE,"E2.15.48.0"),sQuery(id+"F0.wireOp",EDGE,"E2.15.49.0"),sQuery(id+"F0.wireOp",EDGE,"E2.16.0.0"),sQuery(id+"F0.wireOp",EDGE,"E2.16.1.0"),sQuery(id+"F0.wireOp",EDGE,"E2.16.2.0"),sQuery(id+"F0.wireOp",EDGE,"E2.16.3.0"),sQuery(id+"F0.wireOp",EDGE,"E2.16.4.0"),sQuery(id+"F0.wireOp",EDGE,"E2.16.5.0"),sQuery(id+"F0.wireOp",EDGE,"E2.16.6.0"),sQuery(id+"F0.wireOp",EDGE,"E2.16.7.0"),sQuery(id+"F0.wireOp",EDGE,"E2.16.8.0"),sQuery(id+"F0.wireOp",EDGE,"E2.16.9.0"),sQuery(id+"F0.wireOp",EDGE,"E2.16.10.0"),sQuery(id+"F0.wireOp",EDGE,"E2.16.11.0"),sQuery(id+"F0.wireOp",EDGE,"E2.16.12.0"),sQuery(id+"F0.wireOp",EDGE,"E2.16.13.0"),sQuery(id+"F0.wireOp",EDGE,"E2.16.14.0"),sQuery(id+"F0.wireOp",EDGE,"E2.16.15.0"),sQuery(id+"F0.wireOp",EDGE,"E2.16.16.0"),sQuery(id+"F0.wireOp",EDGE,"E2.16.17.0"),sQuery(id+"F0.wireOp",EDGE,"E2.16.18.0"),sQuery(id+"F0.wireOp",EDGE,"E2.16.19.0"),sQuery(id+"F0.wireOp",EDGE,"E2.16.20.0"),sQuery(id+"F0.wireOp",EDGE,"E2.16.21.0"),sQuery(id+"F0.wireOp",EDGE,"E2.16.22.0"),sQuery(id+"F0.wireOp",EDGE,"E2.16.23.0"),sQuery(id+"F0.wireOp",EDGE,"E2.16.24.0"),sQuery(id+"F0.wireOp",EDGE,"E2.16.25.0"),sQuery(id+"F0.wireOp",EDGE,"E2.16.26.0"),sQuery(id+"F0.wireOp",EDGE,"E2.16.27.0"),sQuery(id+"F0.wireOp",EDGE,"E2.16.28.0"),sQuery(id+"F0.wireOp",EDGE,"E2.16.29.0"),sQuery(id+"F0.wireOp",EDGE,"E2.16.30.0"),sQuery(id+"F0.wireOp",EDGE,"E2.16.31.0"),sQuery(id+"F0.wireOp",EDGE,"E2.16.32.0"),sQuery(id+"F0.wireOp",EDGE,"E2.16.33.0"),sQuery(id+"F0.wireOp",EDGE,"E2.16.34.0"),sQuery(id+"F0.wireOp",EDGE,"E2.16.35.0"),sQuery(id+"F0.wireOp",EDGE,"E2.16.36.0"),sQuery(id+"F0.wireOp",EDGE,"E2.16.37.0"),sQuery(id+"F0.wireOp",EDGE,"E2.16.38.0"),sQuery(id+"F0.wireOp",EDGE,"E2.16.39.0"),sQuery(id+"F0.wireOp",EDGE,"E2.16.40.0"),sQuery(id+"F0.wireOp",EDGE,"E2.16.41.0"),sQuery(id+"F0.wireOp",EDGE,"E2.16.42.0"),sQuery(id+"F0.wireOp",EDGE,"E2.16.43.0"),sQuery(id+"F0.wireOp",EDGE,"E2.16.44.0"),sQuery(id+"F0.wireOp",EDGE,"E2.16.45.0"),sQuery(id+"F0.wireOp",EDGE,"E2.16.46.0"),sQuery(id+"F0.wireOp",EDGE,"E2.16.47.0"),sQuery(id+"F0.wireOp",EDGE,"E2.16.48.0"),sQuery(id+"F0.wireOp",EDGE,"E2.16.49.0"),sQuery(id+"F0.wireOp",EDGE,"E2.17.0.0"),sQuery(id+"F0.wireOp",EDGE,"E2.17.1.0"),sQuery(id+"F0.wireOp",EDGE,"E2.17.2.0"),sQuery(id+"F0.wireOp",EDGE,"E2.17.3.0"),sQuery(id+"F0.wireOp",EDGE,"E2.17.4.0"),sQuery(id+"F0.wireOp",EDGE,"E2.17.5.0"),sQuery(id+"F0.wireOp",EDGE,"E2.17.6.0"),sQuery(id+"F0.wireOp",EDGE,"E2.17.7.0"),sQuery(id+"F0.wireOp",EDGE,"E2.17.8.0"),sQuery(id+"F0.wireOp",EDGE,"E2.17.9.0"),sQuery(id+"F0.wireOp",EDGE,"E2.17.10.0"),sQuery(id+"F0.wireOp",EDGE,"E2.17.11.0"),sQuery(id+"F0.wireOp",EDGE,"E2.17.12.0"),sQuery(id+"F0.wireOp",EDGE,"E2.17.13.0"),sQuery(id+"F0.wireOp",EDGE,"E2.17.14.0"),sQuery(id+"F0.wireOp",EDGE,"E2.17.15.0"),sQuery(id+"F0.wireOp",EDGE,"E2.17.16.0"),sQuery(id+"F0.wireOp",EDGE,"E2.17.17.0"),sQuery(id+"F0.wireOp",EDGE,"E2.17.18.0"),sQuery(id+"F0.wireOp",EDGE,"E2.17.19.0"),sQuery(id+"F0.wireOp",EDGE,"E2.17.20.0"),sQuery(id+"F0.wireOp",EDGE,"E2.17.21.0"),sQuery(id+"F0.wireOp",EDGE,"E2.17.22.0"),sQuery(id+"F0.wireOp",EDGE,"E2.17.23.0"),sQuery(id+"F0.wireOp",EDGE,"E2.17.24.0"),sQuery(id+"F0.wireOp",EDGE,"E2.17.25.0"),sQuery(id+"F0.wireOp",EDGE,"E2.17.26.0"),sQuery(id+"F0.wireOp",EDGE,"E2.17.27.0"),sQuery(id+"F0.wireOp",EDGE,"E2.17.28.0"),sQuery(id+"F0.wireOp",EDGE,"E2.17.29.0"),sQuery(id+"F0.wireOp",EDGE,"E2.17.30.0"),sQuery(id+"F0.wireOp",EDGE,"E2.17.31.0"),sQuery(id+"F0.wireOp",EDGE,"E2.17.32.0"),sQuery(id+"F0.wireOp",EDGE,"E2.17.33.0"),sQuery(id+"F0.wireOp",EDGE,"E2.17.34.0"),sQuery(id+"F0.wireOp",EDGE,"E2.17.35.0"),sQuery(id+"F0.wireOp",EDGE,"E2.17.36.0"),sQuery(id+"F0.wireOp",EDGE,"E2.17.37.0"),sQuery(id+"F0.wireOp",EDGE,"E2.17.38.0"),sQuery(id+"F0.wireOp",EDGE,"E2.17.39.0"),sQuery(id+"F0.wireOp",EDGE,"E2.17.40.0"),sQuery(id+"F0.wireOp",EDGE,"E2.17.41.0"),sQuery(id+"F0.wireOp",EDGE,"E2.17.42.0"),sQuery(id+"F0.wireOp",EDGE,"E2.17.43.0"),sQuery(id+"F0.wireOp",EDGE,"E2.17.44.0"),sQuery(id+"F0.wireOp",EDGE,"E2.17.45.0"),sQuery(id+"F0.wireOp",EDGE,"E2.17.46.0"),sQuery(id+"F0.wireOp",EDGE,"E2.17.47.0"),sQuery(id+"F0.wireOp",EDGE,"E2.17.48.0"),sQuery(id+"F0.wireOp",EDGE,"E2.17.49.0"),sQuery(id+"F0.wireOp",EDGE,"E2.18.0.0"),sQuery(id+"F0.wireOp",EDGE,"E2.18.1.0"),sQuery(id+"F0.wireOp",EDGE,"E2.18.2.0"),sQuery(id+"F0.wireOp",EDGE,"E2.18.3.0"),sQuery(id+"F0.wireOp",EDGE,"E2.18.4.0"),sQuery(id+"F0.wireOp",EDGE,"E2.18.5.0"),sQuery(id+"F0.wireOp",EDGE,"E2.18.6.0"),sQuery(id+"F0.wireOp",EDGE,"E2.18.7.0"),sQuery(id+"F0.wireOp",EDGE,"E2.18.8.0"),sQuery(id+"F0.wireOp",EDGE,"E2.18.9.0"),sQuery(id+"F0.wireOp",EDGE,"E2.18.10.0"),sQuery(id+"F0.wireOp",EDGE,"E2.18.11.0"),sQuery(id+"F0.wireOp",EDGE,"E2.18.12.0"),sQuery(id+"F0.wireOp",EDGE,"E2.18.13.0"),sQuery(id+"F0.wireOp",EDGE,"E2.18.14.0"),sQuery(id+"F0.wireOp",EDGE,"E2.18.15.0"),sQuery(id+"F0.wireOp",EDGE,"E2.18.16.0"),sQuery(id+"F0.wireOp",EDGE,"E2.18.17.0"),sQuery(id+"F0.wireOp",EDGE,"E2.18.18.0"),sQuery(id+"F0.wireOp",EDGE,"E2.18.19.0"),sQuery(id+"F0.wireOp",EDGE,"E2.18.20.0"),sQuery(id+"F0.wireOp",EDGE,"E2.18.21.0"),sQuery(id+"F0.wireOp",EDGE,"E2.18.22.0"),sQuery(id+"F0.wireOp",EDGE,"E2.18.23.0"),sQuery(id+"F0.wireOp",EDGE,"E2.18.24.0"),sQuery(id+"F0.wireOp",EDGE,"E2.18.25.0"),sQuery(id+"F0.wireOp",EDGE,"E2.18.26.0"),sQuery(id+"F0.wireOp",EDGE,"E2.18.27.0"),sQuery(id+"F0.wireOp",EDGE,"E2.18.28.0"),sQuery(id+"F0.wireOp",EDGE,"E2.18.29.0"),sQuery(id+"F0.wireOp",EDGE,"E2.18.30.0"),sQuery(id+"F0.wireOp",EDGE,"E2.18.31.0"),sQuery(id+"F0.wireOp",EDGE,"E2.18.32.0"),sQuery(id+"F0.wireOp",EDGE,"E2.18.33.0"),sQuery(id+"F0.wireOp",EDGE,"E2.18.34.0"),sQuery(id+"F0.wireOp",EDGE,"E2.18.35.0"),sQuery(id+"F0.wireOp",EDGE,"E2.18.36.0"),sQuery(id+"F0.wireOp",EDGE,"E2.18.37.0"),sQuery(id+"F0.wireOp",EDGE,"E2.18.38.0"),sQuery(id+"F0.wireOp",EDGE,"E2.18.39.0"),sQuery(id+"F0.wireOp",EDGE,"E2.18.40.0"),sQuery(id+"F0.wireOp",EDGE,"E2.18.41.0"),sQuery(id+"F0.wireOp",EDGE,"E2.18.42.0"),sQuery(id+"F0.wireOp",EDGE,"E2.18.43.0"),sQuery(id+"F0.wireOp",EDGE,"E2.18.44.0"),sQuery(id+"F0.wireOp",EDGE,"E2.18.45.0"),sQuery(id+"F0.wireOp",EDGE,"E2.18.46.0"),sQuery(id+"F0.wireOp",EDGE,"E2.18.47.0"),sQuery(id+"F0.wireOp",EDGE,"E2.18.48.0"),sQuery(id+"F0.wireOp",EDGE,"E2.18.49.0"),sQuery(id+"F0.wireOp",EDGE,"E2.19.0.0"),sQuery(id+"F0.wireOp",EDGE,"E2.19.1.0"),sQuery(id+"F0.wireOp",EDGE,"E2.19.2.0"),sQuery(id+"F0.wireOp",EDGE,"E2.19.3.0"),sQuery(id+"F0.wireOp",EDGE,"E2.19.4.0"),sQuery(id+"F0.wireOp",EDGE,"E2.19.5.0"),sQuery(id+"F0.wireOp",EDGE,"E2.19.6.0"),sQuery(id+"F0.wireOp",EDGE,"E2.19.7.0"),sQuery(id+"F0.wireOp",EDGE,"E2.19.8.0"),sQuery(id+"F0.wireOp",EDGE,"E2.19.9.0"),sQuery(id+"F0.wireOp",EDGE,"E2.19.10.0"),sQuery(id+"F0.wireOp",EDGE,"E2.19.11.0"),sQuery(id+"F0.wireOp",EDGE,"E2.19.12.0"),sQuery(id+"F0.wireOp",EDGE,"E2.19.13.0"),sQuery(id+"F0.wireOp",EDGE,"E2.19.14.0"),sQuery(id+"F0.wireOp",EDGE,"E2.19.15.0"),sQuery(id+"F0.wireOp",EDGE,"E2.19.16.0"),sQuery(id+"F0.wireOp",EDGE,"E2.19.17.0"),sQuery(id+"F0.wireOp",EDGE,"E2.19.18.0"),sQuery(id+"F0.wireOp",EDGE,"E2.19.19.0"),sQuery(id+"F0.wireOp",EDGE,"E2.19.20.0"),sQuery(id+"F0.wireOp",EDGE,"E2.19.21.0"),sQuery(id+"F0.wireOp",EDGE,"E2.19.22.0"),sQuery(id+"F0.wireOp",EDGE,"E2.19.23.0"),sQuery(id+"F0.wireOp",EDGE,"E2.19.24.0"),sQuery(id+"F0.wireOp",EDGE,"E2.19.25.0"),sQuery(id+"F0.wireOp",EDGE,"E2.19.26.0"),sQuery(id+"F0.wireOp",EDGE,"E2.19.27.0"),sQuery(id+"F0.wireOp",EDGE,"E2.19.28.0"),sQuery(id+"F0.wireOp",EDGE,"E2.19.29.0"),sQuery(id+"F0.wireOp",EDGE,"E2.19.30.0"),sQuery(id+"F0.wireOp",EDGE,"E2.19.31.0"),sQuery(id+"F0.wireOp",EDGE,"E2.19.32.0"),sQuery(id+"F0.wireOp",EDGE,"E2.19.33.0"),sQuery(id+"F0.wireOp",EDGE,"E2.19.34.0"),sQuery(id+"F0.wireOp",EDGE,"E2.19.35.0"),sQuery(id+"F0.wireOp",EDGE,"E2.19.36.0"),sQuery(id+"F0.wireOp",EDGE,"E2.19.37.0"),sQuery(id+"F0.wireOp",EDGE,"E2.19.38.0"),sQuery(id+"F0.wireOp",EDGE,"E2.19.39.0"),sQuery(id+"F0.wireOp",EDGE,"E2.19.40.0"),sQuery(id+"F0.wireOp",EDGE,"E2.19.41.0"),sQuery(id+"F0.wireOp",EDGE,"E2.19.42.0"),sQuery(id+"F0.wireOp",EDGE,"E2.19.43.0"),sQuery(id+"F0.wireOp",EDGE,"E2.19.44.0"),sQuery(id+"F0.wireOp",EDGE,"E2.19.45.0"),sQuery(id+"F0.wireOp",EDGE,"E2.19.46.0"),sQuery(id+"F0.wireOp",EDGE,"E2.19.47.0"),sQuery(id+"F0.wireOp",EDGE,"E2.19.48.0"),sQuery(id+"F0.wireOp",EDGE,"E2.19.49.0"),sQuery(id+"F0.wireOp",EDGE,"E2.20.0.0"),sQuery(id+"F0.wireOp",EDGE,"E2.20.1.0"),sQuery(id+"F0.wireOp",EDGE,"E2.20.2.0"),sQuery(id+"F0.wireOp",EDGE,"E2.20.3.0"),sQuery(id+"F0.wireOp",EDGE,"E2.20.4.0"),sQuery(id+"F0.wireOp",EDGE,"E2.20.5.0"),sQuery(id+"F0.wireOp",EDGE,"E2.20.6.0"),sQuery(id+"F0.wireOp",EDGE,"E2.20.7.0"),sQuery(id+"F0.wireOp",EDGE,"E2.20.8.0"),sQuery(id+"F0.wireOp",EDGE,"E2.20.9.0"),sQuery(id+"F0.wireOp",EDGE,"E2.20.10.0"),sQuery(id+"F0.wireOp",EDGE,"E2.20.11.0"),sQuery(id+"F0.wireOp",EDGE,"E2.20.12.0"),sQuery(id+"F0.wireOp",EDGE,"E2.20.13.0"),sQuery(id+"F0.wireOp",EDGE,"E2.20.14.0"),sQuery(id+"F0.wireOp",EDGE,"E2.20.15.0"),sQuery(id+"F0.wireOp",EDGE,"E2.20.16.0"),sQuery(id+"F0.wireOp",EDGE,"E2.20.17.0"),sQuery(id+"F0.wireOp",EDGE,"E2.20.18.0"),sQuery(id+"F0.wireOp",EDGE,"E2.20.19.0"),sQuery(id+"F0.wireOp",EDGE,"E2.20.20.0"),sQuery(id+"F0.wireOp",EDGE,"E2.20.21.0"),sQuery(id+"F0.wireOp",EDGE,"E2.20.22.0"),sQuery(id+"F0.wireOp",EDGE,"E2.20.23.0"),sQuery(id+"F0.wireOp",EDGE,"E2.20.24.0"),sQuery(id+"F0.wireOp",EDGE,"E2.20.25.0"),sQuery(id+"F0.wireOp",EDGE,"E2.20.26.0"),sQuery(id+"F0.wireOp",EDGE,"E2.20.27.0"),sQuery(id+"F0.wireOp",EDGE,"E2.20.28.0"),sQuery(id+"F0.wireOp",EDGE,"E2.20.29.0"),sQuery(id+"F0.wireOp",EDGE,"E2.20.30.0"),sQuery(id+"F0.wireOp",EDGE,"E2.20.31.0"),sQuery(id+"F0.wireOp",EDGE,"E2.20.32.0"),sQuery(id+"F0.wireOp",EDGE,"E2.20.33.0"),sQuery(id+"F0.wireOp",EDGE,"E2.20.34.0"),sQuery(id+"F0.wireOp",EDGE,"E2.20.35.0"),sQuery(id+"F0.wireOp",EDGE,"E2.20.36.0"),sQuery(id+"F0.wireOp",EDGE,"E2.20.37.0"),sQuery(id+"F0.wireOp",EDGE,"E2.20.38.0"),sQuery(id+"F0.wireOp",EDGE,"E2.20.39.0"),sQuery(id+"F0.wireOp",EDGE,"E2.20.40.0"),sQuery(id+"F0.wireOp",EDGE,"E2.20.41.0"),sQuery(id+"F0.wireOp",EDGE,"E2.20.42.0"),sQuery(id+"F0.wireOp",EDGE,"E2.20.43.0"),sQuery(id+"F0.wireOp",EDGE,"E2.20.44.0"),sQuery(id+"F0.wireOp",EDGE,"E2.20.45.0"),sQuery(id+"F0.wireOp",EDGE,"E2.20.46.0"),sQuery(id+"F0.wireOp",EDGE,"E2.20.47.0"),sQuery(id+"F0.wireOp",EDGE,"E2.20.48.0"),sQuery(id+"F0.wireOp",EDGE,"E2.20.49.0"),sQuery(id+"F0.wireOp",EDGE,"E2.21.0.0"),sQuery(id+"F0.wireOp",EDGE,"E2.21.1.0"),sQuery(id+"F0.wireOp",EDGE,"E2.21.2.0"),sQuery(id+"F0.wireOp",EDGE,"E2.21.3.0"),sQuery(id+"F0.wireOp",EDGE,"E2.21.4.0"),sQuery(id+"F0.wireOp",EDGE,"E2.21.5.0"),sQuery(id+"F0.wireOp",EDGE,"E2.21.6.0"),sQuery(id+"F0.wireOp",EDGE,"E2.21.7.0"),sQuery(id+"F0.wireOp",EDGE,"E2.21.8.0"),sQuery(id+"F0.wireOp",EDGE,"E2.21.9.0"),sQuery(id+"F0.wireOp",EDGE,"E2.21.10.0"),sQuery(id+"F0.wireOp",EDGE,"E2.21.11.0"),sQuery(id+"F0.wireOp",EDGE,"E2.21.12.0"),sQuery(id+"F0.wireOp",EDGE,"E2.21.13.0"),sQuery(id+"F0.wireOp",EDGE,"E2.21.14.0"),sQuery(id+"F0.wireOp",EDGE,"E2.21.15.0"),sQuery(id+"F0.wireOp",EDGE,"E2.21.16.0"),sQuery(id+"F0.wireOp",EDGE,"E2.21.17.0"),sQuery(id+"F0.wireOp",EDGE,"E2.21.18.0"),sQuery(id+"F0.wireOp",EDGE,"E2.21.19.0"),sQuery(id+"F0.wireOp",EDGE,"E2.21.20.0"),sQuery(id+"F0.wireOp",EDGE,"E2.21.21.0"),sQuery(id+"F0.wireOp",EDGE,"E2.21.22.0"),sQuery(id+"F0.wireOp",EDGE,"E2.21.23.0"),sQuery(id+"F0.wireOp",EDGE,"E2.21.24.0"),sQuery(id+"F0.wireOp",EDGE,"E2.21.25.0"),sQuery(id+"F0.wireOp",EDGE,"E2.21.26.0"),sQuery(id+"F0.wireOp",EDGE,"E2.21.27.0"),sQuery(id+"F0.wireOp",EDGE,"E2.21.28.0"),sQuery(id+"F0.wireOp",EDGE,"E2.21.29.0"),sQuery(id+"F0.wireOp",EDGE,"E2.21.30.0"),sQuery(id+"F0.wireOp",EDGE,"E2.21.31.0"),sQuery(id+"F0.wireOp",EDGE,"E2.21.32.0"),sQuery(id+"F0.wireOp",EDGE,"E2.21.33.0"),sQuery(id+"F0.wireOp",EDGE,"E2.21.34.0"),sQuery(id+"F0.wireOp",EDGE,"E2.21.35.0"),sQuery(id+"F0.wireOp",EDGE,"E2.21.36.0"),sQuery(id+"F0.wireOp",EDGE,"E2.21.37.0"),sQuery(id+"F0.wireOp",EDGE,"E2.21.38.0"),sQuery(id+"F0.wireOp",EDGE,"E2.21.39.0"),sQuery(id+"F0.wireOp",EDGE,"E2.21.40.0"),sQuery(id+"F0.wireOp",EDGE,"E2.21.41.0"),sQuery(id+"F0.wireOp",EDGE,"E2.21.42.0"),sQuery(id+"F0.wireOp",EDGE,"E2.21.43.0"),sQuery(id+"F0.wireOp",EDGE,"E2.21.44.0"),sQuery(id+"F0.wireOp",EDGE,"E2.21.45.0"),sQuery(id+"F0.wireOp",EDGE,"E2.21.46.0"),sQuery(id+"F0.wireOp",EDGE,"E2.21.47.0"),sQuery(id+"F0.wireOp",EDGE,"E2.21.48.0"),sQuery(id+"F0.wireOp",EDGE,"E2.21.49.0"),sQuery(id+"F0.wireOp",EDGE,"E2.22.0.0"),sQuery(id+"F0.wireOp",EDGE,"E2.22.1.0"),sQuery(id+"F0.wireOp",EDGE,"E2.22.2.0"),sQuery(id+"F0.wireOp",EDGE,"E2.22.3.0"),sQuery(id+"F0.wireOp",EDGE,"E2.22.4.0"),sQuery(id+"F0.wireOp",EDGE,"E2.22.5.0"),sQuery(id+"F0.wireOp",EDGE,"E2.22.6.0"),sQuery(id+"F0.wireOp",EDGE,"E2.22.7.0"),sQuery(id+"F0.wireOp",EDGE,"E2.22.8.0"),sQuery(id+"F0.wireOp",EDGE,"E2.22.9.0"),sQuery(id+"F0.wireOp",EDGE,"E2.22.10.0"),sQuery(id+"F0.wireOp",EDGE,"E2.22.11.0"),sQuery(id+"F0.wireOp",EDGE,"E2.22.12.0"),sQuery(id+"F0.wireOp",EDGE,"E2.22.13.0"),sQuery(id+"F0.wireOp",EDGE,"E2.22.14.0"),sQuery(id+"F0.wireOp",EDGE,"E2.22.15.0"),sQuery(id+"F0.wireOp",EDGE,"E2.22.16.0"),sQuery(id+"F0.wireOp",EDGE,"E2.22.17.0"),sQuery(id+"F0.wireOp",EDGE,"E2.22.18.0"),sQuery(id+"F0.wireOp",EDGE,"E2.22.19.0"),sQuery(id+"F0.wireOp",EDGE,"E2.22.20.0"),sQuery(id+"F0.wireOp",EDGE,"E2.22.21.0"),sQuery(id+"F0.wireOp",EDGE,"E2.22.22.0"),sQuery(id+"F0.wireOp",EDGE,"E2.22.23.0"),sQuery(id+"F0.wireOp",EDGE,"E2.22.24.0"),sQuery(id+"F0.wireOp",EDGE,"E2.22.25.0"),sQuery(id+"F0.wireOp",EDGE,"E2.22.26.0"),sQuery(id+"F0.wireOp",EDGE,"E2.22.27.0"),sQuery(id+"F0.wireOp",EDGE,"E2.22.28.0"),sQuery(id+"F0.wireOp",EDGE,"E2.22.29.0"),sQuery(id+"F0.wireOp",EDGE,"E2.22.30.0"),sQuery(id+"F0.wireOp",EDGE,"E2.22.31.0"),sQuery(id+"F0.wireOp",EDGE,"E2.22.32.0"),sQuery(id+"F0.wireOp",EDGE,"E2.22.33.0"),sQuery(id+"F0.wireOp",EDGE,"E2.22.34.0"),sQuery(id+"F0.wireOp",EDGE,"E2.22.35.0"),sQuery(id+"F0.wireOp",EDGE,"E2.22.36.0"),sQuery(id+"F0.wireOp",EDGE,"E2.22.37.0"),sQuery(id+"F0.wireOp",EDGE,"E2.22.38.0"),sQuery(id+"F0.wireOp",EDGE,"E2.22.39.0"),sQuery(id+"F0.wireOp",EDGE,"E2.22.40.0"),sQuery(id+"F0.wireOp",EDGE,"E2.22.41.0"),sQuery(id+"F0.wireOp",EDGE,"E2.22.42.0"),sQuery(id+"F0.wireOp",EDGE,"E2.22.43.0"),sQuery(id+"F0.wireOp",EDGE,"E2.22.44.0"),sQuery(id+"F0.wireOp",EDGE,"E2.22.45.0"),sQuery(id+"F0.wireOp",EDGE,"E2.22.46.0"),sQuery(id+"F0.wireOp",EDGE,"E2.22.47.0"),sQuery(id+"F0.wireOp",EDGE,"E2.22.48.0"),sQuery(id+"F0.wireOp",EDGE,"E2.22.49.0"),sQuery(id+"F0.wireOp",EDGE,"E2.23.0.0"),sQuery(id+"F0.wireOp",EDGE,"E2.23.1.0"),sQuery(id+"F0.wireOp",EDGE,"E2.23.2.0"),sQuery(id+"F0.wireOp",EDGE,"E2.23.3.0"),sQuery(id+"F0.wireOp",EDGE,"E2.23.4.0"),sQuery(id+"F0.wireOp",EDGE,"E2.23.5.0"),sQuery(id+"F0.wireOp",EDGE,"E2.23.6.0"),sQuery(id+"F0.wireOp",EDGE,"E2.23.7.0"),sQuery(id+"F0.wireOp",EDGE,"E2.23.8.0"),sQuery(id+"F0.wireOp",EDGE,"E2.23.9.0"),sQuery(id+"F0.wireOp",EDGE,"E2.23.10.0"),sQuery(id+"F0.wireOp",EDGE,"E2.23.11.0"),sQuery(id+"F0.wireOp",EDGE,"E2.23.12.0"),sQuery(id+"F0.wireOp",EDGE,"E2.23.13.0"),sQuery(id+"F0.wireOp",EDGE,"E2.23.14.0"),sQuery(id+"F0.wireOp",EDGE,"E2.23.15.0"),sQuery(id+"F0.wireOp",EDGE,"E2.23.16.0"),sQuery(id+"F0.wireOp",EDGE,"E2.23.17.0"),sQuery(id+"F0.wireOp",EDGE,"E2.23.18.0"),sQuery(id+"F0.wireOp",EDGE,"E2.23.19.0"),sQuery(id+"F0.wireOp",EDGE,"E2.23.20.0"),sQuery(id+"F0.wireOp",EDGE,"E2.23.21.0"),sQuery(id+"F0.wireOp",EDGE,"E2.23.22.0"),sQuery(id+"F0.wireOp",EDGE,"E2.23.23.0"),sQuery(id+"F0.wireOp",EDGE,"E2.23.24.0"),sQuery(id+"F0.wireOp",EDGE,"E2.23.25.0"),sQuery(id+"F0.wireOp",EDGE,"E2.23.26.0"),sQuery(id+"F0.wireOp",EDGE,"E2.23.27.0"),sQuery(id+"F0.wireOp",EDGE,"E2.23.28.0"),sQuery(id+"F0.wireOp",EDGE,"E2.23.29.0"),sQuery(id+"F0.wireOp",EDGE,"E2.23.30.0"),sQuery(id+"F0.wireOp",EDGE,"E2.23.31.0"),sQuery(id+"F0.wireOp",EDGE,"E2.23.32.0"),sQuery(id+"F0.wireOp",EDGE,"E2.23.33.0"),sQuery(id+"F0.wireOp",EDGE,"E2.23.34.0"),sQuery(id+"F0.wireOp",EDGE,"E2.23.35.0"),sQuery(id+"F0.wireOp",EDGE,"E2.23.36.0"),sQuery(id+"F0.wireOp",EDGE,"E2.23.37.0"),sQuery(id+"F0.wireOp",EDGE,"E2.23.38.0"),sQuery(id+"F0.wireOp",EDGE,"E2.23.39.0"),sQuery(id+"F0.wireOp",EDGE,"E2.23.40.0"),sQuery(id+"F0.wireOp",EDGE,"E2.23.41.0"),sQuery(id+"F0.wireOp",EDGE,"E2.23.42.0"),sQuery(id+"F0.wireOp",EDGE,"E2.23.43.0"),sQuery(id+"F0.wireOp",EDGE,"E2.23.44.0"),sQuery(id+"F0.wireOp",EDGE,"E2.23.45.0"),sQuery(id+"F0.wireOp",EDGE,"E2.23.46.0"),sQuery(id+"F0.wireOp",EDGE,"E2.23.47.0"),sQuery(id+"F0.wireOp",EDGE,"E2.23.48.0"),sQuery(id+"F0.wireOp",EDGE,"E2.23.49.0"),sQuery(id+"F0.wireOp",EDGE,"E2.24.0.0"),sQuery(id+"F0.wireOp",EDGE,"E2.24.1.0"),sQuery(id+"F0.wireOp",EDGE,"E2.24.2.0"),sQuery(id+"F0.wireOp",EDGE,"E2.24.3.0"),sQuery(id+"F0.wireOp",EDGE,"E2.24.4.0"),sQuery(id+"F0.wireOp",EDGE,"E2.24.5.0"),sQuery(id+"F0.wireOp",EDGE,"E2.24.6.0"),sQuery(id+"F0.wireOp",EDGE,"E2.24.7.0"),sQuery(id+"F0.wireOp",EDGE,"E2.24.8.0"),sQuery(id+"F0.wireOp",EDGE,"E2.24.9.0"),sQuery(id+"F0.wireOp",EDGE,"E2.24.10.0"),sQuery(id+"F0.wireOp",EDGE,"E2.24.11.0"),sQuery(id+"F0.wireOp",EDGE,"E2.24.12.0"),sQuery(id+"F0.wireOp",EDGE,"E2.24.13.0"),sQuery(id+"F0.wireOp",EDGE,"E2.24.14.0"),sQuery(id+"F0.wireOp",EDGE,"E2.24.15.0"),sQuery(id+"F0.wireOp",EDGE,"E2.24.16.0"),sQuery(id+"F0.wireOp",EDGE,"E2.24.17.0"),sQuery(id+"F0.wireOp",EDGE,"E2.24.18.0"),sQuery(id+"F0.wireOp",EDGE,"E2.24.19.0"),sQuery(id+"F0.wireOp",EDGE,"E2.24.20.0"),sQuery(id+"F0.wireOp",EDGE,"E2.24.21.0"),sQuery(id+"F0.wireOp",EDGE,"E2.24.22.0"),sQuery(id+"F0.wireOp",EDGE,"E2.24.23.0"),sQuery(id+"F0.wireOp",EDGE,"E2.24.24.0"),sQuery(id+"F0.wireOp",EDGE,"E2.24.25.0"),sQuery(id+"F0.wireOp",EDGE,"E2.24.26.0"),sQuery(id+"F0.wireOp",EDGE,"E2.24.27.0"),sQuery(id+"F0.wireOp",EDGE,"E2.24.28.0"),sQuery(id+"F0.wireOp",EDGE,"E2.24.29.0"),sQuery(id+"F0.wireOp",EDGE,"E2.24.30.0"),sQuery(id+"F0.wireOp",EDGE,"E2.24.31.0"),sQuery(id+"F0.wireOp",EDGE,"E2.24.32.0"),sQuery(id+"F0.wireOp",EDGE,"E2.24.33.0"),sQuery(id+"F0.wireOp",EDGE,"E2.24.34.0"),sQuery(id+"F0.wireOp",EDGE,"E2.24.35.0"),sQuery(id+"F0.wireOp",EDGE,"E2.24.36.0"),sQuery(id+"F0.wireOp",EDGE,"E2.24.37.0"),sQuery(id+"F0.wireOp",EDGE,"E2.24.38.0"),sQuery(id+"F0.wireOp",EDGE,"E2.24.39.0"),sQuery(id+"F0.wireOp",EDGE,"E2.24.40.0"),sQuery(id+"F0.wireOp",EDGE,"E2.24.41.0"),sQuery(id+"F0.wireOp",EDGE,"E2.24.42.0"),sQuery(id+"F0.wireOp",EDGE,"E2.24.43.0"),sQuery(id+"F0.wireOp",EDGE,"E2.24.44.0"),sQuery(id+"F0.wireOp",EDGE,"E2.24.45.0"),sQuery(id+"F0.wireOp",EDGE,"E2.24.46.0"),sQuery(id+"F0.wireOp",EDGE,"E2.24.47.0"),sQuery(id+"F0.wireOp",EDGE,"E2.24.48.0"),sQuery(id+"F0.wireOp",EDGE,"E2.24.49.0"),sQuery(id+"F0.wireOp",EDGE,"E2.25.0.0"),sQuery(id+"F0.wireOp",EDGE,"E2.25.1.0"),sQuery(id+"F0.wireOp",EDGE,"E2.25.2.0"),sQuery(id+"F0.wireOp",EDGE,"E2.25.3.0"),sQuery(id+"F0.wireOp",EDGE,"E2.25.4.0"),sQuery(id+"F0.wireOp",EDGE,"E2.25.5.0"),sQuery(id+"F0.wireOp",EDGE,"E2.25.6.0"),sQuery(id+"F0.wireOp",EDGE,"E2.25.7.0"),sQuery(id+"F0.wireOp",EDGE,"E2.25.8.0"),sQuery(id+"F0.wireOp",EDGE,"E2.25.9.0"),sQuery(id+"F0.wireOp",EDGE,"E2.25.10.0"),sQuery(id+"F0.wireOp",EDGE,"E2.25.11.0"),sQuery(id+"F0.wireOp",EDGE,"E2.25.12.0"),sQuery(id+"F0.wireOp",EDGE,"E2.25.13.0"),sQuery(id+"F0.wireOp",EDGE,"E2.25.14.0"),sQuery(id+"F0.wireOp",EDGE,"E2.25.15.0"),sQuery(id+"F0.wireOp",EDGE,"E2.25.16.0"),sQuery(id+"F0.wireOp",EDGE,"E2.25.17.0"),sQuery(id+"F0.wireOp",EDGE,"E2.25.18.0"),sQuery(id+"F0.wireOp",EDGE,"E2.25.19.0"),sQuery(id+"F0.wireOp",EDGE,"E2.25.20.0"),sQuery(id+"F0.wireOp",EDGE,"E2.25.21.0"),sQuery(id+"F0.wireOp",EDGE,"E2.25.22.0"),sQuery(id+"F0.wireOp",EDGE,"E2.25.23.0"),sQuery(id+"F0.wireOp",EDGE,"E2.25.24.0"),sQuery(id+"F0.wireOp",EDGE,"E2.25.25.0"),sQuery(id+"F0.wireOp",EDGE,"E2.25.26.0"),sQuery(id+"F0.wireOp",EDGE,"E2.25.27.0"),sQuery(id+"F0.wireOp",EDGE,"E2.25.28.0"),sQuery(id+"F0.wireOp",EDGE,"E2.25.29.0"),sQuery(id+"F0.wireOp",EDGE,"E2.25.30.0"),sQuery(id+"F0.wireOp",EDGE,"E2.25.31.0"),sQuery(id+"F0.wireOp",EDGE,"E2.25.32.0"),sQuery(id+"F0.wireOp",EDGE,"E2.25.33.0"),sQuery(id+"F0.wireOp",EDGE,"E2.25.34.0"),sQuery(id+"F0.wireOp",EDGE,"E2.25.35.0"),sQuery(id+"F0.wireOp",EDGE,"E2.25.36.0"),sQuery(id+"F0.wireOp",EDGE,"E2.25.37.0"),sQuery(id+"F0.wireOp",EDGE,"E2.25.38.0"),sQuery(id+"F0.wireOp",EDGE,"E2.25.39.0"),sQuery(id+"F0.wireOp",EDGE,"E2.25.40.0"),sQuery(id+"F0.wireOp",EDGE,"E2.25.41.0"),sQuery(id+"F0.wireOp",EDGE,"E2.25.42.0"),sQuery(id+"F0.wireOp",EDGE,"E2.25.43.0"),sQuery(id+"F0.wireOp",EDGE,"E2.25.44.0"),sQuery(id+"F0.wireOp",EDGE,"E2.25.45.0"),sQuery(id+"F0.wireOp",EDGE,"E2.25.46.0"),sQuery(id+"F0.wireOp",EDGE,"E2.25.47.0"),sQuery(id+"F0.wireOp",EDGE,"E2.25.48.0"),sQuery(id+"F0.wireOp",EDGE,"E2.25.49.0"),sQuery(id+"F0.wireOp",EDGE,"E2.26.0.0"),sQuery(id+"F0.wireOp",EDGE,"E2.26.1.0"),sQuery(id+"F0.wireOp",EDGE,"E2.26.2.0"),sQuery(id+"F0.wireOp",EDGE,"E2.26.3.0"),sQuery(id+"F0.wireOp",EDGE,"E2.26.4.0"),sQuery(id+"F0.wireOp",EDGE,"E2.26.5.0"),sQuery(id+"F0.wireOp",EDGE,"E2.26.6.0"),sQuery(id+"F0.wireOp",EDGE,"E2.26.7.0"),sQuery(id+"F0.wireOp",EDGE,"E2.26.8.0"),sQuery(id+"F0.wireOp",EDGE,"E2.26.9.0"),sQuery(id+"F0.wireOp",EDGE,"E2.26.10.0"),sQuery(id+"F0.wireOp",EDGE,"E2.26.11.0"),sQuery(id+"F0.wireOp",EDGE,"E2.26.12.0"),sQuery(id+"F0.wireOp",EDGE,"E2.26.13.0"),sQuery(id+"F0.wireOp",EDGE,"E2.26.14.0"),sQuery(id+"F0.wireOp",EDGE,"E2.26.15.0"),sQuery(id+"F0.wireOp",EDGE,"E2.26.16.0"),sQuery(id+"F0.wireOp",EDGE,"E2.26.17.0"),sQuery(id+"F0.wireOp",EDGE,"E2.26.18.0"),sQuery(id+"F0.wireOp",EDGE,"E2.26.19.0"),sQuery(id+"F0.wireOp",EDGE,"E2.26.20.0"),sQuery(id+"F0.wireOp",EDGE,"E2.26.21.0"),sQuery(id+"F0.wireOp",EDGE,"E2.26.22.0"),sQuery(id+"F0.wireOp",EDGE,"E2.26.23.0"),sQuery(id+"F0.wireOp",EDGE,"E2.26.24.0"),sQuery(id+"F0.wireOp",EDGE,"E2.26.25.0"),sQuery(id+"F0.wireOp",EDGE,"E2.26.26.0"),sQuery(id+"F0.wireOp",EDGE,"E2.26.27.0"),sQuery(id+"F0.wireOp",EDGE,"E2.26.28.0"),sQuery(id+"F0.wireOp",EDGE,"E2.26.29.0"),sQuery(id+"F0.wireOp",EDGE,"E2.26.30.0"),sQuery(id+"F0.wireOp",EDGE,"E2.26.31.0"),sQuery(id+"F0.wireOp",EDGE,"E2.26.32.0"),sQuery(id+"F0.wireOp",EDGE,"E2.26.33.0"),sQuery(id+"F0.wireOp",EDGE,"E2.26.34.0"),sQuery(id+"F0.wireOp",EDGE,"E2.26.35.0"),sQuery(id+"F0.wireOp",EDGE,"E2.26.36.0"),sQuery(id+"F0.wireOp",EDGE,"E2.26.37.0"),sQuery(id+"F0.wireOp",EDGE,"E2.26.38.0"),sQuery(id+"F0.wireOp",EDGE,"E2.26.39.0"),sQuery(id+"F0.wireOp",EDGE,"E2.26.40.0"),sQuery(id+"F0.wireOp",EDGE,"E2.26.41.0"),sQuery(id+"F0.wireOp",EDGE,"E2.26.42.0"),sQuery(id+"F0.wireOp",EDGE,"E2.26.43.0"),sQuery(id+"F0.wireOp",EDGE,"E2.26.44.0"),sQuery(id+"F0.wireOp",EDGE,"E2.26.45.0"),sQuery(id+"F0.wireOp",EDGE,"E2.26.46.0"),sQuery(id+"F0.wireOp",EDGE,"E2.26.47.0"),sQuery(id+"F0.wireOp",EDGE,"E2.26.48.0"),sQuery(id+"F0.wireOp",EDGE,"E2.26.49.0"),sQuery(id+"F0.wireOp",EDGE,"E2.27.0.0"),sQuery(id+"F0.wireOp",EDGE,"E2.27.1.0"),sQuery(id+"F0.wireOp",EDGE,"E2.27.2.0"),sQuery(id+"F0.wireOp",EDGE,"E2.27.3.0"),sQuery(id+"F0.wireOp",EDGE,"E2.27.4.0"),sQuery(id+"F0.wireOp",EDGE,"E2.27.5.0"),sQuery(id+"F0.wireOp",EDGE,"E2.27.6.0"),sQuery(id+"F0.wireOp",EDGE,"E2.27.7.0"),sQuery(id+"F0.wireOp",EDGE,"E2.27.8.0"),sQuery(id+"F0.wireOp",EDGE,"E2.27.9.0"),sQuery(id+"F0.wireOp",EDGE,"E2.27.10.0"),sQuery(id+"F0.wireOp",EDGE,"E2.27.11.0"),sQuery(id+"F0.wireOp",EDGE,"E2.27.12.0"),sQuery(id+"F0.wireOp",EDGE,"E2.27.13.0"),sQuery(id+"F0.wireOp",EDGE,"E2.27.14.0"),sQuery(id+"F0.wireOp",EDGE,"E2.27.15.0"),sQuery(id+"F0.wireOp",EDGE,"E2.27.16.0"),sQuery(id+"F0.wireOp",EDGE,"E2.27.17.0"),sQuery(id+"F0.wireOp",EDGE,"E2.27.18.0"),sQuery(id+"F0.wireOp",EDGE,"E2.27.19.0"),sQuery(id+"F0.wireOp",EDGE,"E2.27.20.0"),sQuery(id+"F0.wireOp",EDGE,"E2.27.21.0"),sQuery(id+"F0.wireOp",EDGE,"E2.27.22.0"),sQuery(id+"F0.wireOp",EDGE,"E2.27.23.0"),sQuery(id+"F0.wireOp",EDGE,"E2.27.24.0"),sQuery(id+"F0.wireOp",EDGE,"E2.27.25.0"),sQuery(id+"F0.wireOp",EDGE,"E2.27.26.0"),sQuery(id+"F0.wireOp",EDGE,"E2.27.27.0"),sQuery(id+"F0.wireOp",EDGE,"E2.27.28.0"),sQuery(id+"F0.wireOp",EDGE,"E2.27.29.0"),sQuery(id+"F0.wireOp",EDGE,"E2.27.30.0"),sQuery(id+"F0.wireOp",EDGE,"E2.27.31.0"),sQuery(id+"F0.wireOp",EDGE,"E2.27.32.0"),sQuery(id+"F0.wireOp",EDGE,"E2.27.33.0"),sQuery(id+"F0.wireOp",EDGE,"E2.27.34.0"),sQuery(id+"F0.wireOp",EDGE,"E2.27.35.0"),sQuery(id+"F0.wireOp",EDGE,"E2.27.36.0"),sQuery(id+"F0.wireOp",EDGE,"E2.27.37.0"),sQuery(id+"F0.wireOp",EDGE,"E2.27.38.0"),sQuery(id+"F0.wireOp",EDGE,"E2.27.39.0"),sQuery(id+"F0.wireOp",EDGE,"E2.27.40.0"),sQuery(id+"F0.wireOp",EDGE,"E2.27.41.0"),sQuery(id+"F0.wireOp",EDGE,"E2.27.42.0"),sQuery(id+"F0.wireOp",EDGE,"E2.27.43.0"),sQuery(id+"F0.wireOp",EDGE,"E2.27.44.0"),sQuery(id+"F0.wireOp",EDGE,"E2.27.45.0"),sQuery(id+"F0.wireOp",EDGE,"E2.27.46.0"),sQuery(id+"F0.wireOp",EDGE,"E2.27.47.0"),sQuery(id+"F0.wireOp",EDGE,"E2.27.48.0"),sQuery(id+"F0.wireOp",EDGE,"E2.27.49.0"),sQuery(id+"F0.wireOp",EDGE,"E2.28.0.0"),sQuery(id+"F0.wireOp",EDGE,"E2.28.1.0"),sQuery(id+"F0.wireOp",EDGE,"E2.28.2.0"),sQuery(id+"F0.wireOp",EDGE,"E2.28.3.0"),sQuery(id+"F0.wireOp",EDGE,"E2.28.4.0"),sQuery(id+"F0.wireOp",EDGE,"E2.28.5.0"),sQuery(id+"F0.wireOp",EDGE,"E2.28.6.0"),sQuery(id+"F0.wireOp",EDGE,"E2.28.7.0"),sQuery(id+"F0.wireOp",EDGE,"E2.28.8.0"),sQuery(id+"F0.wireOp",EDGE,"E2.28.9.0"),sQuery(id+"F0.wireOp",EDGE,"E2.28.10.0"),sQuery(id+"F0.wireOp",EDGE,"E2.28.11.0"),sQuery(id+"F0.wireOp",EDGE,"E2.28.12.0"),sQuery(id+"F0.wireOp",EDGE,"E2.28.13.0"),sQuery(id+"F0.wireOp",EDGE,"E2.28.14.0"),sQuery(id+"F0.wireOp",EDGE,"E2.28.15.0"),sQuery(id+"F0.wireOp",EDGE,"E2.28.16.0"),sQuery(id+"F0.wireOp",EDGE,"E2.28.17.0"),sQuery(id+"F0.wireOp",EDGE,"E2.28.18.0"),sQuery(id+"F0.wireOp",EDGE,"E2.28.19.0"),sQuery(id+"F0.wireOp",EDGE,"E2.28.20.0"),sQuery(id+"F0.wireOp",EDGE,"E2.28.21.0"),sQuery(id+"F0.wireOp",EDGE,"E2.28.22.0"),sQuery(id+"F0.wireOp",EDGE,"E2.28.23.0"),sQuery(id+"F0.wireOp",EDGE,"E2.28.24.0"),sQuery(id+"F0.wireOp",EDGE,"E2.28.25.0"),sQuery(id+"F0.wireOp",EDGE,"E2.28.26.0"),sQuery(id+"F0.wireOp",EDGE,"E2.28.27.0"),sQuery(id+"F0.wireOp",EDGE,"E2.28.28.0"),sQuery(id+"F0.wireOp",EDGE,"E2.28.29.0"),sQuery(id+"F0.wireOp",EDGE,"E2.28.30.0"),sQuery(id+"F0.wireOp",EDGE,"E2.28.31.0"),sQuery(id+"F0.wireOp",EDGE,"E2.28.32.0"),sQuery(id+"F0.wireOp",EDGE,"E2.28.33.0"),sQuery(id+"F0.wireOp",EDGE,"E2.28.34.0"),sQuery(id+"F0.wireOp",EDGE,"E2.28.35.0"),sQuery(id+"F0.wireOp",EDGE,"E2.28.36.0"),sQuery(id+"F0.wireOp",EDGE,"E2.28.37.0"),sQuery(id+"F0.wireOp",EDGE,"E2.28.38.0"),sQuery(id+"F0.wireOp",EDGE,"E2.28.39.0"),sQuery(id+"F0.wireOp",EDGE,"E2.28.40.0"),sQuery(id+"F0.wireOp",EDGE,"E2.28.41.0"),sQuery(id+"F0.wireOp",EDGE,"E2.28.42.0"),sQuery(id+"F0.wireOp",EDGE,"E2.28.43.0"),sQuery(id+"F0.wireOp",EDGE,"E2.28.44.0"),sQuery(id+"F0.wireOp",EDGE,"E2.28.45.0"),sQuery(id+"F0.wireOp",EDGE,"E2.28.46.0"),sQuery(id+"F0.wireOp",EDGE,"E2.28.47.0"),sQuery(id+"F0.wireOp",EDGE,"E2.28.48.0"),sQuery(id+"F0.wireOp",EDGE,"E2.28.49.0"),sQuery(id+"F0.wireOp",EDGE,"E2.29.0.0"),sQuery(id+"F0.wireOp",EDGE,"E2.29.1.0"),sQuery(id+"F0.wireOp",EDGE,"E2.29.2.0"),sQuery(id+"F0.wireOp",EDGE,"E2.29.3.0"),sQuery(id+"F0.wireOp",EDGE,"E2.29.4.0"),sQuery(id+"F0.wireOp",EDGE,"E2.29.5.0"),sQuery(id+"F0.wireOp",EDGE,"E2.29.6.0"),sQuery(id+"F0.wireOp",EDGE,"E2.29.7.0"),sQuery(id+"F0.wireOp",EDGE,"E2.29.8.0"),sQuery(id+"F0.wireOp",EDGE,"E2.29.9.0"),sQuery(id+"F0.wireOp",EDGE,"E2.29.10.0"),sQuery(id+"F0.wireOp",EDGE,"E2.29.11.0"),sQuery(id+"F0.wireOp",EDGE,"E2.29.12.0"),sQuery(id+"F0.wireOp",EDGE,"E2.29.13.0"),sQuery(id+"F0.wireOp",EDGE,"E2.29.14.0"),sQuery(id+"F0.wireOp",EDGE,"E2.29.15.0"),sQuery(id+"F0.wireOp",EDGE,"E2.29.16.0"),sQuery(id+"F0.wireOp",EDGE,"E2.29.17.0"),sQuery(id+"F0.wireOp",EDGE,"E2.29.18.0"),sQuery(id+"F0.wireOp",EDGE,"E2.29.19.0"),sQuery(id+"F0.wireOp",EDGE,"E2.29.20.0"),sQuery(id+"F0.wireOp",EDGE,"E2.29.21.0"),sQuery(id+"F0.wireOp",EDGE,"E2.29.22.0"),sQuery(id+"F0.wireOp",EDGE,"E2.29.23.0"),sQuery(id+"F0.wireOp",EDGE,"E2.29.24.0"),sQuery(id+"F0.wireOp",EDGE,"E2.29.25.0"),sQuery(id+"F0.wireOp",EDGE,"E2.29.26.0"),sQuery(id+"F0.wireOp",EDGE,"E2.29.27.0"),sQuery(id+"F0.wireOp",EDGE,"E2.29.28.0"),sQuery(id+"F0.wireOp",EDGE,"E2.29.29.0"),sQuery(id+"F0.wireOp",EDGE,"E2.29.30.0"),sQuery(id+"F0.wireOp",EDGE,"E2.29.31.0"),sQuery(id+"F0.wireOp",EDGE,"E2.29.32.0"),sQuery(id+"F0.wireOp",EDGE,"E2.29.33.0"),sQuery(id+"F0.wireOp",EDGE,"E2.29.34.0"),sQuery(id+"F0.wireOp",EDGE,"E2.29.35.0"),sQuery(id+"F0.wireOp",EDGE,"E2.29.36.0"),sQuery(id+"F0.wireOp",EDGE,"E2.29.37.0"),sQuery(id+"F0.wireOp",EDGE,"E2.29.38.0"),sQuery(id+"F0.wireOp",EDGE,"E2.29.39.0"),sQuery(id+"F0.wireOp",EDGE,"E2.29.40.0"),sQuery(id+"F0.wireOp",EDGE,"E2.29.41.0"),sQuery(id+"F0.wireOp",EDGE,"E2.29.42.0"),sQuery(id+"F0.wireOp",EDGE,"E2.29.43.0"),sQuery(id+"F0.wireOp",EDGE,"E2.29.44.0"),sQuery(id+"F0.wireOp",EDGE,"E2.29.45.0"),sQuery(id+"F0.wireOp",EDGE,"E2.29.46.0"),sQuery(id+"F0.wireOp",EDGE,"E2.29.47.0"),sQuery(id+"F0.wireOp",EDGE,"E2.29.48.0"),sQuery(id+"F0.wireOp",EDGE,"E2.29.49.0"),sQuery(id+"F0.wireOp",EDGE,"E2.30.0.0"),sQuery(id+"F0.wireOp",EDGE,"E2.30.1.0"),sQuery(id+"F0.wireOp",EDGE,"E2.30.2.0"),sQuery(id+"F0.wireOp",EDGE,"E2.30.3.0"),sQuery(id+"F0.wireOp",EDGE,"E2.30.4.0"),sQuery(id+"F0.wireOp",EDGE,"E2.30.5.0"),sQuery(id+"F0.wireOp",EDGE,"E2.30.6.0"),sQuery(id+"F0.wireOp",EDGE,"E2.30.7.0"),sQuery(id+"F0.wireOp",EDGE,"E2.30.8.0"),sQuery(id+"F0.wireOp",EDGE,"E2.30.9.0"),sQuery(id+"F0.wireOp",EDGE,"E2.30.10.0"),sQuery(id+"F0.wireOp",EDGE,"E2.30.11.0"),sQuery(id+"F0.wireOp",EDGE,"E2.30.12.0"),sQuery(id+"F0.wireOp",EDGE,"E2.30.13.0"),sQuery(id+"F0.wireOp",EDGE,"E2.30.14.0"),sQuery(id+"F0.wireOp",EDGE,"E2.30.15.0"),sQuery(id+"F0.wireOp",EDGE,"E2.30.16.0"),sQuery(id+"F0.wireOp",EDGE,"E2.30.17.0"),sQuery(id+"F0.wireOp",EDGE,"E2.30.18.0"),sQuery(id+"F0.wireOp",EDGE,"E2.30.19.0"),sQuery(id+"F0.wireOp",EDGE,"E2.30.20.0"),sQuery(id+"F0.wireOp",EDGE,"E2.30.21.0"),sQuery(id+"F0.wireOp",EDGE,"E2.30.22.0"),sQuery(id+"F0.wireOp",EDGE,"E2.30.23.0"),sQuery(id+"F0.wireOp",EDGE,"E2.30.24.0"),sQuery(id+"F0.wireOp",EDGE,"E2.30.25.0"),sQuery(id+"F0.wireOp",EDGE,"E2.30.26.0"),sQuery(id+"F0.wireOp",EDGE,"E2.30.27.0"),sQuery(id+"F0.wireOp",EDGE,"E2.30.28.0"),sQuery(id+"F0.wireOp",EDGE,"E2.30.29.0"),sQuery(id+"F0.wireOp",EDGE,"E2.30.30.0"),sQuery(id+"F0.wireOp",EDGE,"E2.30.31.0"),sQuery(id+"F0.wireOp",EDGE,"E2.30.32.0"),sQuery(id+"F0.wireOp",EDGE,"E2.30.33.0"),sQuery(id+"F0.wireOp",EDGE,"E2.30.34.0"),sQuery(id+"F0.wireOp",EDGE,"E2.30.35.0"),sQuery(id+"F0.wireOp",EDGE,"E2.30.36.0"),sQuery(id+"F0.wireOp",EDGE,"E2.30.37.0"),sQuery(id+"F0.wireOp",EDGE,"E2.30.38.0"),sQuery(id+"F0.wireOp",EDGE,"E2.30.39.0"),sQuery(id+"F0.wireOp",EDGE,"E2.30.40.0"),sQuery(id+"F0.wireOp",EDGE,"E2.30.41.0"),sQuery(id+"F0.wireOp",EDGE,"E2.30.42.0"),sQuery(id+"F0.wireOp",EDGE,"E2.30.43.0"),sQuery(id+"F0.wireOp",EDGE,"E2.30.44.0"),sQuery(id+"F0.wireOp",EDGE,"E2.30.45.0"),sQuery(id+"F0.wireOp",EDGE,"E2.30.46.0"),sQuery(id+"F0.wireOp",EDGE,"E2.30.47.0"),sQuery(id+"F0.wireOp",EDGE,"E2.30.48.0"),sQuery(id+"F0.wireOp",EDGE,"E2.30.49.0"),sQuery(id+"F0.wireOp",EDGE,"E2.31.0.0"),sQuery(id+"F0.wireOp",EDGE,"E2.31.1.0"),sQuery(id+"F0.wireOp",EDGE,"E2.31.2.0"),sQuery(id+"F0.wireOp",EDGE,"E2.31.3.0"),sQuery(id+"F0.wireOp",EDGE,"E2.31.4.0"),sQuery(id+"F0.wireOp",EDGE,"E2.31.5.0"),sQuery(id+"F0.wireOp",EDGE,"E2.31.6.0"),sQuery(id+"F0.wireOp",EDGE,"E2.31.7.0"),sQuery(id+"F0.wireOp",EDGE,"E2.31.8.0"),sQuery(id+"F0.wireOp",EDGE,"E2.31.9.0"),sQuery(id+"F0.wireOp",EDGE,"E2.31.10.0"),sQuery(id+"F0.wireOp",EDGE,"E2.31.11.0"),sQuery(id+"F0.wireOp",EDGE,"E2.31.12.0"),sQuery(id+"F0.wireOp",EDGE,"E2.31.13.0"),sQuery(id+"F0.wireOp",EDGE,"E2.31.14.0"),sQuery(id+"F0.wireOp",EDGE,"E2.31.15.0"),sQuery(id+"F0.wireOp",EDGE,"E2.31.16.0"),sQuery(id+"F0.wireOp",EDGE,"E2.31.17.0"),sQuery(id+"F0.wireOp",EDGE,"E2.31.18.0"),sQuery(id+"F0.wireOp",EDGE,"E2.31.19.0"),sQuery(id+"F0.wireOp",EDGE,"E2.31.20.0"),sQuery(id+"F0.wireOp",EDGE,"E2.31.21.0"),sQuery(id+"F0.wireOp",EDGE,"E2.31.22.0"),sQuery(id+"F0.wireOp",EDGE,"E2.31.23.0"),sQuery(id+"F0.wireOp",EDGE,"E2.31.24.0"),sQuery(id+"F0.wireOp",EDGE,"E2.31.25.0"),sQuery(id+"F0.wireOp",EDGE,"E2.31.26.0"),sQuery(id+"F0.wireOp",EDGE,"E2.31.27.0"),sQuery(id+"F0.wireOp",EDGE,"E2.31.28.0"),sQuery(id+"F0.wireOp",EDGE,"E2.31.29.0"),sQuery(id+"F0.wireOp",EDGE,"E2.31.30.0"),sQuery(id+"F0.wireOp",EDGE,"E2.31.31.0"),sQuery(id+"F0.wireOp",EDGE,"E2.31.32.0"),sQuery(id+"F0.wireOp",EDGE,"E2.31.33.0"),sQuery(id+"F0.wireOp",EDGE,"E2.31.34.0"),sQuery(id+"F0.wireOp",EDGE,"E2.31.35.0"),sQuery(id+"F0.wireOp",EDGE,"E2.31.36.0"),sQuery(id+"F0.wireOp",EDGE,"E2.31.37.0"),sQuery(id+"F0.wireOp",EDGE,"E2.31.38.0"),sQuery(id+"F0.wireOp",EDGE,"E2.31.39.0"),sQuery(id+"F0.wireOp",EDGE,"E2.31.40.0"),sQuery(id+"F0.wireOp",EDGE,"E2.31.41.0"),sQuery(id+"F0.wireOp",EDGE,"E2.31.42.0"),sQuery(id+"F0.wireOp",EDGE,"E2.31.43.0"),sQuery(id+"F0.wireOp",EDGE,"E2.31.44.0"),sQuery(id+"F0.wireOp",EDGE,"E2.31.45.0"),sQuery(id+"F0.wireOp",EDGE,"E2.31.46.0"),sQuery(id+"F0.wireOp",EDGE,"E2.31.47.0"),sQuery(id+"F0.wireOp",EDGE,"E2.31.48.0"),sQuery(id+"F0.wireOp",EDGE,"E2.31.49.0"),sQuery(id+"F0.wireOp",EDGE,"E2.32.0.0"),sQuery(id+"F0.wireOp",EDGE,"E2.32.1.0"),sQuery(id+"F0.wireOp",EDGE,"E2.32.2.0"),sQuery(id+"F0.wireOp",EDGE,"E2.32.3.0"),sQuery(id+"F0.wireOp",EDGE,"E2.32.4.0"),sQuery(id+"F0.wireOp",EDGE,"E2.32.5.0"),sQuery(id+"F0.wireOp",EDGE,"E2.32.6.0"),sQuery(id+"F0.wireOp",EDGE,"E2.32.7.0"),sQuery(id+"F0.wireOp",EDGE,"E2.32.8.0"),sQuery(id+"F0.wireOp",EDGE,"E2.32.9.0"),sQuery(id+"F0.wireOp",EDGE,"E2.32.10.0"),sQuery(id+"F0.wireOp",EDGE,"E2.32.11.0"),sQuery(id+"F0.wireOp",EDGE,"E2.32.12.0"),sQuery(id+"F0.wireOp",EDGE,"E2.32.13.0"),sQuery(id+"F0.wireOp",EDGE,"E2.32.14.0"),sQuery(id+"F0.wireOp",EDGE,"E2.32.15.0"),sQuery(id+"F0.wireOp",EDGE,"E2.32.16.0"),sQuery(id+"F0.wireOp",EDGE,"E2.32.17.0"),sQuery(id+"F0.wireOp",EDGE,"E2.32.18.0"),sQuery(id+"F0.wireOp",EDGE,"E2.32.19.0"),sQuery(id+"F0.wireOp",EDGE,"E2.32.20.0"),sQuery(id+"F0.wireOp",EDGE,"E2.32.21.0"),sQuery(id+"F0.wireOp",EDGE,"E2.32.22.0"),sQuery(id+"F0.wireOp",EDGE,"E2.32.23.0"),sQuery(id+"F0.wireOp",EDGE,"E2.32.24.0"),sQuery(id+"F0.wireOp",EDGE,"E2.32.25.0"),sQuery(id+"F0.wireOp",EDGE,"E2.32.26.0"),sQuery(id+"F0.wireOp",EDGE,"E2.32.27.0"),sQuery(id+"F0.wireOp",EDGE,"E2.32.28.0"),sQuery(id+"F0.wireOp",EDGE,"E2.32.29.0"),sQuery(id+"F0.wireOp",EDGE,"E2.32.30.0"),sQuery(id+"F0.wireOp",EDGE,"E2.32.31.0"),sQuery(id+"F0.wireOp",EDGE,"E2.32.32.0"),sQuery(id+"F0.wireOp",EDGE,"E2.32.33.0"),sQuery(id+"F0.wireOp",EDGE,"E2.32.34.0"),sQuery(id+"F0.wireOp",EDGE,"E2.32.35.0"),sQuery(id+"F0.wireOp",EDGE,"E2.32.36.0"),sQuery(id+"F0.wireOp",EDGE,"E2.32.37.0"),sQuery(id+"F0.wireOp",EDGE,"E2.32.38.0"),sQuery(id+"F0.wireOp",EDGE,"E2.32.39.0"),sQuery(id+"F0.wireOp",EDGE,"E2.32.40.0"),sQuery(id+"F0.wireOp",EDGE,"E2.32.41.0"),sQuery(id+"F0.wireOp",EDGE,"E2.32.42.0"),sQuery(id+"F0.wireOp",EDGE,"E2.32.43.0"),sQuery(id+"F0.wireOp",EDGE,"E2.32.44.0"),sQuery(id+"F0.wireOp",EDGE,"E2.32.45.0"),sQuery(id+"F0.wireOp",EDGE,"E2.32.46.0"),sQuery(id+"F0.wireOp",EDGE,"E2.32.47.0"),sQuery(id+"F0.wireOp",EDGE,"E2.32.48.0"),sQuery(id+"F0.wireOp",EDGE,"E2.32.49.0"),sQuery(id+"F0.wireOp",EDGE,"E2.33.0.0"),sQuery(id+"F0.wireOp",EDGE,"E2.33.1.0"),sQuery(id+"F0.wireOp",EDGE,"E2.33.2.0"),sQuery(id+"F0.wireOp",EDGE,"E2.33.3.0"),sQuery(id+"F0.wireOp",EDGE,"E2.33.4.0"),sQuery(id+"F0.wireOp",EDGE,"E2.33.5.0"),sQuery(id+"F0.wireOp",EDGE,"E2.33.6.0"),sQuery(id+"F0.wireOp",EDGE,"E2.33.7.0"),sQuery(id+"F0.wireOp",EDGE,"E2.33.8.0"),sQuery(id+"F0.wireOp",EDGE,"E2.33.9.0"),sQuery(id+"F0.wireOp",EDGE,"E2.33.10.0"),sQuery(id+"F0.wireOp",EDGE,"E2.33.11.0"),sQuery(id+"F0.wireOp",EDGE,"E2.33.12.0"),sQuery(id+"F0.wireOp",EDGE,"E2.33.13.0"),sQuery(id+"F0.wireOp",EDGE,"E2.33.14.0"),sQuery(id+"F0.wireOp",EDGE,"E2.33.15.0"),sQuery(id+"F0.wireOp",EDGE,"E2.33.16.0"),sQuery(id+"F0.wireOp",EDGE,"E2.33.17.0"),sQuery(id+"F0.wireOp",EDGE,"E2.33.18.0"),sQuery(id+"F0.wireOp",EDGE,"E2.33.19.0"),sQuery(id+"F0.wireOp",EDGE,"E2.33.20.0"),sQuery(id+"F0.wireOp",EDGE,"E2.33.21.0"),sQuery(id+"F0.wireOp",EDGE,"E2.33.22.0"),sQuery(id+"F0.wireOp",EDGE,"E2.33.23.0"),sQuery(id+"F0.wireOp",EDGE,"E2.33.24.0"),sQuery(id+"F0.wireOp",EDGE,"E2.33.25.0"),sQuery(id+"F0.wireOp",EDGE,"E2.33.26.0"),sQuery(id+"F0.wireOp",EDGE,"E2.33.27.0"),sQuery(id+"F0.wireOp",EDGE,"E2.33.28.0"),sQuery(id+"F0.wireOp",EDGE,"E2.33.29.0"),sQuery(id+"F0.wireOp",EDGE,"E2.33.30.0"),sQuery(id+"F0.wireOp",EDGE,"E2.33.31.0"),sQuery(id+"F0.wireOp",EDGE,"E2.33.32.0"),sQuery(id+"F0.wireOp",EDGE,"E2.33.33.0"),sQuery(id+"F0.wireOp",EDGE,"E2.33.34.0"),sQuery(id+"F0.wireOp",EDGE,"E2.33.35.0"),sQuery(id+"F0.wireOp",EDGE,"E2.33.36.0"),sQuery(id+"F0.wireOp",EDGE,"E2.33.37.0"),sQuery(id+"F0.wireOp",EDGE,"E2.33.38.0"),sQuery(id+"F0.wireOp",EDGE,"E2.33.39.0"),sQuery(id+"F0.wireOp",EDGE,"E2.33.40.0"),sQuery(id+"F0.wireOp",EDGE,"E2.33.41.0"),sQuery(id+"F0.wireOp",EDGE,"E2.33.42.0"),sQuery(id+"F0.wireOp",EDGE,"E2.33.43.0"),sQuery(id+"F0.wireOp",EDGE,"E2.33.44.0"),sQuery(id+"F0.wireOp",EDGE,"E2.33.45.0"),sQuery(id+"F0.wireOp",EDGE,"E2.33.46.0"),sQuery(id+"F0.wireOp",EDGE,"E2.33.47.0"),sQuery(id+"F0.wireOp",EDGE,"E2.33.48.0"),sQuery(id+"F0.wireOp",EDGE,"E2.33.49.0"),sQuery(id+"F0.wireOp",EDGE,"E2.34.0.0"),sQuery(id+"F0.wireOp",EDGE,"E2.34.1.0"),sQuery(id+"F0.wireOp",EDGE,"E2.34.2.0"),sQuery(id+"F0.wireOp",EDGE,"E2.34.3.0"),sQuery(id+"F0.wireOp",EDGE,"E2.34.4.0"),sQuery(id+"F0.wireOp",EDGE,"E2.34.5.0"),sQuery(id+"F0.wireOp",EDGE,"E2.34.6.0"),sQuery(id+"F0.wireOp",EDGE,"E2.34.7.0"),sQuery(id+"F0.wireOp",EDGE,"E2.34.8.0"),sQuery(id+"F0.wireOp",EDGE,"E2.34.9.0"),sQuery(id+"F0.wireOp",EDGE,"E2.34.10.0"),sQuery(id+"F0.wireOp",EDGE,"E2.34.11.0"),sQuery(id+"F0.wireOp",EDGE,"E2.34.12.0"),sQuery(id+"F0.wireOp",EDGE,"E2.34.13.0"),sQuery(id+"F0.wireOp",EDGE,"E2.34.14.0"),sQuery(id+"F0.wireOp",EDGE,"E2.34.15.0"),sQuery(id+"F0.wireOp",EDGE,"E2.34.16.0"),sQuery(id+"F0.wireOp",EDGE,"E2.34.17.0"),sQuery(id+"F0.wireOp",EDGE,"E2.34.18.0"),sQuery(id+"F0.wireOp",EDGE,"E2.34.19.0"),sQuery(id+"F0.wireOp",EDGE,"E2.34.20.0"),sQuery(id+"F0.wireOp",EDGE,"E2.34.21.0"),sQuery(id+"F0.wireOp",EDGE,"E2.34.22.0"),sQuery(id+"F0.wireOp",EDGE,"E2.34.23.0"),sQuery(id+"F0.wireOp",EDGE,"E2.34.24.0"),sQuery(id+"F0.wireOp",EDGE,"E2.34.25.0"),sQuery(id+"F0.wireOp",EDGE,"E2.34.26.0"),sQuery(id+"F0.wireOp",EDGE,"E2.34.27.0"),sQuery(id+"F0.wireOp",EDGE,"E2.34.28.0"),sQuery(id+"F0.wireOp",EDGE,"E2.34.29.0"),sQuery(id+"F0.wireOp",EDGE,"E2.34.30.0"),sQuery(id+"F0.wireOp",EDGE,"E2.34.31.0"),sQuery(id+"F0.wireOp",EDGE,"E2.34.32.0"),sQuery(id+"F0.wireOp",EDGE,"E2.34.33.0"),sQuery(id+"F0.wireOp",EDGE,"E2.34.34.0"),sQuery(id+"F0.wireOp",EDGE,"E2.34.35.0"),sQuery(id+"F0.wireOp",EDGE,"E2.34.36.0"),sQuery(id+"F0.wireOp",EDGE,"E2.34.37.0"),sQuery(id+"F0.wireOp",EDGE,"E2.34.38.0"),sQuery(id+"F0.wireOp",EDGE,"E2.34.39.0"),sQuery(id+"F0.wireOp",EDGE,"E2.34.40.0"),sQuery(id+"F0.wireOp",EDGE,"E2.34.41.0"),sQuery(id+"F0.wireOp",EDGE,"E2.34.42.0"),sQuery(id+"F0.wireOp",EDGE,"E2.34.43.0"),sQuery(id+"F0.wireOp",EDGE,"E2.34.44.0"),sQuery(id+"F0.wireOp",EDGE,"E2.34.45.0"),sQuery(id+"F0.wireOp",EDGE,"E2.34.46.0"),sQuery(id+"F0.wireOp",EDGE,"E2.34.47.0"),sQuery(id+"F0.wireOp",EDGE,"E2.34.48.0"),sQuery(id+"F0.wireOp",EDGE,"E2.34.49.0"),sQuery(id+"F0.wireOp",EDGE,"E2.35.0.0"),sQuery(id+"F0.wireOp",EDGE,"E2.35.1.0"),sQuery(id+"F0.wireOp",EDGE,"E2.35.2.0"),sQuery(id+"F0.wireOp",EDGE,"E2.35.3.0"),sQuery(id+"F0.wireOp",EDGE,"E2.35.4.0"),sQuery(id+"F0.wireOp",EDGE,"E2.35.5.0"),sQuery(id+"F0.wireOp",EDGE,"E2.35.6.0"),sQuery(id+"F0.wireOp",EDGE,"E2.35.7.0"),sQuery(id+"F0.wireOp",EDGE,"E2.35.8.0"),sQuery(id+"F0.wireOp",EDGE,"E2.35.9.0"),sQuery(id+"F0.wireOp",EDGE,"E2.35.10.0"),sQuery(id+"F0.wireOp",EDGE,"E2.35.11.0"),sQuery(id+"F0.wireOp",EDGE,"E2.35.12.0"),sQuery(id+"F0.wireOp",EDGE,"E2.35.13.0"),sQuery(id+"F0.wireOp",EDGE,"E2.35.14.0"),sQuery(id+"F0.wireOp",EDGE,"E2.35.15.0"),sQuery(id+"F0.wireOp",EDGE,"E2.35.16.0"),sQuery(id+"F0.wireOp",EDGE,"E2.35.17.0"),sQuery(id+"F0.wireOp",EDGE,"E2.35.18.0"),sQuery(id+"F0.wireOp",EDGE,"E2.35.19.0"),sQuery(id+"F0.wireOp",EDGE,"E2.35.20.0"),sQuery(id+"F0.wireOp",EDGE,"E2.35.21.0"),sQuery(id+"F0.wireOp",EDGE,"E2.35.22.0"),sQuery(id+"F0.wireOp",EDGE,"E2.35.23.0"),sQuery(id+"F0.wireOp",EDGE,"E2.35.24.0"),sQuery(id+"F0.wireOp",EDGE,"E2.35.25.0"),sQuery(id+"F0.wireOp",EDGE,"E2.35.26.0"),sQuery(id+"F0.wireOp",EDGE,"E2.35.27.0"),sQuery(id+"F0.wireOp",EDGE,"E2.35.28.0"),sQuery(id+"F0.wireOp",EDGE,"E2.35.29.0"),sQuery(id+"F0.wireOp",EDGE,"E2.35.30.0"),sQuery(id+"F0.wireOp",EDGE,"E2.35.31.0"),sQuery(id+"F0.wireOp",EDGE,"E2.35.32.0"),sQuery(id+"F0.wireOp",EDGE,"E2.35.33.0"),sQuery(id+"F0.wireOp",EDGE,"E2.35.34.0"),sQuery(id+"F0.wireOp",EDGE,"E2.35.35.0"),sQuery(id+"F0.wireOp",EDGE,"E2.35.36.0"),sQuery(id+"F0.wireOp",EDGE,"E2.35.37.0"),sQuery(id+"F0.wireOp",EDGE,"E2.35.38.0"),sQuery(id+"F0.wireOp",EDGE,"E2.35.39.0"),sQuery(id+"F0.wireOp",EDGE,"E2.35.40.0"),sQuery(id+"F0.wireOp",EDGE,"E2.35.41.0"),sQuery(id+"F0.wireOp",EDGE,"E2.35.42.0"),sQuery(id+"F0.wireOp",EDGE,"E2.35.43.0"),sQuery(id+"F0.wireOp",EDGE,"E2.35.44.0"),sQuery(id+"F0.wireOp",EDGE,"E2.35.45.0"),sQuery(id+"F0.wireOp",EDGE,"E2.35.46.0"),sQuery(id+"F0.wireOp",EDGE,"E2.35.47.0"),sQuery(id+"F0.wireOp",EDGE,"E2.35.48.0"),sQuery(id+"F0.wireOp",EDGE,"E2.35.49.0"),sQuery(id+"F0.wireOp",EDGE,"E2.36.0.0"),sQuery(id+"F0.wireOp",EDGE,"E2.36.1.0"),sQuery(id+"F0.wireOp",EDGE,"E2.36.2.0"),sQuery(id+"F0.wireOp",EDGE,"E2.36.3.0"),sQuery(id+"F0.wireOp",EDGE,"E2.36.4.0"),sQuery(id+"F0.wireOp",EDGE,"E2.36.5.0"),sQuery(id+"F0.wireOp",EDGE,"E2.36.6.0"),sQuery(id+"F0.wireOp",EDGE,"E2.36.7.0"),sQuery(id+"F0.wireOp",EDGE,"E2.36.8.0"),sQuery(id+"F0.wireOp",EDGE,"E2.36.9.0"),sQuery(id+"F0.wireOp",EDGE,"E2.36.10.0"),sQuery(id+"F0.wireOp",EDGE,"E2.36.11.0"),sQuery(id+"F0.wireOp",EDGE,"E2.36.12.0"),sQuery(id+"F0.wireOp",EDGE,"E2.36.13.0"),sQuery(id+"F0.wireOp",EDGE,"E2.36.14.0"),sQuery(id+"F0.wireOp",EDGE,"E2.36.15.0"),sQuery(id+"F0.wireOp",EDGE,"E2.36.16.0"),sQuery(id+"F0.wireOp",EDGE,"E2.36.17.0"),sQuery(id+"F0.wireOp",EDGE,"E2.36.18.0"),sQuery(id+"F0.wireOp",EDGE,"E2.36.19.0"),sQuery(id+"F0.wireOp",EDGE,"E2.36.20.0"),sQuery(id+"F0.wireOp",EDGE,"E2.36.21.0"),sQuery(id+"F0.wireOp",EDGE,"E2.36.22.0"),sQuery(id+"F0.wireOp",EDGE,"E2.36.23.0"),sQuery(id+"F0.wireOp",EDGE,"E2.36.24.0"),sQuery(id+"F0.wireOp",EDGE,"E2.36.25.0"),sQuery(id+"F0.wireOp",EDGE,"E2.36.26.0"),sQuery(id+"F0.wireOp",EDGE,"E2.36.27.0"),sQuery(id+"F0.wireOp",EDGE,"E2.36.28.0"),sQuery(id+"F0.wireOp",EDGE,"E2.36.29.0"),sQuery(id+"F0.wireOp",EDGE,"E2.36.30.0"),sQuery(id+"F0.wireOp",EDGE,"E2.36.31.0"),sQuery(id+"F0.wireOp",EDGE,"E2.36.32.0"),sQuery(id+"F0.wireOp",EDGE,"E2.36.33.0"),sQuery(id+"F0.wireOp",EDGE,"E2.36.34.0"),sQuery(id+"F0.wireOp",EDGE,"E2.36.35.0"),sQuery(id+"F0.wireOp",EDGE,"E2.36.36.0"),sQuery(id+"F0.wireOp",EDGE,"E2.36.37.0"),sQuery(id+"F0.wireOp",EDGE,"E2.36.38.0"),sQuery(id+"F0.wireOp",EDGE,"E2.36.39.0"),sQuery(id+"F0.wireOp",EDGE,"E2.36.40.0"),sQuery(id+"F0.wireOp",EDGE,"E2.36.41.0"),sQuery(id+"F0.wireOp",EDGE,"E2.36.42.0"),sQuery(id+"F0.wireOp",EDGE,"E2.36.43.0"),sQuery(id+"F0.wireOp",EDGE,"E2.36.44.0"),sQuery(id+"F0.wireOp",EDGE,"E2.36.45.0"),sQuery(id+"F0.wireOp",EDGE,"E2.36.46.0"),sQuery(id+"F0.wireOp",EDGE,"E2.36.47.0"),sQuery(id+"F0.wireOp",EDGE,"E2.36.48.0"),sQuery(id+"F0.wireOp",EDGE,"E2.36.49.0"),sQuery(id+"F0.wireOp",EDGE,"E2.37.0.0"),sQuery(id+"F0.wireOp",EDGE,"E2.37.1.0"),sQuery(id+"F0.wireOp",EDGE,"E2.37.2.0"),sQuery(id+"F0.wireOp",EDGE,"E2.37.3.0"),sQuery(id+"F0.wireOp",EDGE,"E2.37.4.0"),sQuery(id+"F0.wireOp",EDGE,"E2.37.5.0"),sQuery(id+"F0.wireOp",EDGE,"E2.37.6.0"),sQuery(id+"F0.wireOp",EDGE,"E2.37.7.0"),sQuery(id+"F0.wireOp",EDGE,"E2.37.8.0"),sQuery(id+"F0.wireOp",EDGE,"E2.37.9.0"),sQuery(id+"F0.wireOp",EDGE,"E2.37.10.0"),sQuery(id+"F0.wireOp",EDGE,"E2.37.11.0"),sQuery(id+"F0.wireOp",EDGE,"E2.37.12.0"),sQuery(id+"F0.wireOp",EDGE,"E2.37.13.0"),sQuery(id+"F0.wireOp",EDGE,"E2.37.14.0"),sQuery(id+"F0.wireOp",EDGE,"E2.37.15.0"),sQuery(id+"F0.wireOp",EDGE,"E2.37.16.0"),sQuery(id+"F0.wireOp",EDGE,"E2.37.17.0"),sQuery(id+"F0.wireOp",EDGE,"E2.37.18.0"),sQuery(id+"F0.wireOp",EDGE,"E2.37.19.0"),sQuery(id+"F0.wireOp",EDGE,"E2.37.20.0"),sQuery(id+"F0.wireOp",EDGE,"E2.37.21.0"),sQuery(id+"F0.wireOp",EDGE,"E2.37.22.0"),sQuery(id+"F0.wireOp",EDGE,"E2.37.23.0"),sQuery(id+"F0.wireOp",EDGE,"E2.37.24.0"),sQuery(id+"F0.wireOp",EDGE,"E2.37.25.0"),sQuery(id+"F0.wireOp",EDGE,"E2.37.26.0"),sQuery(id+"F0.wireOp",EDGE,"E2.37.27.0"),sQuery(id+"F0.wireOp",EDGE,"E2.37.28.0"),sQuery(id+"F0.wireOp",EDGE,"E2.37.29.0"),sQuery(id+"F0.wireOp",EDGE,"E2.37.30.0"),sQuery(id+"F0.wireOp",EDGE,"E2.37.31.0"),sQuery(id+"F0.wireOp",EDGE,"E2.37.32.0"),sQuery(id+"F0.wireOp",EDGE,"E2.37.33.0"),sQuery(id+"F0.wireOp",EDGE,"E2.37.34.0"),sQuery(id+"F0.wireOp",EDGE,"E2.37.35.0"),sQuery(id+"F0.wireOp",EDGE,"E2.37.36.0"),sQuery(id+"F0.wireOp",EDGE,"E2.37.37.0"),sQuery(id+"F0.wireOp",EDGE,"E2.37.38.0"),sQuery(id+"F0.wireOp",EDGE,"E2.37.39.0"),sQuery(id+"F0.wireOp",EDGE,"E2.37.40.0"),sQuery(id+"F0.wireOp",EDGE,"E2.37.41.0"),sQuery(id+"F0.wireOp",EDGE,"E2.37.42.0"),sQuery(id+"F0.wireOp",EDGE,"E2.37.43.0"),sQuery(id+"F0.wireOp",EDGE,"E2.37.44.0"),sQuery(id+"F0.wireOp",EDGE,"E2.37.45.0"),sQuery(id+"F0.wireOp",EDGE,"E2.37.46.0"),sQuery(id+"F0.wireOp",EDGE,"E2.37.47.0"),sQuery(id+"F0.wireOp",EDGE,"E2.37.48.0"),sQuery(id+"F0.wireOp",EDGE,"E2.37.49.0"),sQuery(id+"F0.wireOp",EDGE,"E2.38.0.0"),sQuery(id+"F0.wireOp",EDGE,"E2.38.1.0"),sQuery(id+"F0.wireOp",EDGE,"E2.38.2.0"),sQuery(id+"F0.wireOp",EDGE,"E2.38.3.0"),sQuery(id+"F0.wireOp",EDGE,"E2.38.4.0"),sQuery(id+"F0.wireOp",EDGE,"E2.38.5.0"),sQuery(id+"F0.wireOp",EDGE,"E2.38.6.0"),sQuery(id+"F0.wireOp",EDGE,"E2.38.7.0"),sQuery(id+"F0.wireOp",EDGE,"E2.38.8.0"),sQuery(id+"F0.wireOp",EDGE,"E2.38.9.0"),sQuery(id+"F0.wireOp",EDGE,"E2.38.10.0"),sQuery(id+"F0.wireOp",EDGE,"E2.38.11.0"),sQuery(id+"F0.wireOp",EDGE,"E2.38.12.0"),sQuery(id+"F0.wireOp",EDGE,"E2.38.13.0"),sQuery(id+"F0.wireOp",EDGE,"E2.38.14.0"),sQuery(id+"F0.wireOp",EDGE,"E2.38.15.0"),sQuery(id+"F0.wireOp",EDGE,"E2.38.16.0"),sQuery(id+"F0.wireOp",EDGE,"E2.38.17.0"),sQuery(id+"F0.wireOp",EDGE,"E2.38.18.0"),sQuery(id+"F0.wireOp",EDGE,"E2.38.19.0"),sQuery(id+"F0.wireOp",EDGE,"E2.38.20.0"),sQuery(id+"F0.wireOp",EDGE,"E2.38.21.0"),sQuery(id+"F0.wireOp",EDGE,"E2.38.22.0"),sQuery(id+"F0.wireOp",EDGE,"E2.38.23.0"),sQuery(id+"F0.wireOp",EDGE,"E2.38.24.0"),sQuery(id+"F0.wireOp",EDGE,"E2.38.25.0"),sQuery(id+"F0.wireOp",EDGE,"E2.38.26.0"),sQuery(id+"F0.wireOp",EDGE,"E2.38.27.0"),sQuery(id+"F0.wireOp",EDGE,"E2.38.28.0"),sQuery(id+"F0.wireOp",EDGE,"E2.38.29.0"),sQuery(id+"F0.wireOp",EDGE,"E2.38.30.0"),sQuery(id+"F0.wireOp",EDGE,"E2.38.31.0"),sQuery(id+"F0.wireOp",EDGE,"E2.38.32.0"),sQuery(id+"F0.wireOp",EDGE,"E2.38.33.0"),sQuery(id+"F0.wireOp",EDGE,"E2.38.34.0"),sQuery(id+"F0.wireOp",EDGE,"E2.38.35.0"),sQuery(id+"F0.wireOp",EDGE,"E2.38.36.0"),sQuery(id+"F0.wireOp",EDGE,"E2.38.37.0"),sQuery(id+"F0.wireOp",EDGE,"E2.38.38.0"),sQuery(id+"F0.wireOp",EDGE,"E2.38.39.0"),sQuery(id+"F0.wireOp",EDGE,"E2.38.40.0"),sQuery(id+"F0.wireOp",EDGE,"E2.38.41.0"),sQuery(id+"F0.wireOp",EDGE,"E2.38.42.0"),sQuery(id+"F0.wireOp",EDGE,"E2.38.43.0"),sQuery(id+"F0.wireOp",EDGE,"E2.38.44.0"),sQuery(id+"F0.wireOp",EDGE,"E2.38.45.0"),sQuery(id+"F0.wireOp",EDGE,"E2.38.46.0"),sQuery(id+"F0.wireOp",EDGE,"E2.38.47.0"),sQuery(id+"F0.wireOp",EDGE,"E2.38.48.0"),sQuery(id+"F0.wireOp",EDGE,"E2.38.49.0"),sQuery(id+"F0.wireOp",EDGE,"E2.39.0.0"),sQuery(id+"F0.wireOp",EDGE,"E2.39.1.0"),sQuery(id+"F0.wireOp",EDGE,"E2.39.2.0"),sQuery(id+"F0.wireOp",EDGE,"E2.39.3.0"),sQuery(id+"F0.wireOp",EDGE,"E2.39.4.0"),sQuery(id+"F0.wireOp",EDGE,"E2.39.5.0"),sQuery(id+"F0.wireOp",EDGE,"E2.39.6.0"),sQuery(id+"F0.wireOp",EDGE,"E2.39.7.0"),sQuery(id+"F0.wireOp",EDGE,"E2.39.8.0"),sQuery(id+"F0.wireOp",EDGE,"E2.39.9.0"),sQuery(id+"F0.wireOp",EDGE,"E2.39.10.0"),sQuery(id+"F0.wireOp",EDGE,"E2.39.11.0"),sQuery(id+"F0.wireOp",EDGE,"E2.39.12.0"),sQuery(id+"F0.wireOp",EDGE,"E2.39.13.0"),sQuery(id+"F0.wireOp",EDGE,"E2.39.14.0"),sQuery(id+"F0.wireOp",EDGE,"E2.39.15.0"),sQuery(id+"F0.wireOp",EDGE,"E2.39.16.0"),sQuery(id+"F0.wireOp",EDGE,"E2.39.17.0"),sQuery(id+"F0.wireOp",EDGE,"E2.39.18.0"),sQuery(id+"F0.wireOp",EDGE,"E2.39.19.0"),sQuery(id+"F0.wireOp",EDGE,"E2.39.20.0"),sQuery(id+"F0.wireOp",EDGE,"E2.39.21.0"),sQuery(id+"F0.wireOp",EDGE,"E2.39.22.0"),sQuery(id+"F0.wireOp",EDGE,"E2.39.23.0"),sQuery(id+"F0.wireOp",EDGE,"E2.39.24.0"),sQuery(id+"F0.wireOp",EDGE,"E2.39.25.0"),sQuery(id+"F0.wireOp",EDGE,"E2.39.26.0"),sQuery(id+"F0.wireOp",EDGE,"E2.39.27.0"),sQuery(id+"F0.wireOp",EDGE,"E2.39.28.0"),sQuery(id+"F0.wireOp",EDGE,"E2.39.29.0"),sQuery(id+"F0.wireOp",EDGE,"E2.39.30.0"),sQuery(id+"F0.wireOp",EDGE,"E2.39.31.0"),sQuery(id+"F0.wireOp",EDGE,"E2.39.32.0"),sQuery(id+"F0.wireOp",EDGE,"E2.39.33.0"),sQuery(id+"F0.wireOp",EDGE,"E2.39.34.0"),sQuery(id+"F0.wireOp",EDGE,"E2.39.35.0"),sQuery(id+"F0.wireOp",EDGE,"E2.39.36.0"),sQuery(id+"F0.wireOp",EDGE,"E2.39.37.0"),sQuery(id+"F0.wireOp",EDGE,"E2.39.38.0"),sQuery(id+"F0.wireOp",EDGE,"E2.39.39.0"),sQuery(id+"F0.wireOp",EDGE,"E2.39.40.0"),sQuery(id+"F0.wireOp",EDGE,"E2.39.41.0"),sQuery(id+"F0.wireOp",EDGE,"E2.39.42.0"),sQuery(id+"F0.wireOp",EDGE,"E2.39.43.0"),sQuery(id+"F0.wireOp",EDGE,"E2.39.44.0"),sQuery(id+"F0.wireOp",EDGE,"E2.39.45.0"),sQuery(id+"F0.wireOp",EDGE,"E2.39.46.0"),sQuery(id+"F0.wireOp",EDGE,"E2.39.47.0"),sQuery(id+"F0.wireOp",EDGE,"E2.39.48.0"),sQuery(id+"F0.wireOp",EDGE,"E2.39.49.0"),sQuery(id+"F0.wireOp",EDGE,"E2.40.0.0"),sQuery(id+"F0.wireOp",EDGE,"E2.40.1.0"),sQuery(id+"F0.wireOp",EDGE,"E2.40.2.0"),sQuery(id+"F0.wireOp",EDGE,"E2.40.3.0"),sQuery(id+"F0.wireOp",EDGE,"E2.40.4.0"),sQuery(id+"F0.wireOp",EDGE,"E2.40.5.0"),sQuery(id+"F0.wireOp",EDGE,"E2.40.6.0"),sQuery(id+"F0.wireOp",EDGE,"E2.40.7.0"),sQuery(id+"F0.wireOp",EDGE,"E2.40.8.0"),sQuery(id+"F0.wireOp",EDGE,"E2.40.9.0"),sQuery(id+"F0.wireOp",EDGE,"E2.40.10.0"),sQuery(id+"F0.wireOp",EDGE,"E2.40.11.0"),sQuery(id+"F0.wireOp",EDGE,"E2.40.12.0"),sQuery(id+"F0.wireOp",EDGE,"E2.40.13.0"),sQuery(id+"F0.wireOp",EDGE,"E2.40.14.0"),sQuery(id+"F0.wireOp",EDGE,"E2.40.15.0"),sQuery(id+"F0.wireOp",EDGE,"E2.40.16.0"),sQuery(id+"F0.wireOp",EDGE,"E2.40.17.0"),sQuery(id+"F0.wireOp",EDGE,"E2.40.18.0"),sQuery(id+"F0.wireOp",EDGE,"E2.40.19.0"),sQuery(id+"F0.wireOp",EDGE,"E2.40.20.0"),sQuery(id+"F0.wireOp",EDGE,"E2.40.21.0"),sQuery(id+"F0.wireOp",EDGE,"E2.40.22.0"),sQuery(id+"F0.wireOp",EDGE,"E2.40.23.0"),sQuery(id+"F0.wireOp",EDGE,"E2.40.24.0"),sQuery(id+"F0.wireOp",EDGE,"E2.40.25.0"),sQuery(id+"F0.wireOp",EDGE,"E2.40.26.0"),sQuery(id+"F0.wireOp",EDGE,"E2.40.27.0"),sQuery(id+"F0.wireOp",EDGE,"E2.40.28.0"),sQuery(id+"F0.wireOp",EDGE,"E2.40.29.0"),sQuery(id+"F0.wireOp",EDGE,"E2.40.30.0"),sQuery(id+"F0.wireOp",EDGE,"E2.40.31.0"),sQuery(id+"F0.wireOp",EDGE,"E2.40.32.0"),sQuery(id+"F0.wireOp",EDGE,"E2.40.33.0"),sQuery(id+"F0.wireOp",EDGE,"E2.40.34.0"),sQuery(id+"F0.wireOp",EDGE,"E2.40.35.0"),sQuery(id+"F0.wireOp",EDGE,"E2.40.36.0"),sQuery(id+"F0.wireOp",EDGE,"E2.40.37.0"),sQuery(id+"F0.wireOp",EDGE,"E2.40.38.0"),sQuery(id+"F0.wireOp",EDGE,"E2.40.39.0"),sQuery(id+"F0.wireOp",EDGE,"E2.40.40.0"),sQuery(id+"F0.wireOp",EDGE,"E2.40.41.0"),sQuery(id+"F0.wireOp",EDGE,"E2.40.42.0"),sQuery(id+"F0.wireOp",EDGE,"E2.40.43.0"),sQuery(id+"F0.wireOp",EDGE,"E2.40.44.0"),sQuery(id+"F0.wireOp",EDGE,"E2.40.45.0"),sQuery(id+"F0.wireOp",EDGE,"E2.40.46.0"),sQuery(id+"F0.wireOp",EDGE,"E2.40.47.0"),sQuery(id+"F0.wireOp",EDGE,"E2.40.48.0"),sQuery(id+"F0.wireOp",EDGE,"E2.40.49.0"),sQuery(id+"F0.wireOp",EDGE,"E2.41.0.0"),sQuery(id+"F0.wireOp",EDGE,"E2.41.1.0"),sQuery(id+"F0.wireOp",EDGE,"E2.41.2.0"),sQuery(id+"F0.wireOp",EDGE,"E2.41.3.0"),sQuery(id+"F0.wireOp",EDGE,"E2.41.4.0"),sQuery(id+"F0.wireOp",EDGE,"E2.41.5.0"),sQuery(id+"F0.wireOp",EDGE,"E2.41.6.0"),sQuery(id+"F0.wireOp",EDGE,"E2.41.7.0"),sQuery(id+"F0.wireOp",EDGE,"E2.41.8.0"),sQuery(id+"F0.wireOp",EDGE,"E2.41.9.0"),sQuery(id+"F0.wireOp",EDGE,"E2.41.10.0"),sQuery(id+"F0.wireOp",EDGE,"E2.41.11.0"),sQuery(id+"F0.wireOp",EDGE,"E2.41.12.0"),sQuery(id+"F0.wireOp",EDGE,"E2.41.13.0"),sQuery(id+"F0.wireOp",EDGE,"E2.41.14.0"),sQuery(id+"F0.wireOp",EDGE,"E2.41.15.0"),sQuery(id+"F0.wireOp",EDGE,"E2.41.16.0"),sQuery(id+"F0.wireOp",EDGE,"E2.41.17.0"),sQuery(id+"F0.wireOp",EDGE,"E2.41.18.0"),sQuery(id+"F0.wireOp",EDGE,"E2.41.19.0"),sQuery(id+"F0.wireOp",EDGE,"E2.41.20.0"),sQuery(id+"F0.wireOp",EDGE,"E2.41.21.0"),sQuery(id+"F0.wireOp",EDGE,"E2.41.22.0"),sQuery(id+"F0.wireOp",EDGE,"E2.41.23.0"),sQuery(id+"F0.wireOp",EDGE,"E2.41.24.0"),sQuery(id+"F0.wireOp",EDGE,"E2.41.25.0"),sQuery(id+"F0.wireOp",EDGE,"E2.41.26.0"),sQuery(id+"F0.wireOp",EDGE,"E2.41.27.0"),sQuery(id+"F0.wireOp",EDGE,"E2.41.28.0"),sQuery(id+"F0.wireOp",EDGE,"E2.41.29.0"),sQuery(id+"F0.wireOp",EDGE,"E2.41.30.0"),sQuery(id+"F0.wireOp",EDGE,"E2.41.31.0"),sQuery(id+"F0.wireOp",EDGE,"E2.41.32.0"),sQuery(id+"F0.wireOp",EDGE,"E2.41.33.0"),sQuery(id+"F0.wireOp",EDGE,"E2.41.34.0"),sQuery(id+"F0.wireOp",EDGE,"E2.41.35.0"),sQuery(id+"F0.wireOp",EDGE,"E2.41.36.0"),sQuery(id+"F0.wireOp",EDGE,"E2.41.37.0"),sQuery(id+"F0.wireOp",EDGE,"E2.41.38.0"),sQuery(id+"F0.wireOp",EDGE,"E2.41.39.0"),sQuery(id+"F0.wireOp",EDGE,"E2.41.40.0"),sQuery(id+"F0.wireOp",EDGE,"E2.41.41.0"),sQuery(id+"F0.wireOp",EDGE,"E2.41.42.0"),sQuery(id+"F0.wireOp",EDGE,"E2.41.43.0"),sQuery(id+"F0.wireOp",EDGE,"E2.41.44.0"),sQuery(id+"F0.wireOp",EDGE,"E2.41.45.0"),sQuery(id+"F0.wireOp",EDGE,"E2.41.46.0"),sQuery(id+"F0.wireOp",EDGE,"E2.41.47.0"),sQuery(id+"F0.wireOp",EDGE,"E2.41.48.0"),sQuery(id+"F0.wireOp",EDGE,"E2.41.49.0"),sQuery(id+"F0.wireOp",EDGE,"E2.42.0.0"),sQuery(id+"F0.wireOp",EDGE,"E2.42.1.0"),sQuery(id+"F0.wireOp",EDGE,"E2.42.2.0"),sQuery(id+"F0.wireOp",EDGE,"E2.42.3.0"),sQuery(id+"F0.wireOp",EDGE,"E2.42.4.0"),sQuery(id+"F0.wireOp",EDGE,"E2.42.5.0"),sQuery(id+"F0.wireOp",EDGE,"E2.42.6.0"),sQuery(id+"F0.wireOp",EDGE,"E2.42.7.0"),sQuery(id+"F0.wireOp",EDGE,"E2.42.8.0"),sQuery(id+"F0.wireOp",EDGE,"E2.42.9.0"),sQuery(id+"F0.wireOp",EDGE,"E2.42.10.0"),sQuery(id+"F0.wireOp",EDGE,"E2.42.11.0"),sQuery(id+"F0.wireOp",EDGE,"E2.42.12.0"),sQuery(id+"F0.wireOp",EDGE,"E2.42.13.0"),sQuery(id+"F0.wireOp",EDGE,"E2.42.14.0"),sQuery(id+"F0.wireOp",EDGE,"E2.42.15.0"),sQuery(id+"F0.wireOp",EDGE,"E2.42.16.0"),sQuery(id+"F0.wireOp",EDGE,"E2.42.17.0"),sQuery(id+"F0.wireOp",EDGE,"E2.42.18.0"),sQuery(id+"F0.wireOp",EDGE,"E2.42.19.0"),sQuery(id+"F0.wireOp",EDGE,"E2.42.20.0"),sQuery(id+"F0.wireOp",EDGE,"E2.42.21.0"),sQuery(id+"F0.wireOp",EDGE,"E2.42.22.0"),sQuery(id+"F0.wireOp",EDGE,"E2.42.23.0"),sQuery(id+"F0.wireOp",EDGE,"E2.42.24.0"),sQuery(id+"F0.wireOp",EDGE,"E2.42.25.0"),sQuery(id+"F0.wireOp",EDGE,"E2.42.26.0"),sQuery(id+"F0.wireOp",EDGE,"E2.42.27.0"),sQuery(id+"F0.wireOp",EDGE,"E2.42.28.0"),sQuery(id+"F0.wireOp",EDGE,"E2.42.29.0"),sQuery(id+"F0.wireOp",EDGE,"E2.42.30.0"),sQuery(id+"F0.wireOp",EDGE,"E2.42.31.0"),sQuery(id+"F0.wireOp",EDGE,"E2.42.32.0"),sQuery(id+"F0.wireOp",EDGE,"E2.42.33.0"),sQuery(id+"F0.wireOp",EDGE,"E2.42.34.0"),sQuery(id+"F0.wireOp",EDGE,"E2.42.35.0"),sQuery(id+"F0.wireOp",EDGE,"E2.42.36.0"),sQuery(id+"F0.wireOp",EDGE,"E2.42.37.0"),sQuery(id+"F0.wireOp",EDGE,"E2.42.38.0"),sQuery(id+"F0.wireOp",EDGE,"E2.42.39.0"),sQuery(id+"F0.wireOp",EDGE,"E2.42.40.0"),sQuery(id+"F0.wireOp",EDGE,"E2.42.41.0"),sQuery(id+"F0.wireOp",EDGE,"E2.42.42.0"),sQuery(id+"F0.wireOp",EDGE,"E2.42.43.0"),sQuery(id+"F0.wireOp",EDGE,"E2.42.44.0"),sQuery(id+"F0.wireOp",EDGE,"E2.42.45.0"),sQuery(id+"F0.wireOp",EDGE,"E2.42.46.0"),sQuery(id+"F0.wireOp",EDGE,"E2.42.47.0"),sQuery(id+"F0.wireOp",EDGE,"E2.42.48.0"),sQuery(id+"F0.wireOp",EDGE,"E2.42.49.0"),sQuery(id+"F0.wireOp",EDGE,"E2.43.0.0"),sQuery(id+"F0.wireOp",EDGE,"E2.43.1.0"),sQuery(id+"F0.wireOp",EDGE,"E2.43.2.0"),sQuery(id+"F0.wireOp",EDGE,"E2.43.3.0"),sQuery(id+"F0.wireOp",EDGE,"E2.43.4.0"),sQuery(id+"F0.wireOp",EDGE,"E2.43.5.0"),sQuery(id+"F0.wireOp",EDGE,"E2.43.6.0"),sQuery(id+"F0.wireOp",EDGE,"E2.43.7.0"),sQuery(id+"F0.wireOp",EDGE,"E2.43.8.0"),sQuery(id+"F0.wireOp",EDGE,"E2.43.9.0"),sQuery(id+"F0.wireOp",EDGE,"E2.43.10.0"),sQuery(id+"F0.wireOp",EDGE,"E2.43.11.0"),sQuery(id+"F0.wireOp",EDGE,"E2.43.12.0"),sQuery(id+"F0.wireOp",EDGE,"E2.43.13.0"),sQuery(id+"F0.wireOp",EDGE,"E2.43.14.0"),sQuery(id+"F0.wireOp",EDGE,"E2.43.15.0"),sQuery(id+"F0.wireOp",EDGE,"E2.43.16.0"),sQuery(id+"F0.wireOp",EDGE,"E2.43.17.0"),sQuery(id+"F0.wireOp",EDGE,"E2.43.18.0"),sQuery(id+"F0.wireOp",EDGE,"E2.43.19.0"),sQuery(id+"F0.wireOp",EDGE,"E2.43.20.0"),sQuery(id+"F0.wireOp",EDGE,"E2.43.21.0"),sQuery(id+"F0.wireOp",EDGE,"E2.43.22.0"),sQuery(id+"F0.wireOp",EDGE,"E2.43.23.0"),sQuery(id+"F0.wireOp",EDGE,"E2.43.24.0"),sQuery(id+"F0.wireOp",EDGE,"E2.43.25.0"),sQuery(id+"F0.wireOp",EDGE,"E2.43.26.0"),sQuery(id+"F0.wireOp",EDGE,"E2.43.27.0"),sQuery(id+"F0.wireOp",EDGE,"E2.43.28.0"),sQuery(id+"F0.wireOp",EDGE,"E2.43.29.0"),sQuery(id+"F0.wireOp",EDGE,"E2.43.30.0"),sQuery(id+"F0.wireOp",EDGE,"E2.43.31.0"),sQuery(id+"F0.wireOp",EDGE,"E2.43.32.0"),sQuery(id+"F0.wireOp",EDGE,"E2.43.33.0"),sQuery(id+"F0.wireOp",EDGE,"E2.43.34.0"),sQuery(id+"F0.wireOp",EDGE,"E2.43.35.0"),sQuery(id+"F0.wireOp",EDGE,"E2.43.36.0"),sQuery(id+"F0.wireOp",EDGE,"E2.43.37.0"),sQuery(id+"F0.wireOp",EDGE,"E2.43.38.0"),sQuery(id+"F0.wireOp",EDGE,"E2.43.39.0"),sQuery(id+"F0.wireOp",EDGE,"E2.43.40.0"),sQuery(id+"F0.wireOp",EDGE,"E2.43.41.0"),sQuery(id+"F0.wireOp",EDGE,"E2.43.42.0"),sQuery(id+"F0.wireOp",EDGE,"E2.43.43.0"),sQuery(id+"F0.wireOp",EDGE,"E2.43.44.0"),sQuery(id+"F0.wireOp",EDGE,"E2.43.45.0"),sQuery(id+"F0.wireOp",EDGE,"E2.43.46.0"),sQuery(id+"F0.wireOp",EDGE,"E2.43.47.0"),sQuery(id+"F0.wireOp",EDGE,"E2.43.48.0"),sQuery(id+"F0.wireOp",EDGE,"E2.43.49.0"),sQuery(id+"F0.wireOp",EDGE,"E2.44.0.0"),sQuery(id+"F0.wireOp",EDGE,"E2.44.1.0"),sQuery(id+"F0.wireOp",EDGE,"E2.44.2.0"),sQuery(id+"F0.wireOp",EDGE,"E2.44.3.0"),sQuery(id+"F0.wireOp",EDGE,"E2.44.4.0"),sQuery(id+"F0.wireOp",EDGE,"E2.44.5.0"),sQuery(id+"F0.wireOp",EDGE,"E2.44.6.0"),sQuery(id+"F0.wireOp",EDGE,"E2.44.7.0"),sQuery(id+"F0.wireOp",EDGE,"E2.44.8.0"),sQuery(id+"F0.wireOp",EDGE,"E2.44.9.0"),sQuery(id+"F0.wireOp",EDGE,"E2.44.10.0"),sQuery(id+"F0.wireOp",EDGE,"E2.44.11.0"),sQuery(id+"F0.wireOp",EDGE,"E2.44.12.0"),sQuery(id+"F0.wireOp",EDGE,"E2.44.13.0"),sQuery(id+"F0.wireOp",EDGE,"E2.44.14.0"),sQuery(id+"F0.wireOp",EDGE,"E2.44.15.0"),sQuery(id+"F0.wireOp",EDGE,"E2.44.16.0"),sQuery(id+"F0.wireOp",EDGE,"E2.44.17.0"),sQuery(id+"F0.wireOp",EDGE,"E2.44.18.0"),sQuery(id+"F0.wireOp",EDGE,"E2.44.19.0"),sQuery(id+"F0.wireOp",EDGE,"E2.44.20.0"),sQuery(id+"F0.wireOp",EDGE,"E2.44.21.0"),sQuery(id+"F0.wireOp",EDGE,"E2.44.22.0"),sQuery(id+"F0.wireOp",EDGE,"E2.44.23.0"),sQuery(id+"F0.wireOp",EDGE,"E2.44.24.0"),sQuery(id+"F0.wireOp",EDGE,"E2.44.25.0"),sQuery(id+"F0.wireOp",EDGE,"E2.44.26.0"),sQuery(id+"F0.wireOp",EDGE,"E2.44.27.0"),sQuery(id+"F0.wireOp",EDGE,"E2.44.28.0"),sQuery(id+"F0.wireOp",EDGE,"E2.44.29.0"),sQuery(id+"F0.wireOp",EDGE,"E2.44.30.0"),sQuery(id+"F0.wireOp",EDGE,"E2.44.31.0"),sQuery(id+"F0.wireOp",EDGE,"E2.44.32.0"),sQuery(id+"F0.wireOp",EDGE,"E2.44.33.0"),sQuery(id+"F0.wireOp",EDGE,"E2.44.34.0"),sQuery(id+"F0.wireOp",EDGE,"E2.44.35.0"),sQuery(id+"F0.wireOp",EDGE,"E2.44.36.0"),sQuery(id+"F0.wireOp",EDGE,"E2.44.37.0"),sQuery(id+"F0.wireOp",EDGE,"E2.44.38.0"),sQuery(id+"F0.wireOp",EDGE,"E2.44.39.0"),sQuery(id+"F0.wireOp",EDGE,"E2.44.40.0"),sQuery(id+"F0.wireOp",EDGE,"E2.44.41.0"),sQuery(id+"F0.wireOp",EDGE,"E2.44.42.0"),sQuery(id+"F0.wireOp",EDGE,"E2.44.43.0"),sQuery(id+"F0.wireOp",EDGE,"E2.44.44.0"),sQuery(id+"F0.wireOp",EDGE,"E2.44.45.0"),sQuery(id+"F0.wireOp",EDGE,"E2.44.46.0"),sQuery(id+"F0.wireOp",EDGE,"E2.44.47.0"),sQuery(id+"F0.wireOp",EDGE,"E2.44.48.0"),sQuery(id+"F0.wireOp",EDGE,"E2.44.49.0"),sQuery(id+"F0.wireOp",EDGE,"E2.45.0.0"),sQuery(id+"F0.wireOp",EDGE,"E2.45.1.0"),sQuery(id+"F0.wireOp",EDGE,"E2.45.2.0"),sQuery(id+"F0.wireOp",EDGE,"E2.45.3.0"),sQuery(id+"F0.wireOp",EDGE,"E2.45.4.0"),sQuery(id+"F0.wireOp",EDGE,"E2.45.5.0"),sQuery(id+"F0.wireOp",EDGE,"E2.45.6.0"),sQuery(id+"F0.wireOp",EDGE,"E2.45.7.0"),sQuery(id+"F0.wireOp",EDGE,"E2.45.8.0"),sQuery(id+"F0.wireOp",EDGE,"E2.45.9.0"),sQuery(id+"F0.wireOp",EDGE,"E2.45.10.0"),sQuery(id+"F0.wireOp",EDGE,"E2.45.11.0"),sQuery(id+"F0.wireOp",EDGE,"E2.45.12.0"),sQuery(id+"F0.wireOp",EDGE,"E2.45.13.0"),sQuery(id+"F0.wireOp",EDGE,"E2.45.14.0"),sQuery(id+"F0.wireOp",EDGE,"E2.45.15.0"),sQuery(id+"F0.wireOp",EDGE,"E2.45.16.0"),sQuery(id+"F0.wireOp",EDGE,"E2.45.17.0"),sQuery(id+"F0.wireOp",EDGE,"E2.45.18.0"),sQuery(id+"F0.wireOp",EDGE,"E2.45.19.0"),sQuery(id+"F0.wireOp",EDGE,"E2.45.20.0"),sQuery(id+"F0.wireOp",EDGE,"E2.45.21.0"),sQuery(id+"F0.wireOp",EDGE,"E2.45.22.0"),sQuery(id+"F0.wireOp",EDGE,"E2.45.23.0"),sQuery(id+"F0.wireOp",EDGE,"E2.45.24.0"),sQuery(id+"F0.wireOp",EDGE,"E2.45.25.0"),sQuery(id+"F0.wireOp",EDGE,"E2.45.26.0"),sQuery(id+"F0.wireOp",EDGE,"E2.45.27.0"),sQuery(id+"F0.wireOp",EDGE,"E2.45.28.0"),sQuery(id+"F0.wireOp",EDGE,"E2.45.29.0"),sQuery(id+"F0.wireOp",EDGE,"E2.45.30.0"),sQuery(id+"F0.wireOp",EDGE,"E2.45.31.0"),sQuery(id+"F0.wireOp",EDGE,"E2.45.32.0"),sQuery(id+"F0.wireOp",EDGE,"E2.45.33.0"),sQuery(id+"F0.wireOp",EDGE,"E2.45.34.0"),sQuery(id+"F0.wireOp",EDGE,"E2.45.35.0"),sQuery(id+"F0.wireOp",EDGE,"E2.45.36.0"),sQuery(id+"F0.wireOp",EDGE,"E2.45.37.0"),sQuery(id+"F0.wireOp",EDGE,"E2.45.38.0"),sQuery(id+"F0.wireOp",EDGE,"E2.45.39.0"),sQuery(id+"F0.wireOp",EDGE,"E2.45.40.0"),sQuery(id+"F0.wireOp",EDGE,"E2.45.41.0"),sQuery(id+"F0.wireOp",EDGE,"E2.45.42.0"),sQuery(id+"F0.wireOp",EDGE,"E2.45.43.0"),sQuery(id+"F0.wireOp",EDGE,"E2.45.44.0"),sQuery(id+"F0.wireOp",EDGE,"E2.45.45.0"),sQuery(id+"F0.wireOp",EDGE,"E2.45.46.0"),sQuery(id+"F0.wireOp",EDGE,"E2.45.47.0"),sQuery(id+"F0.wireOp",EDGE,"E2.45.48.0"),sQuery(id+"F0.wireOp",EDGE,"E2.45.49.0"),sQuery(id+"F0.wireOp",EDGE,"E2.46.0.0"),sQuery(id+"F0.wireOp",EDGE,"E2.46.1.0"),sQuery(id+"F0.wireOp",EDGE,"E2.46.2.0"),sQuery(id+"F0.wireOp",EDGE,"E2.46.3.0"),sQuery(id+"F0.wireOp",EDGE,"E2.46.4.0"),sQuery(id+"F0.wireOp",EDGE,"E2.46.5.0"),sQuery(id+"F0.wireOp",EDGE,"E2.46.6.0"),sQuery(id+"F0.wireOp",EDGE,"E2.46.7.0"),sQuery(id+"F0.wireOp",EDGE,"E2.46.8.0"),sQuery(id+"F0.wireOp",EDGE,"E2.46.9.0"),sQuery(id+"F0.wireOp",EDGE,"E2.46.10.0"),sQuery(id+"F0.wireOp",EDGE,"E2.46.11.0"),sQuery(id+"F0.wireOp",EDGE,"E2.46.12.0"),sQuery(id+"F0.wireOp",EDGE,"E2.46.13.0"),sQuery(id+"F0.wireOp",EDGE,"E2.46.14.0"),sQuery(id+"F0.wireOp",EDGE,"E2.46.15.0"),sQuery(id+"F0.wireOp",EDGE,"E2.46.16.0"),sQuery(id+"F0.wireOp",EDGE,"E2.46.17.0"),sQuery(id+"F0.wireOp",EDGE,"E2.46.18.0"),sQuery(id+"F0.wireOp",EDGE,"E2.46.19.0"),sQuery(id+"F0.wireOp",EDGE,"E2.46.20.0"),sQuery(id+"F0.wireOp",EDGE,"E2.46.21.0"),sQuery(id+"F0.wireOp",EDGE,"E2.46.22.0"),sQuery(id+"F0.wireOp",EDGE,"E2.46.23.0"),sQuery(id+"F0.wireOp",EDGE,"E2.46.24.0"),sQuery(id+"F0.wireOp",EDGE,"E2.46.25.0"),sQuery(id+"F0.wireOp",EDGE,"E2.46.26.0"),sQuery(id+"F0.wireOp",EDGE,"E2.46.27.0"),sQuery(id+"F0.wireOp",EDGE,"E2.46.28.0"),sQuery(id+"F0.wireOp",EDGE,"E2.46.29.0"),sQuery(id+"F0.wireOp",EDGE,"E2.46.30.0"),sQuery(id+"F0.wireOp",EDGE,"E2.46.31.0"),sQuery(id+"F0.wireOp",EDGE,"E2.46.32.0"),sQuery(id+"F0.wireOp",EDGE,"E2.46.33.0"),sQuery(id+"F0.wireOp",EDGE,"E2.46.34.0"),sQuery(id+"F0.wireOp",EDGE,"E2.46.35.0"),sQuery(id+"F0.wireOp",EDGE,"E2.46.36.0"),sQuery(id+"F0.wireOp",EDGE,"E2.46.37.0"),sQuery(id+"F0.wireOp",EDGE,"E2.46.38.0"),sQuery(id+"F0.wireOp",EDGE,"E2.46.39.0"),sQuery(id+"F0.wireOp",EDGE,"E2.46.40.0"),sQuery(id+"F0.wireOp",EDGE,"E2.46.41.0"),sQuery(id+"F0.wireOp",EDGE,"E2.46.42.0"),sQuery(id+"F0.wireOp",EDGE,"E2.46.43.0"),sQuery(id+"F0.wireOp",EDGE,"E2.46.44.0"),sQuery(id+"F0.wireOp",EDGE,"E2.46.45.0"),sQuery(id+"F0.wireOp",EDGE,"E2.46.46.0"),sQuery(id+"F0.wireOp",EDGE,"E2.46.47.0"),sQuery(id+"F0.wireOp",EDGE,"E2.46.48.0"),sQuery(id+"F0.wireOp",EDGE,"E2.46.49.0"),sQuery(id+"F0.wireOp",EDGE,"E2.47.0.0"),sQuery(id+"F0.wireOp",EDGE,"E2.47.1.0"),sQuery(id+"F0.wireOp",EDGE,"E2.47.2.0"),sQuery(id+"F0.wireOp",EDGE,"E2.47.3.0"),sQuery(id+"F0.wireOp",EDGE,"E2.47.4.0"),sQuery(id+"F0.wireOp",EDGE,"E2.47.5.0"),sQuery(id+"F0.wireOp",EDGE,"E2.47.6.0"),sQuery(id+"F0.wireOp",EDGE,"E2.47.7.0"),sQuery(id+"F0.wireOp",EDGE,"E2.47.8.0"),sQuery(id+"F0.wireOp",EDGE,"E2.47.9.0"),sQuery(id+"F0.wireOp",EDGE,"E2.47.10.0"),sQuery(id+"F0.wireOp",EDGE,"E2.47.11.0"),sQuery(id+"F0.wireOp",EDGE,"E2.47.12.0"),sQuery(id+"F0.wireOp",EDGE,"E2.47.13.0"),sQuery(id+"F0.wireOp",EDGE,"E2.47.14.0"),sQuery(id+"F0.wireOp",EDGE,"E2.47.15.0"),sQuery(id+"F0.wireOp",EDGE,"E2.47.16.0"),sQuery(id+"F0.wireOp",EDGE,"E2.47.17.0"),sQuery(id+"F0.wireOp",EDGE,"E2.47.18.0"),sQuery(id+"F0.wireOp",EDGE,"E2.47.19.0"),sQuery(id+"F0.wireOp",EDGE,"E2.47.20.0"),sQuery(id+"F0.wireOp",EDGE,"E2.47.21.0"),sQuery(id+"F0.wireOp",EDGE,"E2.47.22.0"),sQuery(id+"F0.wireOp",EDGE,"E2.47.23.0"),sQuery(id+"F0.wireOp",EDGE,"E2.47.24.0"),sQuery(id+"F0.wireOp",EDGE,"E2.47.25.0"),sQuery(id+"F0.wireOp",EDGE,"E2.47.26.0"),sQuery(id+"F0.wireOp",EDGE,"E2.47.27.0"),sQuery(id+"F0.wireOp",EDGE,"E2.47.28.0"),sQuery(id+"F0.wireOp",EDGE,"E2.47.29.0"),sQuery(id+"F0.wireOp",EDGE,"E2.47.30.0"),sQuery(id+"F0.wireOp",EDGE,"E2.47.31.0"),sQuery(id+"F0.wireOp",EDGE,"E2.47.32.0"),sQuery(id+"F0.wireOp",EDGE,"E2.47.33.0"),sQuery(id+"F0.wireOp",EDGE,"E2.47.34.0"),sQuery(id+"F0.wireOp",EDGE,"E2.47.35.0"),sQuery(id+"F0.wireOp",EDGE,"E2.47.36.0"),sQuery(id+"F0.wireOp",EDGE,"E2.47.37.0"),sQuery(id+"F0.wireOp",EDGE,"E2.47.38.0"),sQuery(id+"F0.wireOp",EDGE,"E2.47.39.0"),sQuery(id+"F0.wireOp",EDGE,"E2.47.40.0"),sQuery(id+"F0.wireOp",EDGE,"E2.47.41.0"),sQuery(id+"F0.wireOp",EDGE,"E2.47.42.0"),sQuery(id+"F0.wireOp",EDGE,"E2.47.43.0"),sQuery(id+"F0.wireOp",EDGE,"E2.47.44.0"),sQuery(id+"F0.wireOp",EDGE,"E2.47.45.0"),sQuery(id+"F0.wireOp",EDGE,"E2.47.46.0"),sQuery(id+"F0.wireOp",EDGE,"E2.47.47.0"),sQuery(id+"F0.wireOp",EDGE,"E2.47.48.0"),sQuery(id+"F0.wireOp",EDGE,"E2.47.49.0"),sQuery(id+"F0.wireOp",EDGE,"E2.48.0.0"),sQuery(id+"F0.wireOp",EDGE,"E2.48.1.0"),sQuery(id+"F0.wireOp",EDGE,"E2.48.2.0"),sQuery(id+"F0.wireOp",EDGE,"E2.48.3.0"),sQuery(id+"F0.wireOp",EDGE,"E2.48.4.0"),sQuery(id+"F0.wireOp",EDGE,"E2.48.5.0"),sQuery(id+"F0.wireOp",EDGE,"E2.48.6.0"),sQuery(id+"F0.wireOp",EDGE,"E2.48.7.0"),sQuery(id+"F0.wireOp",EDGE,"E2.48.8.0"),sQuery(id+"F0.wireOp",EDGE,"E2.48.9.0"),sQuery(id+"F0.wireOp",EDGE,"E2.48.10.0"),sQuery(id+"F0.wireOp",EDGE,"E2.48.11.0"),sQuery(id+"F0.wireOp",EDGE,"E2.48.12.0"),sQuery(id+"F0.wireOp",EDGE,"E2.48.13.0"),sQuery(id+"F0.wireOp",EDGE,"E2.48.14.0"),sQuery(id+"F0.wireOp",EDGE,"E2.48.15.0"),sQuery(id+"F0.wireOp",EDGE,"E2.48.16.0"),sQuery(id+"F0.wireOp",EDGE,"E2.48.17.0"),sQuery(id+"F0.wireOp",EDGE,"E2.48.18.0"),sQuery(id+"F0.wireOp",EDGE,"E2.48.19.0"),sQuery(id+"F0.wireOp",EDGE,"E2.48.20.0"),sQuery(id+"F0.wireOp",EDGE,"E2.48.21.0"),sQuery(id+"F0.wireOp",EDGE,"E2.48.22.0"),sQuery(id+"F0.wireOp",EDGE,"E2.48.23.0"),sQuery(id+"F0.wireOp",EDGE,"E2.48.24.0"),sQuery(id+"F0.wireOp",EDGE,"E2.48.25.0"),sQuery(id+"F0.wireOp",EDGE,"E2.48.26.0"),sQuery(id+"F0.wireOp",EDGE,"E2.48.27.0"),sQuery(id+"F0.wireOp",EDGE,"E2.48.28.0"),sQuery(id+"F0.wireOp",EDGE,"E2.48.29.0"),sQuery(id+"F0.wireOp",EDGE,"E2.48.30.0"),sQuery(id+"F0.wireOp",EDGE,"E2.48.31.0"),sQuery(id+"F0.wireOp",EDGE,"E2.48.32.0"),sQuery(id+"F0.wireOp",EDGE,"E2.48.33.0"),sQuery(id+"F0.wireOp",EDGE,"E2.48.34.0"),sQuery(id+"F0.wireOp",EDGE,"E2.48.35.0"),sQuery(id+"F0.wireOp",EDGE,"E2.48.36.0"),sQuery(id+"F0.wireOp",EDGE,"E2.48.37.0"),sQuery(id+"F0.wireOp",EDGE,"E2.48.38.0"),sQuery(id+"F0.wireOp",EDGE,"E2.48.39.0"),sQuery(id+"F0.wireOp",EDGE,"E2.48.40.0"),sQuery(id+"F0.wireOp",EDGE,"E2.48.41.0"),sQuery(id+"F0.wireOp",EDGE,"E2.48.42.0"),sQuery(id+"F0.wireOp",EDGE,"E2.48.43.0"),sQuery(id+"F0.wireOp",EDGE,"E2.48.44.0"),sQuery(id+"F0.wireOp",EDGE,"E2.48.45.0"),sQuery(id+"F0.wireOp",EDGE,"E2.48.46.0"),sQuery(id+"F0.wireOp",EDGE,"E2.48.47.0"),sQuery(id+"F0.wireOp",EDGE,"E2.48.48.0"),sQuery(id+"F0.wireOp",EDGE,"E2.48.49.0"),sQuery(id+"F0.wireOp",EDGE,"E2.49.0.0"),sQuery(id+"F0.wireOp",EDGE,"E2.49.1.0"),sQuery(id+"F0.wireOp",EDGE,"E2.49.2.0"),sQuery(id+"F0.wireOp",EDGE,"E2.49.3.0"),sQuery(id+"F0.wireOp",EDGE,"E2.49.4.0"),sQuery(id+"F0.wireOp",EDGE,"E2.49.5.0"),sQuery(id+"F0.wireOp",EDGE,"E2.49.6.0"),sQuery(id+"F0.wireOp",EDGE,"E2.49.7.0"),sQuery(id+"F0.wireOp",EDGE,"E2.49.8.0"),sQuery(id+"F0.wireOp",EDGE,"E2.49.9.0"),sQuery(id+"F0.wireOp",EDGE,"E2.49.10.0"),sQuery(id+"F0.wireOp",EDGE,"E2.49.11.0"),sQuery(id+"F0.wireOp",EDGE,"E2.49.12.0"),sQuery(id+"F0.wireOp",EDGE,"E2.49.13.0"),sQuery(id+"F0.wireOp",EDGE,"E2.49.14.0"),sQuery(id+"F0.wireOp",EDGE,"E2.49.15.0"),sQuery(id+"F0.wireOp",EDGE,"E2.49.16.0"),sQuery(id+"F0.wireOp",EDGE,"E2.49.17.0"),sQuery(id+"F0.wireOp",EDGE,"E2.49.18.0"),sQuery(id+"F0.wireOp",EDGE,"E2.49.19.0"),sQuery(id+"F0.wireOp",EDGE,"E2.49.20.0"),sQuery(id+"F0.wireOp",EDGE,"E2.49.21.0"),sQuery(id+"F0.wireOp",EDGE,"E2.49.22.0"),sQuery(id+"F0.wireOp",EDGE,"E2.49.23.0"),sQuery(id+"F0.wireOp",EDGE,"E2.49.24.0"),sQuery(id+"F0.wireOp",EDGE,"E2.49.25.0"),sQuery(id+"F0.wireOp",EDGE,"E2.49.26.0"),sQuery(id+"F0.wireOp",EDGE,"E2.49.27.0"),sQuery(id+"F0.wireOp",EDGE,"E2.49.28.0"),sQuery(id+"F0.wireOp",EDGE,"E2.49.29.0"),sQuery(id+"F0.wireOp",EDGE,"E2.49.30.0"),sQuery(id+"F0.wireOp",EDGE,"E2.49.31.0"),sQuery(id+"F0.wireOp",EDGE,"E2.49.32.0"),sQuery(id+"F0.wireOp",EDGE,"E2.49.33.0"),sQuery(id+"F0.wireOp",EDGE,"E2.49.34.0"),sQuery(id+"F0.wireOp",EDGE,"E2.49.35.0"),sQuery(id+"F0.wireOp",EDGE,"E2.49.36.0"),sQuery(id+"F0.wireOp",EDGE,"E2.49.37.0"),sQuery(id+"F0.wireOp",EDGE,"E2.49.38.0"),sQuery(id+"F0.wireOp",EDGE,"E2.49.39.0"),sQuery(id+"F0.wireOp",EDGE,"E2.49.40.0"),sQuery(id+"F0.wireOp",EDGE,"E2.49.41.0"),sQuery(id+"F0.wireOp",EDGE,"E2.49.42.0"),sQuery(id+"F0.wireOp",EDGE,"E2.49.43.0"),sQuery(id+"F0.wireOp",EDGE,"E2.49.44.0"),sQuery(id+"F0.wireOp",EDGE,"E2.49.45.0"),sQuery(id+"F0.wireOp",EDGE,"E2.49.46.0"),sQuery(id+"F0.wireOp",EDGE,"E2.49.47.0"),sQuery(id+"F0.wireOp",EDGE,"E2.49.48.0"),sQuery(id+"F0.wireOp",EDGE,"E2.49.49.0"),sQuery(id+"F0.wireOp",EDGE,"E2.50.0.0"),sQuery(id+"F0.wireOp",EDGE,"E2.50.1.0"),sQuery(id+"F0.wireOp",EDGE,"E2.50.2.0"),sQuery(id+"F0.wireOp",EDGE,"E2.50.3.0"),sQuery(id+"F0.wireOp",EDGE,"E2.50.4.0"),sQuery(id+"F0.wireOp",EDGE,"E2.50.5.0"),sQuery(id+"F0.wireOp",EDGE,"E2.50.6.0"),sQuery(id+"F0.wireOp",EDGE,"E2.50.7.0"),sQuery(id+"F0.wireOp",EDGE,"E2.50.8.0"),sQuery(id+"F0.wireOp",EDGE,"E2.50.9.0"),sQuery(id+"F0.wireOp",EDGE,"E2.50.10.0"),sQuery(id+"F0.wireOp",EDGE,"E2.50.11.0"),sQuery(id+"F0.wireOp",EDGE,"E2.50.12.0"),sQuery(id+"F0.wireOp",EDGE,"E2.50.13.0"),sQuery(id+"F0.wireOp",EDGE,"E2.50.14.0"),sQuery(id+"F0.wireOp",EDGE,"E2.50.15.0"),sQuery(id+"F0.wireOp",EDGE,"E2.50.16.0"),sQuery(id+"F0.wireOp",EDGE,"E2.50.17.0"),sQuery(id+"F0.wireOp",EDGE,"E2.50.18.0"),sQuery(id+"F0.wireOp",EDGE,"E2.50.19.0"),sQuery(id+"F0.wireOp",EDGE,"E2.50.20.0"),sQuery(id+"F0.wireOp",EDGE,"E2.50.21.0"),sQuery(id+"F0.wireOp",EDGE,"E2.50.22.0"),sQuery(id+"F0.wireOp",EDGE,"E2.50.23.0"),sQuery(id+"F0.wireOp",EDGE,"E2.50.24.0"),sQuery(id+"F0.wireOp",EDGE,"E2.50.25.0"),sQuery(id+"F0.wireOp",EDGE,"E2.50.26.0"),sQuery(id+"F0.wireOp",EDGE,"E2.50.27.0"),sQuery(id+"F0.wireOp",EDGE,"E2.50.28.0"),sQuery(id+"F0.wireOp",EDGE,"E2.50.29.0"),sQuery(id+"F0.wireOp",EDGE,"E2.50.30.0"),sQuery(id+"F0.wireOp",EDGE,"E2.50.31.0"),sQuery(id+"F0.wireOp",EDGE,"E2.50.32.0"),sQuery(id+"F0.wireOp",EDGE,"E2.50.33.0"),sQuery(id+"F0.wireOp",EDGE,"E2.50.34.0"),sQuery(id+"F0.wireOp",EDGE,"E2.50.35.0"),sQuery(id+"F0.wireOp",EDGE,"E2.50.36.0"),sQuery(id+"F0.wireOp",EDGE,"E2.50.37.0"),sQuery(id+"F0.wireOp",EDGE,"E2.50.38.0"),sQuery(id+"F0.wireOp",EDGE,"E2.50.39.0"),sQuery(id+"F0.wireOp",EDGE,"E2.50.40.0"),sQuery(id+"F0.wireOp",EDGE,"E2.50.41.0"),sQuery(id+"F0.wireOp",EDGE,"E2.50.42.0"),sQuery(id+"F0.wireOp",EDGE,"E2.50.43.0"),sQuery(id+"F0.wireOp",EDGE,"E2.50.44.0"),sQuery(id+"F0.wireOp",EDGE,"E2.50.45.0"),sQuery(id+"F0.wireOp",EDGE,"E2.50.46.0"),sQuery(id+"F0.wireOp",EDGE,"E2.50.47.0"),sQuery(id+"F0.wireOp",EDGE,"E2.50.48.0"),sQuery(id+"F0.wireOp",EDGE,"E2.50.49.0"),sQuery(id+"F0.wireOp",EDGE,"E2.51.0.0"),sQuery(id+"F0.wireOp",EDGE,"E2.51.1.0"),sQuery(id+"F0.wireOp",EDGE,"E2.51.2.0"),sQuery(id+"F0.wireOp",EDGE,"E2.51.3.0"),sQuery(id+"F0.wireOp",EDGE,"E2.51.4.0"),sQuery(id+"F0.wireOp",EDGE,"E2.51.5.0"),sQuery(id+"F0.wireOp",EDGE,"E2.51.6.0"),sQuery(id+"F0.wireOp",EDGE,"E2.51.7.0"),sQuery(id+"F0.wireOp",EDGE,"E2.51.8.0"),sQuery(id+"F0.wireOp",EDGE,"E2.51.9.0"),sQuery(id+"F0.wireOp",EDGE,"E2.51.10.0"),sQuery(id+"F0.wireOp",EDGE,"E2.51.11.0"),sQuery(id+"F0.wireOp",EDGE,"E2.51.12.0"),sQuery(id+"F0.wireOp",EDGE,"E2.51.13.0"),sQuery(id+"F0.wireOp",EDGE,"E2.51.14.0"),sQuery(id+"F0.wireOp",EDGE,"E2.51.15.0"),sQuery(id+"F0.wireOp",EDGE,"E2.51.16.0"),sQuery(id+"F0.wireOp",EDGE,"E2.51.17.0"),sQuery(id+"F0.wireOp",EDGE,"E2.51.18.0"),sQuery(id+"F0.wireOp",EDGE,"E2.51.19.0"),sQuery(id+"F0.wireOp",EDGE,"E2.51.20.0"),sQuery(id+"F0.wireOp",EDGE,"E2.51.21.0"),sQuery(id+"F0.wireOp",EDGE,"E2.51.22.0"),sQuery(id+"F0.wireOp",EDGE,"E2.51.23.0"),sQuery(id+"F0.wireOp",EDGE,"E2.51.24.0"),sQuery(id+"F0.wireOp",EDGE,"E2.51.25.0"),sQuery(id+"F0.wireOp",EDGE,"E2.51.26.0"),sQuery(id+"F0.wireOp",EDGE,"E2.51.27.0"),sQuery(id+"F0.wireOp",EDGE,"E2.51.28.0"),sQuery(id+"F0.wireOp",EDGE,"E2.51.29.0"),sQuery(id+"F0.wireOp",EDGE,"E2.51.30.0"),sQuery(id+"F0.wireOp",EDGE,"E2.51.31.0"),sQuery(id+"F0.wireOp",EDGE,"E2.51.32.0"),sQuery(id+"F0.wireOp",EDGE,"E2.51.33.0"),sQuery(id+"F0.wireOp",EDGE,"E2.51.34.0"),sQuery(id+"F0.wireOp",EDGE,"E2.51.35.0"),sQuery(id+"F0.wireOp",EDGE,"E2.51.36.0"),sQuery(id+"F0.wireOp",EDGE,"E2.51.37.0"),sQuery(id+"F0.wireOp",EDGE,"E2.51.38.0"),sQuery(id+"F0.wireOp",EDGE,"E2.51.39.0"),sQuery(id+"F0.wireOp",EDGE,"E2.51.40.0"),sQuery(id+"F0.wireOp",EDGE,"E2.51.41.0"),sQuery(id+"F0.wireOp",EDGE,"E2.51.42.0"),sQuery(id+"F0.wireOp",EDGE,"E2.51.43.0"),sQuery(id+"F0.wireOp",EDGE,"E2.51.44.0"),sQuery(id+"F0.wireOp",EDGE,"E2.51.45.0"),sQuery(id+"F0.wireOp",EDGE,"E2.51.46.0"),sQuery(id+"F0.wireOp",EDGE,"E2.51.47.0"),sQuery(id+"F0.wireOp",EDGE,"E2.51.48.0"),sQuery(id+"F0.wireOp",EDGE,"E2.51.49.0"),sQuery(id+"F0.wireOp",EDGE,"E2.52.0.0"),sQuery(id+"F0.wireOp",EDGE,"E2.52.1.0"),sQuery(id+"F0.wireOp",EDGE,"E2.52.2.0"),sQuery(id+"F0.wireOp",EDGE,"E2.52.3.0"),sQuery(id+"F0.wireOp",EDGE,"E2.52.4.0"),sQuery(id+"F0.wireOp",EDGE,"E2.52.5.0"),sQuery(id+"F0.wireOp",EDGE,"E2.52.6.0"),sQuery(id+"F0.wireOp",EDGE,"E2.52.7.0"),sQuery(id+"F0.wireOp",EDGE,"E2.52.8.0"),sQuery(id+"F0.wireOp",EDGE,"E2.52.9.0"),sQuery(id+"F0.wireOp",EDGE,"E2.52.10.0"),sQuery(id+"F0.wireOp",EDGE,"E2.52.11.0"),sQuery(id+"F0.wireOp",EDGE,"E2.52.12.0"),sQuery(id+"F0.wireOp",EDGE,"E2.52.13.0"),sQuery(id+"F0.wireOp",EDGE,"E2.52.14.0"),sQuery(id+"F0.wireOp",EDGE,"E2.52.15.0"),sQuery(id+"F0.wireOp",EDGE,"E2.52.16.0"),sQuery(id+"F0.wireOp",EDGE,"E2.52.17.0"),sQuery(id+"F0.wireOp",EDGE,"E2.52.18.0"),sQuery(id+"F0.wireOp",EDGE,"E2.52.19.0"),sQuery(id+"F0.wireOp",EDGE,"E2.52.20.0"),sQuery(id+"F0.wireOp",EDGE,"E2.52.21.0"),sQuery(id+"F0.wireOp",EDGE,"E2.52.22.0"),sQuery(id+"F0.wireOp",EDGE,"E2.52.23.0"),sQuery(id+"F0.wireOp",EDGE,"E2.52.24.0"),sQuery(id+"F0.wireOp",EDGE,"E2.52.25.0"),sQuery(id+"F0.wireOp",EDGE,"E2.52.26.0"),sQuery(id+"F0.wireOp",EDGE,"E2.52.27.0"),sQuery(id+"F0.wireOp",EDGE,"E2.52.28.0"),sQuery(id+"F0.wireOp",EDGE,"E2.52.29.0"),sQuery(id+"F0.wireOp",EDGE,"E2.52.30.0"),sQuery(id+"F0.wireOp",EDGE,"E2.52.31.0"),sQuery(id+"F0.wireOp",EDGE,"E2.52.32.0"),sQuery(id+"F0.wireOp",EDGE,"E2.52.33.0"),sQuery(id+"F0.wireOp",EDGE,"E2.52.34.0"),sQuery(id+"F0.wireOp",EDGE,"E2.52.35.0"),sQuery(id+"F0.wireOp",EDGE,"E2.52.36.0"),sQuery(id+"F0.wireOp",EDGE,"E2.52.37.0"),sQuery(id+"F0.wireOp",EDGE,"E2.52.38.0"),sQuery(id+"F0.wireOp",EDGE,"E2.52.39.0"),sQuery(id+"F0.wireOp",EDGE,"E2.52.40.0"),sQuery(id+"F0.wireOp",EDGE,"E2.52.41.0"),sQuery(id+"F0.wireOp",EDGE,"E2.52.42.0"),sQuery(id+"F0.wireOp",EDGE,"E2.52.43.0"),sQuery(id+"F0.wireOp",EDGE,"E2.52.44.0"),sQuery(id+"F0.wireOp",EDGE,"E2.52.45.0"),sQuery(id+"F0.wireOp",EDGE,"E2.52.46.0"),sQuery(id+"F0.wireOp",EDGE,"E2.52.47.0"),sQuery(id+"F0.wireOp",EDGE,"E2.52.48.0"),sQuery(id+"F0.wireOp",EDGE,"E2.52.49.0"),sQuery(id+"F0.wireOp",EDGE,"E2.53.0.0"),sQuery(id+"F0.wireOp",EDGE,"E2.53.1.0"),sQuery(id+"F0.wireOp",EDGE,"E2.53.2.0"),sQuery(id+"F0.wireOp",EDGE,"E2.53.3.0"),sQuery(id+"F0.wireOp",EDGE,"E2.53.4.0"),sQuery(id+"F0.wireOp",EDGE,"E2.53.5.0"),sQuery(id+"F0.wireOp",EDGE,"E2.53.6.0"),sQuery(id+"F0.wireOp",EDGE,"E2.53.7.0"),sQuery(id+"F0.wireOp",EDGE,"E2.53.8.0"),sQuery(id+"F0.wireOp",EDGE,"E2.53.9.0"),sQuery(id+"F0.wireOp",EDGE,"E2.53.10.0"),sQuery(id+"F0.wireOp",EDGE,"E2.53.11.0"),sQuery(id+"F0.wireOp",EDGE,"E2.53.12.0"),sQuery(id+"F0.wireOp",EDGE,"E2.53.13.0"),sQuery(id+"F0.wireOp",EDGE,"E2.53.14.0"),sQuery(id+"F0.wireOp",EDGE,"E2.53.15.0"),sQuery(id+"F0.wireOp",EDGE,"E2.53.16.0"),sQuery(id+"F0.wireOp",EDGE,"E2.53.17.0"),sQuery(id+"F0.wireOp",EDGE,"E2.53.18.0"),sQuery(id+"F0.wireOp",EDGE,"E2.53.19.0"),sQuery(id+"F0.wireOp",EDGE,"E2.53.20.0"),sQuery(id+"F0.wireOp",EDGE,"E2.53.21.0"),sQuery(id+"F0.wireOp",EDGE,"E2.53.22.0"),sQuery(id+"F0.wireOp",EDGE,"E2.53.23.0"),sQuery(id+"F0.wireOp",EDGE,"E2.53.24.0"),sQuery(id+"F0.wireOp",EDGE,"E2.53.25.0"),sQuery(id+"F0.wireOp",EDGE,"E2.53.26.0"),sQuery(id+"F0.wireOp",EDGE,"E2.53.27.0"),sQuery(id+"F0.wireOp",EDGE,"E2.53.28.0"),sQuery(id+"F0.wireOp",EDGE,"E2.53.29.0"),sQuery(id+"F0.wireOp",EDGE,"E2.53.30.0"),sQuery(id+"F0.wireOp",EDGE,"E2.53.31.0"),sQuery(id+"F0.wireOp",EDGE,"E2.53.32.0"),sQuery(id+"F0.wireOp",EDGE,"E2.53.33.0"),sQuery(id+"F0.wireOp",EDGE,"E2.53.34.0"),sQuery(id+"F0.wireOp",EDGE,"E2.53.35.0"),sQuery(id+"F0.wireOp",EDGE,"E2.53.36.0"),sQuery(id+"F0.wireOp",EDGE,"E2.53.37.0"),sQuery(id+"F0.wireOp",EDGE,"E2.53.38.0"),sQuery(id+"F0.wireOp",EDGE,"E2.53.39.0"),sQuery(id+"F0.wireOp",EDGE,"E2.53.40.0"),sQuery(id+"F0.wireOp",EDGE,"E2.53.41.0"),sQuery(id+"F0.wireOp",EDGE,"E2.53.42.0"),sQuery(id+"F0.wireOp",EDGE,"E2.53.43.0"),sQuery(id+"F0.wireOp",EDGE,"E2.53.44.0"),sQuery(id+"F0.wireOp",EDGE,"E2.53.45.0"),sQuery(id+"F0.wireOp",EDGE,"E2.53.46.0"),sQuery(id+"F0.wireOp",EDGE,"E2.53.47.0"),sQuery(id+"F0.wireOp",EDGE,"E2.53.48.0"),sQuery(id+"F0.wireOp",EDGE,"E2.53.49.0"),sQuery(id+"F0.wireOp",EDGE,"E2.54.0.0"),sQuery(id+"F0.wireOp",EDGE,"E2.54.1.0"),sQuery(id+"F0.wireOp",EDGE,"E2.54.2.0"),sQuery(id+"F0.wireOp",EDGE,"E2.54.3.0"),sQuery(id+"F0.wireOp",EDGE,"E2.54.4.0"),sQuery(id+"F0.wireOp",EDGE,"E2.54.5.0"),sQuery(id+"F0.wireOp",EDGE,"E2.54.6.0"),sQuery(id+"F0.wireOp",EDGE,"E2.54.7.0"),sQuery(id+"F0.wireOp",EDGE,"E2.54.8.0"),sQuery(id+"F0.wireOp",EDGE,"E2.54.9.0"),sQuery(id+"F0.wireOp",EDGE,"E2.54.10.0"),sQuery(id+"F0.wireOp",EDGE,"E2.54.11.0"),sQuery(id+"F0.wireOp",EDGE,"E2.54.12.0"),sQuery(id+"F0.wireOp",EDGE,"E2.54.13.0"),sQuery(id+"F0.wireOp",EDGE,"E2.54.14.0"),sQuery(id+"F0.wireOp",EDGE,"E2.54.15.0"),sQuery(id+"F0.wireOp",EDGE,"E2.54.16.0"),sQuery(id+"F0.wireOp",EDGE,"E2.54.17.0"),sQuery(id+"F0.wireOp",EDGE,"E2.54.18.0"),sQuery(id+"F0.wireOp",EDGE,"E2.54.19.0"),sQuery(id+"F0.wireOp",EDGE,"E2.54.20.0"),sQuery(id+"F0.wireOp",EDGE,"E2.54.21.0"),sQuery(id+"F0.wireOp",EDGE,"E2.54.22.0"),sQuery(id+"F0.wireOp",EDGE,"E2.54.23.0"),sQuery(id+"F0.wireOp",EDGE,"E2.54.24.0"),sQuery(id+"F0.wireOp",EDGE,"E2.54.25.0"),sQuery(id+"F0.wireOp",EDGE,"E2.54.26.0"),sQuery(id+"F0.wireOp",EDGE,"E2.54.27.0"),sQuery(id+"F0.wireOp",EDGE,"E2.54.28.0"),sQuery(id+"F0.wireOp",EDGE,"E2.54.29.0"),sQuery(id+"F0.wireOp",EDGE,"E2.54.30.0"),sQuery(id+"F0.wireOp",EDGE,"E2.54.31.0"),sQuery(id+"F0.wireOp",EDGE,"E2.54.32.0"),sQuery(id+"F0.wireOp",EDGE,"E2.54.33.0"),sQuery(id+"F0.wireOp",EDGE,"E2.54.34.0"),sQuery(id+"F0.wireOp",EDGE,"E2.54.35.0"),sQuery(id+"F0.wireOp",EDGE,"E2.54.36.0"),sQuery(id+"F0.wireOp",EDGE,"E2.54.37.0"),sQuery(id+"F0.wireOp",EDGE,"E2.54.38.0"),sQuery(id+"F0.wireOp",EDGE,"E2.54.39.0"),sQuery(id+"F0.wireOp",EDGE,"E2.54.40.0"),sQuery(id+"F0.wireOp",EDGE,"E2.54.41.0"),sQuery(id+"F0.wireOp",EDGE,"E2.54.42.0"),sQuery(id+"F0.wireOp",EDGE,"E2.54.43.0"),sQuery(id+"F0.wireOp",EDGE,"E2.54.44.0"),sQuery(id+"F0.wireOp",EDGE,"E2.54.45.0"),sQuery(id+"F0.wireOp",EDGE,"E2.54.46.0"),sQuery(id+"F0.wireOp",EDGE,"E2.54.47.0"),sQuery(id+"F0.wireOp",EDGE,"E2.54.48.0"),sQuery(id+"F0.wireOp",EDGE,"E2.54.49.0"),sQuery(id+"F0.wireOp",EDGE,"E2.55.0.0"),sQuery(id+"F0.wireOp",EDGE,"E2.55.1.0"),sQuery(id+"F0.wireOp",EDGE,"E2.55.2.0"),sQuery(id+"F0.wireOp",EDGE,"E2.55.3.0"),sQuery(id+"F0.wireOp",EDGE,"E2.55.4.0"),sQuery(id+"F0.wireOp",EDGE,"E2.55.5.0"),sQuery(id+"F0.wireOp",EDGE,"E2.55.6.0"),sQuery(id+"F0.wireOp",EDGE,"E2.55.7.0"),sQuery(id+"F0.wireOp",EDGE,"E2.55.8.0"),sQuery(id+"F0.wireOp",EDGE,"E2.55.9.0"),sQuery(id+"F0.wireOp",EDGE,"E2.55.10.0"),sQuery(id+"F0.wireOp",EDGE,"E2.55.11.0"),sQuery(id+"F0.wireOp",EDGE,"E2.55.12.0"),sQuery(id+"F0.wireOp",EDGE,"E2.55.13.0"),sQuery(id+"F0.wireOp",EDGE,"E2.55.14.0"),sQuery(id+"F0.wireOp",EDGE,"E2.55.15.0"),sQuery(id+"F0.wireOp",EDGE,"E2.55.16.0"),sQuery(id+"F0.wireOp",EDGE,"E2.55.17.0"),sQuery(id+"F0.wireOp",EDGE,"E2.55.18.0"),sQuery(id+"F0.wireOp",EDGE,"E2.55.19.0"),sQuery(id+"F0.wireOp",EDGE,"E2.55.20.0"),sQuery(id+"F0.wireOp",EDGE,"E2.55.21.0"),sQuery(id+"F0.wireOp",EDGE,"E2.55.22.0"),sQuery(id+"F0.wireOp",EDGE,"E2.55.23.0"),sQuery(id+"F0.wireOp",EDGE,"E2.55.24.0"),sQuery(id+"F0.wireOp",EDGE,"E2.55.25.0"),sQuery(id+"F0.wireOp",EDGE,"E2.55.26.0"),sQuery(id+"F0.wireOp",EDGE,"E2.55.27.0"),sQuery(id+"F0.wireOp",EDGE,"E2.55.28.0"),sQuery(id+"F0.wireOp",EDGE,"E2.55.29.0"),sQuery(id+"F0.wireOp",EDGE,"E2.55.30.0"),sQuery(id+"F0.wireOp",EDGE,"E2.55.31.0"),sQuery(id+"F0.wireOp",EDGE,"E2.55.32.0"),sQuery(id+"F0.wireOp",EDGE,"E2.55.33.0"),sQuery(id+"F0.wireOp",EDGE,"E2.55.34.0"),sQuery(id+"F0.wireOp",EDGE,"E2.55.35.0"),sQuery(id+"F0.wireOp",EDGE,"E2.55.36.0"),sQuery(id+"F0.wireOp",EDGE,"E2.55.37.0"),sQuery(id+"F0.wireOp",EDGE,"E2.55.38.0"),sQuery(id+"F0.wireOp",EDGE,"E2.55.39.0"),sQuery(id+"F0.wireOp",EDGE,"E2.55.40.0"),sQuery(id+"F0.wireOp",EDGE,"E2.55.41.0"),sQuery(id+"F0.wireOp",EDGE,"E2.55.42.0"),sQuery(id+"F0.wireOp",EDGE,"E2.55.43.0"),sQuery(id+"F0.wireOp",EDGE,"E2.55.44.0"),sQuery(id+"F0.wireOp",EDGE,"E2.55.45.0"),sQuery(id+"F0.wireOp",EDGE,"E2.55.46.0"),sQuery(id+"F0.wireOp",EDGE,"E2.55.47.0"),sQuery(id+"F0.wireOp",EDGE,"E2.55.48.0"),sQuery(id+"F0.wireOp",EDGE,"E2.55.49.0"),sQuery(id+"F0.wireOp",EDGE,"E2.56.0.0"),sQuery(id+"F0.wireOp",EDGE,"E2.56.1.0"),sQuery(id+"F0.wireOp",EDGE,"E2.56.2.0"),sQuery(id+"F0.wireOp",EDGE,"E2.56.3.0"),sQuery(id+"F0.wireOp",EDGE,"E2.56.4.0"),sQuery(id+"F0.wireOp",EDGE,"E2.56.5.0"),sQuery(id+"F0.wireOp",EDGE,"E2.56.6.0"),sQuery(id+"F0.wireOp",EDGE,"E2.56.7.0"),sQuery(id+"F0.wireOp",EDGE,"E2.56.8.0"),sQuery(id+"F0.wireOp",EDGE,"E2.56.9.0"),sQuery(id+"F0.wireOp",EDGE,"E2.56.10.0"),sQuery(id+"F0.wireOp",EDGE,"E2.56.11.0"),sQuery(id+"F0.wireOp",EDGE,"E2.56.12.0"),sQuery(id+"F0.wireOp",EDGE,"E2.56.13.0"),sQuery(id+"F0.wireOp",EDGE,"E2.56.14.0"),sQuery(id+"F0.wireOp",EDGE,"E2.56.15.0"),sQuery(id+"F0.wireOp",EDGE,"E2.56.16.0"),sQuery(id+"F0.wireOp",EDGE,"E2.56.17.0"),sQuery(id+"F0.wireOp",EDGE,"E2.56.18.0"),sQuery(id+"F0.wireOp",EDGE,"E2.56.19.0"),sQuery(id+"F0.wireOp",EDGE,"E2.56.20.0"),sQuery(id+"F0.wireOp",EDGE,"E2.56.21.0"),sQuery(id+"F0.wireOp",EDGE,"E2.56.22.0"),sQuery(id+"F0.wireOp",EDGE,"E2.56.23.0"),sQuery(id+"F0.wireOp",EDGE,"E2.56.24.0"),sQuery(id+"F0.wireOp",EDGE,"E2.56.25.0"),sQuery(id+"F0.wireOp",EDGE,"E2.56.26.0"),sQuery(id+"F0.wireOp",EDGE,"E2.56.27.0"),sQuery(id+"F0.wireOp",EDGE,"E2.56.28.0"),sQuery(id+"F0.wireOp",EDGE,"E2.56.29.0"),sQuery(id+"F0.wireOp",EDGE,"E2.56.30.0"),sQuery(id+"F0.wireOp",EDGE,"E2.56.31.0"),sQuery(id+"F0.wireOp",EDGE,"E2.56.32.0"),sQuery(id+"F0.wireOp",EDGE,"E2.56.33.0"),sQuery(id+"F0.wireOp",EDGE,"E2.56.34.0"),sQuery(id+"F0.wireOp",EDGE,"E2.56.35.0"),sQuery(id+"F0.wireOp",EDGE,"E2.56.36.0"),sQuery(id+"F0.wireOp",EDGE,"E2.56.37.0"),sQuery(id+"F0.wireOp",EDGE,"E2.56.38.0"),sQuery(id+"F0.wireOp",EDGE,"E2.56.39.0"),sQuery(id+"F0.wireOp",EDGE,"E2.56.40.0"),sQuery(id+"F0.wireOp",EDGE,"E2.56.41.0"),sQuery(id+"F0.wireOp",EDGE,"E2.56.42.0"),sQuery(id+"F0.wireOp",EDGE,"E2.56.43.0"),sQuery(id+"F0.wireOp",EDGE,"E2.56.44.0"),sQuery(id+"F0.wireOp",EDGE,"E2.56.45.0"),sQuery(id+"F0.wireOp",EDGE,"E2.56.46.0"),sQuery(id+"F0.wireOp",EDGE,"E2.56.47.0"),sQuery(id+"F0.wireOp",EDGE,"E2.56.48.0"),sQuery(id+"F0.wireOp",EDGE,"E2.56.49.0"),sQuery(id+"F0.wireOp",EDGE,"E2.57.0.0"),sQuery(id+"F0.wireOp",EDGE,"E2.57.1.0"),sQuery(id+"F0.wireOp",EDGE,"E2.57.2.0"),sQuery(id+"F0.wireOp",EDGE,"E2.57.3.0"),sQuery(id+"F0.wireOp",EDGE,"E2.57.4.0"),sQuery(id+"F0.wireOp",EDGE,"E2.57.5.0"),sQuery(id+"F0.wireOp",EDGE,"E2.57.6.0"),sQuery(id+"F0.wireOp",EDGE,"E2.57.7.0"),sQuery(id+"F0.wireOp",EDGE,"E2.57.8.0"),sQuery(id+"F0.wireOp",EDGE,"E2.57.9.0"),sQuery(id+"F0.wireOp",EDGE,"E2.57.10.0"),sQuery(id+"F0.wireOp",EDGE,"E2.57.11.0"),sQuery(id+"F0.wireOp",EDGE,"E2.57.12.0"),sQuery(id+"F0.wireOp",EDGE,"E2.57.13.0"),sQuery(id+"F0.wireOp",EDGE,"E2.57.14.0"),sQuery(id+"F0.wireOp",EDGE,"E2.57.15.0"),sQuery(id+"F0.wireOp",EDGE,"E2.57.16.0"),sQuery(id+"F0.wireOp",EDGE,"E2.57.17.0"),sQuery(id+"F0.wireOp",EDGE,"E2.57.18.0"),sQuery(id+"F0.wireOp",EDGE,"E2.57.19.0"),sQuery(id+"F0.wireOp",EDGE,"E2.57.20.0"),sQuery(id+"F0.wireOp",EDGE,"E2.57.21.0"),sQuery(id+"F0.wireOp",EDGE,"E2.57.22.0"),sQuery(id+"F0.wireOp",EDGE,"E2.57.23.0"),sQuery(id+"F0.wireOp",EDGE,"E2.57.24.0"),sQuery(id+"F0.wireOp",EDGE,"E2.57.25.0"),sQuery(id+"F0.wireOp",EDGE,"E2.57.26.0"),sQuery(id+"F0.wireOp",EDGE,"E2.57.27.0"),sQuery(id+"F0.wireOp",EDGE,"E2.57.28.0"),sQuery(id+"F0.wireOp",EDGE,"E2.57.29.0"),sQuery(id+"F0.wireOp",EDGE,"E2.57.30.0"),sQuery(id+"F0.wireOp",EDGE,"E2.57.31.0"),sQuery(id+"F0.wireOp",EDGE,"E2.57.32.0"),sQuery(id+"F0.wireOp",EDGE,"E2.57.33.0"),sQuery(id+"F0.wireOp",EDGE,"E2.57.34.0"),sQuery(id+"F0.wireOp",EDGE,"E2.57.35.0"),sQuery(id+"F0.wireOp",EDGE,"E2.57.36.0"),sQuery(id+"F0.wireOp",EDGE,"E2.57.37.0"),sQuery(id+"F0.wireOp",EDGE,"E2.57.38.0"),sQuery(id+"F0.wireOp",EDGE,"E2.57.39.0"),sQuery(id+"F0.wireOp",EDGE,"E2.57.40.0"),sQuery(id+"F0.wireOp",EDGE,"E2.57.41.0"),sQuery(id+"F0.wireOp",EDGE,"E2.57.42.0"),sQuery(id+"F0.wireOp",EDGE,"E2.57.43.0"),sQuery(id+"F0.wireOp",EDGE,"E2.57.44.0"),sQuery(id+"F0.wireOp",EDGE,"E2.57.45.0"),sQuery(id+"F0.wireOp",EDGE,"E2.57.46.0"),sQuery(id+"F0.wireOp",EDGE,"E2.57.47.0"),sQuery(id+"F0.wireOp",EDGE,"E2.57.48.0"),sQuery(id+"F0.wireOp",EDGE,"E2.57.49.0"),sQuery(id+"F0.wireOp",EDGE,"E2.58.0.0"),sQuery(id+"F0.wireOp",EDGE,"E2.58.1.0"),sQuery(id+"F0.wireOp",EDGE,"E2.58.2.0"),sQuery(id+"F0.wireOp",EDGE,"E2.58.3.0"),sQuery(id+"F0.wireOp",EDGE,"E2.58.4.0"),sQuery(id+"F0.wireOp",EDGE,"E2.58.5.0"),sQuery(id+"F0.wireOp",EDGE,"E2.58.6.0"),sQuery(id+"F0.wireOp",EDGE,"E2.58.7.0"),sQuery(id+"F0.wireOp",EDGE,"E2.58.8.0"),sQuery(id+"F0.wireOp",EDGE,"E2.58.9.0"),sQuery(id+"F0.wireOp",EDGE,"E2.58.10.0"),sQuery(id+"F0.wireOp",EDGE,"E2.58.11.0"),sQuery(id+"F0.wireOp",EDGE,"E2.58.12.0"),sQuery(id+"F0.wireOp",EDGE,"E2.58.13.0"),sQuery(id+"F0.wireOp",EDGE,"E2.58.14.0"),sQuery(id+"F0.wireOp",EDGE,"E2.58.15.0"),sQuery(id+"F0.wireOp",EDGE,"E2.58.16.0"),sQuery(id+"F0.wireOp",EDGE,"E2.58.17.0"),sQuery(id+"F0.wireOp",EDGE,"E2.58.18.0"),sQuery(id+"F0.wireOp",EDGE,"E2.58.19.0"),sQuery(id+"F0.wireOp",EDGE,"E2.58.20.0"),sQuery(id+"F0.wireOp",EDGE,"E2.58.21.0"),sQuery(id+"F0.wireOp",EDGE,"E2.58.22.0"),sQuery(id+"F0.wireOp",EDGE,"E2.58.23.0"),sQuery(id+"F0.wireOp",EDGE,"E2.58.24.0"),sQuery(id+"F0.wireOp",EDGE,"E2.58.25.0"),sQuery(id+"F0.wireOp",EDGE,"E2.58.26.0"),sQuery(id+"F0.wireOp",EDGE,"E2.58.27.0"),sQuery(id+"F0.wireOp",EDGE,"E2.58.28.0"),sQuery(id+"F0.wireOp",EDGE,"E2.58.29.0"),sQuery(id+"F0.wireOp",EDGE,"E2.58.30.0"),sQuery(id+"F0.wireOp",EDGE,"E2.58.31.0"),sQuery(id+"F0.wireOp",EDGE,"E2.58.32.0"),sQuery(id+"F0.wireOp",EDGE,"E2.58.33.0"),sQuery(id+"F0.wireOp",EDGE,"E2.58.34.0"),sQuery(id+"F0.wireOp",EDGE,"E2.58.35.0"),sQuery(id+"F0.wireOp",EDGE,"E2.58.36.0"),sQuery(id+"F0.wireOp",EDGE,"E2.58.37.0"),sQuery(id+"F0.wireOp",EDGE,"E2.58.38.0"),sQuery(id+"F0.wireOp",EDGE,"E2.58.39.0"),sQuery(id+"F0.wireOp",EDGE,"E2.58.40.0"),sQuery(id+"F0.wireOp",EDGE,"E2.58.41.0"),sQuery(id+"F0.wireOp",EDGE,"E2.58.42.0"),sQuery(id+"F0.wireOp",EDGE,"E2.58.43.0"),sQuery(id+"F0.wireOp",EDGE,"E2.58.44.0"),sQuery(id+"F0.wireOp",EDGE,"E2.58.45.0"),sQuery(id+"F0.wireOp",EDGE,"E2.58.46.0"),sQuery(id+"F0.wireOp",EDGE,"E2.58.47.0"),sQuery(id+"F0.wireOp",EDGE,"E2.58.48.0"),sQuery(id+"F0.wireOp",EDGE,"E2.58.49.0"),sQuery(id+"F0.wireOp",EDGE,"E2.59.0.0"),sQuery(id+"F0.wireOp",EDGE,"E2.59.1.0"),sQuery(id+"F0.wireOp",EDGE,"E2.59.2.0"),sQuery(id+"F0.wireOp",EDGE,"E2.59.3.0"),sQuery(id+"F0.wireOp",EDGE,"E2.59.4.0"),sQuery(id+"F0.wireOp",EDGE,"E2.59.5.0"),sQuery(id+"F0.wireOp",EDGE,"E2.59.6.0"),sQuery(id+"F0.wireOp",EDGE,"E2.59.7.0"),sQuery(id+"F0.wireOp",EDGE,"E2.59.8.0"),sQuery(id+"F0.wireOp",EDGE,"E2.59.9.0"),sQuery(id+"F0.wireOp",EDGE,"E2.59.10.0"),sQuery(id+"F0.wireOp",EDGE,"E2.59.11.0"),sQuery(id+"F0.wireOp",EDGE,"E2.59.12.0"),sQuery(id+"F0.wireOp",EDGE,"E2.59.13.0"),sQuery(id+"F0.wireOp",EDGE,"E2.59.14.0"),sQuery(id+"F0.wireOp",EDGE,"E2.59.15.0"),sQuery(id+"F0.wireOp",EDGE,"E2.59.16.0"),sQuery(id+"F0.wireOp",EDGE,"E2.59.17.0"),sQuery(id+"F0.wireOp",EDGE,"E2.59.18.0"),sQuery(id+"F0.wireOp",EDGE,"E2.59.19.0"),sQuery(id+"F0.wireOp",EDGE,"E2.59.20.0"),sQuery(id+"F0.wireOp",EDGE,"E2.59.21.0"),sQuery(id+"F0.wireOp",EDGE,"E2.59.22.0"),sQuery(id+"F0.wireOp",EDGE,"E2.59.23.0"),sQuery(id+"F0.wireOp",EDGE,"E2.59.24.0"),sQuery(id+"F0.wireOp",EDGE,"E2.59.25.0"),sQuery(id+"F0.wireOp",EDGE,"E2.59.26.0"),sQuery(id+"F0.wireOp",EDGE,"E2.59.27.0"),sQuery(id+"F0.wireOp",EDGE,"E2.59.28.0"),sQuery(id+"F0.wireOp",EDGE,"E2.59.29.0"),sQuery(id+"F0.wireOp",EDGE,"E2.59.30.0"),sQuery(id+"F0.wireOp",EDGE,"E2.59.31.0"),sQuery(id+"F0.wireOp",EDGE,"E2.59.32.0"),sQuery(id+"F0.wireOp",EDGE,"E2.59.33.0"),sQuery(id+"F0.wireOp",EDGE,"E2.59.34.0"),sQuery(id+"F0.wireOp",EDGE,"E2.59.35.0"),sQuery(id+"F0.wireOp",EDGE,"E2.59.36.0"),sQuery(id+"F0.wireOp",EDGE,"E2.59.37.0"),sQuery(id+"F0.wireOp",EDGE,"E2.59.38.0"),sQuery(id+"F0.wireOp",EDGE,"E2.59.39.0"),sQuery(id+"F0.wireOp",EDGE,"E2.59.40.0"),sQuery(id+"F0.wireOp",EDGE,"E2.59.41.0"),sQuery(id+"F0.wireOp",EDGE,"E2.59.42.0"),sQuery(id+"F0.wireOp",EDGE,"E2.59.43.0"),sQuery(id+"F0.wireOp",EDGE,"E2.59.44.0"),sQuery(id+"F0.wireOp",EDGE,"E2.59.45.0"),sQuery(id+"F0.wireOp",EDGE,"E2.59.46.0"),sQuery(id+"F0.wireOp",EDGE,"E2.59.47.0"),sQuery(id+"F0.wireOp",EDGE,"E2.59.48.0"),sQuery(id+"F0.wireOp",EDGE,"E2.59.49.0"),sQuery(id+"F0.wireOp",EDGE,"E3.0.60.0"),sQuery(id+"F0.wireOp",EDGE,"E3.0.60.1"),sQuery(id+"F0.wireOp",EDGE,"E3.0.60.2"),sQuery(id+"F0.wireOp",EDGE,"E3.0.60.3"),sQuery(id+"F0.wireOp",EDGE,"E3.0.60.4"),sQuery(id+"F0.wireOp",EDGE,"E3.0.60.5"),sQuery(id+"F0.wireOp",EDGE,"E3.0.60.6"),sQuery(id+"F0.wireOp",EDGE,"E3.0.60.7"),sQuery(id+"F0.wireOp",EDGE,"E3.0.60.8"),sQuery(id+"F0.wireOp",EDGE,"E3.0.60.9"),sQuery(id+"F0.wireOp",EDGE,"E3.0.60.10"),sQuery(id+"F0.wireOp",EDGE,"E3.0.60.11"),sQuery(id+"F0.wireOp",EDGE,"E3.0.60.12"),sQuery(id+"F0.wireOp",EDGE,"E3.0.60.13"),sQuery(id+"F0.wireOp",EDGE,"E3.0.60.14"),sQuery(id+"F0.wireOp",EDGE,"E3.0.60.15"),sQuery(id+"F0.wireOp",EDGE,"E3.0.60.16"),sQuery(id+"F0.wireOp",EDGE,"E3.0.60.17"),sQuery(id+"F0.wireOp",EDGE,"E3.0.60.18"),sQuery(id+"F0.wireOp",EDGE,"E3.0.60.19"),sQuery(id+"F0.wireOp",EDGE,"E3.0.60.20"),sQuery(id+"F0.wireOp",EDGE,"E3.0.60.21"),sQuery(id+"F0.wireOp",EDGE,"E3.0.60.22"),sQuery(id+"F0.wireOp",EDGE,"E3.0.60.23"),sQuery(id+"F0.wireOp",EDGE,"E3.0.60.24"),sQuery(id+"F0.wireOp",EDGE,"E3.0.60.25"),sQuery(id+"F0.wireOp",EDGE,"E3.0.60.26"),sQuery(id+"F0.wireOp",EDGE,"E3.0.60.27"),sQuery(id+"F0.wireOp",EDGE,"E3.0.60.28"),sQuery(id+"F0.wireOp",EDGE,"E3.0.60.29"),sQuery(id+"F0.wireOp",EDGE,"E3.0.60.30"),sQuery(id+"F0.wireOp",EDGE,"E3.0.60.31"),sQuery(id+"F0.wireOp",EDGE,"E3.0.60.32"),sQuery(id+"F0.wireOp",EDGE,"E3.0.60.33"),sQuery(id+"F0.wireOp",EDGE,"E3.0.60.34"),sQuery(id+"F0.wireOp",EDGE,"E3.0.60.35"),sQuery(id+"F0.wireOp",EDGE,"E3.0.60.36"),sQuery(id+"F0.wireOp",EDGE,"E3.0.60.37"),sQuery(id+"F0.wireOp",EDGE,"E3.0.60.38"),sQuery(id+"F0.wireOp",EDGE,"E3.0.60.39"),sQuery(id+"F0.wireOp",EDGE,"E3.0.60.40"),sQuery(id+"F0.wireOp",EDGE,"E3.0.60.41"),sQuery(id+"F0.wireOp",EDGE,"E3.0.60.42"),sQuery(id+"F0.wireOp",EDGE,"E3.0.60.43"),sQuery(id+"F0.wireOp",EDGE,"E3.0.60.44"),sQuery(id+"F0.wireOp",EDGE,"E3.0.60.45"),sQuery(id+"F0.wireOp",EDGE,"E3.0.60.46"),sQuery(id+"F0.wireOp",EDGE,"E3.0.60.47"),sQuery(id+"F0.wireOp",EDGE,"E3.0.60.48"),sQuery(id+"F0.wireOp",EDGE,"E3.0.60.49"),sQuery(id+"F0.wireOp",EDGE,"E3.0.61.0"),sQuery(id+"F0.wireOp",EDGE,"E3.0.61.1"),sQuery(id+"F0.wireOp",EDGE,"E3.0.61.2"),sQuery(id+"F0.wireOp",EDGE,"E3.0.61.3"),sQuery(id+"F0.wireOp",EDGE,"E3.0.61.4"),sQuery(id+"F0.wireOp",EDGE,"E3.0.61.5"),sQuery(id+"F0.wireOp",EDGE,"E3.0.61.6"),sQuery(id+"F0.wireOp",EDGE,"E3.0.61.7"),sQuery(id+"F0.wireOp",EDGE,"E3.0.61.8"),sQuery(id+"F0.wireOp",EDGE,"E3.0.61.9"),sQuery(id+"F0.wireOp",EDGE,"E3.0.61.10"),sQuery(id+"F0.wireOp",EDGE,"E3.0.61.11"),sQuery(id+"F0.wireOp",EDGE,"E3.0.61.12"),sQuery(id+"F0.wireOp",EDGE,"E3.0.61.13"),sQuery(id+"F0.wireOp",EDGE,"E3.0.61.14"),sQuery(id+"F0.wireOp",EDGE,"E3.0.61.15"),sQuery(id+"F0.wireOp",EDGE,"E3.0.61.16"),sQuery(id+"F0.wireOp",EDGE,"E3.0.61.17"),sQuery(id+"F0.wireOp",EDGE,"E3.0.61.18"),sQuery(id+"F0.wireOp",EDGE,"E3.0.61.19"),sQuery(id+"F0.wireOp",EDGE,"E3.0.61.20"),sQuery(id+"F0.wireOp",EDGE,"E3.0.61.21"),sQuery(id+"F0.wireOp",EDGE,"E3.0.61.22"),sQuery(id+"F0.wireOp",EDGE,"E3.0.61.23"),sQuery(id+"F0.wireOp",EDGE,"E3.0.61.24"),sQuery(id+"F0.wireOp",EDGE,"E3.0.61.25"),sQuery(id+"F0.wireOp",EDGE,"E3.0.61.26"),sQuery(id+"F0.wireOp",EDGE,"E3.0.61.27"),sQuery(id+"F0.wireOp",EDGE,"E3.0.61.28"),sQuery(id+"F0.wireOp",EDGE,"E3.0.61.29"),sQuery(id+"F0.wireOp",EDGE,"E3.0.61.30"),sQuery(id+"F0.wireOp",EDGE,"E3.0.61.31"),sQuery(id+"F0.wireOp",EDGE,"E3.0.61.32"),sQuery(id+"F0.wireOp",EDGE,"E3.0.61.33"),sQuery(id+"F0.wireOp",EDGE,"E3.0.61.34"),sQuery(id+"F0.wireOp",EDGE,"E3.0.61.35"),sQuery(id+"F0.wireOp",EDGE,"E3.0.61.36"),sQuery(id+"F0.wireOp",EDGE,"E3.0.61.37"),sQuery(id+"F0.wireOp",EDGE,"E3.0.61.38"),sQuery(id+"F0.wireOp",EDGE,"E3.0.61.39"),sQuery(id+"F0.wireOp",EDGE,"E3.0.61.40"),sQuery(id+"F0.wireOp",EDGE,"E3.0.61.41"),sQuery(id+"F0.wireOp",EDGE,"E3.0.61.42"),sQuery(id+"F0.wireOp",EDGE,"E3.0.61.43"),sQuery(id+"F0.wireOp",EDGE,"E3.0.61.44"),sQuery(id+"F0.wireOp",EDGE,"E3.0.61.45"),sQuery(id+"F0.wireOp",EDGE,"E3.0.61.46"),sQuery(id+"F0.wireOp",EDGE,"E3.0.61.47"),sQuery(id+"F0.wireOp",EDGE,"E3.0.61.48"),sQuery(id+"F0.wireOp",EDGE,"E3.0.61.49")])],"isStart":false});
            cPlane(context, id + "F2", {"entities" : qUnion([Q0]), "cplaneType" : CPlaneType.OFFSET, "offset" : 0 * mm, "width" : 150 * mm, "height" : 150 * mm});
        }
        {
            var Q0;
            Q0=qCreatedBy(id+"F2.planeOp",FACE);
            var sketch = newSketch(context, id + "F3", { "sketchPlane" : qUnion([Q0])});
            skLineSegment(sketch, "E4.bottom", {"start": v(250, -200) * mm, "end": v(-250, -200) * mm});
            skLineSegment(sketch, "E4.left", {"start": v(250, -200) * mm, "end": v(250, 200) * mm});
            skLineSegment(sketch, "E4.right", {"start": v(-250, -200) * mm, "end": v(-250, 200) * mm});
            skPoint(sketch, "E4.middle", {"position": v(0, 0) * mm});
            skLineSegment(sketch, "E5.bottom", {"start": v(-249, -199) * mm, "end": v(249, -199) * mm});
            skLineSegment(sketch, "E5.left", {"start": v(-249, -199) * mm, "end": v(-249, 199) * mm});
            skLineSegment(sketch, "E5.right", {"start": v(249, -199) * mm, "end": v(249, 199) * mm});
            skLineSegment(sketch, "E6", {"start": v(0, 291.64) * mm, "end": v(0, -255.6) * mm, "construction": true});
            skLineSegment(sketch, "E7", {"start": v(-318.82, 0) * mm, "end": v(365.99, 0) * mm, "construction": true});
            skPoint(sketch, "E8.orphan", {"position": v(47.2, 243.98) * mm});
            skPoint(sketch, "E9.end.orphan", {"position": v(-47.2, 243.98) * mm});
            skPoint(sketch, "E10.trimOffspring.start.orphan", {"position": v(-110, 200) * mm});
            skPoint(sketch, "E4.top.end.orphan", {"position": v(110, 200) * mm});
            skLineSegment(sketch, "E11", {"start": v(250, 200) * mm, "end": v(-250, 200) * mm});
            skLineSegment(sketch, "E12", {"start": v(-249, 199) * mm, "end": v(249, 199) * mm});
            skSolve(sketch);
        }
        {
            var Q0;
            Q0 = qSketchRegion(id + "F3", true);
            extrude(context, id + "F4", {"entities" : qUnion([Q0]), "operationType" : NewBodyOperationType.ADD, "depth" : 49 * mm, "offsetDistance" : 25 * mm});
        }
        {
            var Q0;
            {var subQ0=sQuery(id+"F3.wireOp",EDGE,"E9");var subQ1=sQuery(id+"F0.wireOp",EDGE,"E0.top");var subQ2=sQuery(id+"F3.wireOp",EDGE,"E4.top");var subQ3=sQuery(id+"F3.wireOp",EDGE,"E10.trimOffspring");var subQ4=sQuery(id+"F3.wireOp",EDGE,"cXP04Abe-EXwQ-TA72-M2dK-SMq0DXKuWj8R");var subQ5=sQuery(id+"F3.wireOp",EDGE,"FrtusRwv-sxAu-fFu7-EsI9-TysyP6uSNmlv");var subQ6=sQuery(id+"F3.wireOp",EDGE,"Hq1bn7TA-5jiC-Ugbu-fv48-WkOfcbb3Rfgt");var subQ7=sQuery(id+"F3.wireOp",EDGE,"adYGXRmT-cTTn-dbqB-Kn3C-ofxO4hpJ3Sf1");var subQ8=sQuery(id+"F3.wireOp",EDGE,"Ih6JNhac-Jw2e-IykQ-3Eoe-Sy21p7Us29C1");Q0=makeQuery(id+"F4.boolean.opBoolean","SPLIT",FACE,{"disambiguationData":[TD([makeQuery(id+"F1.opExtrude","SWEPT_FACE",FACE,{"disambiguationData":[OSD([subQ1])]})])],"derivedFrom":makeQuery(id+"F4.opExtrude","CAP_FACE",FACE,{"disambiguationData":[OSD([sQuery(id+"F3.wireOp",EDGE,"E4.bottom"),subQ2,sQuery(id+"F3.wireOp",EDGE,"E4.left"),sQuery(id+"F3.wireOp",EDGE,"E4.right"),sQuery(id+"F3.wireOp",EDGE,"E5.bottom"),sQuery(id+"F3.wireOp",EDGE,"E5.top"),sQuery(id+"F3.wireOp",EDGE,"E5.left"),sQuery(id+"F3.wireOp",EDGE,"E5.right"),subQ0,subQ4,subQ5,subQ6,subQ3,sQuery(id+"F3.wireOp",EDGE,"1b9e854d-0ea8-4f2e-8941-d81ae45ba924.trimOffspring"),subQ7,subQ8])],"isStart":true})});}
            var Q1;
            Q1=makeQuery(id+"F4.opExtrude","CAP_FACE",FACE,{"disambiguationData":[OSD([sQuery(id+"F3.wireOp",EDGE,"E4.bottom"),sQuery(id+"F3.wireOp",EDGE,"E4.left"),sQuery(id+"F3.wireOp",EDGE,"E4.right"),sQuery(id+"F3.wireOp",EDGE,"E5.bottom"),sQuery(id+"F3.wireOp",EDGE,"E5.left"),sQuery(id+"F3.wireOp",EDGE,"E5.right"),sQuery(id+"F3.wireOp",EDGE,"E11"),sQuery(id+"F3.wireOp",EDGE,"E12")])],"isStart":false});
            cPlane(context, id + "F5", {"entities" : qUnion([Q0, Q1]), "cplaneType" : CPlaneType.OFFSET, "offset" : 0 * mm, "width" : 150 * mm, "height" : 150 * mm});
        }
        {
            var Q0;
            Q0=qCreatedBy(id+"F5.planeOp",FACE);
            var sketch = newSketch(context, id + "F6", { "sketchPlane" : qUnion([Q0])});
            skLineSegment(sketch, "E13.bottom", {"start": v(250, -200) * mm, "end": v(-250, -200) * mm});
            skLineSegment(sketch, "E13.top", {"start": v(250, 200) * mm, "end": v(-250, 200) * mm});
            skLineSegment(sketch, "E13.left", {"start": v(250, -200) * mm, "end": v(250, 200) * mm});
            skLineSegment(sketch, "E13.right", {"start": v(-250, -200) * mm, "end": v(-250, 200) * mm});
            skPoint(sketch, "E13.middle", {"position": v(0, 0) * mm});
            skPoint(sketch, "E14.bottom.end.orphan", {"position": v(-249, -199) * mm});
            skPoint(sketch, "E14.left.start.orphan", {"position": v(249, -199) * mm});
            skPoint(sketch, "E14.top.end.orphan", {"position": v(-249, 199) * mm});
            skPoint(sketch, "E14.top.start.orphan", {"position": v(249, 199) * mm});
            skSolve(sketch);
        }
        {
            var Q0;
            Q0=makeQuery(id+"F6.imprint","IMPRINT",FACE,{"disambiguationData":[TD([[makeQuery(id+"F6.imprint","IMPRINT",EDGE,{"derivedFrom":sQuery(id+"F6.wireOp",EDGE,"E13.bottom")}),-1.0]])]});
            extrude(context, id + "F7", {"entities" : qUnion([Q0]), "operationType" : NewBodyOperationType.ADD, "depth" : 2 * mm, "offsetDistance" : 25 * mm});
        }
        {
            var Q0;
            Q0=makeQuery(id+"F7.boolean.opBoolean","MERGE",FACE,{"derivedFrom":[makeQuery(id+"F4.boolean.opBoolean","MERGE",FACE,{"derivedFrom":[makeQuery(id+"F1.opExtrude","SWEPT_FACE",FACE,{"disambiguationData":[OSD([sQuery(id+"F0.wireOp",EDGE,"E0.bottom")])]}),makeQuery(id+"F4.opExtrude","SWEPT_FACE",FACE,{"disambiguationData":[OSD([sQuery(id+"F3.wireOp",EDGE,"E4.bottom")])]})]}),makeQuery(id+"F7.opExtrude","SWEPT_FACE",FACE,{"disambiguationData":[OSD([sQuery(id+"F6.wireOp",EDGE,"E13.bottom")])]})]});
            cPlane(context, id + "F8", {"entities" : qUnion([Q0]), "cplaneType" : CPlaneType.OFFSET, "offset" : 0 * mm, "width" : 150 * mm, "height" : 150 * mm});
        }
        {
            var Q0;
            Q0=makeQuery(id+"F7.boolean.opBoolean","MERGE",FACE,{"derivedFrom":[makeQuery(id+"F4.boolean.opBoolean","MERGE",FACE,{"derivedFrom":[makeQuery(id+"F1.opExtrude","SWEPT_FACE",FACE,{"disambiguationData":[OSD([sQuery(id+"F0.wireOp",EDGE,"E0.bottom")])]}),makeQuery(id+"F4.opExtrude","SWEPT_FACE",FACE,{"disambiguationData":[OSD([sQuery(id+"F3.wireOp",EDGE,"E4.bottom")])]})]}),makeQuery(id+"F7.opExtrude","SWEPT_FACE",FACE,{"disambiguationData":[OSD([sQuery(id+"F6.wireOp",EDGE,"E13.bottom")])]})]});
            cPlane(context, id + "F9", {"entities" : qUnion([Q0]), "cplaneType" : CPlaneType.OFFSET, "offset" : 50 * mm, "width" : 150 * mm, "height" : 150 * mm});
        }
        {
            var Q0;
            Q0=qCreatedBy(id+"F8.planeOp",FACE);
            var sketch = newSketch(context, id + "F10", { "sketchPlane" : qUnion([Q0])});
            skLineSegment(sketch, "E15", {"start": v(-27.05, 26.5) * mm, "end": v(28.46, 26.5) * mm, "construction": true});
            skLineSegment(sketch, "E16", {"start": v(0, 38.38) * mm, "end": v(0, 15.64) * mm, "construction": true});
            skEllipse(sketch, "E17", {"center": v(0, 26.5) * mm, "majorRadius": 100 * mm, "minorRadius": 24 * mm, "majorAxis": v(-1, 0)});
            skSolve(sketch);
        }
        {
            var Q0;
            Q0=qCreatedBy(id+"F9.planeOp",FACE);
            var sketch = newSketch(context, id + "F11", { "sketchPlane" : qUnion([Q0])});
            skLineSegment(sketch, "E18", {"start": v(0, 45.3) * mm, "end": v(0, 10.83) * mm, "construction": true});
            skLineSegment(sketch, "E19", {"start": v(-17.18, 26.5) * mm, "end": v(30.07, 26.5) * mm, "construction": true});
            skCircle(sketch, "E20", {"center": v(0, 26.5) * mm, "radius": 75 * mm});
            skSolve(sketch);
        }
        {
            var Q0;
            Q0=qCreatedBy(id+"F9.planeOp",FACE);
            cPlane(context, id + "F12", {"entities" : qUnion([Q0]), "cplaneType" : CPlaneType.OFFSET, "offset" : 25 * mm, "width" : 150 * mm, "height" : 150 * mm});
        }
        {
            var Q0;
            Q0 = qSketchRegion(id + "F10", true);
            extrude(context, id + "F13", {"entities" : qUnion([Q0]), "operationType" : NewBodyOperationType.REMOVE, "oppositeDirection" : true, "depth" : 25 * mm, "offsetDistance" : 25 * mm});
        }
        {
            var Q0;
            Q0=qCreatedBy(id+"F12.planeOp",FACE);
            var sketch = newSketch(context, id + "F14", { "sketchPlane" : qUnion([Q0])});
            skLineSegment(sketch, "E21", {"start": v(-18.84, 26.5) * mm, "end": v(27.73, 26.5) * mm, "construction": true});
            skLineSegment(sketch, "E22", {"start": v(0, 54.86) * mm, "end": v(0, 0) * mm, "construction": true});
            skCircle(sketch, "E23", {"center": v(0, 26.5) * mm, "radius": 75 * mm});
            skSolve(sketch);
        }
        {
            var Q0;
            Q0=qCreatedBy(id+"F8.planeOp",FACE);
            var sketch = newSketch(context, id + "F15", { "sketchPlane" : qUnion([Q0])});
            skLineSegment(sketch, "E24", {"start": v(-12.2, 26.5) * mm, "end": v(17.43, 26.5) * mm, "construction": true});
            skLineSegment(sketch, "E25", {"start": v(0, 38.6) * mm, "end": v(0, 12.98) * mm, "construction": true});
            skEllipse(sketch, "E26", {"center": v(0, 26.5) * mm, "majorRadius": 100 * mm, "minorRadius": 24 * mm, "majorAxis": v(-1, 0)});
            skSolve(sketch);
        }
        {
            var Q0;
            Q0=makeQuery(id+"F15.imprint","IMPRINT",FACE,{"disambiguationData":[TD([[makeQuery(id+"F15.imprint","IMPRINT",EDGE,{"derivedFrom":sQuery(id+"F15.wireOp",EDGE,"E26")}),1.0]])]});
            var Q1;
            Q1=makeQuery(id+"F11.imprint","IMPRINT",FACE,{"disambiguationData":[TD([[makeQuery(id+"F11.imprint","IMPRINT",EDGE,{"derivedFrom":sQuery(id+"F11.wireOp",EDGE,"E20")}),1.0]])]});
            var Q2;
            Q2=makeQuery(id+"F14.imprint","IMPRINT",FACE,{"disambiguationData":[TD([[makeQuery(id+"F14.imprint","IMPRINT",EDGE,{"derivedFrom":sQuery(id+"F14.wireOp",EDGE,"E23")}),1.0]])]});
            loft(context, id + "F16", {"sheetProfilesArray" : [{ "sheetProfileEntities" : qUnion([Q0]) }, { "sheetProfileEntities" : qUnion([Q1]) }, { "sheetProfileEntities" : qUnion([Q2]) }]});
        }
        {
            var Q0;
            Q0=makeQuery(id+"F16.opLoft","CAP_FACE",FACE,{"disambiguationData":[OSD([makeQuery(id+"F14.imprint","IMPRINT",FACE,{"disambiguationData":[TD([[makeQuery(id+"F14.imprint","IMPRINT",EDGE,{"derivedFrom":sQuery(id+"F14.wireOp",EDGE,"E23")}),1.0]])]})])],"isStart":true});
            shell(context, id + "F17", {"entities" : qUnion([Q0]), "thickness" : 2.5 * mm});
        }
        {
            var Q0;
            Q0=makeQuery(id+"F17.opShell","OFFSET_FACE",FACE,{"disambiguationData":[OSD([makeQuery(id+"F15.imprint","IMPRINT",FACE,{"disambiguationData":[TD([[makeQuery(id+"F15.imprint","IMPRINT",EDGE,{"derivedFrom":sQuery(id+"F15.wireOp",EDGE,"E26")}),1.0]])]})])]});
            extrude(context, id + "F18", {"entities" : qUnion([Q0]), "operationType" : NewBodyOperationType.REMOVE, "oppositeDirection" : true, "depth" : 25 * mm, "offsetDistance" : 25 * mm});
        }
    });
